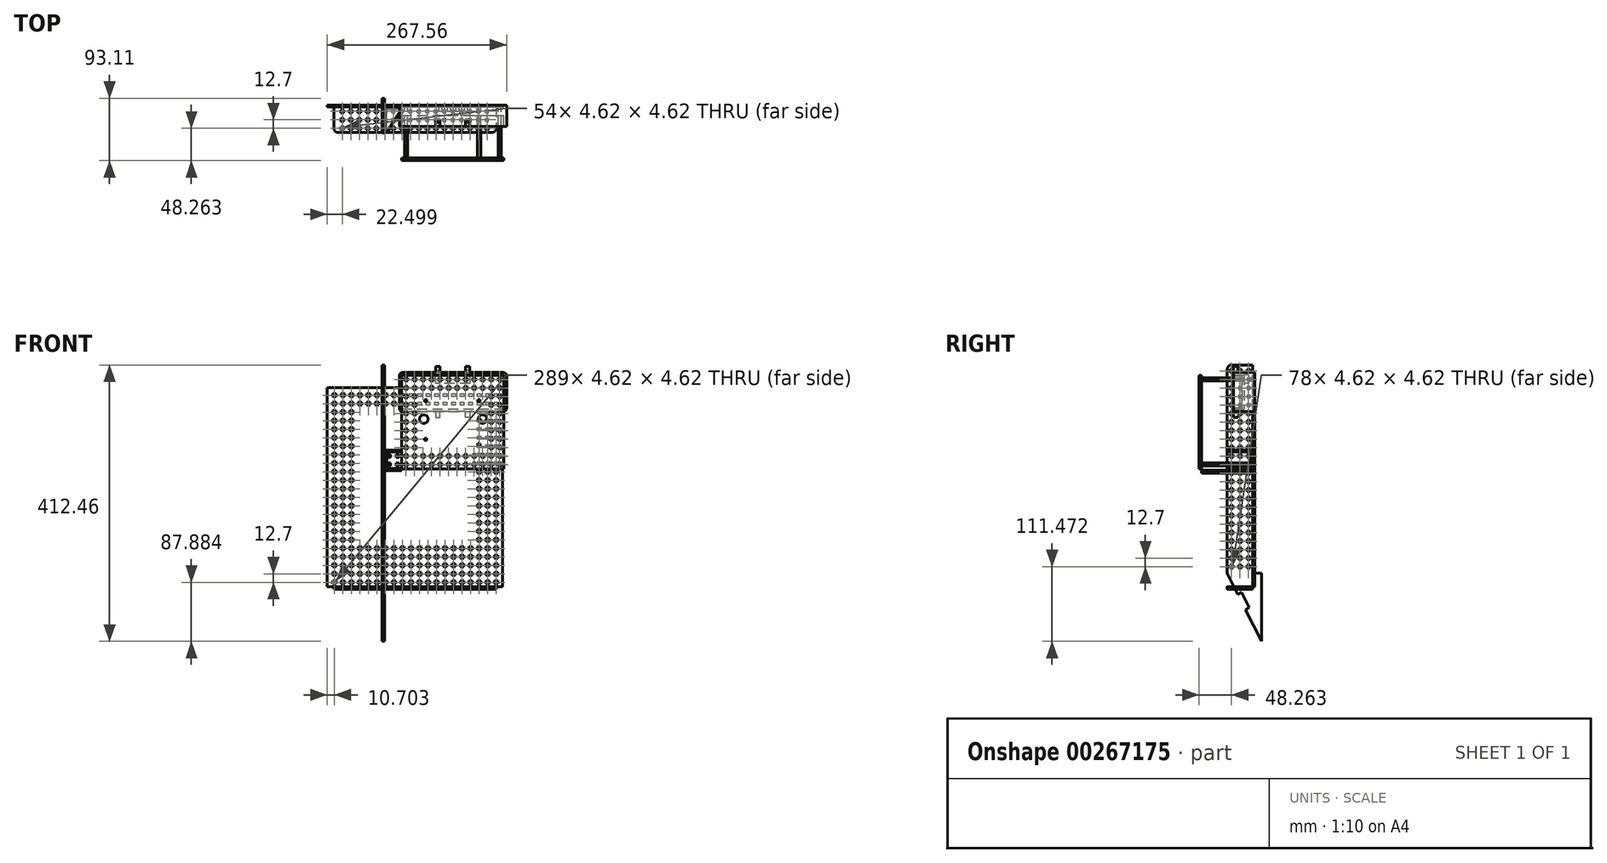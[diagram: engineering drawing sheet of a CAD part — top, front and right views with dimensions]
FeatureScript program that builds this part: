
annotation { "Feature Type Name" : "Feature", "Feature Type Description" : "" }
export const myFeature = defineFeature(function(context is Context, id is Id, definition is map)
    precondition{}
    {
        {
            var Q0;
            Q0=qCreatedBy(makeId("Front.planeOp"),FACE);
            var sketch = newSketch(context, id + "F0", { "sketchPlane" : qUnion([Q0])});
            skLineSegment(sketch, "E0.0.3.0", {"start": v(43.35, 107.94) * mm, "end": v(43.35, 112.57) * mm});
            skLineSegment(sketch, "E0.0.3.1", {"start": v(47.97, 107.94) * mm, "end": v(43.35, 107.94) * mm});
            skLineSegment(sketch, "E0.0.3.2", {"start": v(47.97, 112.57) * mm, "end": v(47.97, 107.94) * mm});
            skLineSegment(sketch, "E0.0.3.3", {"start": v(43.35, 112.57) * mm, "end": v(47.97, 112.57) * mm});
            skLineSegment(sketch, "E0.0.4.0", {"start": v(43.35, 95.24) * mm, "end": v(43.35, 99.87) * mm});
            skLineSegment(sketch, "E0.0.4.1", {"start": v(47.97, 95.24) * mm, "end": v(43.35, 95.24) * mm});
            skLineSegment(sketch, "E0.0.4.2", {"start": v(47.97, 99.87) * mm, "end": v(47.97, 95.24) * mm});
            skLineSegment(sketch, "E0.0.4.3", {"start": v(43.35, 99.87) * mm, "end": v(47.97, 99.87) * mm});
            skLineSegment(sketch, "E0.0.5.0", {"start": v(43.35, 82.54) * mm, "end": v(43.35, 87.17) * mm});
            skLineSegment(sketch, "E0.0.5.1", {"start": v(47.97, 82.54) * mm, "end": v(43.35, 82.54) * mm});
            skLineSegment(sketch, "E0.0.5.2", {"start": v(47.97, 87.17) * mm, "end": v(47.97, 82.54) * mm});
            skLineSegment(sketch, "E0.0.5.3", {"start": v(43.35, 87.17) * mm, "end": v(47.97, 87.17) * mm});
            skLineSegment(sketch, "E0.0.6.0", {"start": v(43.35, 69.84) * mm, "end": v(43.35, 74.47) * mm});
            skLineSegment(sketch, "E0.0.6.1", {"start": v(47.97, 69.84) * mm, "end": v(43.35, 69.84) * mm});
            skLineSegment(sketch, "E0.0.6.2", {"start": v(47.97, 74.47) * mm, "end": v(47.97, 69.84) * mm});
            skLineSegment(sketch, "E0.0.6.3", {"start": v(43.35, 74.47) * mm, "end": v(47.97, 74.47) * mm});
            skLineSegment(sketch, "E0.0.7.0", {"start": v(43.35, 57.14) * mm, "end": v(43.35, 61.77) * mm});
            skLineSegment(sketch, "E0.0.7.1", {"start": v(47.97, 57.14) * mm, "end": v(43.35, 57.14) * mm});
            skLineSegment(sketch, "E0.0.7.2", {"start": v(47.97, 61.77) * mm, "end": v(47.97, 57.14) * mm});
            skLineSegment(sketch, "E0.0.7.3", {"start": v(43.35, 61.77) * mm, "end": v(47.97, 61.77) * mm});
            skLineSegment(sketch, "E0.0.8.0", {"start": v(43.35, 44.44) * mm, "end": v(43.35, 49.07) * mm});
            skLineSegment(sketch, "E0.0.8.1", {"start": v(47.97, 44.44) * mm, "end": v(43.35, 44.44) * mm});
            skLineSegment(sketch, "E0.0.8.2", {"start": v(47.97, 49.07) * mm, "end": v(47.97, 44.44) * mm});
            skLineSegment(sketch, "E0.0.8.3", {"start": v(43.35, 49.07) * mm, "end": v(47.97, 49.07) * mm});
            skLineSegment(sketch, "E0.0.9.0", {"start": v(43.35, 31.74) * mm, "end": v(43.35, 36.37) * mm});
            skLineSegment(sketch, "E0.0.9.1", {"start": v(47.97, 31.74) * mm, "end": v(43.35, 31.74) * mm});
            skLineSegment(sketch, "E0.0.9.2", {"start": v(47.97, 36.37) * mm, "end": v(47.97, 31.74) * mm});
            skLineSegment(sketch, "E0.0.9.3", {"start": v(43.35, 36.37) * mm, "end": v(47.97, 36.37) * mm});
            skLineSegment(sketch, "E0.0.10.0", {"start": v(43.35, 19.04) * mm, "end": v(43.35, 23.67) * mm});
            skLineSegment(sketch, "E0.0.10.1", {"start": v(47.97, 19.04) * mm, "end": v(43.35, 19.04) * mm});
            skLineSegment(sketch, "E0.0.10.2", {"start": v(47.97, 23.67) * mm, "end": v(47.97, 19.04) * mm});
            skLineSegment(sketch, "E0.0.10.3", {"start": v(43.35, 23.67) * mm, "end": v(47.97, 23.67) * mm});
            skLineSegment(sketch, "E0.0.11.0", {"start": v(43.35, 6.34) * mm, "end": v(43.35, 10.97) * mm});
            skLineSegment(sketch, "E0.0.11.1", {"start": v(47.97, 6.34) * mm, "end": v(43.35, 6.34) * mm});
            skLineSegment(sketch, "E0.0.11.2", {"start": v(47.97, 10.97) * mm, "end": v(47.97, 6.34) * mm});
            skLineSegment(sketch, "E0.0.11.3", {"start": v(43.35, 10.97) * mm, "end": v(47.97, 10.97) * mm});
            skLineSegment(sketch, "E0.0.12.0", {"start": v(43.35, -6.36) * mm, "end": v(43.35, -1.73) * mm});
            skLineSegment(sketch, "E0.0.12.1", {"start": v(47.97, -6.36) * mm, "end": v(43.35, -6.36) * mm});
            skLineSegment(sketch, "E0.0.12.2", {"start": v(47.97, -1.73) * mm, "end": v(47.97, -6.36) * mm});
            skLineSegment(sketch, "E0.0.12.3", {"start": v(43.35, -1.73) * mm, "end": v(47.97, -1.73) * mm});
            skLineSegment(sketch, "E0.0.13.0", {"start": v(43.35, -19.06) * mm, "end": v(43.35, -14.43) * mm});
            skLineSegment(sketch, "E0.0.13.1", {"start": v(47.97, -19.06) * mm, "end": v(43.35, -19.06) * mm});
            skLineSegment(sketch, "E0.0.13.2", {"start": v(47.97, -14.43) * mm, "end": v(47.97, -19.06) * mm});
            skLineSegment(sketch, "E0.0.13.3", {"start": v(43.35, -14.43) * mm, "end": v(47.97, -14.43) * mm});
            skLineSegment(sketch, "E0.0.14.0", {"start": v(43.35, -31.76) * mm, "end": v(43.35, -27.13) * mm});
            skLineSegment(sketch, "E0.0.14.1", {"start": v(47.97, -31.76) * mm, "end": v(43.35, -31.76) * mm});
            skLineSegment(sketch, "E0.0.14.2", {"start": v(47.97, -27.13) * mm, "end": v(47.97, -31.76) * mm});
            skLineSegment(sketch, "E0.0.14.3", {"start": v(43.35, -27.13) * mm, "end": v(47.97, -27.13) * mm});
            skLineSegment(sketch, "E0.0.15.0", {"start": v(43.35, -44.46) * mm, "end": v(43.35, -39.83) * mm});
            skLineSegment(sketch, "E0.0.15.1", {"start": v(47.97, -44.46) * mm, "end": v(43.35, -44.46) * mm});
            skLineSegment(sketch, "E0.0.15.2", {"start": v(47.97, -39.83) * mm, "end": v(47.97, -44.46) * mm});
            skLineSegment(sketch, "E0.0.15.3", {"start": v(43.35, -39.83) * mm, "end": v(47.97, -39.83) * mm});
            skLineSegment(sketch, "E0.0.16.0", {"start": v(43.35, -57.16) * mm, "end": v(43.35, -52.53) * mm});
            skLineSegment(sketch, "E0.0.16.1", {"start": v(47.97, -57.16) * mm, "end": v(43.35, -57.16) * mm});
            skLineSegment(sketch, "E0.0.16.2", {"start": v(47.97, -52.53) * mm, "end": v(47.97, -57.16) * mm});
            skLineSegment(sketch, "E0.0.16.3", {"start": v(43.35, -52.53) * mm, "end": v(47.97, -52.53) * mm});
            skLineSegment(sketch, "E0.0.17.0", {"start": v(43.35, -69.86) * mm, "end": v(43.35, -65.23) * mm});
            skLineSegment(sketch, "E0.0.17.1", {"start": v(47.97, -69.86) * mm, "end": v(43.35, -69.86) * mm});
            skLineSegment(sketch, "E0.0.17.2", {"start": v(47.97, -65.23) * mm, "end": v(47.97, -69.86) * mm});
            skLineSegment(sketch, "E0.0.17.3", {"start": v(43.35, -65.23) * mm, "end": v(47.97, -65.23) * mm});
            skLineSegment(sketch, "E0.0.18.0", {"start": v(43.35, -82.56) * mm, "end": v(43.35, -77.93) * mm});
            skLineSegment(sketch, "E0.0.18.1", {"start": v(47.97, -82.56) * mm, "end": v(43.35, -82.56) * mm});
            skLineSegment(sketch, "E0.0.18.2", {"start": v(47.97, -77.93) * mm, "end": v(47.97, -82.56) * mm});
            skLineSegment(sketch, "E0.0.18.3", {"start": v(43.35, -77.93) * mm, "end": v(47.97, -77.93) * mm});
            skLineSegment(sketch, "E0.0.19.0", {"start": v(43.35, -95.26) * mm, "end": v(43.35, -90.63) * mm});
            skLineSegment(sketch, "E0.0.19.1", {"start": v(47.97, -95.26) * mm, "end": v(43.35, -95.26) * mm});
            skLineSegment(sketch, "E0.0.19.2", {"start": v(47.97, -90.63) * mm, "end": v(47.97, -95.26) * mm});
            skLineSegment(sketch, "E0.0.19.3", {"start": v(43.35, -90.63) * mm, "end": v(47.97, -90.63) * mm});
            skLineSegment(sketch, "E0.0.20.0", {"start": v(43.35, -107.96) * mm, "end": v(43.35, -103.33) * mm});
            skLineSegment(sketch, "E0.0.20.1", {"start": v(47.97, -107.96) * mm, "end": v(43.35, -107.96) * mm});
            skLineSegment(sketch, "E0.0.20.2", {"start": v(47.97, -103.33) * mm, "end": v(47.97, -107.96) * mm});
            skLineSegment(sketch, "E0.0.20.3", {"start": v(43.35, -103.33) * mm, "end": v(47.97, -103.33) * mm});
            skLineSegment(sketch, "E0.0.21.0", {"start": v(43.35, -120.66) * mm, "end": v(43.35, -116.03) * mm});
            skLineSegment(sketch, "E0.0.21.1", {"start": v(47.97, -120.66) * mm, "end": v(43.35, -120.66) * mm});
            skLineSegment(sketch, "E0.0.21.2", {"start": v(47.97, -116.03) * mm, "end": v(47.97, -120.66) * mm});
            skLineSegment(sketch, "E0.0.21.3", {"start": v(43.35, -116.03) * mm, "end": v(47.97, -116.03) * mm});
            skLineSegment(sketch, "E0.0.22.0", {"start": v(43.35, -133.36) * mm, "end": v(43.35, -128.73) * mm});
            skLineSegment(sketch, "E0.0.22.1", {"start": v(47.97, -133.36) * mm, "end": v(43.35, -133.36) * mm});
            skLineSegment(sketch, "E0.0.22.2", {"start": v(47.97, -128.73) * mm, "end": v(47.97, -133.36) * mm});
            skLineSegment(sketch, "E0.0.22.3", {"start": v(43.35, -128.73) * mm, "end": v(47.97, -128.73) * mm});
            skLineSegment(sketch, "E0.0.23.0", {"start": v(43.35, -146.06) * mm, "end": v(43.35, -141.43) * mm});
            skLineSegment(sketch, "E0.0.23.1", {"start": v(47.97, -146.06) * mm, "end": v(43.35, -146.06) * mm});
            skLineSegment(sketch, "E0.0.23.2", {"start": v(47.97, -141.43) * mm, "end": v(47.97, -146.06) * mm});
            skLineSegment(sketch, "E0.0.23.3", {"start": v(43.35, -141.43) * mm, "end": v(47.97, -141.43) * mm});
            skLineSegment(sketch, "E0.0.24.0", {"start": v(43.35, -158.76) * mm, "end": v(43.35, -154.13) * mm});
            skLineSegment(sketch, "E0.0.24.1", {"start": v(47.97, -158.76) * mm, "end": v(43.35, -158.76) * mm});
            skLineSegment(sketch, "E0.0.24.2", {"start": v(47.97, -154.13) * mm, "end": v(47.97, -158.76) * mm});
            skLineSegment(sketch, "E0.0.24.3", {"start": v(43.35, -154.13) * mm, "end": v(47.97, -154.13) * mm});
            skLineSegment(sketch, "E0.0.25.0", {"start": v(43.35, -171.46) * mm, "end": v(43.35, -166.83) * mm});
            skLineSegment(sketch, "E0.0.25.1", {"start": v(47.97, -171.46) * mm, "end": v(43.35, -171.46) * mm});
            skLineSegment(sketch, "E0.0.25.2", {"start": v(47.97, -166.83) * mm, "end": v(47.97, -171.46) * mm});
            skLineSegment(sketch, "E0.0.25.3", {"start": v(43.35, -166.83) * mm, "end": v(47.97, -166.83) * mm});
            skLineSegment(sketch, "E0.1.3.0", {"start": v(30.65, 107.94) * mm, "end": v(30.65, 112.57) * mm});
            skLineSegment(sketch, "E0.1.3.1", {"start": v(35.27, 107.94) * mm, "end": v(30.65, 107.94) * mm});
            skLineSegment(sketch, "E0.1.3.2", {"start": v(35.27, 112.57) * mm, "end": v(35.27, 107.94) * mm});
            skLineSegment(sketch, "E0.1.3.3", {"start": v(30.65, 112.57) * mm, "end": v(35.27, 112.57) * mm});
            skLineSegment(sketch, "E0.1.4.0", {"start": v(30.65, 95.24) * mm, "end": v(30.65, 99.87) * mm});
            skLineSegment(sketch, "E0.1.4.1", {"start": v(35.27, 95.24) * mm, "end": v(30.65, 95.24) * mm});
            skLineSegment(sketch, "E0.1.4.2", {"start": v(35.27, 99.87) * mm, "end": v(35.27, 95.24) * mm});
            skLineSegment(sketch, "E0.1.4.3", {"start": v(30.65, 99.87) * mm, "end": v(35.27, 99.87) * mm});
            skLineSegment(sketch, "E0.1.5.0", {"start": v(30.65, 82.54) * mm, "end": v(30.65, 87.17) * mm});
            skLineSegment(sketch, "E0.1.5.1", {"start": v(35.27, 82.54) * mm, "end": v(30.65, 82.54) * mm});
            skLineSegment(sketch, "E0.1.5.2", {"start": v(35.27, 87.17) * mm, "end": v(35.27, 82.54) * mm});
            skLineSegment(sketch, "E0.1.5.3", {"start": v(30.65, 87.17) * mm, "end": v(35.27, 87.17) * mm});
            skLineSegment(sketch, "E0.1.6.0", {"start": v(30.65, 69.84) * mm, "end": v(30.65, 74.47) * mm});
            skLineSegment(sketch, "E0.1.6.1", {"start": v(35.27, 69.84) * mm, "end": v(30.65, 69.84) * mm});
            skLineSegment(sketch, "E0.1.6.2", {"start": v(35.27, 74.47) * mm, "end": v(35.27, 69.84) * mm});
            skLineSegment(sketch, "E0.1.6.3", {"start": v(30.65, 74.47) * mm, "end": v(35.27, 74.47) * mm});
            skLineSegment(sketch, "E0.1.7.0", {"start": v(30.65, 57.14) * mm, "end": v(30.65, 61.77) * mm});
            skLineSegment(sketch, "E0.1.7.1", {"start": v(35.27, 57.14) * mm, "end": v(30.65, 57.14) * mm});
            skLineSegment(sketch, "E0.1.7.2", {"start": v(35.27, 61.77) * mm, "end": v(35.27, 57.14) * mm});
            skLineSegment(sketch, "E0.1.7.3", {"start": v(30.65, 61.77) * mm, "end": v(35.27, 61.77) * mm});
            skLineSegment(sketch, "E0.1.8.0", {"start": v(30.65, 44.44) * mm, "end": v(30.65, 49.07) * mm});
            skLineSegment(sketch, "E0.1.8.1", {"start": v(35.27, 44.44) * mm, "end": v(30.65, 44.44) * mm});
            skLineSegment(sketch, "E0.1.8.2", {"start": v(35.27, 49.07) * mm, "end": v(35.27, 44.44) * mm});
            skLineSegment(sketch, "E0.1.8.3", {"start": v(30.65, 49.07) * mm, "end": v(35.27, 49.07) * mm});
            skLineSegment(sketch, "E0.1.9.0", {"start": v(30.65, 31.74) * mm, "end": v(30.65, 36.37) * mm});
            skLineSegment(sketch, "E0.1.9.1", {"start": v(35.27, 31.74) * mm, "end": v(30.65, 31.74) * mm});
            skLineSegment(sketch, "E0.1.9.2", {"start": v(35.27, 36.37) * mm, "end": v(35.27, 31.74) * mm});
            skLineSegment(sketch, "E0.1.9.3", {"start": v(30.65, 36.37) * mm, "end": v(35.27, 36.37) * mm});
            skLineSegment(sketch, "E0.1.10.0", {"start": v(30.65, 19.04) * mm, "end": v(30.65, 23.67) * mm});
            skLineSegment(sketch, "E0.1.10.1", {"start": v(35.27, 19.04) * mm, "end": v(30.65, 19.04) * mm});
            skLineSegment(sketch, "E0.1.10.2", {"start": v(35.27, 23.67) * mm, "end": v(35.27, 19.04) * mm});
            skLineSegment(sketch, "E0.1.10.3", {"start": v(30.65, 23.67) * mm, "end": v(35.27, 23.67) * mm});
            skLineSegment(sketch, "E0.1.11.0", {"start": v(30.65, 6.34) * mm, "end": v(30.65, 10.97) * mm});
            skLineSegment(sketch, "E0.1.11.1", {"start": v(35.27, 6.34) * mm, "end": v(30.65, 6.34) * mm});
            skLineSegment(sketch, "E0.1.11.2", {"start": v(35.27, 10.97) * mm, "end": v(35.27, 6.34) * mm});
            skLineSegment(sketch, "E0.1.11.3", {"start": v(30.65, 10.97) * mm, "end": v(35.27, 10.97) * mm});
            skLineSegment(sketch, "E0.1.12.0", {"start": v(30.65, -6.36) * mm, "end": v(30.65, -1.73) * mm});
            skLineSegment(sketch, "E0.1.12.1", {"start": v(35.27, -6.36) * mm, "end": v(30.65, -6.36) * mm});
            skLineSegment(sketch, "E0.1.12.2", {"start": v(35.27, -1.73) * mm, "end": v(35.27, -6.36) * mm});
            skLineSegment(sketch, "E0.1.12.3", {"start": v(30.65, -1.73) * mm, "end": v(35.27, -1.73) * mm});
            skLineSegment(sketch, "E0.1.13.0", {"start": v(30.65, -19.06) * mm, "end": v(30.65, -14.43) * mm});
            skLineSegment(sketch, "E0.1.13.1", {"start": v(35.27, -19.06) * mm, "end": v(30.65, -19.06) * mm});
            skLineSegment(sketch, "E0.1.13.2", {"start": v(35.27, -14.43) * mm, "end": v(35.27, -19.06) * mm});
            skLineSegment(sketch, "E0.1.13.3", {"start": v(30.65, -14.43) * mm, "end": v(35.27, -14.43) * mm});
            skLineSegment(sketch, "E0.1.14.0", {"start": v(30.65, -31.76) * mm, "end": v(30.65, -27.13) * mm});
            skLineSegment(sketch, "E0.1.14.1", {"start": v(35.27, -31.76) * mm, "end": v(30.65, -31.76) * mm});
            skLineSegment(sketch, "E0.1.14.2", {"start": v(35.27, -27.13) * mm, "end": v(35.27, -31.76) * mm});
            skLineSegment(sketch, "E0.1.14.3", {"start": v(30.65, -27.13) * mm, "end": v(35.27, -27.13) * mm});
            skLineSegment(sketch, "E0.1.15.0", {"start": v(30.65, -44.46) * mm, "end": v(30.65, -39.83) * mm});
            skLineSegment(sketch, "E0.1.15.1", {"start": v(35.27, -44.46) * mm, "end": v(30.65, -44.46) * mm});
            skLineSegment(sketch, "E0.1.15.2", {"start": v(35.27, -39.83) * mm, "end": v(35.27, -44.46) * mm});
            skLineSegment(sketch, "E0.1.15.3", {"start": v(30.65, -39.83) * mm, "end": v(35.27, -39.83) * mm});
            skLineSegment(sketch, "E0.1.16.0", {"start": v(30.65, -57.16) * mm, "end": v(30.65, -52.53) * mm});
            skLineSegment(sketch, "E0.1.16.1", {"start": v(35.27, -57.16) * mm, "end": v(30.65, -57.16) * mm});
            skLineSegment(sketch, "E0.1.16.2", {"start": v(35.27, -52.53) * mm, "end": v(35.27, -57.16) * mm});
            skLineSegment(sketch, "E0.1.16.3", {"start": v(30.65, -52.53) * mm, "end": v(35.27, -52.53) * mm});
            skLineSegment(sketch, "E0.1.17.0", {"start": v(30.65, -69.86) * mm, "end": v(30.65, -65.23) * mm});
            skLineSegment(sketch, "E0.1.17.1", {"start": v(35.27, -69.86) * mm, "end": v(30.65, -69.86) * mm});
            skLineSegment(sketch, "E0.1.17.2", {"start": v(35.27, -65.23) * mm, "end": v(35.27, -69.86) * mm});
            skLineSegment(sketch, "E0.1.17.3", {"start": v(30.65, -65.23) * mm, "end": v(35.27, -65.23) * mm});
            skLineSegment(sketch, "E0.1.18.0", {"start": v(30.65, -82.56) * mm, "end": v(30.65, -77.93) * mm});
            skLineSegment(sketch, "E0.1.18.1", {"start": v(35.27, -82.56) * mm, "end": v(30.65, -82.56) * mm});
            skLineSegment(sketch, "E0.1.18.2", {"start": v(35.27, -77.93) * mm, "end": v(35.27, -82.56) * mm});
            skLineSegment(sketch, "E0.1.18.3", {"start": v(30.65, -77.93) * mm, "end": v(35.27, -77.93) * mm});
            skLineSegment(sketch, "E0.1.19.0", {"start": v(30.65, -95.26) * mm, "end": v(30.65, -90.63) * mm});
            skLineSegment(sketch, "E0.1.19.1", {"start": v(35.27, -95.26) * mm, "end": v(30.65, -95.26) * mm});
            skLineSegment(sketch, "E0.1.19.2", {"start": v(35.27, -90.63) * mm, "end": v(35.27, -95.26) * mm});
            skLineSegment(sketch, "E0.1.19.3", {"start": v(30.65, -90.63) * mm, "end": v(35.27, -90.63) * mm});
            skLineSegment(sketch, "E0.1.20.0", {"start": v(30.65, -107.96) * mm, "end": v(30.65, -103.33) * mm});
            skLineSegment(sketch, "E0.1.20.1", {"start": v(35.27, -107.96) * mm, "end": v(30.65, -107.96) * mm});
            skLineSegment(sketch, "E0.1.20.2", {"start": v(35.27, -103.33) * mm, "end": v(35.27, -107.96) * mm});
            skLineSegment(sketch, "E0.1.20.3", {"start": v(30.65, -103.33) * mm, "end": v(35.27, -103.33) * mm});
            skLineSegment(sketch, "E0.1.21.0", {"start": v(30.65, -120.66) * mm, "end": v(30.65, -116.03) * mm});
            skLineSegment(sketch, "E0.1.21.1", {"start": v(35.27, -120.66) * mm, "end": v(30.65, -120.66) * mm});
            skLineSegment(sketch, "E0.1.21.2", {"start": v(35.27, -116.03) * mm, "end": v(35.27, -120.66) * mm});
            skLineSegment(sketch, "E0.1.21.3", {"start": v(30.65, -116.03) * mm, "end": v(35.27, -116.03) * mm});
            skLineSegment(sketch, "E0.1.22.0", {"start": v(30.65, -133.36) * mm, "end": v(30.65, -128.73) * mm});
            skLineSegment(sketch, "E0.1.22.1", {"start": v(35.27, -133.36) * mm, "end": v(30.65, -133.36) * mm});
            skLineSegment(sketch, "E0.1.22.2", {"start": v(35.27, -128.73) * mm, "end": v(35.27, -133.36) * mm});
            skLineSegment(sketch, "E0.1.22.3", {"start": v(30.65, -128.73) * mm, "end": v(35.27, -128.73) * mm});
            skLineSegment(sketch, "E0.1.23.0", {"start": v(30.65, -146.06) * mm, "end": v(30.65, -141.43) * mm});
            skLineSegment(sketch, "E0.1.23.1", {"start": v(35.27, -146.06) * mm, "end": v(30.65, -146.06) * mm});
            skLineSegment(sketch, "E0.1.23.2", {"start": v(35.27, -141.43) * mm, "end": v(35.27, -146.06) * mm});
            skLineSegment(sketch, "E0.1.23.3", {"start": v(30.65, -141.43) * mm, "end": v(35.27, -141.43) * mm});
            skLineSegment(sketch, "E0.1.24.0", {"start": v(30.65, -158.76) * mm, "end": v(30.65, -154.13) * mm});
            skLineSegment(sketch, "E0.1.24.1", {"start": v(35.27, -158.76) * mm, "end": v(30.65, -158.76) * mm});
            skLineSegment(sketch, "E0.1.24.2", {"start": v(35.27, -154.13) * mm, "end": v(35.27, -158.76) * mm});
            skLineSegment(sketch, "E0.1.24.3", {"start": v(30.65, -154.13) * mm, "end": v(35.27, -154.13) * mm});
            skLineSegment(sketch, "E0.1.25.0", {"start": v(30.65, -171.46) * mm, "end": v(30.65, -166.83) * mm});
            skLineSegment(sketch, "E0.1.25.1", {"start": v(35.27, -171.46) * mm, "end": v(30.65, -171.46) * mm});
            skLineSegment(sketch, "E0.1.25.2", {"start": v(35.27, -166.83) * mm, "end": v(35.27, -171.46) * mm});
            skLineSegment(sketch, "E0.1.25.3", {"start": v(30.65, -166.83) * mm, "end": v(35.27, -166.83) * mm});
            skLineSegment(sketch, "E0.2.3.0", {"start": v(17.95, 107.94) * mm, "end": v(17.95, 112.57) * mm});
            skLineSegment(sketch, "E0.2.3.1", {"start": v(22.57, 107.94) * mm, "end": v(17.95, 107.94) * mm});
            skLineSegment(sketch, "E0.2.3.2", {"start": v(22.57, 112.57) * mm, "end": v(22.57, 107.94) * mm});
            skLineSegment(sketch, "E0.2.3.3", {"start": v(17.95, 112.57) * mm, "end": v(22.57, 112.57) * mm});
            skLineSegment(sketch, "E0.2.4.0", {"start": v(17.95, 95.24) * mm, "end": v(17.95, 99.87) * mm});
            skLineSegment(sketch, "E0.2.4.1", {"start": v(22.57, 95.24) * mm, "end": v(17.95, 95.24) * mm});
            skLineSegment(sketch, "E0.2.4.2", {"start": v(22.57, 99.87) * mm, "end": v(22.57, 95.24) * mm});
            skLineSegment(sketch, "E0.2.4.3", {"start": v(17.95, 99.87) * mm, "end": v(22.57, 99.87) * mm});
            skLineSegment(sketch, "E0.2.5.0", {"start": v(17.95, 82.54) * mm, "end": v(17.95, 87.17) * mm});
            skLineSegment(sketch, "E0.2.5.1", {"start": v(22.57, 82.54) * mm, "end": v(17.95, 82.54) * mm});
            skLineSegment(sketch, "E0.2.5.2", {"start": v(22.57, 87.17) * mm, "end": v(22.57, 82.54) * mm});
            skLineSegment(sketch, "E0.2.5.3", {"start": v(17.95, 87.17) * mm, "end": v(22.57, 87.17) * mm});
            skLineSegment(sketch, "E0.2.6.0", {"start": v(17.95, 69.84) * mm, "end": v(17.95, 74.47) * mm});
            skLineSegment(sketch, "E0.2.6.1", {"start": v(22.57, 69.84) * mm, "end": v(17.95, 69.84) * mm});
            skLineSegment(sketch, "E0.2.6.2", {"start": v(22.57, 74.47) * mm, "end": v(22.57, 69.84) * mm});
            skLineSegment(sketch, "E0.2.6.3", {"start": v(17.95, 74.47) * mm, "end": v(22.57, 74.47) * mm});
            skLineSegment(sketch, "E0.2.7.0", {"start": v(17.95, 57.14) * mm, "end": v(17.95, 61.77) * mm});
            skLineSegment(sketch, "E0.2.7.1", {"start": v(22.57, 57.14) * mm, "end": v(17.95, 57.14) * mm});
            skLineSegment(sketch, "E0.2.7.2", {"start": v(22.57, 61.77) * mm, "end": v(22.57, 57.14) * mm});
            skLineSegment(sketch, "E0.2.7.3", {"start": v(17.95, 61.77) * mm, "end": v(22.57, 61.77) * mm});
            skLineSegment(sketch, "E0.2.8.0", {"start": v(17.95, 44.44) * mm, "end": v(17.95, 49.07) * mm});
            skLineSegment(sketch, "E0.2.8.1", {"start": v(22.57, 44.44) * mm, "end": v(17.95, 44.44) * mm});
            skLineSegment(sketch, "E0.2.8.2", {"start": v(22.57, 49.07) * mm, "end": v(22.57, 44.44) * mm});
            skLineSegment(sketch, "E0.2.8.3", {"start": v(17.95, 49.07) * mm, "end": v(22.57, 49.07) * mm});
            skLineSegment(sketch, "E0.2.9.0", {"start": v(17.95, 31.74) * mm, "end": v(17.95, 36.37) * mm});
            skLineSegment(sketch, "E0.2.9.1", {"start": v(22.57, 31.74) * mm, "end": v(17.95, 31.74) * mm});
            skLineSegment(sketch, "E0.2.9.2", {"start": v(22.57, 36.37) * mm, "end": v(22.57, 31.74) * mm});
            skLineSegment(sketch, "E0.2.9.3", {"start": v(17.95, 36.37) * mm, "end": v(22.57, 36.37) * mm});
            skLineSegment(sketch, "E0.2.10.0", {"start": v(17.95, 19.04) * mm, "end": v(17.95, 23.67) * mm});
            skLineSegment(sketch, "E0.2.10.1", {"start": v(22.57, 19.04) * mm, "end": v(17.95, 19.04) * mm});
            skLineSegment(sketch, "E0.2.10.2", {"start": v(22.57, 23.67) * mm, "end": v(22.57, 19.04) * mm});
            skLineSegment(sketch, "E0.2.10.3", {"start": v(17.95, 23.67) * mm, "end": v(22.57, 23.67) * mm});
            skLineSegment(sketch, "E0.2.11.0", {"start": v(17.95, 6.34) * mm, "end": v(17.95, 10.97) * mm});
            skLineSegment(sketch, "E0.2.11.1", {"start": v(22.57, 6.34) * mm, "end": v(17.95, 6.34) * mm});
            skLineSegment(sketch, "E0.2.11.2", {"start": v(22.57, 10.97) * mm, "end": v(22.57, 6.34) * mm});
            skLineSegment(sketch, "E0.2.11.3", {"start": v(17.95, 10.97) * mm, "end": v(22.57, 10.97) * mm});
            skLineSegment(sketch, "E0.2.12.0", {"start": v(17.95, -6.36) * mm, "end": v(17.95, -1.73) * mm});
            skLineSegment(sketch, "E0.2.12.1", {"start": v(22.57, -6.36) * mm, "end": v(17.95, -6.36) * mm});
            skLineSegment(sketch, "E0.2.12.2", {"start": v(22.57, -1.73) * mm, "end": v(22.57, -6.36) * mm});
            skLineSegment(sketch, "E0.2.12.3", {"start": v(17.95, -1.73) * mm, "end": v(22.57, -1.73) * mm});
            skLineSegment(sketch, "E0.2.13.0", {"start": v(17.95, -19.06) * mm, "end": v(17.95, -14.43) * mm});
            skLineSegment(sketch, "E0.2.13.1", {"start": v(22.57, -19.06) * mm, "end": v(17.95, -19.06) * mm});
            skLineSegment(sketch, "E0.2.13.2", {"start": v(22.57, -14.43) * mm, "end": v(22.57, -19.06) * mm});
            skLineSegment(sketch, "E0.2.13.3", {"start": v(17.95, -14.43) * mm, "end": v(22.57, -14.43) * mm});
            skLineSegment(sketch, "E0.2.14.0", {"start": v(17.95, -31.76) * mm, "end": v(17.95, -27.13) * mm});
            skLineSegment(sketch, "E0.2.14.1", {"start": v(22.57, -31.76) * mm, "end": v(17.95, -31.76) * mm});
            skLineSegment(sketch, "E0.2.14.2", {"start": v(22.57, -27.13) * mm, "end": v(22.57, -31.76) * mm});
            skLineSegment(sketch, "E0.2.14.3", {"start": v(17.95, -27.13) * mm, "end": v(22.57, -27.13) * mm});
            skLineSegment(sketch, "E0.2.15.0", {"start": v(17.95, -44.46) * mm, "end": v(17.95, -39.83) * mm});
            skLineSegment(sketch, "E0.2.15.1", {"start": v(22.57, -44.46) * mm, "end": v(17.95, -44.46) * mm});
            skLineSegment(sketch, "E0.2.15.2", {"start": v(22.57, -39.83) * mm, "end": v(22.57, -44.46) * mm});
            skLineSegment(sketch, "E0.2.15.3", {"start": v(17.95, -39.83) * mm, "end": v(22.57, -39.83) * mm});
            skLineSegment(sketch, "E0.2.16.0", {"start": v(17.95, -57.16) * mm, "end": v(17.95, -52.53) * mm});
            skLineSegment(sketch, "E0.2.16.1", {"start": v(22.57, -57.16) * mm, "end": v(17.95, -57.16) * mm});
            skLineSegment(sketch, "E0.2.16.2", {"start": v(22.57, -52.53) * mm, "end": v(22.57, -57.16) * mm});
            skLineSegment(sketch, "E0.2.16.3", {"start": v(17.95, -52.53) * mm, "end": v(22.57, -52.53) * mm});
            skLineSegment(sketch, "E0.2.17.0", {"start": v(17.95, -69.86) * mm, "end": v(17.95, -65.23) * mm});
            skLineSegment(sketch, "E0.2.17.1", {"start": v(22.57, -69.86) * mm, "end": v(17.95, -69.86) * mm});
            skLineSegment(sketch, "E0.2.17.2", {"start": v(22.57, -65.23) * mm, "end": v(22.57, -69.86) * mm});
            skLineSegment(sketch, "E0.2.17.3", {"start": v(17.95, -65.23) * mm, "end": v(22.57, -65.23) * mm});
            skLineSegment(sketch, "E0.2.18.0", {"start": v(17.95, -82.56) * mm, "end": v(17.95, -77.93) * mm});
            skLineSegment(sketch, "E0.2.18.1", {"start": v(22.57, -82.56) * mm, "end": v(17.95, -82.56) * mm});
            skLineSegment(sketch, "E0.2.18.2", {"start": v(22.57, -77.93) * mm, "end": v(22.57, -82.56) * mm});
            skLineSegment(sketch, "E0.2.18.3", {"start": v(17.95, -77.93) * mm, "end": v(22.57, -77.93) * mm});
            skLineSegment(sketch, "E0.2.19.0", {"start": v(17.95, -95.26) * mm, "end": v(17.95, -90.63) * mm});
            skLineSegment(sketch, "E0.2.19.1", {"start": v(22.57, -95.26) * mm, "end": v(17.95, -95.26) * mm});
            skLineSegment(sketch, "E0.2.19.2", {"start": v(22.57, -90.63) * mm, "end": v(22.57, -95.26) * mm});
            skLineSegment(sketch, "E0.2.19.3", {"start": v(17.95, -90.63) * mm, "end": v(22.57, -90.63) * mm});
            skLineSegment(sketch, "E0.2.20.0", {"start": v(17.95, -107.96) * mm, "end": v(17.95, -103.33) * mm});
            skLineSegment(sketch, "E0.2.20.1", {"start": v(22.57, -107.96) * mm, "end": v(17.95, -107.96) * mm});
            skLineSegment(sketch, "E0.2.20.2", {"start": v(22.57, -103.33) * mm, "end": v(22.57, -107.96) * mm});
            skLineSegment(sketch, "E0.2.20.3", {"start": v(17.95, -103.33) * mm, "end": v(22.57, -103.33) * mm});
            skLineSegment(sketch, "E0.2.21.0", {"start": v(17.95, -120.66) * mm, "end": v(17.95, -116.03) * mm});
            skLineSegment(sketch, "E0.2.21.1", {"start": v(22.57, -120.66) * mm, "end": v(17.95, -120.66) * mm});
            skLineSegment(sketch, "E0.2.21.2", {"start": v(22.57, -116.03) * mm, "end": v(22.57, -120.66) * mm});
            skLineSegment(sketch, "E0.2.21.3", {"start": v(17.95, -116.03) * mm, "end": v(22.57, -116.03) * mm});
            skLineSegment(sketch, "E0.2.22.0", {"start": v(17.95, -133.36) * mm, "end": v(17.95, -128.73) * mm});
            skLineSegment(sketch, "E0.2.22.1", {"start": v(22.57, -133.36) * mm, "end": v(17.95, -133.36) * mm});
            skLineSegment(sketch, "E0.2.22.2", {"start": v(22.57, -128.73) * mm, "end": v(22.57, -133.36) * mm});
            skLineSegment(sketch, "E0.2.22.3", {"start": v(17.95, -128.73) * mm, "end": v(22.57, -128.73) * mm});
            skLineSegment(sketch, "E0.2.23.0", {"start": v(17.95, -146.06) * mm, "end": v(17.95, -141.43) * mm});
            skLineSegment(sketch, "E0.2.23.1", {"start": v(22.57, -146.06) * mm, "end": v(17.95, -146.06) * mm});
            skLineSegment(sketch, "E0.2.23.2", {"start": v(22.57, -141.43) * mm, "end": v(22.57, -146.06) * mm});
            skLineSegment(sketch, "E0.2.23.3", {"start": v(17.95, -141.43) * mm, "end": v(22.57, -141.43) * mm});
            skLineSegment(sketch, "E0.2.24.0", {"start": v(17.95, -158.76) * mm, "end": v(17.95, -154.13) * mm});
            skLineSegment(sketch, "E0.2.24.1", {"start": v(22.57, -158.76) * mm, "end": v(17.95, -158.76) * mm});
            skLineSegment(sketch, "E0.2.24.2", {"start": v(22.57, -154.13) * mm, "end": v(22.57, -158.76) * mm});
            skLineSegment(sketch, "E0.2.24.3", {"start": v(17.95, -154.13) * mm, "end": v(22.57, -154.13) * mm});
            skLineSegment(sketch, "E0.2.25.0", {"start": v(17.95, -171.46) * mm, "end": v(17.95, -166.83) * mm});
            skLineSegment(sketch, "E0.2.25.1", {"start": v(22.57, -171.46) * mm, "end": v(17.95, -171.46) * mm});
            skLineSegment(sketch, "E0.2.25.2", {"start": v(22.57, -166.83) * mm, "end": v(22.57, -171.46) * mm});
            skLineSegment(sketch, "E0.2.25.3", {"start": v(17.95, -166.83) * mm, "end": v(22.57, -166.83) * mm});
            skLineSegment(sketch, "E1", {"start": v(-196.31, -175.5) * mm, "end": v(45.66, -175.5) * mm});
            skLineSegment(sketch, "E2.0.1.0", {"start": v(-167.93, 112.57) * mm, "end": v(-167.93, 107.94) * mm});
            skLineSegment(sketch, "E2.0.1.1", {"start": v(-172.55, 112.57) * mm, "end": v(-167.93, 112.57) * mm});
            skLineSegment(sketch, "E2.0.1.2", {"start": v(-172.55, 107.94) * mm, "end": v(-172.55, 112.57) * mm});
            skLineSegment(sketch, "E2.0.1.3", {"start": v(-167.93, 107.94) * mm, "end": v(-172.55, 107.94) * mm});
            skLineSegment(sketch, "E2.0.1.4", {"start": v(-180.63, 112.57) * mm, "end": v(-180.63, 107.94) * mm});
            skLineSegment(sketch, "E2.0.1.5", {"start": v(-185.25, 112.57) * mm, "end": v(-180.63, 112.57) * mm});
            skLineSegment(sketch, "E2.0.1.6", {"start": v(-180.63, 107.94) * mm, "end": v(-185.25, 107.94) * mm});
            skLineSegment(sketch, "E2.0.1.7", {"start": v(-185.25, 107.94) * mm, "end": v(-185.25, 112.57) * mm});
            skLineSegment(sketch, "E2.0.1.8", {"start": v(-193.33, 112.57) * mm, "end": v(-193.33, 107.94) * mm});
            skLineSegment(sketch, "E2.0.1.9", {"start": v(-197.95, 112.57) * mm, "end": v(-193.33, 112.57) * mm});
            skLineSegment(sketch, "E2.0.1.10", {"start": v(-197.95, 107.94) * mm, "end": v(-197.95, 112.57) * mm});
            skLineSegment(sketch, "E2.0.1.11", {"start": v(-193.33, 107.94) * mm, "end": v(-197.95, 107.94) * mm});
            skLineSegment(sketch, "E2.0.2.0", {"start": v(-167.93, 99.87) * mm, "end": v(-167.93, 95.24) * mm});
            skLineSegment(sketch, "E2.0.2.1", {"start": v(-172.55, 99.87) * mm, "end": v(-167.93, 99.87) * mm});
            skLineSegment(sketch, "E2.0.2.2", {"start": v(-172.55, 95.24) * mm, "end": v(-172.55, 99.87) * mm});
            skLineSegment(sketch, "E2.0.2.3", {"start": v(-167.93, 95.24) * mm, "end": v(-172.55, 95.24) * mm});
            skLineSegment(sketch, "E2.0.2.4", {"start": v(-180.63, 99.87) * mm, "end": v(-180.63, 95.24) * mm});
            skLineSegment(sketch, "E2.0.2.5", {"start": v(-185.25, 99.87) * mm, "end": v(-180.63, 99.87) * mm});
            skLineSegment(sketch, "E2.0.2.6", {"start": v(-180.63, 95.24) * mm, "end": v(-185.25, 95.24) * mm});
            skLineSegment(sketch, "E2.0.2.7", {"start": v(-185.25, 95.24) * mm, "end": v(-185.25, 99.87) * mm});
            skLineSegment(sketch, "E2.0.2.8", {"start": v(-193.33, 99.87) * mm, "end": v(-193.33, 95.24) * mm});
            skLineSegment(sketch, "E2.0.2.9", {"start": v(-197.95, 99.87) * mm, "end": v(-193.33, 99.87) * mm});
            skLineSegment(sketch, "E2.0.2.10", {"start": v(-197.95, 95.24) * mm, "end": v(-197.95, 99.87) * mm});
            skLineSegment(sketch, "E2.0.2.11", {"start": v(-193.33, 95.24) * mm, "end": v(-197.95, 95.24) * mm});
            skLineSegment(sketch, "E2.0.3.0", {"start": v(-167.93, 87.17) * mm, "end": v(-167.93, 82.54) * mm});
            skLineSegment(sketch, "E2.0.3.1", {"start": v(-172.55, 87.17) * mm, "end": v(-167.93, 87.17) * mm});
            skLineSegment(sketch, "E2.0.3.2", {"start": v(-172.55, 82.54) * mm, "end": v(-172.55, 87.17) * mm});
            skLineSegment(sketch, "E2.0.3.3", {"start": v(-167.93, 82.54) * mm, "end": v(-172.55, 82.54) * mm});
            skLineSegment(sketch, "E2.0.3.4", {"start": v(-180.63, 87.17) * mm, "end": v(-180.63, 82.54) * mm});
            skLineSegment(sketch, "E2.0.3.5", {"start": v(-185.25, 87.17) * mm, "end": v(-180.63, 87.17) * mm});
            skLineSegment(sketch, "E2.0.3.6", {"start": v(-180.63, 82.54) * mm, "end": v(-185.25, 82.54) * mm});
            skLineSegment(sketch, "E2.0.3.7", {"start": v(-185.25, 82.54) * mm, "end": v(-185.25, 87.17) * mm});
            skLineSegment(sketch, "E2.0.3.8", {"start": v(-193.33, 87.17) * mm, "end": v(-193.33, 82.54) * mm});
            skLineSegment(sketch, "E2.0.3.9", {"start": v(-197.95, 87.17) * mm, "end": v(-193.33, 87.17) * mm});
            skLineSegment(sketch, "E2.0.3.10", {"start": v(-197.95, 82.54) * mm, "end": v(-197.95, 87.17) * mm});
            skLineSegment(sketch, "E2.0.3.11", {"start": v(-193.33, 82.54) * mm, "end": v(-197.95, 82.54) * mm});
            skLineSegment(sketch, "E2.0.4.0", {"start": v(-167.93, 74.47) * mm, "end": v(-167.93, 69.84) * mm});
            skLineSegment(sketch, "E2.0.4.1", {"start": v(-172.55, 74.47) * mm, "end": v(-167.93, 74.47) * mm});
            skLineSegment(sketch, "E2.0.4.2", {"start": v(-172.55, 69.84) * mm, "end": v(-172.55, 74.47) * mm});
            skLineSegment(sketch, "E2.0.4.3", {"start": v(-167.93, 69.84) * mm, "end": v(-172.55, 69.84) * mm});
            skLineSegment(sketch, "E2.0.4.4", {"start": v(-180.63, 74.47) * mm, "end": v(-180.63, 69.84) * mm});
            skLineSegment(sketch, "E2.0.4.5", {"start": v(-185.25, 74.47) * mm, "end": v(-180.63, 74.47) * mm});
            skLineSegment(sketch, "E2.0.4.6", {"start": v(-180.63, 69.84) * mm, "end": v(-185.25, 69.84) * mm});
            skLineSegment(sketch, "E2.0.4.7", {"start": v(-185.25, 69.84) * mm, "end": v(-185.25, 74.47) * mm});
            skLineSegment(sketch, "E2.0.4.8", {"start": v(-193.33, 74.47) * mm, "end": v(-193.33, 69.84) * mm});
            skLineSegment(sketch, "E2.0.4.9", {"start": v(-197.95, 74.47) * mm, "end": v(-193.33, 74.47) * mm});
            skLineSegment(sketch, "E2.0.4.10", {"start": v(-197.95, 69.84) * mm, "end": v(-197.95, 74.47) * mm});
            skLineSegment(sketch, "E2.0.4.11", {"start": v(-193.33, 69.84) * mm, "end": v(-197.95, 69.84) * mm});
            skLineSegment(sketch, "E2.0.5.0", {"start": v(-167.93, 61.77) * mm, "end": v(-167.93, 57.14) * mm});
            skLineSegment(sketch, "E2.0.5.1", {"start": v(-172.55, 61.77) * mm, "end": v(-167.93, 61.77) * mm});
            skLineSegment(sketch, "E2.0.5.2", {"start": v(-172.55, 57.14) * mm, "end": v(-172.55, 61.77) * mm});
            skLineSegment(sketch, "E2.0.5.3", {"start": v(-167.93, 57.14) * mm, "end": v(-172.55, 57.14) * mm});
            skLineSegment(sketch, "E2.0.5.4", {"start": v(-180.63, 61.77) * mm, "end": v(-180.63, 57.14) * mm});
            skLineSegment(sketch, "E2.0.5.5", {"start": v(-185.25, 61.77) * mm, "end": v(-180.63, 61.77) * mm});
            skLineSegment(sketch, "E2.0.5.6", {"start": v(-180.63, 57.14) * mm, "end": v(-185.25, 57.14) * mm});
            skLineSegment(sketch, "E2.0.5.7", {"start": v(-185.25, 57.14) * mm, "end": v(-185.25, 61.77) * mm});
            skLineSegment(sketch, "E2.0.5.8", {"start": v(-193.33, 61.77) * mm, "end": v(-193.33, 57.14) * mm});
            skLineSegment(sketch, "E2.0.5.9", {"start": v(-197.95, 61.77) * mm, "end": v(-193.33, 61.77) * mm});
            skLineSegment(sketch, "E2.0.5.10", {"start": v(-197.95, 57.14) * mm, "end": v(-197.95, 61.77) * mm});
            skLineSegment(sketch, "E2.0.5.11", {"start": v(-193.33, 57.14) * mm, "end": v(-197.95, 57.14) * mm});
            skLineSegment(sketch, "E2.0.6.0", {"start": v(-167.93, 49.07) * mm, "end": v(-167.93, 44.44) * mm});
            skLineSegment(sketch, "E2.0.6.1", {"start": v(-172.55, 49.07) * mm, "end": v(-167.93, 49.07) * mm});
            skLineSegment(sketch, "E2.0.6.2", {"start": v(-172.55, 44.44) * mm, "end": v(-172.55, 49.07) * mm});
            skLineSegment(sketch, "E2.0.6.3", {"start": v(-167.93, 44.44) * mm, "end": v(-172.55, 44.44) * mm});
            skLineSegment(sketch, "E2.0.6.4", {"start": v(-180.63, 49.07) * mm, "end": v(-180.63, 44.44) * mm});
            skLineSegment(sketch, "E2.0.6.5", {"start": v(-185.25, 49.07) * mm, "end": v(-180.63, 49.07) * mm});
            skLineSegment(sketch, "E2.0.6.6", {"start": v(-180.63, 44.44) * mm, "end": v(-185.25, 44.44) * mm});
            skLineSegment(sketch, "E2.0.6.7", {"start": v(-185.25, 44.44) * mm, "end": v(-185.25, 49.07) * mm});
            skLineSegment(sketch, "E2.0.6.8", {"start": v(-193.33, 49.07) * mm, "end": v(-193.33, 44.44) * mm});
            skLineSegment(sketch, "E2.0.6.9", {"start": v(-197.95, 49.07) * mm, "end": v(-193.33, 49.07) * mm});
            skLineSegment(sketch, "E2.0.6.10", {"start": v(-197.95, 44.44) * mm, "end": v(-197.95, 49.07) * mm});
            skLineSegment(sketch, "E2.0.6.11", {"start": v(-193.33, 44.44) * mm, "end": v(-197.95, 44.44) * mm});
            skLineSegment(sketch, "E2.0.7.0", {"start": v(-167.93, 36.37) * mm, "end": v(-167.93, 31.74) * mm});
            skLineSegment(sketch, "E2.0.7.1", {"start": v(-172.55, 36.37) * mm, "end": v(-167.93, 36.37) * mm});
            skLineSegment(sketch, "E2.0.7.2", {"start": v(-172.55, 31.74) * mm, "end": v(-172.55, 36.37) * mm});
            skLineSegment(sketch, "E2.0.7.3", {"start": v(-167.93, 31.74) * mm, "end": v(-172.55, 31.74) * mm});
            skLineSegment(sketch, "E2.0.7.4", {"start": v(-180.63, 36.37) * mm, "end": v(-180.63, 31.74) * mm});
            skLineSegment(sketch, "E2.0.7.5", {"start": v(-185.25, 36.37) * mm, "end": v(-180.63, 36.37) * mm});
            skLineSegment(sketch, "E2.0.7.6", {"start": v(-180.63, 31.74) * mm, "end": v(-185.25, 31.74) * mm});
            skLineSegment(sketch, "E2.0.7.7", {"start": v(-185.25, 31.74) * mm, "end": v(-185.25, 36.37) * mm});
            skLineSegment(sketch, "E2.0.7.8", {"start": v(-193.33, 36.37) * mm, "end": v(-193.33, 31.74) * mm});
            skLineSegment(sketch, "E2.0.7.9", {"start": v(-197.95, 36.37) * mm, "end": v(-193.33, 36.37) * mm});
            skLineSegment(sketch, "E2.0.7.10", {"start": v(-197.95, 31.74) * mm, "end": v(-197.95, 36.37) * mm});
            skLineSegment(sketch, "E2.0.7.11", {"start": v(-193.33, 31.74) * mm, "end": v(-197.95, 31.74) * mm});
            skLineSegment(sketch, "E2.0.8.0", {"start": v(-167.93, 23.67) * mm, "end": v(-167.93, 19.04) * mm});
            skLineSegment(sketch, "E2.0.8.1", {"start": v(-172.55, 23.67) * mm, "end": v(-167.93, 23.67) * mm});
            skLineSegment(sketch, "E2.0.8.2", {"start": v(-172.55, 19.04) * mm, "end": v(-172.55, 23.67) * mm});
            skLineSegment(sketch, "E2.0.8.3", {"start": v(-167.93, 19.04) * mm, "end": v(-172.55, 19.04) * mm});
            skLineSegment(sketch, "E2.0.8.4", {"start": v(-180.63, 23.67) * mm, "end": v(-180.63, 19.04) * mm});
            skLineSegment(sketch, "E2.0.8.5", {"start": v(-185.25, 23.67) * mm, "end": v(-180.63, 23.67) * mm});
            skLineSegment(sketch, "E2.0.8.6", {"start": v(-180.63, 19.04) * mm, "end": v(-185.25, 19.04) * mm});
            skLineSegment(sketch, "E2.0.8.7", {"start": v(-185.25, 19.04) * mm, "end": v(-185.25, 23.67) * mm});
            skLineSegment(sketch, "E2.0.8.8", {"start": v(-193.33, 23.67) * mm, "end": v(-193.33, 19.04) * mm});
            skLineSegment(sketch, "E2.0.8.9", {"start": v(-197.95, 23.67) * mm, "end": v(-193.33, 23.67) * mm});
            skLineSegment(sketch, "E2.0.8.10", {"start": v(-197.95, 19.04) * mm, "end": v(-197.95, 23.67) * mm});
            skLineSegment(sketch, "E2.0.8.11", {"start": v(-193.33, 19.04) * mm, "end": v(-197.95, 19.04) * mm});
            skLineSegment(sketch, "E2.0.9.0", {"start": v(-167.93, 10.97) * mm, "end": v(-167.93, 6.34) * mm});
            skLineSegment(sketch, "E2.0.9.1", {"start": v(-172.55, 10.97) * mm, "end": v(-167.93, 10.97) * mm});
            skLineSegment(sketch, "E2.0.9.2", {"start": v(-172.55, 6.34) * mm, "end": v(-172.55, 10.97) * mm});
            skLineSegment(sketch, "E2.0.9.3", {"start": v(-167.93, 6.34) * mm, "end": v(-172.55, 6.34) * mm});
            skLineSegment(sketch, "E2.0.9.4", {"start": v(-180.63, 10.97) * mm, "end": v(-180.63, 6.34) * mm});
            skLineSegment(sketch, "E2.0.9.5", {"start": v(-185.25, 10.97) * mm, "end": v(-180.63, 10.97) * mm});
            skLineSegment(sketch, "E2.0.9.6", {"start": v(-180.63, 6.34) * mm, "end": v(-185.25, 6.34) * mm});
            skLineSegment(sketch, "E2.0.9.7", {"start": v(-185.25, 6.34) * mm, "end": v(-185.25, 10.97) * mm});
            skLineSegment(sketch, "E2.0.9.8", {"start": v(-193.33, 10.97) * mm, "end": v(-193.33, 6.34) * mm});
            skLineSegment(sketch, "E2.0.9.9", {"start": v(-197.95, 10.97) * mm, "end": v(-193.33, 10.97) * mm});
            skLineSegment(sketch, "E2.0.9.10", {"start": v(-197.95, 6.34) * mm, "end": v(-197.95, 10.97) * mm});
            skLineSegment(sketch, "E2.0.9.11", {"start": v(-193.33, 6.34) * mm, "end": v(-197.95, 6.34) * mm});
            skLineSegment(sketch, "E2.0.10.0", {"start": v(-167.93, -1.73) * mm, "end": v(-167.93, -6.36) * mm});
            skLineSegment(sketch, "E2.0.10.1", {"start": v(-172.55, -1.73) * mm, "end": v(-167.93, -1.73) * mm});
            skLineSegment(sketch, "E2.0.10.2", {"start": v(-172.55, -6.36) * mm, "end": v(-172.55, -1.73) * mm});
            skLineSegment(sketch, "E2.0.10.3", {"start": v(-167.93, -6.36) * mm, "end": v(-172.55, -6.36) * mm});
            skLineSegment(sketch, "E2.0.10.4", {"start": v(-180.63, -1.73) * mm, "end": v(-180.63, -6.36) * mm});
            skLineSegment(sketch, "E2.0.10.5", {"start": v(-185.25, -1.73) * mm, "end": v(-180.63, -1.73) * mm});
            skLineSegment(sketch, "E2.0.10.6", {"start": v(-180.63, -6.36) * mm, "end": v(-185.25, -6.36) * mm});
            skLineSegment(sketch, "E2.0.10.7", {"start": v(-185.25, -6.36) * mm, "end": v(-185.25, -1.73) * mm});
            skLineSegment(sketch, "E2.0.10.8", {"start": v(-193.33, -1.73) * mm, "end": v(-193.33, -6.36) * mm});
            skLineSegment(sketch, "E2.0.10.9", {"start": v(-197.95, -1.73) * mm, "end": v(-193.33, -1.73) * mm});
            skLineSegment(sketch, "E2.0.10.10", {"start": v(-197.95, -6.36) * mm, "end": v(-197.95, -1.73) * mm});
            skLineSegment(sketch, "E2.0.10.11", {"start": v(-193.33, -6.36) * mm, "end": v(-197.95, -6.36) * mm});
            skLineSegment(sketch, "E2.0.11.0", {"start": v(-167.93, -14.43) * mm, "end": v(-167.93, -19.06) * mm});
            skLineSegment(sketch, "E2.0.11.1", {"start": v(-172.55, -14.43) * mm, "end": v(-167.93, -14.43) * mm});
            skLineSegment(sketch, "E2.0.11.2", {"start": v(-172.55, -19.06) * mm, "end": v(-172.55, -14.43) * mm});
            skLineSegment(sketch, "E2.0.11.3", {"start": v(-167.93, -19.06) * mm, "end": v(-172.55, -19.06) * mm});
            skLineSegment(sketch, "E2.0.11.4", {"start": v(-180.63, -14.43) * mm, "end": v(-180.63, -19.06) * mm});
            skLineSegment(sketch, "E2.0.11.5", {"start": v(-185.25, -14.43) * mm, "end": v(-180.63, -14.43) * mm});
            skLineSegment(sketch, "E2.0.11.6", {"start": v(-180.63, -19.06) * mm, "end": v(-185.25, -19.06) * mm});
            skLineSegment(sketch, "E2.0.11.7", {"start": v(-185.25, -19.06) * mm, "end": v(-185.25, -14.43) * mm});
            skLineSegment(sketch, "E2.0.11.8", {"start": v(-193.33, -14.43) * mm, "end": v(-193.33, -19.06) * mm});
            skLineSegment(sketch, "E2.0.11.9", {"start": v(-197.95, -14.43) * mm, "end": v(-193.33, -14.43) * mm});
            skLineSegment(sketch, "E2.0.11.10", {"start": v(-197.95, -19.06) * mm, "end": v(-197.95, -14.43) * mm});
            skLineSegment(sketch, "E2.0.11.11", {"start": v(-193.33, -19.06) * mm, "end": v(-197.95, -19.06) * mm});
            skLineSegment(sketch, "E2.0.12.0", {"start": v(-167.93, -27.13) * mm, "end": v(-167.93, -31.76) * mm});
            skLineSegment(sketch, "E2.0.12.1", {"start": v(-172.55, -27.13) * mm, "end": v(-167.93, -27.13) * mm});
            skLineSegment(sketch, "E2.0.12.2", {"start": v(-172.55, -31.76) * mm, "end": v(-172.55, -27.13) * mm});
            skLineSegment(sketch, "E2.0.12.3", {"start": v(-167.93, -31.76) * mm, "end": v(-172.55, -31.76) * mm});
            skLineSegment(sketch, "E2.0.12.4", {"start": v(-180.63, -27.13) * mm, "end": v(-180.63, -31.76) * mm});
            skLineSegment(sketch, "E2.0.12.5", {"start": v(-185.25, -27.13) * mm, "end": v(-180.63, -27.13) * mm});
            skLineSegment(sketch, "E2.0.12.6", {"start": v(-180.63, -31.76) * mm, "end": v(-185.25, -31.76) * mm});
            skLineSegment(sketch, "E2.0.12.7", {"start": v(-185.25, -31.76) * mm, "end": v(-185.25, -27.13) * mm});
            skLineSegment(sketch, "E2.0.12.8", {"start": v(-193.33, -27.13) * mm, "end": v(-193.33, -31.76) * mm});
            skLineSegment(sketch, "E2.0.12.9", {"start": v(-197.95, -27.13) * mm, "end": v(-193.33, -27.13) * mm});
            skLineSegment(sketch, "E2.0.12.10", {"start": v(-197.95, -31.76) * mm, "end": v(-197.95, -27.13) * mm});
            skLineSegment(sketch, "E2.0.12.11", {"start": v(-193.33, -31.76) * mm, "end": v(-197.95, -31.76) * mm});
            skLineSegment(sketch, "E2.0.13.0", {"start": v(-167.93, -39.83) * mm, "end": v(-167.93, -44.46) * mm});
            skLineSegment(sketch, "E2.0.13.1", {"start": v(-172.55, -39.83) * mm, "end": v(-167.93, -39.83) * mm});
            skLineSegment(sketch, "E2.0.13.2", {"start": v(-172.55, -44.46) * mm, "end": v(-172.55, -39.83) * mm});
            skLineSegment(sketch, "E2.0.13.3", {"start": v(-167.93, -44.46) * mm, "end": v(-172.55, -44.46) * mm});
            skLineSegment(sketch, "E2.0.13.4", {"start": v(-180.63, -39.83) * mm, "end": v(-180.63, -44.46) * mm});
            skLineSegment(sketch, "E2.0.13.5", {"start": v(-185.25, -39.83) * mm, "end": v(-180.63, -39.83) * mm});
            skLineSegment(sketch, "E2.0.13.6", {"start": v(-180.63, -44.46) * mm, "end": v(-185.25, -44.46) * mm});
            skLineSegment(sketch, "E2.0.13.7", {"start": v(-185.25, -44.46) * mm, "end": v(-185.25, -39.83) * mm});
            skLineSegment(sketch, "E2.0.13.8", {"start": v(-193.33, -39.83) * mm, "end": v(-193.33, -44.46) * mm});
            skLineSegment(sketch, "E2.0.13.9", {"start": v(-197.95, -39.83) * mm, "end": v(-193.33, -39.83) * mm});
            skLineSegment(sketch, "E2.0.13.10", {"start": v(-197.95, -44.46) * mm, "end": v(-197.95, -39.83) * mm});
            skLineSegment(sketch, "E2.0.13.11", {"start": v(-193.33, -44.46) * mm, "end": v(-197.95, -44.46) * mm});
            skLineSegment(sketch, "E2.0.14.0", {"start": v(-167.93, -52.53) * mm, "end": v(-167.93, -57.16) * mm});
            skLineSegment(sketch, "E2.0.14.1", {"start": v(-172.55, -52.53) * mm, "end": v(-167.93, -52.53) * mm});
            skLineSegment(sketch, "E2.0.14.2", {"start": v(-172.55, -57.16) * mm, "end": v(-172.55, -52.53) * mm});
            skLineSegment(sketch, "E2.0.14.3", {"start": v(-167.93, -57.16) * mm, "end": v(-172.55, -57.16) * mm});
            skLineSegment(sketch, "E2.0.14.4", {"start": v(-180.63, -52.53) * mm, "end": v(-180.63, -57.16) * mm});
            skLineSegment(sketch, "E2.0.14.5", {"start": v(-185.25, -52.53) * mm, "end": v(-180.63, -52.53) * mm});
            skLineSegment(sketch, "E2.0.14.6", {"start": v(-180.63, -57.16) * mm, "end": v(-185.25, -57.16) * mm});
            skLineSegment(sketch, "E2.0.14.7", {"start": v(-185.25, -57.16) * mm, "end": v(-185.25, -52.53) * mm});
            skLineSegment(sketch, "E2.0.14.8", {"start": v(-193.33, -52.53) * mm, "end": v(-193.33, -57.16) * mm});
            skLineSegment(sketch, "E2.0.14.9", {"start": v(-197.95, -52.53) * mm, "end": v(-193.33, -52.53) * mm});
            skLineSegment(sketch, "E2.0.14.10", {"start": v(-197.95, -57.16) * mm, "end": v(-197.95, -52.53) * mm});
            skLineSegment(sketch, "E2.0.14.11", {"start": v(-193.33, -57.16) * mm, "end": v(-197.95, -57.16) * mm});
            skLineSegment(sketch, "E2.0.15.0", {"start": v(-167.93, -65.23) * mm, "end": v(-167.93, -69.86) * mm});
            skLineSegment(sketch, "E2.0.15.1", {"start": v(-172.55, -65.23) * mm, "end": v(-167.93, -65.23) * mm});
            skLineSegment(sketch, "E2.0.15.2", {"start": v(-172.55, -69.86) * mm, "end": v(-172.55, -65.23) * mm});
            skLineSegment(sketch, "E2.0.15.3", {"start": v(-167.93, -69.86) * mm, "end": v(-172.55, -69.86) * mm});
            skLineSegment(sketch, "E2.0.15.4", {"start": v(-180.63, -65.23) * mm, "end": v(-180.63, -69.86) * mm});
            skLineSegment(sketch, "E2.0.15.5", {"start": v(-185.25, -65.23) * mm, "end": v(-180.63, -65.23) * mm});
            skLineSegment(sketch, "E2.0.15.6", {"start": v(-180.63, -69.86) * mm, "end": v(-185.25, -69.86) * mm});
            skLineSegment(sketch, "E2.0.15.7", {"start": v(-185.25, -69.86) * mm, "end": v(-185.25, -65.23) * mm});
            skLineSegment(sketch, "E2.0.15.8", {"start": v(-193.33, -65.23) * mm, "end": v(-193.33, -69.86) * mm});
            skLineSegment(sketch, "E2.0.15.9", {"start": v(-197.95, -65.23) * mm, "end": v(-193.33, -65.23) * mm});
            skLineSegment(sketch, "E2.0.15.10", {"start": v(-197.95, -69.86) * mm, "end": v(-197.95, -65.23) * mm});
            skLineSegment(sketch, "E2.0.15.11", {"start": v(-193.33, -69.86) * mm, "end": v(-197.95, -69.86) * mm});
            skLineSegment(sketch, "E2.0.16.0", {"start": v(-167.93, -77.93) * mm, "end": v(-167.93, -82.56) * mm});
            skLineSegment(sketch, "E2.0.16.1", {"start": v(-172.55, -77.93) * mm, "end": v(-167.93, -77.93) * mm});
            skLineSegment(sketch, "E2.0.16.2", {"start": v(-172.55, -82.56) * mm, "end": v(-172.55, -77.93) * mm});
            skLineSegment(sketch, "E2.0.16.3", {"start": v(-167.93, -82.56) * mm, "end": v(-172.55, -82.56) * mm});
            skLineSegment(sketch, "E2.0.16.4", {"start": v(-180.63, -77.93) * mm, "end": v(-180.63, -82.56) * mm});
            skLineSegment(sketch, "E2.0.16.5", {"start": v(-185.25, -77.93) * mm, "end": v(-180.63, -77.93) * mm});
            skLineSegment(sketch, "E2.0.16.6", {"start": v(-180.63, -82.56) * mm, "end": v(-185.25, -82.56) * mm});
            skLineSegment(sketch, "E2.0.16.7", {"start": v(-185.25, -82.56) * mm, "end": v(-185.25, -77.93) * mm});
            skLineSegment(sketch, "E2.0.16.8", {"start": v(-193.33, -77.93) * mm, "end": v(-193.33, -82.56) * mm});
            skLineSegment(sketch, "E2.0.16.9", {"start": v(-197.95, -77.93) * mm, "end": v(-193.33, -77.93) * mm});
            skLineSegment(sketch, "E2.0.16.10", {"start": v(-197.95, -82.56) * mm, "end": v(-197.95, -77.93) * mm});
            skLineSegment(sketch, "E2.0.16.11", {"start": v(-193.33, -82.56) * mm, "end": v(-197.95, -82.56) * mm});
            skLineSegment(sketch, "E2.0.17.0", {"start": v(-167.93, -90.63) * mm, "end": v(-167.93, -95.26) * mm});
            skLineSegment(sketch, "E2.0.17.1", {"start": v(-172.55, -90.63) * mm, "end": v(-167.93, -90.63) * mm});
            skLineSegment(sketch, "E2.0.17.2", {"start": v(-172.55, -95.26) * mm, "end": v(-172.55, -90.63) * mm});
            skLineSegment(sketch, "E2.0.17.3", {"start": v(-167.93, -95.26) * mm, "end": v(-172.55, -95.26) * mm});
            skLineSegment(sketch, "E2.0.17.4", {"start": v(-180.63, -90.63) * mm, "end": v(-180.63, -95.26) * mm});
            skLineSegment(sketch, "E2.0.17.5", {"start": v(-185.25, -90.63) * mm, "end": v(-180.63, -90.63) * mm});
            skLineSegment(sketch, "E2.0.17.6", {"start": v(-180.63, -95.26) * mm, "end": v(-185.25, -95.26) * mm});
            skLineSegment(sketch, "E2.0.17.7", {"start": v(-185.25, -95.26) * mm, "end": v(-185.25, -90.63) * mm});
            skLineSegment(sketch, "E2.0.17.8", {"start": v(-193.33, -90.63) * mm, "end": v(-193.33, -95.26) * mm});
            skLineSegment(sketch, "E2.0.17.9", {"start": v(-197.95, -90.63) * mm, "end": v(-193.33, -90.63) * mm});
            skLineSegment(sketch, "E2.0.17.10", {"start": v(-197.95, -95.26) * mm, "end": v(-197.95, -90.63) * mm});
            skLineSegment(sketch, "E2.0.17.11", {"start": v(-193.33, -95.26) * mm, "end": v(-197.95, -95.26) * mm});
            skLineSegment(sketch, "E2.0.18.0", {"start": v(-167.93, -103.33) * mm, "end": v(-167.93, -107.96) * mm});
            skLineSegment(sketch, "E2.0.18.1", {"start": v(-172.55, -103.33) * mm, "end": v(-167.93, -103.33) * mm});
            skLineSegment(sketch, "E2.0.18.2", {"start": v(-172.55, -107.96) * mm, "end": v(-172.55, -103.33) * mm});
            skLineSegment(sketch, "E2.0.18.3", {"start": v(-167.93, -107.96) * mm, "end": v(-172.55, -107.96) * mm});
            skLineSegment(sketch, "E2.0.18.4", {"start": v(-180.63, -103.33) * mm, "end": v(-180.63, -107.96) * mm});
            skLineSegment(sketch, "E2.0.18.5", {"start": v(-185.25, -103.33) * mm, "end": v(-180.63, -103.33) * mm});
            skLineSegment(sketch, "E2.0.18.6", {"start": v(-180.63, -107.96) * mm, "end": v(-185.25, -107.96) * mm});
            skLineSegment(sketch, "E2.0.18.7", {"start": v(-185.25, -107.96) * mm, "end": v(-185.25, -103.33) * mm});
            skLineSegment(sketch, "E2.0.18.8", {"start": v(-193.33, -103.33) * mm, "end": v(-193.33, -107.96) * mm});
            skLineSegment(sketch, "E2.0.18.9", {"start": v(-197.95, -103.33) * mm, "end": v(-193.33, -103.33) * mm});
            skLineSegment(sketch, "E2.0.18.10", {"start": v(-197.95, -107.96) * mm, "end": v(-197.95, -103.33) * mm});
            skLineSegment(sketch, "E2.0.18.11", {"start": v(-193.33, -107.96) * mm, "end": v(-197.95, -107.96) * mm});
            skLineSegment(sketch, "E2.0.19.0", {"start": v(-167.93, -116.03) * mm, "end": v(-167.93, -120.66) * mm});
            skLineSegment(sketch, "E2.0.19.1", {"start": v(-172.55, -116.03) * mm, "end": v(-167.93, -116.03) * mm});
            skLineSegment(sketch, "E2.0.19.2", {"start": v(-172.55, -120.66) * mm, "end": v(-172.55, -116.03) * mm});
            skLineSegment(sketch, "E2.0.19.3", {"start": v(-167.93, -120.66) * mm, "end": v(-172.55, -120.66) * mm});
            skLineSegment(sketch, "E2.0.19.4", {"start": v(-180.63, -116.03) * mm, "end": v(-180.63, -120.66) * mm});
            skLineSegment(sketch, "E2.0.19.5", {"start": v(-185.25, -116.03) * mm, "end": v(-180.63, -116.03) * mm});
            skLineSegment(sketch, "E2.0.19.6", {"start": v(-180.63, -120.66) * mm, "end": v(-185.25, -120.66) * mm});
            skLineSegment(sketch, "E2.0.19.7", {"start": v(-185.25, -120.66) * mm, "end": v(-185.25, -116.03) * mm});
            skLineSegment(sketch, "E2.0.19.8", {"start": v(-193.33, -116.03) * mm, "end": v(-193.33, -120.66) * mm});
            skLineSegment(sketch, "E2.0.19.9", {"start": v(-197.95, -116.03) * mm, "end": v(-193.33, -116.03) * mm});
            skLineSegment(sketch, "E2.0.19.10", {"start": v(-197.95, -120.66) * mm, "end": v(-197.95, -116.03) * mm});
            skLineSegment(sketch, "E2.0.19.11", {"start": v(-193.33, -120.66) * mm, "end": v(-197.95, -120.66) * mm});
            skLineSegment(sketch, "E2.0.20.0", {"start": v(-167.93, -128.73) * mm, "end": v(-167.93, -133.36) * mm});
            skLineSegment(sketch, "E2.0.20.1", {"start": v(-172.55, -128.73) * mm, "end": v(-167.93, -128.73) * mm});
            skLineSegment(sketch, "E2.0.20.2", {"start": v(-172.55, -133.36) * mm, "end": v(-172.55, -128.73) * mm});
            skLineSegment(sketch, "E2.0.20.3", {"start": v(-167.93, -133.36) * mm, "end": v(-172.55, -133.36) * mm});
            skLineSegment(sketch, "E2.0.20.4", {"start": v(-180.63, -128.73) * mm, "end": v(-180.63, -133.36) * mm});
            skLineSegment(sketch, "E2.0.20.5", {"start": v(-185.25, -128.73) * mm, "end": v(-180.63, -128.73) * mm});
            skLineSegment(sketch, "E2.0.20.6", {"start": v(-180.63, -133.36) * mm, "end": v(-185.25, -133.36) * mm});
            skLineSegment(sketch, "E2.0.20.7", {"start": v(-185.25, -133.36) * mm, "end": v(-185.25, -128.73) * mm});
            skLineSegment(sketch, "E2.0.20.8", {"start": v(-193.33, -128.73) * mm, "end": v(-193.33, -133.36) * mm});
            skLineSegment(sketch, "E2.0.20.9", {"start": v(-197.95, -128.73) * mm, "end": v(-193.33, -128.73) * mm});
            skLineSegment(sketch, "E2.0.20.10", {"start": v(-197.95, -133.36) * mm, "end": v(-197.95, -128.73) * mm});
            skLineSegment(sketch, "E2.0.20.11", {"start": v(-193.33, -133.36) * mm, "end": v(-197.95, -133.36) * mm});
            skLineSegment(sketch, "E2.0.21.0", {"start": v(-167.93, -141.43) * mm, "end": v(-167.93, -146.06) * mm});
            skLineSegment(sketch, "E2.0.21.1", {"start": v(-172.55, -141.43) * mm, "end": v(-167.93, -141.43) * mm});
            skLineSegment(sketch, "E2.0.21.2", {"start": v(-172.55, -146.06) * mm, "end": v(-172.55, -141.43) * mm});
            skLineSegment(sketch, "E2.0.21.3", {"start": v(-167.93, -146.06) * mm, "end": v(-172.55, -146.06) * mm});
            skLineSegment(sketch, "E2.0.21.4", {"start": v(-180.63, -141.43) * mm, "end": v(-180.63, -146.06) * mm});
            skLineSegment(sketch, "E2.0.21.5", {"start": v(-185.25, -141.43) * mm, "end": v(-180.63, -141.43) * mm});
            skLineSegment(sketch, "E2.0.21.6", {"start": v(-180.63, -146.06) * mm, "end": v(-185.25, -146.06) * mm});
            skLineSegment(sketch, "E2.0.21.7", {"start": v(-185.25, -146.06) * mm, "end": v(-185.25, -141.43) * mm});
            skLineSegment(sketch, "E2.0.21.8", {"start": v(-193.33, -141.43) * mm, "end": v(-193.33, -146.06) * mm});
            skLineSegment(sketch, "E2.0.21.9", {"start": v(-197.95, -141.43) * mm, "end": v(-193.33, -141.43) * mm});
            skLineSegment(sketch, "E2.0.21.10", {"start": v(-197.95, -146.06) * mm, "end": v(-197.95, -141.43) * mm});
            skLineSegment(sketch, "E2.0.21.11", {"start": v(-193.33, -146.06) * mm, "end": v(-197.95, -146.06) * mm});
            skLineSegment(sketch, "E2.0.22.0", {"start": v(-167.93, -154.13) * mm, "end": v(-167.93, -158.76) * mm});
            skLineSegment(sketch, "E2.0.22.1", {"start": v(-172.55, -154.13) * mm, "end": v(-167.93, -154.13) * mm});
            skLineSegment(sketch, "E2.0.22.2", {"start": v(-172.55, -158.76) * mm, "end": v(-172.55, -154.13) * mm});
            skLineSegment(sketch, "E2.0.22.3", {"start": v(-167.93, -158.76) * mm, "end": v(-172.55, -158.76) * mm});
            skLineSegment(sketch, "E2.0.22.4", {"start": v(-180.63, -154.13) * mm, "end": v(-180.63, -158.76) * mm});
            skLineSegment(sketch, "E2.0.22.5", {"start": v(-185.25, -154.13) * mm, "end": v(-180.63, -154.13) * mm});
            skLineSegment(sketch, "E2.0.22.6", {"start": v(-180.63, -158.76) * mm, "end": v(-185.25, -158.76) * mm});
            skLineSegment(sketch, "E2.0.22.7", {"start": v(-185.25, -158.76) * mm, "end": v(-185.25, -154.13) * mm});
            skLineSegment(sketch, "E2.0.22.8", {"start": v(-193.33, -154.13) * mm, "end": v(-193.33, -158.76) * mm});
            skLineSegment(sketch, "E2.0.22.9", {"start": v(-197.95, -154.13) * mm, "end": v(-193.33, -154.13) * mm});
            skLineSegment(sketch, "E2.0.22.10", {"start": v(-197.95, -158.76) * mm, "end": v(-197.95, -154.13) * mm});
            skLineSegment(sketch, "E2.0.22.11", {"start": v(-193.33, -158.76) * mm, "end": v(-197.95, -158.76) * mm});
            skLineSegment(sketch, "E2.0.23.0", {"start": v(-167.93, -166.83) * mm, "end": v(-167.93, -171.46) * mm});
            skLineSegment(sketch, "E2.0.23.1", {"start": v(-172.55, -166.83) * mm, "end": v(-167.93, -166.83) * mm});
            skLineSegment(sketch, "E2.0.23.2", {"start": v(-172.55, -171.46) * mm, "end": v(-172.55, -166.83) * mm});
            skLineSegment(sketch, "E2.0.23.3", {"start": v(-167.93, -171.46) * mm, "end": v(-172.55, -171.46) * mm});
            skLineSegment(sketch, "E2.0.23.4", {"start": v(-180.63, -166.83) * mm, "end": v(-180.63, -171.46) * mm});
            skLineSegment(sketch, "E2.0.23.5", {"start": v(-185.25, -166.83) * mm, "end": v(-180.63, -166.83) * mm});
            skLineSegment(sketch, "E2.0.23.6", {"start": v(-180.63, -171.46) * mm, "end": v(-185.25, -171.46) * mm});
            skLineSegment(sketch, "E2.0.23.7", {"start": v(-185.25, -171.46) * mm, "end": v(-185.25, -166.83) * mm});
            skLineSegment(sketch, "E2.0.23.8", {"start": v(-193.33, -166.83) * mm, "end": v(-193.33, -171.46) * mm});
            skLineSegment(sketch, "E2.0.23.9", {"start": v(-197.95, -166.83) * mm, "end": v(-193.33, -166.83) * mm});
            skLineSegment(sketch, "E2.0.23.10", {"start": v(-197.95, -171.46) * mm, "end": v(-197.95, -166.83) * mm});
            skLineSegment(sketch, "E2.0.23.11", {"start": v(-193.33, -171.46) * mm, "end": v(-197.95, -171.46) * mm});
            skLineSegment(sketch, "E3.1.0.0", {"start": v(9.87, 107.94) * mm, "end": v(5.25, 107.94) * mm});
            skLineSegment(sketch, "E3.1.0.1", {"start": v(9.87, 112.57) * mm, "end": v(9.87, 107.94) * mm});
            skLineSegment(sketch, "E3.1.0.2", {"start": v(5.25, 112.57) * mm, "end": v(9.87, 112.57) * mm});
            skLineSegment(sketch, "E3.1.0.3", {"start": v(5.25, 95.24) * mm, "end": v(5.25, 99.87) * mm});
            skLineSegment(sketch, "E3.1.0.4", {"start": v(9.87, 95.24) * mm, "end": v(5.25, 95.24) * mm});
            skLineSegment(sketch, "E3.1.0.5", {"start": v(9.87, 99.87) * mm, "end": v(9.87, 95.24) * mm});
            skLineSegment(sketch, "E3.1.0.6", {"start": v(5.25, 99.87) * mm, "end": v(9.87, 99.87) * mm});
            skLineSegment(sketch, "E3.1.0.7", {"start": v(5.25, 107.94) * mm, "end": v(5.25, 112.57) * mm});
            skLineSegment(sketch, "E3.2.0.0", {"start": v(-2.83, 107.94) * mm, "end": v(-7.45, 107.94) * mm});
            skLineSegment(sketch, "E3.2.0.1", {"start": v(-2.83, 112.57) * mm, "end": v(-2.83, 107.94) * mm});
            skLineSegment(sketch, "E3.2.0.2", {"start": v(-7.45, 112.57) * mm, "end": v(-2.83, 112.57) * mm});
            skLineSegment(sketch, "E3.2.0.3", {"start": v(-7.45, 95.24) * mm, "end": v(-7.45, 99.87) * mm});
            skLineSegment(sketch, "E3.2.0.4", {"start": v(-2.83, 95.24) * mm, "end": v(-7.45, 95.24) * mm});
            skLineSegment(sketch, "E3.2.0.5", {"start": v(-2.83, 99.87) * mm, "end": v(-2.83, 95.24) * mm});
            skLineSegment(sketch, "E3.2.0.6", {"start": v(-7.45, 99.87) * mm, "end": v(-2.83, 99.87) * mm});
            skLineSegment(sketch, "E3.2.0.7", {"start": v(-7.45, 107.94) * mm, "end": v(-7.45, 112.57) * mm});
            skLineSegment(sketch, "E3.3.0.0", {"start": v(-15.53, 107.94) * mm, "end": v(-20.15, 107.94) * mm});
            skLineSegment(sketch, "E3.3.0.1", {"start": v(-15.53, 112.57) * mm, "end": v(-15.53, 107.94) * mm});
            skLineSegment(sketch, "E3.3.0.2", {"start": v(-20.15, 112.57) * mm, "end": v(-15.53, 112.57) * mm});
            skLineSegment(sketch, "E3.3.0.3", {"start": v(-20.15, 95.24) * mm, "end": v(-20.15, 99.87) * mm});
            skLineSegment(sketch, "E3.3.0.4", {"start": v(-15.53, 95.24) * mm, "end": v(-20.15, 95.24) * mm});
            skLineSegment(sketch, "E3.3.0.5", {"start": v(-15.53, 99.87) * mm, "end": v(-15.53, 95.24) * mm});
            skLineSegment(sketch, "E3.3.0.6", {"start": v(-20.15, 99.87) * mm, "end": v(-15.53, 99.87) * mm});
            skLineSegment(sketch, "E3.3.0.7", {"start": v(-20.15, 107.94) * mm, "end": v(-20.15, 112.57) * mm});
            skLineSegment(sketch, "E3.4.0.0", {"start": v(-28.23, 107.94) * mm, "end": v(-32.85, 107.94) * mm});
            skLineSegment(sketch, "E3.4.0.1", {"start": v(-28.23, 112.57) * mm, "end": v(-28.23, 107.94) * mm});
            skLineSegment(sketch, "E3.4.0.2", {"start": v(-32.85, 112.57) * mm, "end": v(-28.23, 112.57) * mm});
            skLineSegment(sketch, "E3.4.0.3", {"start": v(-32.85, 95.24) * mm, "end": v(-32.85, 99.87) * mm});
            skLineSegment(sketch, "E3.4.0.4", {"start": v(-28.23, 95.24) * mm, "end": v(-32.85, 95.24) * mm});
            skLineSegment(sketch, "E3.4.0.5", {"start": v(-28.23, 99.87) * mm, "end": v(-28.23, 95.24) * mm});
            skLineSegment(sketch, "E3.4.0.6", {"start": v(-32.85, 99.87) * mm, "end": v(-28.23, 99.87) * mm});
            skLineSegment(sketch, "E3.4.0.7", {"start": v(-32.85, 107.94) * mm, "end": v(-32.85, 112.57) * mm});
            skLineSegment(sketch, "E3.5.0.0", {"start": v(-40.93, 107.94) * mm, "end": v(-45.55, 107.94) * mm});
            skLineSegment(sketch, "E3.5.0.1", {"start": v(-40.93, 112.57) * mm, "end": v(-40.93, 107.94) * mm});
            skLineSegment(sketch, "E3.5.0.2", {"start": v(-45.55, 112.57) * mm, "end": v(-40.93, 112.57) * mm});
            skLineSegment(sketch, "E3.5.0.3", {"start": v(-45.55, 95.24) * mm, "end": v(-45.55, 99.87) * mm});
            skLineSegment(sketch, "E3.5.0.4", {"start": v(-40.93, 95.24) * mm, "end": v(-45.55, 95.24) * mm});
            skLineSegment(sketch, "E3.5.0.5", {"start": v(-40.93, 99.87) * mm, "end": v(-40.93, 95.24) * mm});
            skLineSegment(sketch, "E3.5.0.6", {"start": v(-45.55, 99.87) * mm, "end": v(-40.93, 99.87) * mm});
            skLineSegment(sketch, "E3.5.0.7", {"start": v(-45.55, 107.94) * mm, "end": v(-45.55, 112.57) * mm});
            skLineSegment(sketch, "E3.6.0.0", {"start": v(-53.63, 107.94) * mm, "end": v(-58.25, 107.94) * mm});
            skLineSegment(sketch, "E3.6.0.1", {"start": v(-53.63, 112.57) * mm, "end": v(-53.63, 107.94) * mm});
            skLineSegment(sketch, "E3.6.0.2", {"start": v(-58.25, 112.57) * mm, "end": v(-53.63, 112.57) * mm});
            skLineSegment(sketch, "E3.6.0.3", {"start": v(-58.25, 95.24) * mm, "end": v(-58.25, 99.87) * mm});
            skLineSegment(sketch, "E3.6.0.4", {"start": v(-53.63, 95.24) * mm, "end": v(-58.25, 95.24) * mm});
            skLineSegment(sketch, "E3.6.0.5", {"start": v(-53.63, 99.87) * mm, "end": v(-53.63, 95.24) * mm});
            skLineSegment(sketch, "E3.6.0.6", {"start": v(-58.25, 99.87) * mm, "end": v(-53.63, 99.87) * mm});
            skLineSegment(sketch, "E3.6.0.7", {"start": v(-58.25, 107.94) * mm, "end": v(-58.25, 112.57) * mm});
            skLineSegment(sketch, "E3.7.0.0", {"start": v(-66.33, 107.94) * mm, "end": v(-70.95, 107.94) * mm});
            skLineSegment(sketch, "E3.7.0.1", {"start": v(-66.33, 112.57) * mm, "end": v(-66.33, 107.94) * mm});
            skLineSegment(sketch, "E3.7.0.2", {"start": v(-70.95, 112.57) * mm, "end": v(-66.33, 112.57) * mm});
            skLineSegment(sketch, "E3.7.0.3", {"start": v(-70.95, 95.24) * mm, "end": v(-70.95, 99.87) * mm});
            skLineSegment(sketch, "E3.7.0.4", {"start": v(-66.33, 95.24) * mm, "end": v(-70.95, 95.24) * mm});
            skLineSegment(sketch, "E3.7.0.5", {"start": v(-66.33, 99.87) * mm, "end": v(-66.33, 95.24) * mm});
            skLineSegment(sketch, "E3.7.0.6", {"start": v(-70.95, 99.87) * mm, "end": v(-66.33, 99.87) * mm});
            skLineSegment(sketch, "E3.7.0.7", {"start": v(-70.95, 107.94) * mm, "end": v(-70.95, 112.57) * mm});
            skLineSegment(sketch, "E3.8.0.0", {"start": v(-79.03, 107.94) * mm, "end": v(-83.65, 107.94) * mm});
            skLineSegment(sketch, "E3.8.0.1", {"start": v(-79.03, 112.57) * mm, "end": v(-79.03, 107.94) * mm});
            skLineSegment(sketch, "E3.8.0.2", {"start": v(-83.65, 112.57) * mm, "end": v(-79.03, 112.57) * mm});
            skLineSegment(sketch, "E3.8.0.3", {"start": v(-83.65, 95.24) * mm, "end": v(-83.65, 99.87) * mm});
            skLineSegment(sketch, "E3.8.0.4", {"start": v(-79.03, 95.24) * mm, "end": v(-83.65, 95.24) * mm});
            skLineSegment(sketch, "E3.8.0.5", {"start": v(-79.03, 99.87) * mm, "end": v(-79.03, 95.24) * mm});
            skLineSegment(sketch, "E3.8.0.6", {"start": v(-83.65, 99.87) * mm, "end": v(-79.03, 99.87) * mm});
            skLineSegment(sketch, "E3.8.0.7", {"start": v(-83.65, 107.94) * mm, "end": v(-83.65, 112.57) * mm});
            skLineSegment(sketch, "E3.9.0.0", {"start": v(-91.73, 107.94) * mm, "end": v(-96.35, 107.94) * mm});
            skLineSegment(sketch, "E3.9.0.1", {"start": v(-91.73, 112.57) * mm, "end": v(-91.73, 107.94) * mm});
            skLineSegment(sketch, "E3.9.0.2", {"start": v(-96.35, 112.57) * mm, "end": v(-91.73, 112.57) * mm});
            skLineSegment(sketch, "E3.9.0.3", {"start": v(-96.35, 95.24) * mm, "end": v(-96.35, 99.87) * mm});
            skLineSegment(sketch, "E3.9.0.4", {"start": v(-91.73, 95.24) * mm, "end": v(-96.35, 95.24) * mm});
            skLineSegment(sketch, "E3.9.0.5", {"start": v(-91.73, 99.87) * mm, "end": v(-91.73, 95.24) * mm});
            skLineSegment(sketch, "E3.9.0.6", {"start": v(-96.35, 99.87) * mm, "end": v(-91.73, 99.87) * mm});
            skLineSegment(sketch, "E3.9.0.7", {"start": v(-96.35, 107.94) * mm, "end": v(-96.35, 112.57) * mm});
            skLineSegment(sketch, "E3.10.0.0", {"start": v(-104.43, 107.94) * mm, "end": v(-109.05, 107.94) * mm});
            skLineSegment(sketch, "E3.10.0.1", {"start": v(-104.43, 112.57) * mm, "end": v(-104.43, 107.94) * mm});
            skLineSegment(sketch, "E3.10.0.2", {"start": v(-109.05, 112.57) * mm, "end": v(-104.43, 112.57) * mm});
            skLineSegment(sketch, "E3.10.0.3", {"start": v(-109.05, 95.24) * mm, "end": v(-109.05, 99.87) * mm});
            skLineSegment(sketch, "E3.10.0.4", {"start": v(-104.43, 95.24) * mm, "end": v(-109.05, 95.24) * mm});
            skLineSegment(sketch, "E3.10.0.5", {"start": v(-104.43, 99.87) * mm, "end": v(-104.43, 95.24) * mm});
            skLineSegment(sketch, "E3.10.0.6", {"start": v(-109.05, 99.87) * mm, "end": v(-104.43, 99.87) * mm});
            skLineSegment(sketch, "E3.10.0.7", {"start": v(-109.05, 107.94) * mm, "end": v(-109.05, 112.57) * mm});
            skLineSegment(sketch, "E3.11.0.0", {"start": v(-117.13, 107.94) * mm, "end": v(-121.75, 107.94) * mm});
            skLineSegment(sketch, "E3.11.0.1", {"start": v(-117.13, 112.57) * mm, "end": v(-117.13, 107.94) * mm});
            skLineSegment(sketch, "E3.11.0.2", {"start": v(-121.75, 112.57) * mm, "end": v(-117.13, 112.57) * mm});
            skLineSegment(sketch, "E3.11.0.3", {"start": v(-121.75, 95.24) * mm, "end": v(-121.75, 99.87) * mm});
            skLineSegment(sketch, "E3.11.0.4", {"start": v(-117.13, 95.24) * mm, "end": v(-121.75, 95.24) * mm});
            skLineSegment(sketch, "E3.11.0.5", {"start": v(-117.13, 99.87) * mm, "end": v(-117.13, 95.24) * mm});
            skLineSegment(sketch, "E3.11.0.6", {"start": v(-121.75, 99.87) * mm, "end": v(-117.13, 99.87) * mm});
            skLineSegment(sketch, "E3.11.0.7", {"start": v(-121.75, 107.94) * mm, "end": v(-121.75, 112.57) * mm});
            skLineSegment(sketch, "E3.12.0.0", {"start": v(-129.83, 107.94) * mm, "end": v(-134.45, 107.94) * mm});
            skLineSegment(sketch, "E3.12.0.1", {"start": v(-129.83, 112.57) * mm, "end": v(-129.83, 107.94) * mm});
            skLineSegment(sketch, "E3.12.0.2", {"start": v(-134.45, 112.57) * mm, "end": v(-129.83, 112.57) * mm});
            skLineSegment(sketch, "E3.12.0.3", {"start": v(-134.45, 95.24) * mm, "end": v(-134.45, 99.87) * mm});
            skLineSegment(sketch, "E3.12.0.4", {"start": v(-129.83, 95.24) * mm, "end": v(-134.45, 95.24) * mm});
            skLineSegment(sketch, "E3.12.0.5", {"start": v(-129.83, 99.87) * mm, "end": v(-129.83, 95.24) * mm});
            skLineSegment(sketch, "E3.12.0.6", {"start": v(-134.45, 99.87) * mm, "end": v(-129.83, 99.87) * mm});
            skLineSegment(sketch, "E3.12.0.7", {"start": v(-134.45, 107.94) * mm, "end": v(-134.45, 112.57) * mm});
            skLineSegment(sketch, "E3.13.0.0", {"start": v(-142.53, 107.94) * mm, "end": v(-147.15, 107.94) * mm});
            skLineSegment(sketch, "E3.13.0.1", {"start": v(-142.53, 112.57) * mm, "end": v(-142.53, 107.94) * mm});
            skLineSegment(sketch, "E3.13.0.2", {"start": v(-147.15, 112.57) * mm, "end": v(-142.53, 112.57) * mm});
            skLineSegment(sketch, "E3.13.0.3", {"start": v(-147.15, 95.24) * mm, "end": v(-147.15, 99.87) * mm});
            skLineSegment(sketch, "E3.13.0.4", {"start": v(-142.53, 95.24) * mm, "end": v(-147.15, 95.24) * mm});
            skLineSegment(sketch, "E3.13.0.5", {"start": v(-142.53, 99.87) * mm, "end": v(-142.53, 95.24) * mm});
            skLineSegment(sketch, "E3.13.0.6", {"start": v(-147.15, 99.87) * mm, "end": v(-142.53, 99.87) * mm});
            skLineSegment(sketch, "E3.13.0.7", {"start": v(-147.15, 107.94) * mm, "end": v(-147.15, 112.57) * mm});
            skLineSegment(sketch, "E3.14.0.0", {"start": v(-155.23, 107.94) * mm, "end": v(-159.85, 107.94) * mm});
            skLineSegment(sketch, "E3.14.0.1", {"start": v(-155.23, 112.57) * mm, "end": v(-155.23, 107.94) * mm});
            skLineSegment(sketch, "E3.14.0.2", {"start": v(-159.85, 112.57) * mm, "end": v(-155.23, 112.57) * mm});
            skLineSegment(sketch, "E3.14.0.3", {"start": v(-159.85, 95.24) * mm, "end": v(-159.85, 99.87) * mm});
            skLineSegment(sketch, "E3.14.0.4", {"start": v(-155.23, 95.24) * mm, "end": v(-159.85, 95.24) * mm});
            skLineSegment(sketch, "E3.14.0.5", {"start": v(-155.23, 99.87) * mm, "end": v(-155.23, 95.24) * mm});
            skLineSegment(sketch, "E3.14.0.6", {"start": v(-159.85, 99.87) * mm, "end": v(-155.23, 99.87) * mm});
            skLineSegment(sketch, "E3.14.0.7", {"start": v(-159.85, 107.94) * mm, "end": v(-159.85, 112.57) * mm});
            skLineSegment(sketch, "E3.direction1", {"start": v(17.95, 95.24) * mm, "end": v(5.25, 95.24) * mm, "construction": true});
            skLineSegment(sketch, "E4.1.0.0", {"start": v(5.25, -141.43) * mm, "end": v(9.87, -141.43) * mm});
            skLineSegment(sketch, "E4.1.0.1", {"start": v(9.87, -146.06) * mm, "end": v(5.25, -146.06) * mm});
            skLineSegment(sketch, "E4.1.0.2", {"start": v(9.87, -154.13) * mm, "end": v(9.87, -158.76) * mm});
            skLineSegment(sketch, "E4.1.0.3", {"start": v(9.87, -141.43) * mm, "end": v(9.87, -146.06) * mm});
            skLineSegment(sketch, "E4.1.0.4", {"start": v(5.25, -166.83) * mm, "end": v(9.87, -166.83) * mm});
            skLineSegment(sketch, "E4.1.0.5", {"start": v(5.25, -116.03) * mm, "end": v(9.87, -116.03) * mm});
            skLineSegment(sketch, "E4.1.0.6", {"start": v(5.25, -120.66) * mm, "end": v(5.25, -116.03) * mm});
            skLineSegment(sketch, "E4.1.0.7", {"start": v(5.25, -171.46) * mm, "end": v(5.25, -166.83) * mm});
            skLineSegment(sketch, "E4.1.0.8", {"start": v(5.25, -154.13) * mm, "end": v(9.87, -154.13) * mm});
            skLineSegment(sketch, "E4.1.0.9", {"start": v(9.87, -133.36) * mm, "end": v(5.25, -133.36) * mm});
            skLineSegment(sketch, "E4.1.0.10", {"start": v(9.87, -166.83) * mm, "end": v(9.87, -171.46) * mm});
            skLineSegment(sketch, "E4.1.0.11", {"start": v(9.87, -116.03) * mm, "end": v(9.87, -120.66) * mm});
            skLineSegment(sketch, "E4.1.0.12", {"start": v(9.87, -171.46) * mm, "end": v(5.25, -171.46) * mm});
            skLineSegment(sketch, "E4.1.0.13", {"start": v(9.87, -120.66) * mm, "end": v(5.25, -120.66) * mm});
            skLineSegment(sketch, "E4.1.0.14", {"start": v(9.87, -128.73) * mm, "end": v(9.87, -133.36) * mm});
            skLineSegment(sketch, "E4.1.0.15", {"start": v(5.25, -128.73) * mm, "end": v(9.87, -128.73) * mm});
            skLineSegment(sketch, "E4.1.0.16", {"start": v(5.25, -158.76) * mm, "end": v(5.25, -154.13) * mm});
            skLineSegment(sketch, "E4.1.0.17", {"start": v(5.25, -133.36) * mm, "end": v(5.25, -128.73) * mm});
            skLineSegment(sketch, "E4.1.0.18", {"start": v(5.25, -146.06) * mm, "end": v(5.25, -141.43) * mm});
            skLineSegment(sketch, "E4.1.0.19", {"start": v(9.87, -158.76) * mm, "end": v(5.25, -158.76) * mm});
            skLineSegment(sketch, "E4.2.0.0", {"start": v(-7.45, -141.43) * mm, "end": v(-2.83, -141.43) * mm});
            skLineSegment(sketch, "E4.2.0.1", {"start": v(-2.83, -146.06) * mm, "end": v(-7.45, -146.06) * mm});
            skLineSegment(sketch, "E4.2.0.2", {"start": v(-2.83, -154.13) * mm, "end": v(-2.83, -158.76) * mm});
            skLineSegment(sketch, "E4.2.0.3", {"start": v(-2.83, -141.43) * mm, "end": v(-2.83, -146.06) * mm});
            skLineSegment(sketch, "E4.2.0.4", {"start": v(-7.45, -166.83) * mm, "end": v(-2.83, -166.83) * mm});
            skLineSegment(sketch, "E4.2.0.5", {"start": v(-7.45, -116.03) * mm, "end": v(-2.83, -116.03) * mm});
            skLineSegment(sketch, "E4.2.0.6", {"start": v(-7.45, -120.66) * mm, "end": v(-7.45, -116.03) * mm});
            skLineSegment(sketch, "E4.2.0.7", {"start": v(-7.45, -171.46) * mm, "end": v(-7.45, -166.83) * mm});
            skLineSegment(sketch, "E4.2.0.8", {"start": v(-7.45, -154.13) * mm, "end": v(-2.83, -154.13) * mm});
            skLineSegment(sketch, "E4.2.0.9", {"start": v(-2.83, -133.36) * mm, "end": v(-7.45, -133.36) * mm});
            skLineSegment(sketch, "E4.2.0.10", {"start": v(-2.83, -166.83) * mm, "end": v(-2.83, -171.46) * mm});
            skLineSegment(sketch, "E4.2.0.11", {"start": v(-2.83, -116.03) * mm, "end": v(-2.83, -120.66) * mm});
            skLineSegment(sketch, "E4.2.0.12", {"start": v(-2.83, -171.46) * mm, "end": v(-7.45, -171.46) * mm});
            skLineSegment(sketch, "E4.2.0.13", {"start": v(-2.83, -120.66) * mm, "end": v(-7.45, -120.66) * mm});
            skLineSegment(sketch, "E4.2.0.14", {"start": v(-2.83, -128.73) * mm, "end": v(-2.83, -133.36) * mm});
            skLineSegment(sketch, "E4.2.0.15", {"start": v(-7.45, -128.73) * mm, "end": v(-2.83, -128.73) * mm});
            skLineSegment(sketch, "E4.2.0.16", {"start": v(-7.45, -158.76) * mm, "end": v(-7.45, -154.13) * mm});
            skLineSegment(sketch, "E4.2.0.17", {"start": v(-7.45, -133.36) * mm, "end": v(-7.45, -128.73) * mm});
            skLineSegment(sketch, "E4.2.0.18", {"start": v(-7.45, -146.06) * mm, "end": v(-7.45, -141.43) * mm});
            skLineSegment(sketch, "E4.2.0.19", {"start": v(-2.83, -158.76) * mm, "end": v(-7.45, -158.76) * mm});
            skLineSegment(sketch, "E4.3.0.0", {"start": v(-20.15, -141.43) * mm, "end": v(-15.53, -141.43) * mm});
            skLineSegment(sketch, "E4.3.0.1", {"start": v(-15.53, -146.06) * mm, "end": v(-20.15, -146.06) * mm});
            skLineSegment(sketch, "E4.3.0.2", {"start": v(-15.53, -154.13) * mm, "end": v(-15.53, -158.76) * mm});
            skLineSegment(sketch, "E4.3.0.3", {"start": v(-15.53, -141.43) * mm, "end": v(-15.53, -146.06) * mm});
            skLineSegment(sketch, "E4.3.0.4", {"start": v(-20.15, -166.83) * mm, "end": v(-15.53, -166.83) * mm});
            skLineSegment(sketch, "E4.3.0.5", {"start": v(-20.15, -116.03) * mm, "end": v(-15.53, -116.03) * mm});
            skLineSegment(sketch, "E4.3.0.6", {"start": v(-20.15, -120.66) * mm, "end": v(-20.15, -116.03) * mm});
            skLineSegment(sketch, "E4.3.0.7", {"start": v(-20.15, -171.46) * mm, "end": v(-20.15, -166.83) * mm});
            skLineSegment(sketch, "E4.3.0.8", {"start": v(-20.15, -154.13) * mm, "end": v(-15.53, -154.13) * mm});
            skLineSegment(sketch, "E4.3.0.9", {"start": v(-15.53, -133.36) * mm, "end": v(-20.15, -133.36) * mm});
            skLineSegment(sketch, "E4.3.0.10", {"start": v(-15.53, -166.83) * mm, "end": v(-15.53, -171.46) * mm});
            skLineSegment(sketch, "E4.3.0.11", {"start": v(-15.53, -116.03) * mm, "end": v(-15.53, -120.66) * mm});
            skLineSegment(sketch, "E4.3.0.12", {"start": v(-15.53, -171.46) * mm, "end": v(-20.15, -171.46) * mm});
            skLineSegment(sketch, "E4.3.0.13", {"start": v(-15.53, -120.66) * mm, "end": v(-20.15, -120.66) * mm});
            skLineSegment(sketch, "E4.3.0.14", {"start": v(-15.53, -128.73) * mm, "end": v(-15.53, -133.36) * mm});
            skLineSegment(sketch, "E4.3.0.15", {"start": v(-20.15, -128.73) * mm, "end": v(-15.53, -128.73) * mm});
            skLineSegment(sketch, "E4.3.0.16", {"start": v(-20.15, -158.76) * mm, "end": v(-20.15, -154.13) * mm});
            skLineSegment(sketch, "E4.3.0.17", {"start": v(-20.15, -133.36) * mm, "end": v(-20.15, -128.73) * mm});
            skLineSegment(sketch, "E4.3.0.18", {"start": v(-20.15, -146.06) * mm, "end": v(-20.15, -141.43) * mm});
            skLineSegment(sketch, "E4.3.0.19", {"start": v(-15.53, -158.76) * mm, "end": v(-20.15, -158.76) * mm});
            skLineSegment(sketch, "E4.4.0.0", {"start": v(-32.85, -141.43) * mm, "end": v(-28.23, -141.43) * mm});
            skLineSegment(sketch, "E4.4.0.1", {"start": v(-28.23, -146.06) * mm, "end": v(-32.85, -146.06) * mm});
            skLineSegment(sketch, "E4.4.0.2", {"start": v(-28.23, -154.13) * mm, "end": v(-28.23, -158.76) * mm});
            skLineSegment(sketch, "E4.4.0.3", {"start": v(-28.23, -141.43) * mm, "end": v(-28.23, -146.06) * mm});
            skLineSegment(sketch, "E4.4.0.4", {"start": v(-32.85, -166.83) * mm, "end": v(-28.23, -166.83) * mm});
            skLineSegment(sketch, "E4.4.0.5", {"start": v(-32.85, -116.03) * mm, "end": v(-28.23, -116.03) * mm});
            skLineSegment(sketch, "E4.4.0.6", {"start": v(-32.85, -120.66) * mm, "end": v(-32.85, -116.03) * mm});
            skLineSegment(sketch, "E4.4.0.7", {"start": v(-32.85, -171.46) * mm, "end": v(-32.85, -166.83) * mm});
            skLineSegment(sketch, "E4.4.0.8", {"start": v(-32.85, -154.13) * mm, "end": v(-28.23, -154.13) * mm});
            skLineSegment(sketch, "E4.4.0.9", {"start": v(-28.23, -133.36) * mm, "end": v(-32.85, -133.36) * mm});
            skLineSegment(sketch, "E4.4.0.10", {"start": v(-28.23, -166.83) * mm, "end": v(-28.23, -171.46) * mm});
            skLineSegment(sketch, "E4.4.0.11", {"start": v(-28.23, -116.03) * mm, "end": v(-28.23, -120.66) * mm});
            skLineSegment(sketch, "E4.4.0.12", {"start": v(-28.23, -171.46) * mm, "end": v(-32.85, -171.46) * mm});
            skLineSegment(sketch, "E4.4.0.13", {"start": v(-28.23, -120.66) * mm, "end": v(-32.85, -120.66) * mm});
            skLineSegment(sketch, "E4.4.0.14", {"start": v(-28.23, -128.73) * mm, "end": v(-28.23, -133.36) * mm});
            skLineSegment(sketch, "E4.4.0.15", {"start": v(-32.85, -128.73) * mm, "end": v(-28.23, -128.73) * mm});
            skLineSegment(sketch, "E4.4.0.16", {"start": v(-32.85, -158.76) * mm, "end": v(-32.85, -154.13) * mm});
            skLineSegment(sketch, "E4.4.0.17", {"start": v(-32.85, -133.36) * mm, "end": v(-32.85, -128.73) * mm});
            skLineSegment(sketch, "E4.4.0.18", {"start": v(-32.85, -146.06) * mm, "end": v(-32.85, -141.43) * mm});
            skLineSegment(sketch, "E4.4.0.19", {"start": v(-28.23, -158.76) * mm, "end": v(-32.85, -158.76) * mm});
            skLineSegment(sketch, "E4.5.0.0", {"start": v(-45.55, -141.43) * mm, "end": v(-40.93, -141.43) * mm});
            skLineSegment(sketch, "E4.5.0.1", {"start": v(-40.93, -146.06) * mm, "end": v(-45.55, -146.06) * mm});
            skLineSegment(sketch, "E4.5.0.2", {"start": v(-40.93, -154.13) * mm, "end": v(-40.93, -158.76) * mm});
            skLineSegment(sketch, "E4.5.0.3", {"start": v(-40.93, -141.43) * mm, "end": v(-40.93, -146.06) * mm});
            skLineSegment(sketch, "E4.5.0.4", {"start": v(-45.55, -166.83) * mm, "end": v(-40.93, -166.83) * mm});
            skLineSegment(sketch, "E4.5.0.5", {"start": v(-45.55, -116.03) * mm, "end": v(-40.93, -116.03) * mm});
            skLineSegment(sketch, "E4.5.0.6", {"start": v(-45.55, -120.66) * mm, "end": v(-45.55, -116.03) * mm});
            skLineSegment(sketch, "E4.5.0.7", {"start": v(-45.55, -171.46) * mm, "end": v(-45.55, -166.83) * mm});
            skLineSegment(sketch, "E4.5.0.8", {"start": v(-45.55, -154.13) * mm, "end": v(-40.93, -154.13) * mm});
            skLineSegment(sketch, "E4.5.0.9", {"start": v(-40.93, -133.36) * mm, "end": v(-45.55, -133.36) * mm});
            skLineSegment(sketch, "E4.5.0.10", {"start": v(-40.93, -166.83) * mm, "end": v(-40.93, -171.46) * mm});
            skLineSegment(sketch, "E4.5.0.11", {"start": v(-40.93, -116.03) * mm, "end": v(-40.93, -120.66) * mm});
            skLineSegment(sketch, "E4.5.0.12", {"start": v(-40.93, -171.46) * mm, "end": v(-45.55, -171.46) * mm});
            skLineSegment(sketch, "E4.5.0.13", {"start": v(-40.93, -120.66) * mm, "end": v(-45.55, -120.66) * mm});
            skLineSegment(sketch, "E4.5.0.14", {"start": v(-40.93, -128.73) * mm, "end": v(-40.93, -133.36) * mm});
            skLineSegment(sketch, "E4.5.0.15", {"start": v(-45.55, -128.73) * mm, "end": v(-40.93, -128.73) * mm});
            skLineSegment(sketch, "E4.5.0.16", {"start": v(-45.55, -158.76) * mm, "end": v(-45.55, -154.13) * mm});
            skLineSegment(sketch, "E4.5.0.17", {"start": v(-45.55, -133.36) * mm, "end": v(-45.55, -128.73) * mm});
            skLineSegment(sketch, "E4.5.0.18", {"start": v(-45.55, -146.06) * mm, "end": v(-45.55, -141.43) * mm});
            skLineSegment(sketch, "E4.5.0.19", {"start": v(-40.93, -158.76) * mm, "end": v(-45.55, -158.76) * mm});
            skLineSegment(sketch, "E4.6.0.0", {"start": v(-58.25, -141.43) * mm, "end": v(-53.63, -141.43) * mm});
            skLineSegment(sketch, "E4.6.0.1", {"start": v(-53.63, -146.06) * mm, "end": v(-58.25, -146.06) * mm});
            skLineSegment(sketch, "E4.6.0.2", {"start": v(-53.63, -154.13) * mm, "end": v(-53.63, -158.76) * mm});
            skLineSegment(sketch, "E4.6.0.3", {"start": v(-53.63, -141.43) * mm, "end": v(-53.63, -146.06) * mm});
            skLineSegment(sketch, "E4.6.0.4", {"start": v(-58.25, -166.83) * mm, "end": v(-53.63, -166.83) * mm});
            skLineSegment(sketch, "E4.6.0.5", {"start": v(-58.25, -116.03) * mm, "end": v(-53.63, -116.03) * mm});
            skLineSegment(sketch, "E4.6.0.6", {"start": v(-58.25, -120.66) * mm, "end": v(-58.25, -116.03) * mm});
            skLineSegment(sketch, "E4.6.0.7", {"start": v(-58.25, -171.46) * mm, "end": v(-58.25, -166.83) * mm});
            skLineSegment(sketch, "E4.6.0.8", {"start": v(-58.25, -154.13) * mm, "end": v(-53.63, -154.13) * mm});
            skLineSegment(sketch, "E4.6.0.9", {"start": v(-53.63, -133.36) * mm, "end": v(-58.25, -133.36) * mm});
            skLineSegment(sketch, "E4.6.0.10", {"start": v(-53.63, -166.83) * mm, "end": v(-53.63, -171.46) * mm});
            skLineSegment(sketch, "E4.6.0.11", {"start": v(-53.63, -116.03) * mm, "end": v(-53.63, -120.66) * mm});
            skLineSegment(sketch, "E4.6.0.12", {"start": v(-53.63, -171.46) * mm, "end": v(-58.25, -171.46) * mm});
            skLineSegment(sketch, "E4.6.0.13", {"start": v(-53.63, -120.66) * mm, "end": v(-58.25, -120.66) * mm});
            skLineSegment(sketch, "E4.6.0.14", {"start": v(-53.63, -128.73) * mm, "end": v(-53.63, -133.36) * mm});
            skLineSegment(sketch, "E4.6.0.15", {"start": v(-58.25, -128.73) * mm, "end": v(-53.63, -128.73) * mm});
            skLineSegment(sketch, "E4.6.0.16", {"start": v(-58.25, -158.76) * mm, "end": v(-58.25, -154.13) * mm});
            skLineSegment(sketch, "E4.6.0.17", {"start": v(-58.25, -133.36) * mm, "end": v(-58.25, -128.73) * mm});
            skLineSegment(sketch, "E4.6.0.18", {"start": v(-58.25, -146.06) * mm, "end": v(-58.25, -141.43) * mm});
            skLineSegment(sketch, "E4.6.0.19", {"start": v(-53.63, -158.76) * mm, "end": v(-58.25, -158.76) * mm});
            skLineSegment(sketch, "E4.7.0.0", {"start": v(-70.95, -141.43) * mm, "end": v(-66.33, -141.43) * mm});
            skLineSegment(sketch, "E4.7.0.1", {"start": v(-66.33, -146.06) * mm, "end": v(-70.95, -146.06) * mm});
            skLineSegment(sketch, "E4.7.0.2", {"start": v(-66.33, -154.13) * mm, "end": v(-66.33, -158.76) * mm});
            skLineSegment(sketch, "E4.7.0.3", {"start": v(-66.33, -141.43) * mm, "end": v(-66.33, -146.06) * mm});
            skLineSegment(sketch, "E4.7.0.4", {"start": v(-70.95, -166.83) * mm, "end": v(-66.33, -166.83) * mm});
            skLineSegment(sketch, "E4.7.0.5", {"start": v(-70.95, -116.03) * mm, "end": v(-66.33, -116.03) * mm});
            skLineSegment(sketch, "E4.7.0.6", {"start": v(-70.95, -120.66) * mm, "end": v(-70.95, -116.03) * mm});
            skLineSegment(sketch, "E4.7.0.7", {"start": v(-70.95, -171.46) * mm, "end": v(-70.95, -166.83) * mm});
            skLineSegment(sketch, "E4.7.0.8", {"start": v(-70.95, -154.13) * mm, "end": v(-66.33, -154.13) * mm});
            skLineSegment(sketch, "E4.7.0.9", {"start": v(-66.33, -133.36) * mm, "end": v(-70.95, -133.36) * mm});
            skLineSegment(sketch, "E4.7.0.10", {"start": v(-66.33, -166.83) * mm, "end": v(-66.33, -171.46) * mm});
            skLineSegment(sketch, "E4.7.0.11", {"start": v(-66.33, -116.03) * mm, "end": v(-66.33, -120.66) * mm});
            skLineSegment(sketch, "E4.7.0.12", {"start": v(-66.33, -171.46) * mm, "end": v(-70.95, -171.46) * mm});
            skLineSegment(sketch, "E4.7.0.13", {"start": v(-66.33, -120.66) * mm, "end": v(-70.95, -120.66) * mm});
            skLineSegment(sketch, "E4.7.0.14", {"start": v(-66.33, -128.73) * mm, "end": v(-66.33, -133.36) * mm});
            skLineSegment(sketch, "E4.7.0.15", {"start": v(-70.95, -128.73) * mm, "end": v(-66.33, -128.73) * mm});
            skLineSegment(sketch, "E4.7.0.16", {"start": v(-70.95, -158.76) * mm, "end": v(-70.95, -154.13) * mm});
            skLineSegment(sketch, "E4.7.0.17", {"start": v(-70.95, -133.36) * mm, "end": v(-70.95, -128.73) * mm});
            skLineSegment(sketch, "E4.7.0.18", {"start": v(-70.95, -146.06) * mm, "end": v(-70.95, -141.43) * mm});
            skLineSegment(sketch, "E4.7.0.19", {"start": v(-66.33, -158.76) * mm, "end": v(-70.95, -158.76) * mm});
            skLineSegment(sketch, "E4.8.0.0", {"start": v(-83.65, -141.43) * mm, "end": v(-79.03, -141.43) * mm});
            skLineSegment(sketch, "E4.8.0.1", {"start": v(-79.03, -146.06) * mm, "end": v(-83.65, -146.06) * mm});
            skLineSegment(sketch, "E4.8.0.2", {"start": v(-79.03, -154.13) * mm, "end": v(-79.03, -158.76) * mm});
            skLineSegment(sketch, "E4.8.0.3", {"start": v(-79.03, -141.43) * mm, "end": v(-79.03, -146.06) * mm});
            skLineSegment(sketch, "E4.8.0.4", {"start": v(-83.65, -166.83) * mm, "end": v(-79.03, -166.83) * mm});
            skLineSegment(sketch, "E4.8.0.5", {"start": v(-83.65, -116.03) * mm, "end": v(-79.03, -116.03) * mm});
            skLineSegment(sketch, "E4.8.0.6", {"start": v(-83.65, -120.66) * mm, "end": v(-83.65, -116.03) * mm});
            skLineSegment(sketch, "E4.8.0.7", {"start": v(-83.65, -171.46) * mm, "end": v(-83.65, -166.83) * mm});
            skLineSegment(sketch, "E4.8.0.8", {"start": v(-83.65, -154.13) * mm, "end": v(-79.03, -154.13) * mm});
            skLineSegment(sketch, "E4.8.0.9", {"start": v(-79.03, -133.36) * mm, "end": v(-83.65, -133.36) * mm});
            skLineSegment(sketch, "E4.8.0.10", {"start": v(-79.03, -166.83) * mm, "end": v(-79.03, -171.46) * mm});
            skLineSegment(sketch, "E4.8.0.11", {"start": v(-79.03, -116.03) * mm, "end": v(-79.03, -120.66) * mm});
            skLineSegment(sketch, "E4.8.0.12", {"start": v(-79.03, -171.46) * mm, "end": v(-83.65, -171.46) * mm});
            skLineSegment(sketch, "E4.8.0.13", {"start": v(-79.03, -120.66) * mm, "end": v(-83.65, -120.66) * mm});
            skLineSegment(sketch, "E4.8.0.14", {"start": v(-79.03, -128.73) * mm, "end": v(-79.03, -133.36) * mm});
            skLineSegment(sketch, "E4.8.0.15", {"start": v(-83.65, -128.73) * mm, "end": v(-79.03, -128.73) * mm});
            skLineSegment(sketch, "E4.8.0.16", {"start": v(-83.65, -158.76) * mm, "end": v(-83.65, -154.13) * mm});
            skLineSegment(sketch, "E4.8.0.17", {"start": v(-83.65, -133.36) * mm, "end": v(-83.65, -128.73) * mm});
            skLineSegment(sketch, "E4.8.0.18", {"start": v(-83.65, -146.06) * mm, "end": v(-83.65, -141.43) * mm});
            skLineSegment(sketch, "E4.8.0.19", {"start": v(-79.03, -158.76) * mm, "end": v(-83.65, -158.76) * mm});
            skLineSegment(sketch, "E4.9.0.0", {"start": v(-96.35, -141.43) * mm, "end": v(-91.73, -141.43) * mm});
            skLineSegment(sketch, "E4.9.0.1", {"start": v(-91.73, -146.06) * mm, "end": v(-96.35, -146.06) * mm});
            skLineSegment(sketch, "E4.9.0.2", {"start": v(-91.73, -154.13) * mm, "end": v(-91.73, -158.76) * mm});
            skLineSegment(sketch, "E4.9.0.3", {"start": v(-91.73, -141.43) * mm, "end": v(-91.73, -146.06) * mm});
            skLineSegment(sketch, "E4.9.0.4", {"start": v(-96.35, -166.83) * mm, "end": v(-91.73, -166.83) * mm});
            skLineSegment(sketch, "E4.9.0.5", {"start": v(-96.35, -116.03) * mm, "end": v(-91.73, -116.03) * mm});
            skLineSegment(sketch, "E4.9.0.6", {"start": v(-96.35, -120.66) * mm, "end": v(-96.35, -116.03) * mm});
            skLineSegment(sketch, "E4.9.0.7", {"start": v(-96.35, -171.46) * mm, "end": v(-96.35, -166.83) * mm});
            skLineSegment(sketch, "E4.9.0.8", {"start": v(-96.35, -154.13) * mm, "end": v(-91.73, -154.13) * mm});
            skLineSegment(sketch, "E4.9.0.9", {"start": v(-91.73, -133.36) * mm, "end": v(-96.35, -133.36) * mm});
            skLineSegment(sketch, "E4.9.0.10", {"start": v(-91.73, -166.83) * mm, "end": v(-91.73, -171.46) * mm});
            skLineSegment(sketch, "E4.9.0.11", {"start": v(-91.73, -116.03) * mm, "end": v(-91.73, -120.66) * mm});
            skLineSegment(sketch, "E4.9.0.12", {"start": v(-91.73, -171.46) * mm, "end": v(-96.35, -171.46) * mm});
            skLineSegment(sketch, "E4.9.0.13", {"start": v(-91.73, -120.66) * mm, "end": v(-96.35, -120.66) * mm});
            skLineSegment(sketch, "E4.9.0.14", {"start": v(-91.73, -128.73) * mm, "end": v(-91.73, -133.36) * mm});
            skLineSegment(sketch, "E4.9.0.15", {"start": v(-96.35, -128.73) * mm, "end": v(-91.73, -128.73) * mm});
            skLineSegment(sketch, "E4.9.0.16", {"start": v(-96.35, -158.76) * mm, "end": v(-96.35, -154.13) * mm});
            skLineSegment(sketch, "E4.9.0.17", {"start": v(-96.35, -133.36) * mm, "end": v(-96.35, -128.73) * mm});
            skLineSegment(sketch, "E4.9.0.18", {"start": v(-96.35, -146.06) * mm, "end": v(-96.35, -141.43) * mm});
            skLineSegment(sketch, "E4.9.0.19", {"start": v(-91.73, -158.76) * mm, "end": v(-96.35, -158.76) * mm});
            skLineSegment(sketch, "E4.10.0.0", {"start": v(-109.05, -141.43) * mm, "end": v(-104.43, -141.43) * mm});
            skLineSegment(sketch, "E4.10.0.1", {"start": v(-104.43, -146.06) * mm, "end": v(-109.05, -146.06) * mm});
            skLineSegment(sketch, "E4.10.0.2", {"start": v(-104.43, -154.13) * mm, "end": v(-104.43, -158.76) * mm});
            skLineSegment(sketch, "E4.10.0.3", {"start": v(-104.43, -141.43) * mm, "end": v(-104.43, -146.06) * mm});
            skLineSegment(sketch, "E4.10.0.4", {"start": v(-109.05, -166.83) * mm, "end": v(-104.43, -166.83) * mm});
            skLineSegment(sketch, "E4.10.0.5", {"start": v(-109.05, -116.03) * mm, "end": v(-104.43, -116.03) * mm});
            skLineSegment(sketch, "E4.10.0.6", {"start": v(-109.05, -120.66) * mm, "end": v(-109.05, -116.03) * mm});
            skLineSegment(sketch, "E4.10.0.7", {"start": v(-109.05, -171.46) * mm, "end": v(-109.05, -166.83) * mm});
            skLineSegment(sketch, "E4.10.0.8", {"start": v(-109.05, -154.13) * mm, "end": v(-104.43, -154.13) * mm});
            skLineSegment(sketch, "E4.10.0.9", {"start": v(-104.43, -133.36) * mm, "end": v(-109.05, -133.36) * mm});
            skLineSegment(sketch, "E4.10.0.10", {"start": v(-104.43, -166.83) * mm, "end": v(-104.43, -171.46) * mm});
            skLineSegment(sketch, "E4.10.0.11", {"start": v(-104.43, -116.03) * mm, "end": v(-104.43, -120.66) * mm});
            skLineSegment(sketch, "E4.10.0.12", {"start": v(-104.43, -171.46) * mm, "end": v(-109.05, -171.46) * mm});
            skLineSegment(sketch, "E4.10.0.13", {"start": v(-104.43, -120.66) * mm, "end": v(-109.05, -120.66) * mm});
            skLineSegment(sketch, "E4.10.0.14", {"start": v(-104.43, -128.73) * mm, "end": v(-104.43, -133.36) * mm});
            skLineSegment(sketch, "E4.10.0.15", {"start": v(-109.05, -128.73) * mm, "end": v(-104.43, -128.73) * mm});
            skLineSegment(sketch, "E4.10.0.16", {"start": v(-109.05, -158.76) * mm, "end": v(-109.05, -154.13) * mm});
            skLineSegment(sketch, "E4.10.0.17", {"start": v(-109.05, -133.36) * mm, "end": v(-109.05, -128.73) * mm});
            skLineSegment(sketch, "E4.10.0.18", {"start": v(-109.05, -146.06) * mm, "end": v(-109.05, -141.43) * mm});
            skLineSegment(sketch, "E4.10.0.19", {"start": v(-104.43, -158.76) * mm, "end": v(-109.05, -158.76) * mm});
            skLineSegment(sketch, "E4.11.0.0", {"start": v(-121.75, -141.43) * mm, "end": v(-117.13, -141.43) * mm});
            skLineSegment(sketch, "E4.11.0.1", {"start": v(-117.13, -146.06) * mm, "end": v(-121.75, -146.06) * mm});
            skLineSegment(sketch, "E4.11.0.2", {"start": v(-117.13, -154.13) * mm, "end": v(-117.13, -158.76) * mm});
            skLineSegment(sketch, "E4.11.0.3", {"start": v(-117.13, -141.43) * mm, "end": v(-117.13, -146.06) * mm});
            skLineSegment(sketch, "E4.11.0.4", {"start": v(-121.75, -166.83) * mm, "end": v(-117.13, -166.83) * mm});
            skLineSegment(sketch, "E4.11.0.5", {"start": v(-121.75, -116.03) * mm, "end": v(-117.13, -116.03) * mm});
            skLineSegment(sketch, "E4.11.0.6", {"start": v(-121.75, -120.66) * mm, "end": v(-121.75, -116.03) * mm});
            skLineSegment(sketch, "E4.11.0.7", {"start": v(-121.75, -171.46) * mm, "end": v(-121.75, -166.83) * mm});
            skLineSegment(sketch, "E4.11.0.8", {"start": v(-121.75, -154.13) * mm, "end": v(-117.13, -154.13) * mm});
            skLineSegment(sketch, "E4.11.0.9", {"start": v(-117.13, -133.36) * mm, "end": v(-121.75, -133.36) * mm});
            skLineSegment(sketch, "E4.11.0.10", {"start": v(-117.13, -166.83) * mm, "end": v(-117.13, -171.46) * mm});
            skLineSegment(sketch, "E4.11.0.11", {"start": v(-117.13, -116.03) * mm, "end": v(-117.13, -120.66) * mm});
            skLineSegment(sketch, "E4.11.0.12", {"start": v(-117.13, -171.46) * mm, "end": v(-121.75, -171.46) * mm});
            skLineSegment(sketch, "E4.11.0.13", {"start": v(-117.13, -120.66) * mm, "end": v(-121.75, -120.66) * mm});
            skLineSegment(sketch, "E4.11.0.14", {"start": v(-117.13, -128.73) * mm, "end": v(-117.13, -133.36) * mm});
            skLineSegment(sketch, "E4.11.0.15", {"start": v(-121.75, -128.73) * mm, "end": v(-117.13, -128.73) * mm});
            skLineSegment(sketch, "E4.11.0.16", {"start": v(-121.75, -158.76) * mm, "end": v(-121.75, -154.13) * mm});
            skLineSegment(sketch, "E4.11.0.17", {"start": v(-121.75, -133.36) * mm, "end": v(-121.75, -128.73) * mm});
            skLineSegment(sketch, "E4.11.0.18", {"start": v(-121.75, -146.06) * mm, "end": v(-121.75, -141.43) * mm});
            skLineSegment(sketch, "E4.11.0.19", {"start": v(-117.13, -158.76) * mm, "end": v(-121.75, -158.76) * mm});
            skLineSegment(sketch, "E4.12.0.0", {"start": v(-134.45, -141.43) * mm, "end": v(-129.83, -141.43) * mm});
            skLineSegment(sketch, "E4.12.0.1", {"start": v(-129.83, -146.06) * mm, "end": v(-134.45, -146.06) * mm});
            skLineSegment(sketch, "E4.12.0.2", {"start": v(-129.83, -154.13) * mm, "end": v(-129.83, -158.76) * mm});
            skLineSegment(sketch, "E4.12.0.3", {"start": v(-129.83, -141.43) * mm, "end": v(-129.83, -146.06) * mm});
            skLineSegment(sketch, "E4.12.0.4", {"start": v(-134.45, -166.83) * mm, "end": v(-129.83, -166.83) * mm});
            skLineSegment(sketch, "E4.12.0.5", {"start": v(-134.45, -116.03) * mm, "end": v(-129.83, -116.03) * mm});
            skLineSegment(sketch, "E4.12.0.6", {"start": v(-134.45, -120.66) * mm, "end": v(-134.45, -116.03) * mm});
            skLineSegment(sketch, "E4.12.0.7", {"start": v(-134.45, -171.46) * mm, "end": v(-134.45, -166.83) * mm});
            skLineSegment(sketch, "E4.12.0.8", {"start": v(-134.45, -154.13) * mm, "end": v(-129.83, -154.13) * mm});
            skLineSegment(sketch, "E4.12.0.9", {"start": v(-129.83, -133.36) * mm, "end": v(-134.45, -133.36) * mm});
            skLineSegment(sketch, "E4.12.0.10", {"start": v(-129.83, -166.83) * mm, "end": v(-129.83, -171.46) * mm});
            skLineSegment(sketch, "E4.12.0.11", {"start": v(-129.83, -116.03) * mm, "end": v(-129.83, -120.66) * mm});
            skLineSegment(sketch, "E4.12.0.12", {"start": v(-129.83, -171.46) * mm, "end": v(-134.45, -171.46) * mm});
            skLineSegment(sketch, "E4.12.0.13", {"start": v(-129.83, -120.66) * mm, "end": v(-134.45, -120.66) * mm});
            skLineSegment(sketch, "E4.12.0.14", {"start": v(-129.83, -128.73) * mm, "end": v(-129.83, -133.36) * mm});
            skLineSegment(sketch, "E4.12.0.15", {"start": v(-134.45, -128.73) * mm, "end": v(-129.83, -128.73) * mm});
            skLineSegment(sketch, "E4.12.0.16", {"start": v(-134.45, -158.76) * mm, "end": v(-134.45, -154.13) * mm});
            skLineSegment(sketch, "E4.12.0.17", {"start": v(-134.45, -133.36) * mm, "end": v(-134.45, -128.73) * mm});
            skLineSegment(sketch, "E4.12.0.18", {"start": v(-134.45, -146.06) * mm, "end": v(-134.45, -141.43) * mm});
            skLineSegment(sketch, "E4.12.0.19", {"start": v(-129.83, -158.76) * mm, "end": v(-134.45, -158.76) * mm});
            skLineSegment(sketch, "E4.13.0.0", {"start": v(-147.15, -141.43) * mm, "end": v(-142.53, -141.43) * mm});
            skLineSegment(sketch, "E4.13.0.1", {"start": v(-142.53, -146.06) * mm, "end": v(-147.15, -146.06) * mm});
            skLineSegment(sketch, "E4.13.0.2", {"start": v(-142.53, -154.13) * mm, "end": v(-142.53, -158.76) * mm});
            skLineSegment(sketch, "E4.13.0.3", {"start": v(-142.53, -141.43) * mm, "end": v(-142.53, -146.06) * mm});
            skLineSegment(sketch, "E4.13.0.4", {"start": v(-147.15, -166.83) * mm, "end": v(-142.53, -166.83) * mm});
            skLineSegment(sketch, "E4.13.0.5", {"start": v(-147.15, -116.03) * mm, "end": v(-142.53, -116.03) * mm});
            skLineSegment(sketch, "E4.13.0.6", {"start": v(-147.15, -120.66) * mm, "end": v(-147.15, -116.03) * mm});
            skLineSegment(sketch, "E4.13.0.7", {"start": v(-147.15, -171.46) * mm, "end": v(-147.15, -166.83) * mm});
            skLineSegment(sketch, "E4.13.0.8", {"start": v(-147.15, -154.13) * mm, "end": v(-142.53, -154.13) * mm});
            skLineSegment(sketch, "E4.13.0.9", {"start": v(-142.53, -133.36) * mm, "end": v(-147.15, -133.36) * mm});
            skLineSegment(sketch, "E4.13.0.10", {"start": v(-142.53, -166.83) * mm, "end": v(-142.53, -171.46) * mm});
            skLineSegment(sketch, "E4.13.0.11", {"start": v(-142.53, -116.03) * mm, "end": v(-142.53, -120.66) * mm});
            skLineSegment(sketch, "E4.13.0.12", {"start": v(-142.53, -171.46) * mm, "end": v(-147.15, -171.46) * mm});
            skLineSegment(sketch, "E4.13.0.13", {"start": v(-142.53, -120.66) * mm, "end": v(-147.15, -120.66) * mm});
            skLineSegment(sketch, "E4.13.0.14", {"start": v(-142.53, -128.73) * mm, "end": v(-142.53, -133.36) * mm});
            skLineSegment(sketch, "E4.13.0.15", {"start": v(-147.15, -128.73) * mm, "end": v(-142.53, -128.73) * mm});
            skLineSegment(sketch, "E4.13.0.16", {"start": v(-147.15, -158.76) * mm, "end": v(-147.15, -154.13) * mm});
            skLineSegment(sketch, "E4.13.0.17", {"start": v(-147.15, -133.36) * mm, "end": v(-147.15, -128.73) * mm});
            skLineSegment(sketch, "E4.13.0.18", {"start": v(-147.15, -146.06) * mm, "end": v(-147.15, -141.43) * mm});
            skLineSegment(sketch, "E4.13.0.19", {"start": v(-142.53, -158.76) * mm, "end": v(-147.15, -158.76) * mm});
            skLineSegment(sketch, "E4.14.0.0", {"start": v(-159.85, -141.43) * mm, "end": v(-155.23, -141.43) * mm});
            skLineSegment(sketch, "E4.14.0.1", {"start": v(-155.23, -146.06) * mm, "end": v(-159.85, -146.06) * mm});
            skLineSegment(sketch, "E4.14.0.2", {"start": v(-155.23, -154.13) * mm, "end": v(-155.23, -158.76) * mm});
            skLineSegment(sketch, "E4.14.0.3", {"start": v(-155.23, -141.43) * mm, "end": v(-155.23, -146.06) * mm});
            skLineSegment(sketch, "E4.14.0.4", {"start": v(-159.85, -166.83) * mm, "end": v(-155.23, -166.83) * mm});
            skLineSegment(sketch, "E4.14.0.5", {"start": v(-159.85, -116.03) * mm, "end": v(-155.23, -116.03) * mm});
            skLineSegment(sketch, "E4.14.0.6", {"start": v(-159.85, -120.66) * mm, "end": v(-159.85, -116.03) * mm});
            skLineSegment(sketch, "E4.14.0.7", {"start": v(-159.85, -171.46) * mm, "end": v(-159.85, -166.83) * mm});
            skLineSegment(sketch, "E4.14.0.8", {"start": v(-159.85, -154.13) * mm, "end": v(-155.23, -154.13) * mm});
            skLineSegment(sketch, "E4.14.0.9", {"start": v(-155.23, -133.36) * mm, "end": v(-159.85, -133.36) * mm});
            skLineSegment(sketch, "E4.14.0.10", {"start": v(-155.23, -166.83) * mm, "end": v(-155.23, -171.46) * mm});
            skLineSegment(sketch, "E4.14.0.11", {"start": v(-155.23, -116.03) * mm, "end": v(-155.23, -120.66) * mm});
            skLineSegment(sketch, "E4.14.0.12", {"start": v(-155.23, -171.46) * mm, "end": v(-159.85, -171.46) * mm});
            skLineSegment(sketch, "E4.14.0.13", {"start": v(-155.23, -120.66) * mm, "end": v(-159.85, -120.66) * mm});
            skLineSegment(sketch, "E4.14.0.14", {"start": v(-155.23, -128.73) * mm, "end": v(-155.23, -133.36) * mm});
            skLineSegment(sketch, "E4.14.0.15", {"start": v(-159.85, -128.73) * mm, "end": v(-155.23, -128.73) * mm});
            skLineSegment(sketch, "E4.14.0.16", {"start": v(-159.85, -158.76) * mm, "end": v(-159.85, -154.13) * mm});
            skLineSegment(sketch, "E4.14.0.17", {"start": v(-159.85, -133.36) * mm, "end": v(-159.85, -128.73) * mm});
            skLineSegment(sketch, "E4.14.0.18", {"start": v(-159.85, -146.06) * mm, "end": v(-159.85, -141.43) * mm});
            skLineSegment(sketch, "E4.14.0.19", {"start": v(-155.23, -158.76) * mm, "end": v(-159.85, -158.76) * mm});
            skLineSegment(sketch, "E4.direction1", {"start": v(17.95, -171.46) * mm, "end": v(5.25, -171.46) * mm, "construction": true});
            skLineSegment(sketch, "E5", {"start": v(-206.34, 112.57) * mm, "end": v(-206.34, -175.5) * mm});
            skLineSegment(sketch, "E6", {"start": v(-206.34, -175.5) * mm, "end": v(-196.31, -175.5) * mm});
            skLineSegment(sketch, "E7", {"start": v(-206.34, 112.57) * mm, "end": v(-206.34, 121.25) * mm});
            skLineSegment(sketch, "E8", {"start": v(-206.34, 121.25) * mm, "end": v(55.04, 121.25) * mm});
            skLineSegment(sketch, "E9", {"start": v(55.04, 121.25) * mm, "end": v(55.04, -175.5) * mm});
            skLineSegment(sketch, "E10", {"start": v(55.04, -175.5) * mm, "end": v(45.66, -175.5) * mm});
            skSolve(sketch);
        }
        {
            var Q0;
            Q0=makeQuery(id+"F0.imprint","IMPRINT",FACE,{"disambiguationData":[TD([[makeQuery(id+"F0.imprint","IMPRINT",EDGE,{"derivedFrom":sQuery(id+"F0.wireOp",EDGE,"E0.0.3.0")}),1.0]])]});
            var sketch = newSketch(context, id + "F1", { "sketchPlane" : qUnion([Q0])});
            skLineSegment(sketch, "E11", {"start": v(-95.21, 140.42) * mm, "end": v(57.19, 140.42) * mm});
            skLineSegment(sketch, "E12", {"start": v(-95.21, 140.42) * mm, "end": v(-95.21, 89.62) * mm});
            skLineSegment(sketch, "E13", {"start": v(-95.21, 89.62) * mm, "end": v(57.19, 89.62) * mm});
            skLineSegment(sketch, "E14", {"start": v(57.19, 89.62) * mm, "end": v(57.19, 140.42) * mm});
            skLineSegment(sketch, "E15", {"start": v(57.19, 144.23) * mm, "end": v(61, 144.23) * mm});
            skLineSegment(sketch, "E16", {"start": v(61.22, 144.23) * mm, "end": v(61.22, 85.81) * mm});
            skPoint(sketch, "E16.endSnap0", {"position": v(61.22, 44.94) * mm});
            skLineSegment(sketch, "E17", {"start": v(61.22, 85.81) * mm, "end": v(-98.8, 85.81) * mm});
            skLineSegment(sketch, "E18", {"start": v(-98.8, 85.81) * mm, "end": v(-98.8, 144.23) * mm});
            skLineSegment(sketch, "E19", {"start": v(-98.8, 144.23) * mm, "end": v(61.22, 144.23) * mm});
            skSolve(sketch);
        }
        {
            var Q0;
            Q0 = qSketchRegion(id + "F0", true);
            extrude(context, id + "F2", {"entities" : qUnion([Q0]), "depth" : 3 * mm});
        }
        {
            var Q0;
            Q0 = qSketchRegion(id + "F1", true);
            extrude(context, id + "F3", {"entities" : qUnion([Q0]), "depth" : 31.75 * mm});
        }
        {
            var Q0;
            Q0=makeQuery(id+"F2.opExtrude","CAP_FACE",FACE,{"disambiguationData":[OSD([sQuery(id+"F0.wireOp",EDGE,"e2akh6Oa-UBHa-86Pb-ZkKs-OABukGgOBKLV.right"),sQuery(id+"F0.wireOp",EDGE,"RFzYo0nL-dbGn-g4QQ-aZl6-wjgrSkBCbLW4.bottom"),sQuery(id+"F0.wireOp",EDGE,"RFzYo0nL-dbGn-g4QQ-aZl6-wjgrSkBCbLW4.top"),sQuery(id+"F0.wireOp",EDGE,"RFzYo0nL-dbGn-g4QQ-aZl6-wjgrSkBCbLW4.left"),sQuery(id+"F0.wireOp",EDGE,"RFzYo0nL-dbGn-g4QQ-aZl6-wjgrSkBCbLW4.right"),sQuery(id+"F0.wireOp",EDGE,"7c84c30b-10c3-426a-8278-929d31200ebf.0.1.0"),sQuery(id+"F0.wireOp",EDGE,"7c84c30b-10c3-426a-8278-929d31200ebf.0.1.1"),sQuery(id+"F0.wireOp",EDGE,"7c84c30b-10c3-426a-8278-929d31200ebf.0.1.2"),sQuery(id+"F0.wireOp",EDGE,"7c84c30b-10c3-426a-8278-929d31200ebf.0.1.3"),sQuery(id+"F0.wireOp",EDGE,"7c84c30b-10c3-426a-8278-929d31200ebf.0.2.0"),sQuery(id+"F0.wireOp",EDGE,"7c84c30b-10c3-426a-8278-929d31200ebf.0.2.1"),sQuery(id+"F0.wireOp",EDGE,"7c84c30b-10c3-426a-8278-929d31200ebf.0.2.2"),sQuery(id+"F0.wireOp",EDGE,"7c84c30b-10c3-426a-8278-929d31200ebf.0.2.3"),sQuery(id+"F0.wireOp",EDGE,"7c84c30b-10c3-426a-8278-929d31200ebf.0.3.0"),sQuery(id+"F0.wireOp",EDGE,"7c84c30b-10c3-426a-8278-929d31200ebf.0.3.1"),sQuery(id+"F0.wireOp",EDGE,"7c84c30b-10c3-426a-8278-929d31200ebf.0.3.2"),sQuery(id+"F0.wireOp",EDGE,"7c84c30b-10c3-426a-8278-929d31200ebf.0.3.3"),sQuery(id+"F0.wireOp",EDGE,"7c84c30b-10c3-426a-8278-929d31200ebf.0.4.0"),sQuery(id+"F0.wireOp",EDGE,"7c84c30b-10c3-426a-8278-929d31200ebf.0.4.1"),sQuery(id+"F0.wireOp",EDGE,"7c84c30b-10c3-426a-8278-929d31200ebf.0.4.2"),sQuery(id+"F0.wireOp",EDGE,"7c84c30b-10c3-426a-8278-929d31200ebf.0.4.3"),sQuery(id+"F0.wireOp",EDGE,"7c84c30b-10c3-426a-8278-929d31200ebf.0.5.0"),sQuery(id+"F0.wireOp",EDGE,"7c84c30b-10c3-426a-8278-929d31200ebf.0.5.1"),sQuery(id+"F0.wireOp",EDGE,"7c84c30b-10c3-426a-8278-929d31200ebf.0.5.2"),sQuery(id+"F0.wireOp",EDGE,"7c84c30b-10c3-426a-8278-929d31200ebf.0.5.3"),sQuery(id+"F0.wireOp",EDGE,"7c84c30b-10c3-426a-8278-929d31200ebf.0.6.0"),sQuery(id+"F0.wireOp",EDGE,"7c84c30b-10c3-426a-8278-929d31200ebf.0.6.1"),sQuery(id+"F0.wireOp",EDGE,"7c84c30b-10c3-426a-8278-929d31200ebf.0.6.2"),sQuery(id+"F0.wireOp",EDGE,"7c84c30b-10c3-426a-8278-929d31200ebf.0.6.3"),sQuery(id+"F0.wireOp",EDGE,"7c84c30b-10c3-426a-8278-929d31200ebf.0.7.0"),sQuery(id+"F0.wireOp",EDGE,"7c84c30b-10c3-426a-8278-929d31200ebf.0.7.1"),sQuery(id+"F0.wireOp",EDGE,"7c84c30b-10c3-426a-8278-929d31200ebf.0.7.2"),sQuery(id+"F0.wireOp",EDGE,"7c84c30b-10c3-426a-8278-929d31200ebf.0.7.3"),sQuery(id+"F0.wireOp",EDGE,"7c84c30b-10c3-426a-8278-929d31200ebf.0.8.0"),sQuery(id+"F0.wireOp",EDGE,"7c84c30b-10c3-426a-8278-929d31200ebf.0.8.1"),sQuery(id+"F0.wireOp",EDGE,"7c84c30b-10c3-426a-8278-929d31200ebf.0.8.2"),sQuery(id+"F0.wireOp",EDGE,"7c84c30b-10c3-426a-8278-929d31200ebf.0.8.3"),sQuery(id+"F0.wireOp",EDGE,"7c84c30b-10c3-426a-8278-929d31200ebf.0.9.0"),sQuery(id+"F0.wireOp",EDGE,"7c84c30b-10c3-426a-8278-929d31200ebf.0.9.1"),sQuery(id+"F0.wireOp",EDGE,"7c84c30b-10c3-426a-8278-929d31200ebf.0.9.2"),sQuery(id+"F0.wireOp",EDGE,"7c84c30b-10c3-426a-8278-929d31200ebf.0.9.3"),sQuery(id+"F0.wireOp",EDGE,"7c84c30b-10c3-426a-8278-929d31200ebf.0.10.0"),sQuery(id+"F0.wireOp",EDGE,"7c84c30b-10c3-426a-8278-929d31200ebf.0.10.1"),sQuery(id+"F0.wireOp",EDGE,"7c84c30b-10c3-426a-8278-929d31200ebf.0.10.2"),sQuery(id+"F0.wireOp",EDGE,"7c84c30b-10c3-426a-8278-929d31200ebf.0.10.3"),sQuery(id+"F0.wireOp",EDGE,"7c84c30b-10c3-426a-8278-929d31200ebf.0.11.0"),sQuery(id+"F0.wireOp",EDGE,"7c84c30b-10c3-426a-8278-929d31200ebf.0.11.1"),sQuery(id+"F0.wireOp",EDGE,"7c84c30b-10c3-426a-8278-929d31200ebf.0.11.2"),sQuery(id+"F0.wireOp",EDGE,"7c84c30b-10c3-426a-8278-929d31200ebf.0.11.3"),sQuery(id+"F0.wireOp",EDGE,"7c84c30b-10c3-426a-8278-929d31200ebf.0.12.0"),sQuery(id+"F0.wireOp",EDGE,"7c84c30b-10c3-426a-8278-929d31200ebf.0.12.1"),sQuery(id+"F0.wireOp",EDGE,"7c84c30b-10c3-426a-8278-929d31200ebf.0.12.2"),sQuery(id+"F0.wireOp",EDGE,"7c84c30b-10c3-426a-8278-929d31200ebf.0.12.3"),sQuery(id+"F0.wireOp",EDGE,"7c84c30b-10c3-426a-8278-929d31200ebf.0.13.0"),sQuery(id+"F0.wireOp",EDGE,"7c84c30b-10c3-426a-8278-929d31200ebf.0.13.1"),sQuery(id+"F0.wireOp",EDGE,"7c84c30b-10c3-426a-8278-929d31200ebf.0.13.2"),sQuery(id+"F0.wireOp",EDGE,"7c84c30b-10c3-426a-8278-929d31200ebf.0.13.3"),sQuery(id+"F0.wireOp",EDGE,"7c84c30b-10c3-426a-8278-929d31200ebf.0.14.0"),sQuery(id+"F0.wireOp",EDGE,"7c84c30b-10c3-426a-8278-929d31200ebf.0.14.1"),sQuery(id+"F0.wireOp",EDGE,"7c84c30b-10c3-426a-8278-929d31200ebf.0.14.2"),sQuery(id+"F0.wireOp",EDGE,"7c84c30b-10c3-426a-8278-929d31200ebf.0.14.3"),sQuery(id+"F0.wireOp",EDGE,"7c84c30b-10c3-426a-8278-929d31200ebf.0.15.0"),sQuery(id+"F0.wireOp",EDGE,"7c84c30b-10c3-426a-8278-929d31200ebf.0.15.1"),sQuery(id+"F0.wireOp",EDGE,"7c84c30b-10c3-426a-8278-929d31200ebf.0.15.2"),sQuery(id+"F0.wireOp",EDGE,"7c84c30b-10c3-426a-8278-929d31200ebf.0.15.3"),sQuery(id+"F0.wireOp",EDGE,"7c84c30b-10c3-426a-8278-929d31200ebf.0.16.0"),sQuery(id+"F0.wireOp",EDGE,"7c84c30b-10c3-426a-8278-929d31200ebf.0.16.1"),sQuery(id+"F0.wireOp",EDGE,"7c84c30b-10c3-426a-8278-929d31200ebf.0.16.2"),sQuery(id+"F0.wireOp",EDGE,"7c84c30b-10c3-426a-8278-929d31200ebf.0.16.3"),sQuery(id+"F0.wireOp",EDGE,"7c84c30b-10c3-426a-8278-929d31200ebf.0.17.0"),sQuery(id+"F0.wireOp",EDGE,"7c84c30b-10c3-426a-8278-929d31200ebf.0.17.1"),sQuery(id+"F0.wireOp",EDGE,"7c84c30b-10c3-426a-8278-929d31200ebf.0.17.2"),sQuery(id+"F0.wireOp",EDGE,"7c84c30b-10c3-426a-8278-929d31200ebf.0.17.3"),sQuery(id+"F0.wireOp",EDGE,"7c84c30b-10c3-426a-8278-929d31200ebf.0.18.0"),sQuery(id+"F0.wireOp",EDGE,"7c84c30b-10c3-426a-8278-929d31200ebf.0.18.1"),sQuery(id+"F0.wireOp",EDGE,"7c84c30b-10c3-426a-8278-929d31200ebf.0.18.2"),sQuery(id+"F0.wireOp",EDGE,"7c84c30b-10c3-426a-8278-929d31200ebf.0.18.3"),sQuery(id+"F0.wireOp",EDGE,"7c84c30b-10c3-426a-8278-929d31200ebf.0.19.0"),sQuery(id+"F0.wireOp",EDGE,"7c84c30b-10c3-426a-8278-929d31200ebf.0.19.1"),sQuery(id+"F0.wireOp",EDGE,"7c84c30b-10c3-426a-8278-929d31200ebf.0.19.2"),sQuery(id+"F0.wireOp",EDGE,"7c84c30b-10c3-426a-8278-929d31200ebf.0.19.3"),sQuery(id+"F0.wireOp",EDGE,"7c84c30b-10c3-426a-8278-929d31200ebf.0.20.0"),sQuery(id+"F0.wireOp",EDGE,"7c84c30b-10c3-426a-8278-929d31200ebf.0.20.1"),sQuery(id+"F0.wireOp",EDGE,"7c84c30b-10c3-426a-8278-929d31200ebf.0.20.2"),sQuery(id+"F0.wireOp",EDGE,"7c84c30b-10c3-426a-8278-929d31200ebf.0.20.3"),sQuery(id+"F0.wireOp",EDGE,"7c84c30b-10c3-426a-8278-929d31200ebf.0.21.0"),sQuery(id+"F0.wireOp",EDGE,"7c84c30b-10c3-426a-8278-929d31200ebf.0.21.1"),sQuery(id+"F0.wireOp",EDGE,"7c84c30b-10c3-426a-8278-929d31200ebf.0.21.2"),sQuery(id+"F0.wireOp",EDGE,"7c84c30b-10c3-426a-8278-929d31200ebf.0.21.3"),sQuery(id+"F0.wireOp",EDGE,"7c84c30b-10c3-426a-8278-929d31200ebf.0.22.0"),sQuery(id+"F0.wireOp",EDGE,"7c84c30b-10c3-426a-8278-929d31200ebf.0.22.1"),sQuery(id+"F0.wireOp",EDGE,"7c84c30b-10c3-426a-8278-929d31200ebf.0.22.2"),sQuery(id+"F0.wireOp",EDGE,"7c84c30b-10c3-426a-8278-929d31200ebf.0.22.3"),sQuery(id+"F0.wireOp",EDGE,"7c84c30b-10c3-426a-8278-929d31200ebf.0.23.0"),sQuery(id+"F0.wireOp",EDGE,"7c84c30b-10c3-426a-8278-929d31200ebf.0.23.1"),sQuery(id+"F0.wireOp",EDGE,"7c84c30b-10c3-426a-8278-929d31200ebf.0.23.2"),sQuery(id+"F0.wireOp",EDGE,"7c84c30b-10c3-426a-8278-929d31200ebf.0.23.3"),sQuery(id+"F0.wireOp",EDGE,"7c84c30b-10c3-426a-8278-929d31200ebf.0.24.0"),sQuery(id+"F0.wireOp",EDGE,"7c84c30b-10c3-426a-8278-929d31200ebf.0.24.1"),sQuery(id+"F0.wireOp",EDGE,"7c84c30b-10c3-426a-8278-929d31200ebf.0.24.2"),sQuery(id+"F0.wireOp",EDGE,"7c84c30b-10c3-426a-8278-929d31200ebf.0.24.3"),sQuery(id+"F0.wireOp",EDGE,"7c84c30b-10c3-426a-8278-929d31200ebf.0.25.0"),sQuery(id+"F0.wireOp",EDGE,"7c84c30b-10c3-426a-8278-929d31200ebf.0.25.1"),sQuery(id+"F0.wireOp",EDGE,"7c84c30b-10c3-426a-8278-929d31200ebf.0.25.2"),sQuery(id+"F0.wireOp",EDGE,"7c84c30b-10c3-426a-8278-929d31200ebf.0.25.3"),sQuery(id+"F0.wireOp",EDGE,"7c84c30b-10c3-426a-8278-929d31200ebf.1.0.0"),sQuery(id+"F0.wireOp",EDGE,"7c84c30b-10c3-426a-8278-929d31200ebf.1.0.1"),sQuery(id+"F0.wireOp",EDGE,"7c84c30b-10c3-426a-8278-929d31200ebf.1.0.2"),sQuery(id+"F0.wireOp",EDGE,"7c84c30b-10c3-426a-8278-929d31200ebf.1.0.3"),sQuery(id+"F0.wireOp",EDGE,"7c84c30b-10c3-426a-8278-929d31200ebf.1.1.0"),sQuery(id+"F0.wireOp",EDGE,"7c84c30b-10c3-426a-8278-929d31200ebf.1.1.1"),sQuery(id+"F0.wireOp",EDGE,"7c84c30b-10c3-426a-8278-929d31200ebf.1.1.2"),sQuery(id+"F0.wireOp",EDGE,"7c84c30b-10c3-426a-8278-929d31200ebf.1.1.3"),sQuery(id+"F0.wireOp",EDGE,"7c84c30b-10c3-426a-8278-929d31200ebf.1.2.0"),sQuery(id+"F0.wireOp",EDGE,"7c84c30b-10c3-426a-8278-929d31200ebf.1.2.1"),sQuery(id+"F0.wireOp",EDGE,"7c84c30b-10c3-426a-8278-929d31200ebf.1.2.2"),sQuery(id+"F0.wireOp",EDGE,"7c84c30b-10c3-426a-8278-929d31200ebf.1.2.3"),sQuery(id+"F0.wireOp",EDGE,"7c84c30b-10c3-426a-8278-929d31200ebf.1.3.0"),sQuery(id+"F0.wireOp",EDGE,"7c84c30b-10c3-426a-8278-929d31200ebf.1.3.1"),sQuery(id+"F0.wireOp",EDGE,"7c84c30b-10c3-426a-8278-929d31200ebf.1.3.2"),sQuery(id+"F0.wireOp",EDGE,"7c84c30b-10c3-426a-8278-929d31200ebf.1.3.3"),sQuery(id+"F0.wireOp",EDGE,"7c84c30b-10c3-426a-8278-929d31200ebf.1.4.0"),sQuery(id+"F0.wireOp",EDGE,"7c84c30b-10c3-426a-8278-929d31200ebf.1.4.1"),sQuery(id+"F0.wireOp",EDGE,"7c84c30b-10c3-426a-8278-929d31200ebf.1.4.2"),sQuery(id+"F0.wireOp",EDGE,"7c84c30b-10c3-426a-8278-929d31200ebf.1.4.3"),sQuery(id+"F0.wireOp",EDGE,"7c84c30b-10c3-426a-8278-929d31200ebf.1.5.0"),sQuery(id+"F0.wireOp",EDGE,"7c84c30b-10c3-426a-8278-929d31200ebf.1.5.1"),sQuery(id+"F0.wireOp",EDGE,"7c84c30b-10c3-426a-8278-929d31200ebf.1.5.2"),sQuery(id+"F0.wireOp",EDGE,"7c84c30b-10c3-426a-8278-929d31200ebf.1.5.3"),sQuery(id+"F0.wireOp",EDGE,"7c84c30b-10c3-426a-8278-929d31200ebf.1.6.0"),sQuery(id+"F0.wireOp",EDGE,"7c84c30b-10c3-426a-8278-929d31200ebf.1.6.1"),sQuery(id+"F0.wireOp",EDGE,"7c84c30b-10c3-426a-8278-929d31200ebf.1.6.2"),sQuery(id+"F0.wireOp",EDGE,"7c84c30b-10c3-426a-8278-929d31200ebf.1.6.3"),sQuery(id+"F0.wireOp",EDGE,"7c84c30b-10c3-426a-8278-929d31200ebf.1.7.0"),sQuery(id+"F0.wireOp",EDGE,"7c84c30b-10c3-426a-8278-929d31200ebf.1.7.1"),sQuery(id+"F0.wireOp",EDGE,"7c84c30b-10c3-426a-8278-929d31200ebf.1.7.2"),sQuery(id+"F0.wireOp",EDGE,"7c84c30b-10c3-426a-8278-929d31200ebf.1.7.3"),sQuery(id+"F0.wireOp",EDGE,"7c84c30b-10c3-426a-8278-929d31200ebf.1.8.0"),sQuery(id+"F0.wireOp",EDGE,"7c84c30b-10c3-426a-8278-929d31200ebf.1.8.1"),sQuery(id+"F0.wireOp",EDGE,"7c84c30b-10c3-426a-8278-929d31200ebf.1.8.2"),sQuery(id+"F0.wireOp",EDGE,"7c84c30b-10c3-426a-8278-929d31200ebf.1.8.3"),sQuery(id+"F0.wireOp",EDGE,"7c84c30b-10c3-426a-8278-929d31200ebf.1.9.0"),sQuery(id+"F0.wireOp",EDGE,"7c84c30b-10c3-426a-8278-929d31200ebf.1.9.1"),sQuery(id+"F0.wireOp",EDGE,"7c84c30b-10c3-426a-8278-929d31200ebf.1.9.2"),sQuery(id+"F0.wireOp",EDGE,"7c84c30b-10c3-426a-8278-929d31200ebf.1.9.3"),sQuery(id+"F0.wireOp",EDGE,"7c84c30b-10c3-426a-8278-929d31200ebf.1.10.0"),sQuery(id+"F0.wireOp",EDGE,"7c84c30b-10c3-426a-8278-929d31200ebf.1.10.1"),sQuery(id+"F0.wireOp",EDGE,"7c84c30b-10c3-426a-8278-929d31200ebf.1.10.2"),sQuery(id+"F0.wireOp",EDGE,"7c84c30b-10c3-426a-8278-929d31200ebf.1.10.3"),sQuery(id+"F0.wireOp",EDGE,"7c84c30b-10c3-426a-8278-929d31200ebf.1.11.0"),sQuery(id+"F0.wireOp",EDGE,"7c84c30b-10c3-426a-8278-929d31200ebf.1.11.1"),sQuery(id+"F0.wireOp",EDGE,"7c84c30b-10c3-426a-8278-929d31200ebf.1.11.2"),sQuery(id+"F0.wireOp",EDGE,"7c84c30b-10c3-426a-8278-929d31200ebf.1.11.3"),sQuery(id+"F0.wireOp",EDGE,"7c84c30b-10c3-426a-8278-929d31200ebf.1.12.0"),sQuery(id+"F0.wireOp",EDGE,"7c84c30b-10c3-426a-8278-929d31200ebf.1.12.1"),sQuery(id+"F0.wireOp",EDGE,"7c84c30b-10c3-426a-8278-929d31200ebf.1.12.2"),sQuery(id+"F0.wireOp",EDGE,"7c84c30b-10c3-426a-8278-929d31200ebf.1.12.3"),sQuery(id+"F0.wireOp",EDGE,"7c84c30b-10c3-426a-8278-929d31200ebf.1.13.0"),sQuery(id+"F0.wireOp",EDGE,"7c84c30b-10c3-426a-8278-929d31200ebf.1.13.1"),sQuery(id+"F0.wireOp",EDGE,"7c84c30b-10c3-426a-8278-929d31200ebf.1.13.2"),sQuery(id+"F0.wireOp",EDGE,"7c84c30b-10c3-426a-8278-929d31200ebf.1.13.3"),sQuery(id+"F0.wireOp",EDGE,"7c84c30b-10c3-426a-8278-929d31200ebf.1.14.0"),sQuery(id+"F0.wireOp",EDGE,"7c84c30b-10c3-426a-8278-929d31200ebf.1.14.1"),sQuery(id+"F0.wireOp",EDGE,"7c84c30b-10c3-426a-8278-929d31200ebf.1.14.2"),sQuery(id+"F0.wireOp",EDGE,"7c84c30b-10c3-426a-8278-929d31200ebf.1.14.3"),sQuery(id+"F0.wireOp",EDGE,"7c84c30b-10c3-426a-8278-929d31200ebf.1.15.0"),sQuery(id+"F0.wireOp",EDGE,"7c84c30b-10c3-426a-8278-929d31200ebf.1.15.1"),sQuery(id+"F0.wireOp",EDGE,"7c84c30b-10c3-426a-8278-929d31200ebf.1.15.2"),sQuery(id+"F0.wireOp",EDGE,"7c84c30b-10c3-426a-8278-929d31200ebf.1.15.3"),sQuery(id+"F0.wireOp",EDGE,"7c84c30b-10c3-426a-8278-929d31200ebf.1.16.0"),sQuery(id+"F0.wireOp",EDGE,"7c84c30b-10c3-426a-8278-929d31200ebf.1.16.1"),sQuery(id+"F0.wireOp",EDGE,"7c84c30b-10c3-426a-8278-929d31200ebf.1.16.2"),sQuery(id+"F0.wireOp",EDGE,"7c84c30b-10c3-426a-8278-929d31200ebf.1.16.3"),sQuery(id+"F0.wireOp",EDGE,"7c84c30b-10c3-426a-8278-929d31200ebf.1.17.0"),sQuery(id+"F0.wireOp",EDGE,"7c84c30b-10c3-426a-8278-929d31200ebf.1.17.1"),sQuery(id+"F0.wireOp",EDGE,"7c84c30b-10c3-426a-8278-929d31200ebf.1.17.2"),sQuery(id+"F0.wireOp",EDGE,"7c84c30b-10c3-426a-8278-929d31200ebf.1.17.3"),sQuery(id+"F0.wireOp",EDGE,"7c84c30b-10c3-426a-8278-929d31200ebf.1.18.0"),sQuery(id+"F0.wireOp",EDGE,"7c84c30b-10c3-426a-8278-929d31200ebf.1.18.1"),sQuery(id+"F0.wireOp",EDGE,"7c84c30b-10c3-426a-8278-929d31200ebf.1.18.2"),sQuery(id+"F0.wireOp",EDGE,"7c84c30b-10c3-426a-8278-929d31200ebf.1.18.3"),sQuery(id+"F0.wireOp",EDGE,"7c84c30b-10c3-426a-8278-929d31200ebf.1.19.0"),sQuery(id+"F0.wireOp",EDGE,"7c84c30b-10c3-426a-8278-929d31200ebf.1.19.1"),sQuery(id+"F0.wireOp",EDGE,"7c84c30b-10c3-426a-8278-929d31200ebf.1.19.2"),sQuery(id+"F0.wireOp",EDGE,"7c84c30b-10c3-426a-8278-929d31200ebf.1.19.3"),sQuery(id+"F0.wireOp",EDGE,"7c84c30b-10c3-426a-8278-929d31200ebf.1.20.0"),sQuery(id+"F0.wireOp",EDGE,"7c84c30b-10c3-426a-8278-929d31200ebf.1.20.1"),sQuery(id+"F0.wireOp",EDGE,"7c84c30b-10c3-426a-8278-929d31200ebf.1.20.2"),sQuery(id+"F0.wireOp",EDGE,"7c84c30b-10c3-426a-8278-929d31200ebf.1.20.3"),sQuery(id+"F0.wireOp",EDGE,"7c84c30b-10c3-426a-8278-929d31200ebf.1.21.0"),sQuery(id+"F0.wireOp",EDGE,"7c84c30b-10c3-426a-8278-929d31200ebf.1.21.1"),sQuery(id+"F0.wireOp",EDGE,"7c84c30b-10c3-426a-8278-929d31200ebf.1.21.2"),sQuery(id+"F0.wireOp",EDGE,"7c84c30b-10c3-426a-8278-929d31200ebf.1.21.3"),sQuery(id+"F0.wireOp",EDGE,"7c84c30b-10c3-426a-8278-929d31200ebf.1.22.0"),sQuery(id+"F0.wireOp",EDGE,"7c84c30b-10c3-426a-8278-929d31200ebf.1.22.1"),sQuery(id+"F0.wireOp",EDGE,"7c84c30b-10c3-426a-8278-929d31200ebf.1.22.2"),sQuery(id+"F0.wireOp",EDGE,"7c84c30b-10c3-426a-8278-929d31200ebf.1.22.3"),sQuery(id+"F0.wireOp",EDGE,"7c84c30b-10c3-426a-8278-929d31200ebf.1.23.0"),sQuery(id+"F0.wireOp",EDGE,"7c84c30b-10c3-426a-8278-929d31200ebf.1.23.1"),sQuery(id+"F0.wireOp",EDGE,"7c84c30b-10c3-426a-8278-929d31200ebf.1.23.2"),sQuery(id+"F0.wireOp",EDGE,"7c84c30b-10c3-426a-8278-929d31200ebf.1.23.3"),sQuery(id+"F0.wireOp",EDGE,"7c84c30b-10c3-426a-8278-929d31200ebf.1.24.0"),sQuery(id+"F0.wireOp",EDGE,"7c84c30b-10c3-426a-8278-929d31200ebf.1.24.1"),sQuery(id+"F0.wireOp",EDGE,"7c84c30b-10c3-426a-8278-929d31200ebf.1.24.2"),sQuery(id+"F0.wireOp",EDGE,"7c84c30b-10c3-426a-8278-929d31200ebf.1.24.3"),sQuery(id+"F0.wireOp",EDGE,"7c84c30b-10c3-426a-8278-929d31200ebf.1.25.0"),sQuery(id+"F0.wireOp",EDGE,"7c84c30b-10c3-426a-8278-929d31200ebf.1.25.1"),sQuery(id+"F0.wireOp",EDGE,"7c84c30b-10c3-426a-8278-929d31200ebf.1.25.2"),sQuery(id+"F0.wireOp",EDGE,"7c84c30b-10c3-426a-8278-929d31200ebf.1.25.3"),sQuery(id+"F0.wireOp",EDGE,"7c84c30b-10c3-426a-8278-929d31200ebf.2.0.0"),sQuery(id+"F0.wireOp",EDGE,"7c84c30b-10c3-426a-8278-929d31200ebf.2.0.1"),sQuery(id+"F0.wireOp",EDGE,"7c84c30b-10c3-426a-8278-929d31200ebf.2.0.2"),sQuery(id+"F0.wireOp",EDGE,"7c84c30b-10c3-426a-8278-929d31200ebf.2.0.3"),sQuery(id+"F0.wireOp",EDGE,"7c84c30b-10c3-426a-8278-929d31200ebf.2.1.0"),sQuery(id+"F0.wireOp",EDGE,"7c84c30b-10c3-426a-8278-929d31200ebf.2.1.1"),sQuery(id+"F0.wireOp",EDGE,"7c84c30b-10c3-426a-8278-929d31200ebf.2.1.2"),sQuery(id+"F0.wireOp",EDGE,"7c84c30b-10c3-426a-8278-929d31200ebf.2.1.3"),sQuery(id+"F0.wireOp",EDGE,"7c84c30b-10c3-426a-8278-929d31200ebf.2.2.0"),sQuery(id+"F0.wireOp",EDGE,"7c84c30b-10c3-426a-8278-929d31200ebf.2.2.1"),sQuery(id+"F0.wireOp",EDGE,"7c84c30b-10c3-426a-8278-929d31200ebf.2.2.2"),sQuery(id+"F0.wireOp",EDGE,"7c84c30b-10c3-426a-8278-929d31200ebf.2.2.3"),sQuery(id+"F0.wireOp",EDGE,"7c84c30b-10c3-426a-8278-929d31200ebf.2.3.0"),sQuery(id+"F0.wireOp",EDGE,"7c84c30b-10c3-426a-8278-929d31200ebf.2.3.1"),sQuery(id+"F0.wireOp",EDGE,"7c84c30b-10c3-426a-8278-929d31200ebf.2.3.2"),sQuery(id+"F0.wireOp",EDGE,"7c84c30b-10c3-426a-8278-929d31200ebf.2.3.3"),sQuery(id+"F0.wireOp",EDGE,"7c84c30b-10c3-426a-8278-929d31200ebf.2.4.0"),sQuery(id+"F0.wireOp",EDGE,"7c84c30b-10c3-426a-8278-929d31200ebf.2.4.1"),sQuery(id+"F0.wireOp",EDGE,"7c84c30b-10c3-426a-8278-929d31200ebf.2.4.2"),sQuery(id+"F0.wireOp",EDGE,"7c84c30b-10c3-426a-8278-929d31200ebf.2.4.3"),sQuery(id+"F0.wireOp",EDGE,"7c84c30b-10c3-426a-8278-929d31200ebf.2.5.0"),sQuery(id+"F0.wireOp",EDGE,"7c84c30b-10c3-426a-8278-929d31200ebf.2.5.1"),sQuery(id+"F0.wireOp",EDGE,"7c84c30b-10c3-426a-8278-929d31200ebf.2.5.2"),sQuery(id+"F0.wireOp",EDGE,"7c84c30b-10c3-426a-8278-929d31200ebf.2.5.3"),sQuery(id+"F0.wireOp",EDGE,"7c84c30b-10c3-426a-8278-929d31200ebf.2.6.0"),sQuery(id+"F0.wireOp",EDGE,"7c84c30b-10c3-426a-8278-929d31200ebf.2.6.1"),sQuery(id+"F0.wireOp",EDGE,"7c84c30b-10c3-426a-8278-929d31200ebf.2.6.2"),sQuery(id+"F0.wireOp",EDGE,"7c84c30b-10c3-426a-8278-929d31200ebf.2.6.3"),sQuery(id+"F0.wireOp",EDGE,"7c84c30b-10c3-426a-8278-929d31200ebf.2.7.0"),sQuery(id+"F0.wireOp",EDGE,"7c84c30b-10c3-426a-8278-929d31200ebf.2.7.1"),sQuery(id+"F0.wireOp",EDGE,"7c84c30b-10c3-426a-8278-929d31200ebf.2.7.2"),sQuery(id+"F0.wireOp",EDGE,"7c84c30b-10c3-426a-8278-929d31200ebf.2.7.3"),sQuery(id+"F0.wireOp",EDGE,"7c84c30b-10c3-426a-8278-929d31200ebf.2.8.0"),sQuery(id+"F0.wireOp",EDGE,"7c84c30b-10c3-426a-8278-929d31200ebf.2.8.1"),sQuery(id+"F0.wireOp",EDGE,"7c84c30b-10c3-426a-8278-929d31200ebf.2.8.2"),sQuery(id+"F0.wireOp",EDGE,"7c84c30b-10c3-426a-8278-929d31200ebf.2.8.3"),sQuery(id+"F0.wireOp",EDGE,"7c84c30b-10c3-426a-8278-929d31200ebf.2.9.0"),sQuery(id+"F0.wireOp",EDGE,"7c84c30b-10c3-426a-8278-929d31200ebf.2.9.1"),sQuery(id+"F0.wireOp",EDGE,"7c84c30b-10c3-426a-8278-929d31200ebf.2.9.2"),sQuery(id+"F0.wireOp",EDGE,"7c84c30b-10c3-426a-8278-929d31200ebf.2.9.3"),sQuery(id+"F0.wireOp",EDGE,"7c84c30b-10c3-426a-8278-929d31200ebf.2.10.0"),sQuery(id+"F0.wireOp",EDGE,"7c84c30b-10c3-426a-8278-929d31200ebf.2.10.1"),sQuery(id+"F0.wireOp",EDGE,"7c84c30b-10c3-426a-8278-929d31200ebf.2.10.2"),sQuery(id+"F0.wireOp",EDGE,"7c84c30b-10c3-426a-8278-929d31200ebf.2.10.3"),sQuery(id+"F0.wireOp",EDGE,"7c84c30b-10c3-426a-8278-929d31200ebf.2.11.0"),sQuery(id+"F0.wireOp",EDGE,"7c84c30b-10c3-426a-8278-929d31200ebf.2.11.1"),sQuery(id+"F0.wireOp",EDGE,"7c84c30b-10c3-426a-8278-929d31200ebf.2.11.2"),sQuery(id+"F0.wireOp",EDGE,"7c84c30b-10c3-426a-8278-929d31200ebf.2.11.3"),sQuery(id+"F0.wireOp",EDGE,"7c84c30b-10c3-426a-8278-929d31200ebf.2.12.0"),sQuery(id+"F0.wireOp",EDGE,"7c84c30b-10c3-426a-8278-929d31200ebf.2.12.1"),sQuery(id+"F0.wireOp",EDGE,"7c84c30b-10c3-426a-8278-929d31200ebf.2.12.2"),sQuery(id+"F0.wireOp",EDGE,"7c84c30b-10c3-426a-8278-929d31200ebf.2.12.3"),sQuery(id+"F0.wireOp",EDGE,"7c84c30b-10c3-426a-8278-929d31200ebf.2.13.0"),sQuery(id+"F0.wireOp",EDGE,"7c84c30b-10c3-426a-8278-929d31200ebf.2.13.1"),sQuery(id+"F0.wireOp",EDGE,"7c84c30b-10c3-426a-8278-929d31200ebf.2.13.2"),sQuery(id+"F0.wireOp",EDGE,"7c84c30b-10c3-426a-8278-929d31200ebf.2.13.3"),sQuery(id+"F0.wireOp",EDGE,"7c84c30b-10c3-426a-8278-929d31200ebf.2.14.0"),sQuery(id+"F0.wireOp",EDGE,"7c84c30b-10c3-426a-8278-929d31200ebf.2.14.1"),sQuery(id+"F0.wireOp",EDGE,"7c84c30b-10c3-426a-8278-929d31200ebf.2.14.2"),sQuery(id+"F0.wireOp",EDGE,"7c84c30b-10c3-426a-8278-929d31200ebf.2.14.3"),sQuery(id+"F0.wireOp",EDGE,"7c84c30b-10c3-426a-8278-929d31200ebf.2.15.0"),sQuery(id+"F0.wireOp",EDGE,"7c84c30b-10c3-426a-8278-929d31200ebf.2.15.1"),sQuery(id+"F0.wireOp",EDGE,"7c84c30b-10c3-426a-8278-929d31200ebf.2.15.2"),sQuery(id+"F0.wireOp",EDGE,"7c84c30b-10c3-426a-8278-929d31200ebf.2.15.3"),sQuery(id+"F0.wireOp",EDGE,"7c84c30b-10c3-426a-8278-929d31200ebf.2.16.0"),sQuery(id+"F0.wireOp",EDGE,"7c84c30b-10c3-426a-8278-929d31200ebf.2.16.1"),sQuery(id+"F0.wireOp",EDGE,"7c84c30b-10c3-426a-8278-929d31200ebf.2.16.2"),sQuery(id+"F0.wireOp",EDGE,"7c84c30b-10c3-426a-8278-929d31200ebf.2.16.3"),sQuery(id+"F0.wireOp",EDGE,"7c84c30b-10c3-426a-8278-929d31200ebf.2.17.0"),sQuery(id+"F0.wireOp",EDGE,"7c84c30b-10c3-426a-8278-929d31200ebf.2.17.1"),sQuery(id+"F0.wireOp",EDGE,"7c84c30b-10c3-426a-8278-929d31200ebf.2.17.2"),sQuery(id+"F0.wireOp",EDGE,"7c84c30b-10c3-426a-8278-929d31200ebf.2.17.3"),sQuery(id+"F0.wireOp",EDGE,"7c84c30b-10c3-426a-8278-929d31200ebf.2.18.0"),sQuery(id+"F0.wireOp",EDGE,"7c84c30b-10c3-426a-8278-929d31200ebf.2.18.1"),sQuery(id+"F0.wireOp",EDGE,"7c84c30b-10c3-426a-8278-929d31200ebf.2.18.2"),sQuery(id+"F0.wireOp",EDGE,"7c84c30b-10c3-426a-8278-929d31200ebf.2.18.3"),sQuery(id+"F0.wireOp",EDGE,"7c84c30b-10c3-426a-8278-929d31200ebf.2.19.0"),sQuery(id+"F0.wireOp",EDGE,"7c84c30b-10c3-426a-8278-929d31200ebf.2.19.1"),sQuery(id+"F0.wireOp",EDGE,"7c84c30b-10c3-426a-8278-929d31200ebf.2.19.2"),sQuery(id+"F0.wireOp",EDGE,"7c84c30b-10c3-426a-8278-929d31200ebf.2.19.3"),sQuery(id+"F0.wireOp",EDGE,"7c84c30b-10c3-426a-8278-929d31200ebf.2.20.0"),sQuery(id+"F0.wireOp",EDGE,"7c84c30b-10c3-426a-8278-929d31200ebf.2.20.1"),sQuery(id+"F0.wireOp",EDGE,"7c84c30b-10c3-426a-8278-929d31200ebf.2.20.2"),sQuery(id+"F0.wireOp",EDGE,"7c84c30b-10c3-426a-8278-929d31200ebf.2.20.3"),sQuery(id+"F0.wireOp",EDGE,"7c84c30b-10c3-426a-8278-929d31200ebf.2.21.0"),sQuery(id+"F0.wireOp",EDGE,"7c84c30b-10c3-426a-8278-929d31200ebf.2.21.1"),sQuery(id+"F0.wireOp",EDGE,"7c84c30b-10c3-426a-8278-929d31200ebf.2.21.2"),sQuery(id+"F0.wireOp",EDGE,"7c84c30b-10c3-426a-8278-929d31200ebf.2.21.3"),sQuery(id+"F0.wireOp",EDGE,"7c84c30b-10c3-426a-8278-929d31200ebf.2.22.0"),sQuery(id+"F0.wireOp",EDGE,"7c84c30b-10c3-426a-8278-929d31200ebf.2.22.1"),sQuery(id+"F0.wireOp",EDGE,"7c84c30b-10c3-426a-8278-929d31200ebf.2.22.2"),sQuery(id+"F0.wireOp",EDGE,"7c84c30b-10c3-426a-8278-929d31200ebf.2.22.3"),sQuery(id+"F0.wireOp",EDGE,"7c84c30b-10c3-426a-8278-929d31200ebf.2.23.0"),sQuery(id+"F0.wireOp",EDGE,"7c84c30b-10c3-426a-8278-929d31200ebf.2.23.1"),sQuery(id+"F0.wireOp",EDGE,"7c84c30b-10c3-426a-8278-929d31200ebf.2.23.2"),sQuery(id+"F0.wireOp",EDGE,"7c84c30b-10c3-426a-8278-929d31200ebf.2.23.3"),sQuery(id+"F0.wireOp",EDGE,"7c84c30b-10c3-426a-8278-929d31200ebf.2.24.0"),sQuery(id+"F0.wireOp",EDGE,"7c84c30b-10c3-426a-8278-929d31200ebf.2.24.1"),sQuery(id+"F0.wireOp",EDGE,"7c84c30b-10c3-426a-8278-929d31200ebf.2.24.2"),sQuery(id+"F0.wireOp",EDGE,"7c84c30b-10c3-426a-8278-929d31200ebf.2.24.3"),sQuery(id+"F0.wireOp",EDGE,"7c84c30b-10c3-426a-8278-929d31200ebf.2.25.0"),sQuery(id+"F0.wireOp",EDGE,"7c84c30b-10c3-426a-8278-929d31200ebf.2.25.1"),sQuery(id+"F0.wireOp",EDGE,"7c84c30b-10c3-426a-8278-929d31200ebf.2.25.2"),sQuery(id+"F0.wireOp",EDGE,"7c84c30b-10c3-426a-8278-929d31200ebf.2.25.3"),sQuery(id+"F0.wireOp",EDGE,"DqMKkSLq-MZEV-FMmD-DK04-qPwwkAkBIbn5"),sQuery(id+"F0.wireOp",EDGE,"b6izAig9-YVkh-wso9-hAal-lVyQwPKH0Rqq"),sQuery(id+"F0.wireOp",EDGE,"Ld8sGsMe-wxKW-HELd-rUX3-tJrgnMnEQjee"),sQuery(id+"F0.wireOp",EDGE,"KcqUpT09-MFPH-TNWY-efLy-ihoS9jBIaYSA"),sQuery(id+"F0.wireOp",EDGE,"E0.0.1.1"),sQuery(id+"F0.wireOp",EDGE,"E0.0.1.2"),sQuery(id+"F0.wireOp",EDGE,"E0.0.1.3"),sQuery(id+"F0.wireOp",EDGE,"E0.0.2.0"),sQuery(id+"F0.wireOp",EDGE,"E0.0.2.1"),sQuery(id+"F0.wireOp",EDGE,"E0.0.2.2"),sQuery(id+"F0.wireOp",EDGE,"E0.0.2.3"),sQuery(id+"F0.wireOp",EDGE,"E0.0.3.0"),sQuery(id+"F0.wireOp",EDGE,"E0.0.3.1"),sQuery(id+"F0.wireOp",EDGE,"E0.0.3.2"),sQuery(id+"F0.wireOp",EDGE,"E0.0.3.3"),sQuery(id+"F0.wireOp",EDGE,"E0.0.4.0"),sQuery(id+"F0.wireOp",EDGE,"E0.0.4.1"),sQuery(id+"F0.wireOp",EDGE,"E0.0.4.2"),sQuery(id+"F0.wireOp",EDGE,"E0.0.4.3"),sQuery(id+"F0.wireOp",EDGE,"E0.0.5.0"),sQuery(id+"F0.wireOp",EDGE,"E0.0.5.1"),sQuery(id+"F0.wireOp",EDGE,"E0.0.5.2"),sQuery(id+"F0.wireOp",EDGE,"E0.0.5.3"),sQuery(id+"F0.wireOp",EDGE,"E0.0.6.0"),sQuery(id+"F0.wireOp",EDGE,"E0.0.6.1"),sQuery(id+"F0.wireOp",EDGE,"E0.0.6.2"),sQuery(id+"F0.wireOp",EDGE,"E0.0.6.3"),sQuery(id+"F0.wireOp",EDGE,"E0.0.7.0"),sQuery(id+"F0.wireOp",EDGE,"E0.0.7.1"),sQuery(id+"F0.wireOp",EDGE,"E0.0.7.2"),sQuery(id+"F0.wireOp",EDGE,"E0.0.7.3"),sQuery(id+"F0.wireOp",EDGE,"E0.0.8.0"),sQuery(id+"F0.wireOp",EDGE,"E0.0.8.1"),sQuery(id+"F0.wireOp",EDGE,"E0.0.8.2"),sQuery(id+"F0.wireOp",EDGE,"E0.0.8.3"),sQuery(id+"F0.wireOp",EDGE,"E0.0.9.0"),sQuery(id+"F0.wireOp",EDGE,"E0.0.9.1"),sQuery(id+"F0.wireOp",EDGE,"E0.0.9.2"),sQuery(id+"F0.wireOp",EDGE,"E0.0.9.3"),sQuery(id+"F0.wireOp",EDGE,"E0.0.10.0"),sQuery(id+"F0.wireOp",EDGE,"E0.0.10.1"),sQuery(id+"F0.wireOp",EDGE,"E0.0.10.2"),sQuery(id+"F0.wireOp",EDGE,"E0.0.10.3"),sQuery(id+"F0.wireOp",EDGE,"E0.0.11.0"),sQuery(id+"F0.wireOp",EDGE,"E0.0.11.1"),sQuery(id+"F0.wireOp",EDGE,"E0.0.11.2"),sQuery(id+"F0.wireOp",EDGE,"E0.0.11.3"),sQuery(id+"F0.wireOp",EDGE,"E0.0.12.0"),sQuery(id+"F0.wireOp",EDGE,"E0.0.12.1"),sQuery(id+"F0.wireOp",EDGE,"E0.0.12.2"),sQuery(id+"F0.wireOp",EDGE,"E0.0.12.3"),sQuery(id+"F0.wireOp",EDGE,"E0.0.13.0"),sQuery(id+"F0.wireOp",EDGE,"E0.0.13.1"),sQuery(id+"F0.wireOp",EDGE,"E0.0.13.2"),sQuery(id+"F0.wireOp",EDGE,"E0.0.13.3"),sQuery(id+"F0.wireOp",EDGE,"E0.0.14.0"),sQuery(id+"F0.wireOp",EDGE,"E0.0.14.1"),sQuery(id+"F0.wireOp",EDGE,"E0.0.14.2"),sQuery(id+"F0.wireOp",EDGE,"E0.0.14.3"),sQuery(id+"F0.wireOp",EDGE,"E0.0.15.0"),sQuery(id+"F0.wireOp",EDGE,"E0.0.15.1"),sQuery(id+"F0.wireOp",EDGE,"E0.0.15.2"),sQuery(id+"F0.wireOp",EDGE,"E0.0.15.3"),sQuery(id+"F0.wireOp",EDGE,"E0.0.16.0"),sQuery(id+"F0.wireOp",EDGE,"E0.0.16.1"),sQuery(id+"F0.wireOp",EDGE,"E0.0.16.2"),sQuery(id+"F0.wireOp",EDGE,"E0.0.16.3"),sQuery(id+"F0.wireOp",EDGE,"E0.0.17.0"),sQuery(id+"F0.wireOp",EDGE,"E0.0.17.1"),sQuery(id+"F0.wireOp",EDGE,"E0.0.17.2"),sQuery(id+"F0.wireOp",EDGE,"E0.0.17.3"),sQuery(id+"F0.wireOp",EDGE,"E0.0.18.0"),sQuery(id+"F0.wireOp",EDGE,"E0.0.18.1"),sQuery(id+"F0.wireOp",EDGE,"E0.0.18.2"),sQuery(id+"F0.wireOp",EDGE,"E0.0.18.3"),sQuery(id+"F0.wireOp",EDGE,"E0.0.19.0"),sQuery(id+"F0.wireOp",EDGE,"E0.0.19.1"),sQuery(id+"F0.wireOp",EDGE,"E0.0.19.2"),sQuery(id+"F0.wireOp",EDGE,"E0.0.19.3"),sQuery(id+"F0.wireOp",EDGE,"E0.0.20.0"),sQuery(id+"F0.wireOp",EDGE,"E0.0.20.1"),sQuery(id+"F0.wireOp",EDGE,"E0.0.20.2"),sQuery(id+"F0.wireOp",EDGE,"E0.0.20.3"),sQuery(id+"F0.wireOp",EDGE,"E0.0.21.0"),sQuery(id+"F0.wireOp",EDGE,"E0.0.21.1"),sQuery(id+"F0.wireOp",EDGE,"E0.0.21.2"),sQuery(id+"F0.wireOp",EDGE,"E0.0.21.3"),sQuery(id+"F0.wireOp",EDGE,"E0.0.22.0"),sQuery(id+"F0.wireOp",EDGE,"E0.0.22.1"),sQuery(id+"F0.wireOp",EDGE,"E0.0.22.2"),sQuery(id+"F0.wireOp",EDGE,"E0.0.22.3"),sQuery(id+"F0.wireOp",EDGE,"E0.0.23.0"),sQuery(id+"F0.wireOp",EDGE,"E0.0.23.1"),sQuery(id+"F0.wireOp",EDGE,"E0.0.23.2"),sQuery(id+"F0.wireOp",EDGE,"E0.0.23.3"),sQuery(id+"F0.wireOp",EDGE,"E0.0.24.0"),sQuery(id+"F0.wireOp",EDGE,"E0.0.24.1"),sQuery(id+"F0.wireOp",EDGE,"E0.0.24.2"),sQuery(id+"F0.wireOp",EDGE,"E0.0.24.3"),sQuery(id+"F0.wireOp",EDGE,"E0.0.25.0"),sQuery(id+"F0.wireOp",EDGE,"E0.0.25.1"),sQuery(id+"F0.wireOp",EDGE,"E0.0.25.2"),sQuery(id+"F0.wireOp",EDGE,"E0.0.25.3"),sQuery(id+"F0.wireOp",EDGE,"E0.1.0.0"),sQuery(id+"F0.wireOp",EDGE,"E0.1.0.1"),sQuery(id+"F0.wireOp",EDGE,"E0.1.0.2"),sQuery(id+"F0.wireOp",EDGE,"E0.1.0.3"),sQuery(id+"F0.wireOp",EDGE,"E0.1.1.0"),sQuery(id+"F0.wireOp",EDGE,"E0.1.1.1"),sQuery(id+"F0.wireOp",EDGE,"E0.1.1.2"),sQuery(id+"F0.wireOp",EDGE,"E0.1.1.3"),sQuery(id+"F0.wireOp",EDGE,"E0.1.2.0"),sQuery(id+"F0.wireOp",EDGE,"E0.1.2.1"),sQuery(id+"F0.wireOp",EDGE,"E0.1.2.2"),sQuery(id+"F0.wireOp",EDGE,"E0.1.2.3"),sQuery(id+"F0.wireOp",EDGE,"E0.1.3.0"),sQuery(id+"F0.wireOp",EDGE,"E0.1.3.1"),sQuery(id+"F0.wireOp",EDGE,"E0.1.3.2"),sQuery(id+"F0.wireOp",EDGE,"E0.1.3.3"),sQuery(id+"F0.wireOp",EDGE,"E0.1.4.0"),sQuery(id+"F0.wireOp",EDGE,"E0.1.4.1"),sQuery(id+"F0.wireOp",EDGE,"E0.1.4.2"),sQuery(id+"F0.wireOp",EDGE,"E0.1.4.3"),sQuery(id+"F0.wireOp",EDGE,"E0.1.5.0"),sQuery(id+"F0.wireOp",EDGE,"E0.1.5.1"),sQuery(id+"F0.wireOp",EDGE,"E0.1.5.2"),sQuery(id+"F0.wireOp",EDGE,"E0.1.5.3"),sQuery(id+"F0.wireOp",EDGE,"E0.1.6.0"),sQuery(id+"F0.wireOp",EDGE,"E0.1.6.1"),sQuery(id+"F0.wireOp",EDGE,"E0.1.6.2"),sQuery(id+"F0.wireOp",EDGE,"E0.1.6.3"),sQuery(id+"F0.wireOp",EDGE,"E0.1.7.0"),sQuery(id+"F0.wireOp",EDGE,"E0.1.7.1"),sQuery(id+"F0.wireOp",EDGE,"E0.1.7.2"),sQuery(id+"F0.wireOp",EDGE,"E0.1.7.3"),sQuery(id+"F0.wireOp",EDGE,"E0.1.8.0"),sQuery(id+"F0.wireOp",EDGE,"E0.1.8.1"),sQuery(id+"F0.wireOp",EDGE,"E0.1.8.2"),sQuery(id+"F0.wireOp",EDGE,"E0.1.8.3"),sQuery(id+"F0.wireOp",EDGE,"E0.1.9.0"),sQuery(id+"F0.wireOp",EDGE,"E0.1.9.1"),sQuery(id+"F0.wireOp",EDGE,"E0.1.9.2"),sQuery(id+"F0.wireOp",EDGE,"E0.1.9.3"),sQuery(id+"F0.wireOp",EDGE,"E0.1.10.0"),sQuery(id+"F0.wireOp",EDGE,"E0.1.10.1"),sQuery(id+"F0.wireOp",EDGE,"E0.1.10.2"),sQuery(id+"F0.wireOp",EDGE,"E0.1.10.3"),sQuery(id+"F0.wireOp",EDGE,"E0.1.11.0"),sQuery(id+"F0.wireOp",EDGE,"E0.1.11.1"),sQuery(id+"F0.wireOp",EDGE,"E0.1.11.2"),sQuery(id+"F0.wireOp",EDGE,"E0.1.11.3"),sQuery(id+"F0.wireOp",EDGE,"E0.1.12.0"),sQuery(id+"F0.wireOp",EDGE,"E0.1.12.1"),sQuery(id+"F0.wireOp",EDGE,"E0.1.12.2"),sQuery(id+"F0.wireOp",EDGE,"E0.1.12.3"),sQuery(id+"F0.wireOp",EDGE,"E0.1.13.0"),sQuery(id+"F0.wireOp",EDGE,"E0.1.13.1"),sQuery(id+"F0.wireOp",EDGE,"E0.1.13.2"),sQuery(id+"F0.wireOp",EDGE,"E0.1.13.3"),sQuery(id+"F0.wireOp",EDGE,"E0.1.14.0"),sQuery(id+"F0.wireOp",EDGE,"E0.1.14.1"),sQuery(id+"F0.wireOp",EDGE,"E0.1.14.2"),sQuery(id+"F0.wireOp",EDGE,"E0.1.14.3"),sQuery(id+"F0.wireOp",EDGE,"E0.1.15.0"),sQuery(id+"F0.wireOp",EDGE,"E0.1.15.1"),sQuery(id+"F0.wireOp",EDGE,"E0.1.15.2"),sQuery(id+"F0.wireOp",EDGE,"E0.1.15.3"),sQuery(id+"F0.wireOp",EDGE,"E0.1.16.0"),sQuery(id+"F0.wireOp",EDGE,"E0.1.16.1"),sQuery(id+"F0.wireOp",EDGE,"E0.1.16.2"),sQuery(id+"F0.wireOp",EDGE,"E0.1.16.3"),sQuery(id+"F0.wireOp",EDGE,"E0.1.17.0"),sQuery(id+"F0.wireOp",EDGE,"E0.1.17.1"),sQuery(id+"F0.wireOp",EDGE,"E0.1.17.2"),sQuery(id+"F0.wireOp",EDGE,"E0.1.17.3"),sQuery(id+"F0.wireOp",EDGE,"E0.1.18.0"),sQuery(id+"F0.wireOp",EDGE,"E0.1.18.1"),sQuery(id+"F0.wireOp",EDGE,"E0.1.18.2"),sQuery(id+"F0.wireOp",EDGE,"E0.1.18.3"),sQuery(id+"F0.wireOp",EDGE,"E0.1.19.0"),sQuery(id+"F0.wireOp",EDGE,"E0.1.19.1"),sQuery(id+"F0.wireOp",EDGE,"E0.1.19.2"),sQuery(id+"F0.wireOp",EDGE,"E0.1.19.3"),sQuery(id+"F0.wireOp",EDGE,"E0.1.20.0"),sQuery(id+"F0.wireOp",EDGE,"E0.1.20.1"),sQuery(id+"F0.wireOp",EDGE,"E0.1.20.2"),sQuery(id+"F0.wireOp",EDGE,"E0.1.20.3"),sQuery(id+"F0.wireOp",EDGE,"E0.1.21.0"),sQuery(id+"F0.wireOp",EDGE,"E0.1.21.1"),sQuery(id+"F0.wireOp",EDGE,"E0.1.21.2"),sQuery(id+"F0.wireOp",EDGE,"E0.1.21.3"),sQuery(id+"F0.wireOp",EDGE,"E0.1.22.0"),sQuery(id+"F0.wireOp",EDGE,"E0.1.22.1"),sQuery(id+"F0.wireOp",EDGE,"E0.1.22.2"),sQuery(id+"F0.wireOp",EDGE,"E0.1.22.3"),sQuery(id+"F0.wireOp",EDGE,"E0.1.23.0"),sQuery(id+"F0.wireOp",EDGE,"E0.1.23.1"),sQuery(id+"F0.wireOp",EDGE,"E0.1.23.2"),sQuery(id+"F0.wireOp",EDGE,"E0.1.23.3"),sQuery(id+"F0.wireOp",EDGE,"E0.1.24.0"),sQuery(id+"F0.wireOp",EDGE,"E0.1.24.1"),sQuery(id+"F0.wireOp",EDGE,"E0.1.24.2"),sQuery(id+"F0.wireOp",EDGE,"E0.1.24.3"),sQuery(id+"F0.wireOp",EDGE,"E0.1.25.0"),sQuery(id+"F0.wireOp",EDGE,"E0.1.25.1"),sQuery(id+"F0.wireOp",EDGE,"E0.1.25.2"),sQuery(id+"F0.wireOp",EDGE,"E0.1.25.3"),sQuery(id+"F0.wireOp",EDGE,"E0.2.0.0"),sQuery(id+"F0.wireOp",EDGE,"E0.2.0.1"),sQuery(id+"F0.wireOp",EDGE,"E0.2.0.2"),sQuery(id+"F0.wireOp",EDGE,"E0.2.0.3"),sQuery(id+"F0.wireOp",EDGE,"E0.2.1.0"),sQuery(id+"F0.wireOp",EDGE,"E0.2.1.1"),sQuery(id+"F0.wireOp",EDGE,"E0.2.1.2"),sQuery(id+"F0.wireOp",EDGE,"E0.2.1.3"),sQuery(id+"F0.wireOp",EDGE,"E0.2.2.0"),sQuery(id+"F0.wireOp",EDGE,"E0.2.2.1"),sQuery(id+"F0.wireOp",EDGE,"E0.2.2.2"),sQuery(id+"F0.wireOp",EDGE,"E0.2.2.3"),sQuery(id+"F0.wireOp",EDGE,"E0.2.3.0"),sQuery(id+"F0.wireOp",EDGE,"E0.2.3.1"),sQuery(id+"F0.wireOp",EDGE,"E0.2.3.2"),sQuery(id+"F0.wireOp",EDGE,"E0.2.3.3"),sQuery(id+"F0.wireOp",EDGE,"E0.2.4.0"),sQuery(id+"F0.wireOp",EDGE,"E0.2.4.1"),sQuery(id+"F0.wireOp",EDGE,"E0.2.4.2"),sQuery(id+"F0.wireOp",EDGE,"E0.2.4.3"),sQuery(id+"F0.wireOp",EDGE,"E0.2.5.0"),sQuery(id+"F0.wireOp",EDGE,"E0.2.5.1"),sQuery(id+"F0.wireOp",EDGE,"E0.2.5.2"),sQuery(id+"F0.wireOp",EDGE,"E0.2.5.3"),sQuery(id+"F0.wireOp",EDGE,"E0.2.6.0"),sQuery(id+"F0.wireOp",EDGE,"E0.2.6.1"),sQuery(id+"F0.wireOp",EDGE,"E0.2.6.2"),sQuery(id+"F0.wireOp",EDGE,"E0.2.6.3"),sQuery(id+"F0.wireOp",EDGE,"E0.2.7.0"),sQuery(id+"F0.wireOp",EDGE,"E0.2.7.1"),sQuery(id+"F0.wireOp",EDGE,"E0.2.7.2"),sQuery(id+"F0.wireOp",EDGE,"E0.2.7.3"),sQuery(id+"F0.wireOp",EDGE,"E0.2.8.0"),sQuery(id+"F0.wireOp",EDGE,"E0.2.8.1"),sQuery(id+"F0.wireOp",EDGE,"E0.2.8.2"),sQuery(id+"F0.wireOp",EDGE,"E0.2.8.3"),sQuery(id+"F0.wireOp",EDGE,"E0.2.9.0"),sQuery(id+"F0.wireOp",EDGE,"E0.2.9.1"),sQuery(id+"F0.wireOp",EDGE,"E0.2.9.2"),sQuery(id+"F0.wireOp",EDGE,"E0.2.9.3"),sQuery(id+"F0.wireOp",EDGE,"E0.2.10.0"),sQuery(id+"F0.wireOp",EDGE,"E0.2.10.1"),sQuery(id+"F0.wireOp",EDGE,"E0.2.10.2"),sQuery(id+"F0.wireOp",EDGE,"E0.2.10.3"),sQuery(id+"F0.wireOp",EDGE,"E0.2.11.0"),sQuery(id+"F0.wireOp",EDGE,"E0.2.11.1"),sQuery(id+"F0.wireOp",EDGE,"E0.2.11.2"),sQuery(id+"F0.wireOp",EDGE,"E0.2.11.3"),sQuery(id+"F0.wireOp",EDGE,"E0.2.12.0"),sQuery(id+"F0.wireOp",EDGE,"E0.2.12.1"),sQuery(id+"F0.wireOp",EDGE,"E0.2.12.2"),sQuery(id+"F0.wireOp",EDGE,"E0.2.12.3"),sQuery(id+"F0.wireOp",EDGE,"E0.2.13.0"),sQuery(id+"F0.wireOp",EDGE,"E0.2.13.1"),sQuery(id+"F0.wireOp",EDGE,"E0.2.13.2"),sQuery(id+"F0.wireOp",EDGE,"E0.2.13.3"),sQuery(id+"F0.wireOp",EDGE,"E0.2.14.0"),sQuery(id+"F0.wireOp",EDGE,"E0.2.14.1"),sQuery(id+"F0.wireOp",EDGE,"E0.2.14.2"),sQuery(id+"F0.wireOp",EDGE,"E0.2.14.3"),sQuery(id+"F0.wireOp",EDGE,"E0.2.15.0"),sQuery(id+"F0.wireOp",EDGE,"E0.2.15.1"),sQuery(id+"F0.wireOp",EDGE,"E0.2.15.2"),sQuery(id+"F0.wireOp",EDGE,"E0.2.15.3"),sQuery(id+"F0.wireOp",EDGE,"E0.2.16.0"),sQuery(id+"F0.wireOp",EDGE,"E0.2.16.1"),sQuery(id+"F0.wireOp",EDGE,"E0.2.16.2"),sQuery(id+"F0.wireOp",EDGE,"E0.2.16.3"),sQuery(id+"F0.wireOp",EDGE,"E0.2.17.0"),sQuery(id+"F0.wireOp",EDGE,"E0.2.17.1"),sQuery(id+"F0.wireOp",EDGE,"E0.2.17.2"),sQuery(id+"F0.wireOp",EDGE,"E0.2.17.3"),sQuery(id+"F0.wireOp",EDGE,"E0.2.18.0"),sQuery(id+"F0.wireOp",EDGE,"E0.2.18.1"),sQuery(id+"F0.wireOp",EDGE,"E0.2.18.2"),sQuery(id+"F0.wireOp",EDGE,"E0.2.18.3"),sQuery(id+"F0.wireOp",EDGE,"E0.2.19.0"),sQuery(id+"F0.wireOp",EDGE,"E0.2.19.1"),sQuery(id+"F0.wireOp",EDGE,"E0.2.19.2"),sQuery(id+"F0.wireOp",EDGE,"E0.2.19.3"),sQuery(id+"F0.wireOp",EDGE,"E0.2.20.0"),sQuery(id+"F0.wireOp",EDGE,"E0.2.20.1"),sQuery(id+"F0.wireOp",EDGE,"E0.2.20.2"),sQuery(id+"F0.wireOp",EDGE,"E0.2.20.3"),sQuery(id+"F0.wireOp",EDGE,"E0.2.21.0"),sQuery(id+"F0.wireOp",EDGE,"E0.2.21.1"),sQuery(id+"F0.wireOp",EDGE,"E0.2.21.2"),sQuery(id+"F0.wireOp",EDGE,"E0.2.21.3"),sQuery(id+"F0.wireOp",EDGE,"E0.2.22.0"),sQuery(id+"F0.wireOp",EDGE,"E0.2.22.1"),sQuery(id+"F0.wireOp",EDGE,"E0.2.22.2"),sQuery(id+"F0.wireOp",EDGE,"E0.2.22.3"),sQuery(id+"F0.wireOp",EDGE,"E0.2.23.0"),sQuery(id+"F0.wireOp",EDGE,"E0.2.23.1"),sQuery(id+"F0.wireOp",EDGE,"E0.2.23.2"),sQuery(id+"F0.wireOp",EDGE,"E0.2.23.3"),sQuery(id+"F0.wireOp",EDGE,"E0.2.24.0"),sQuery(id+"F0.wireOp",EDGE,"E0.2.24.1"),sQuery(id+"F0.wireOp",EDGE,"E0.2.24.2"),sQuery(id+"F0.wireOp",EDGE,"E0.2.24.3"),sQuery(id+"F0.wireOp",EDGE,"E0.2.25.0"),sQuery(id+"F0.wireOp",EDGE,"E0.2.25.1"),sQuery(id+"F0.wireOp",EDGE,"E0.2.25.2"),sQuery(id+"F0.wireOp",EDGE,"E0.2.25.3"),sQuery(id+"F0.wireOp",EDGE,"AU2oHFlj-txaj-hLN4-KDEQ-E2aTrxoRIFTm"),sQuery(id+"F0.wireOp",EDGE,"T7GrudpP-bjZC-sghp-RzMj-ol2ZXyDjpRGs"),sQuery(id+"F0.wireOp",EDGE,"E1"),sQuery(id+"F0.wireOp",EDGE,"90fbf2e0-ce94-4077-ba36-f7078a65e9f6.1.0.0"),sQuery(id+"F0.wireOp",EDGE,"90fbf2e0-ce94-4077-ba36-f7078a65e9f6.1.0.1"),sQuery(id+"F0.wireOp",EDGE,"90fbf2e0-ce94-4077-ba36-f7078a65e9f6.1.0.2"),sQuery(id+"F0.wireOp",EDGE,"90fbf2e0-ce94-4077-ba36-f7078a65e9f6.1.0.3"),sQuery(id+"F0.wireOp",EDGE,"90fbf2e0-ce94-4077-ba36-f7078a65e9f6.1.0.4"),sQuery(id+"F0.wireOp",EDGE,"90fbf2e0-ce94-4077-ba36-f7078a65e9f6.1.0.5"),sQuery(id+"F0.wireOp",EDGE,"90fbf2e0-ce94-4077-ba36-f7078a65e9f6.1.0.6"),sQuery(id+"F0.wireOp",EDGE,"90fbf2e0-ce94-4077-ba36-f7078a65e9f6.1.0.7"),sQuery(id+"F0.wireOp",EDGE,"90fbf2e0-ce94-4077-ba36-f7078a65e9f6.1.0.8"),sQuery(id+"F0.wireOp",EDGE,"90fbf2e0-ce94-4077-ba36-f7078a65e9f6.1.0.9"),sQuery(id+"F0.wireOp",EDGE,"90fbf2e0-ce94-4077-ba36-f7078a65e9f6.1.0.10"),sQuery(id+"F0.wireOp",EDGE,"90fbf2e0-ce94-4077-ba36-f7078a65e9f6.1.0.11"),sQuery(id+"F0.wireOp",EDGE,"90fbf2e0-ce94-4077-ba36-f7078a65e9f6.2.0.0"),sQuery(id+"F0.wireOp",EDGE,"90fbf2e0-ce94-4077-ba36-f7078a65e9f6.2.0.1"),sQuery(id+"F0.wireOp",EDGE,"90fbf2e0-ce94-4077-ba36-f7078a65e9f6.2.0.2"),sQuery(id+"F0.wireOp",EDGE,"90fbf2e0-ce94-4077-ba36-f7078a65e9f6.2.0.3"),sQuery(id+"F0.wireOp",EDGE,"90fbf2e0-ce94-4077-ba36-f7078a65e9f6.2.0.4"),sQuery(id+"F0.wireOp",EDGE,"90fbf2e0-ce94-4077-ba36-f7078a65e9f6.2.0.5"),sQuery(id+"F0.wireOp",EDGE,"90fbf2e0-ce94-4077-ba36-f7078a65e9f6.2.0.6"),sQuery(id+"F0.wireOp",EDGE,"90fbf2e0-ce94-4077-ba36-f7078a65e9f6.2.0.7"),sQuery(id+"F0.wireOp",EDGE,"90fbf2e0-ce94-4077-ba36-f7078a65e9f6.2.0.8"),sQuery(id+"F0.wireOp",EDGE,"90fbf2e0-ce94-4077-ba36-f7078a65e9f6.2.0.9"),sQuery(id+"F0.wireOp",EDGE,"90fbf2e0-ce94-4077-ba36-f7078a65e9f6.2.0.10"),sQuery(id+"F0.wireOp",EDGE,"90fbf2e0-ce94-4077-ba36-f7078a65e9f6.2.0.11"),sQuery(id+"F0.wireOp",EDGE,"90fbf2e0-ce94-4077-ba36-f7078a65e9f6.3.0.0"),sQuery(id+"F0.wireOp",EDGE,"90fbf2e0-ce94-4077-ba36-f7078a65e9f6.3.0.1"),sQuery(id+"F0.wireOp",EDGE,"90fbf2e0-ce94-4077-ba36-f7078a65e9f6.3.0.2"),sQuery(id+"F0.wireOp",EDGE,"90fbf2e0-ce94-4077-ba36-f7078a65e9f6.3.0.3"),sQuery(id+"F0.wireOp",EDGE,"90fbf2e0-ce94-4077-ba36-f7078a65e9f6.3.0.4"),sQuery(id+"F0.wireOp",EDGE,"90fbf2e0-ce94-4077-ba36-f7078a65e9f6.3.0.5"),sQuery(id+"F0.wireOp",EDGE,"90fbf2e0-ce94-4077-ba36-f7078a65e9f6.3.0.6"),sQuery(id+"F0.wireOp",EDGE,"90fbf2e0-ce94-4077-ba36-f7078a65e9f6.3.0.7"),sQuery(id+"F0.wireOp",EDGE,"90fbf2e0-ce94-4077-ba36-f7078a65e9f6.3.0.8"),sQuery(id+"F0.wireOp",EDGE,"90fbf2e0-ce94-4077-ba36-f7078a65e9f6.3.0.9"),sQuery(id+"F0.wireOp",EDGE,"90fbf2e0-ce94-4077-ba36-f7078a65e9f6.3.0.10"),sQuery(id+"F0.wireOp",EDGE,"90fbf2e0-ce94-4077-ba36-f7078a65e9f6.3.0.11"),sQuery(id+"F0.wireOp",EDGE,"90fbf2e0-ce94-4077-ba36-f7078a65e9f6.4.0.0"),sQuery(id+"F0.wireOp",EDGE,"90fbf2e0-ce94-4077-ba36-f7078a65e9f6.4.0.1"),sQuery(id+"F0.wireOp",EDGE,"90fbf2e0-ce94-4077-ba36-f7078a65e9f6.4.0.2"),sQuery(id+"F0.wireOp",EDGE,"90fbf2e0-ce94-4077-ba36-f7078a65e9f6.4.0.3"),sQuery(id+"F0.wireOp",EDGE,"90fbf2e0-ce94-4077-ba36-f7078a65e9f6.4.0.4"),sQuery(id+"F0.wireOp",EDGE,"90fbf2e0-ce94-4077-ba36-f7078a65e9f6.4.0.5"),sQuery(id+"F0.wireOp",EDGE,"90fbf2e0-ce94-4077-ba36-f7078a65e9f6.4.0.6"),sQuery(id+"F0.wireOp",EDGE,"90fbf2e0-ce94-4077-ba36-f7078a65e9f6.4.0.7"),sQuery(id+"F0.wireOp",EDGE,"90fbf2e0-ce94-4077-ba36-f7078a65e9f6.4.0.8"),sQuery(id+"F0.wireOp",EDGE,"90fbf2e0-ce94-4077-ba36-f7078a65e9f6.4.0.9"),sQuery(id+"F0.wireOp",EDGE,"90fbf2e0-ce94-4077-ba36-f7078a65e9f6.4.0.10"),sQuery(id+"F0.wireOp",EDGE,"90fbf2e0-ce94-4077-ba36-f7078a65e9f6.4.0.11"),sQuery(id+"F0.wireOp",EDGE,"90fbf2e0-ce94-4077-ba36-f7078a65e9f6.5.0.0"),sQuery(id+"F0.wireOp",EDGE,"90fbf2e0-ce94-4077-ba36-f7078a65e9f6.5.0.1"),sQuery(id+"F0.wireOp",EDGE,"90fbf2e0-ce94-4077-ba36-f7078a65e9f6.5.0.2"),sQuery(id+"F0.wireOp",EDGE,"90fbf2e0-ce94-4077-ba36-f7078a65e9f6.5.0.3"),sQuery(id+"F0.wireOp",EDGE,"90fbf2e0-ce94-4077-ba36-f7078a65e9f6.5.0.4"),sQuery(id+"F0.wireOp",EDGE,"90fbf2e0-ce94-4077-ba36-f7078a65e9f6.5.0.5"),sQuery(id+"F0.wireOp",EDGE,"90fbf2e0-ce94-4077-ba36-f7078a65e9f6.5.0.6"),sQuery(id+"F0.wireOp",EDGE,"90fbf2e0-ce94-4077-ba36-f7078a65e9f6.5.0.7"),sQuery(id+"F0.wireOp",EDGE,"90fbf2e0-ce94-4077-ba36-f7078a65e9f6.5.0.8"),sQuery(id+"F0.wireOp",EDGE,"90fbf2e0-ce94-4077-ba36-f7078a65e9f6.5.0.9"),sQuery(id+"F0.wireOp",EDGE,"90fbf2e0-ce94-4077-ba36-f7078a65e9f6.5.0.10"),sQuery(id+"F0.wireOp",EDGE,"90fbf2e0-ce94-4077-ba36-f7078a65e9f6.5.0.11"),sQuery(id+"F0.wireOp",EDGE,"90fbf2e0-ce94-4077-ba36-f7078a65e9f6.6.0.0"),sQuery(id+"F0.wireOp",EDGE,"90fbf2e0-ce94-4077-ba36-f7078a65e9f6.6.0.1"),sQuery(id+"F0.wireOp",EDGE,"90fbf2e0-ce94-4077-ba36-f7078a65e9f6.6.0.2"),sQuery(id+"F0.wireOp",EDGE,"90fbf2e0-ce94-4077-ba36-f7078a65e9f6.6.0.3"),sQuery(id+"F0.wireOp",EDGE,"90fbf2e0-ce94-4077-ba36-f7078a65e9f6.6.0.4"),sQuery(id+"F0.wireOp",EDGE,"90fbf2e0-ce94-4077-ba36-f7078a65e9f6.6.0.5"),sQuery(id+"F0.wireOp",EDGE,"90fbf2e0-ce94-4077-ba36-f7078a65e9f6.6.0.6"),sQuery(id+"F0.wireOp",EDGE,"90fbf2e0-ce94-4077-ba36-f7078a65e9f6.6.0.7"),sQuery(id+"F0.wireOp",EDGE,"90fbf2e0-ce94-4077-ba36-f7078a65e9f6.6.0.8"),sQuery(id+"F0.wireOp",EDGE,"90fbf2e0-ce94-4077-ba36-f7078a65e9f6.6.0.9"),sQuery(id+"F0.wireOp",EDGE,"90fbf2e0-ce94-4077-ba36-f7078a65e9f6.6.0.10"),sQuery(id+"F0.wireOp",EDGE,"90fbf2e0-ce94-4077-ba36-f7078a65e9f6.6.0.11"),sQuery(id+"F0.wireOp",EDGE,"90fbf2e0-ce94-4077-ba36-f7078a65e9f6.7.0.0"),sQuery(id+"F0.wireOp",EDGE,"90fbf2e0-ce94-4077-ba36-f7078a65e9f6.7.0.1"),sQuery(id+"F0.wireOp",EDGE,"90fbf2e0-ce94-4077-ba36-f7078a65e9f6.7.0.2"),sQuery(id+"F0.wireOp",EDGE,"90fbf2e0-ce94-4077-ba36-f7078a65e9f6.7.0.3"),sQuery(id+"F0.wireOp",EDGE,"90fbf2e0-ce94-4077-ba36-f7078a65e9f6.7.0.4"),sQuery(id+"F0.wireOp",EDGE,"90fbf2e0-ce94-4077-ba36-f7078a65e9f6.7.0.5"),sQuery(id+"F0.wireOp",EDGE,"90fbf2e0-ce94-4077-ba36-f7078a65e9f6.7.0.6"),sQuery(id+"F0.wireOp",EDGE,"90fbf2e0-ce94-4077-ba36-f7078a65e9f6.7.0.7"),sQuery(id+"F0.wireOp",EDGE,"90fbf2e0-ce94-4077-ba36-f7078a65e9f6.7.0.8"),sQuery(id+"F0.wireOp",EDGE,"90fbf2e0-ce94-4077-ba36-f7078a65e9f6.7.0.9"),sQuery(id+"F0.wireOp",EDGE,"90fbf2e0-ce94-4077-ba36-f7078a65e9f6.7.0.10"),sQuery(id+"F0.wireOp",EDGE,"90fbf2e0-ce94-4077-ba36-f7078a65e9f6.7.0.11"),sQuery(id+"F0.wireOp",EDGE,"90fbf2e0-ce94-4077-ba36-f7078a65e9f6.8.0.0"),sQuery(id+"F0.wireOp",EDGE,"90fbf2e0-ce94-4077-ba36-f7078a65e9f6.8.0.1"),sQuery(id+"F0.wireOp",EDGE,"90fbf2e0-ce94-4077-ba36-f7078a65e9f6.8.0.2"),sQuery(id+"F0.wireOp",EDGE,"90fbf2e0-ce94-4077-ba36-f7078a65e9f6.8.0.3"),sQuery(id+"F0.wireOp",EDGE,"90fbf2e0-ce94-4077-ba36-f7078a65e9f6.8.0.4"),sQuery(id+"F0.wireOp",EDGE,"90fbf2e0-ce94-4077-ba36-f7078a65e9f6.8.0.5"),sQuery(id+"F0.wireOp",EDGE,"90fbf2e0-ce94-4077-ba36-f7078a65e9f6.8.0.6"),sQuery(id+"F0.wireOp",EDGE,"90fbf2e0-ce94-4077-ba36-f7078a65e9f6.8.0.7"),sQuery(id+"F0.wireOp",EDGE,"90fbf2e0-ce94-4077-ba36-f7078a65e9f6.8.0.8"),sQuery(id+"F0.wireOp",EDGE,"90fbf2e0-ce94-4077-ba36-f7078a65e9f6.8.0.9"),sQuery(id+"F0.wireOp",EDGE,"90fbf2e0-ce94-4077-ba36-f7078a65e9f6.8.0.10"),sQuery(id+"F0.wireOp",EDGE,"90fbf2e0-ce94-4077-ba36-f7078a65e9f6.8.0.11"),sQuery(id+"F0.wireOp",EDGE,"90fbf2e0-ce94-4077-ba36-f7078a65e9f6.9.0.0"),sQuery(id+"F0.wireOp",EDGE,"90fbf2e0-ce94-4077-ba36-f7078a65e9f6.9.0.1"),sQuery(id+"F0.wireOp",EDGE,"90fbf2e0-ce94-4077-ba36-f7078a65e9f6.9.0.2"),sQuery(id+"F0.wireOp",EDGE,"90fbf2e0-ce94-4077-ba36-f7078a65e9f6.9.0.3"),sQuery(id+"F0.wireOp",EDGE,"90fbf2e0-ce94-4077-ba36-f7078a65e9f6.9.0.4"),sQuery(id+"F0.wireOp",EDGE,"90fbf2e0-ce94-4077-ba36-f7078a65e9f6.9.0.5"),sQuery(id+"F0.wireOp",EDGE,"90fbf2e0-ce94-4077-ba36-f7078a65e9f6.9.0.6"),sQuery(id+"F0.wireOp",EDGE,"90fbf2e0-ce94-4077-ba36-f7078a65e9f6.9.0.7"),sQuery(id+"F0.wireOp",EDGE,"90fbf2e0-ce94-4077-ba36-f7078a65e9f6.9.0.8"),sQuery(id+"F0.wireOp",EDGE,"90fbf2e0-ce94-4077-ba36-f7078a65e9f6.9.0.9"),sQuery(id+"F0.wireOp",EDGE,"90fbf2e0-ce94-4077-ba36-f7078a65e9f6.9.0.10"),sQuery(id+"F0.wireOp",EDGE,"90fbf2e0-ce94-4077-ba36-f7078a65e9f6.9.0.11"),sQuery(id+"F0.wireOp",EDGE,"90fbf2e0-ce94-4077-ba36-f7078a65e9f6.10.0.0"),sQuery(id+"F0.wireOp",EDGE,"90fbf2e0-ce94-4077-ba36-f7078a65e9f6.10.0.1"),sQuery(id+"F0.wireOp",EDGE,"90fbf2e0-ce94-4077-ba36-f7078a65e9f6.10.0.2"),sQuery(id+"F0.wireOp",EDGE,"90fbf2e0-ce94-4077-ba36-f7078a65e9f6.10.0.3"),sQuery(id+"F0.wireOp",EDGE,"90fbf2e0-ce94-4077-ba36-f7078a65e9f6.10.0.4"),sQuery(id+"F0.wireOp",EDGE,"90fbf2e0-ce94-4077-ba36-f7078a65e9f6.10.0.5"),sQuery(id+"F0.wireOp",EDGE,"90fbf2e0-ce94-4077-ba36-f7078a65e9f6.10.0.6"),sQuery(id+"F0.wireOp",EDGE,"90fbf2e0-ce94-4077-ba36-f7078a65e9f6.10.0.7"),sQuery(id+"F0.wireOp",EDGE,"90fbf2e0-ce94-4077-ba36-f7078a65e9f6.10.0.8"),sQuery(id+"F0.wireOp",EDGE,"90fbf2e0-ce94-4077-ba36-f7078a65e9f6.10.0.9"),sQuery(id+"F0.wireOp",EDGE,"90fbf2e0-ce94-4077-ba36-f7078a65e9f6.10.0.10"),sQuery(id+"F0.wireOp",EDGE,"90fbf2e0-ce94-4077-ba36-f7078a65e9f6.10.0.11"),sQuery(id+"F0.wireOp",EDGE,"ef05f06f-9539-49a4-bbe1-e5de78f87bac.1.0.0"),sQuery(id+"F0.wireOp",EDGE,"ef05f06f-9539-49a4-bbe1-e5de78f87bac.1.0.1"),sQuery(id+"F0.wireOp",EDGE,"ef05f06f-9539-49a4-bbe1-e5de78f87bac.1.0.2"),sQuery(id+"F0.wireOp",EDGE,"ef05f06f-9539-49a4-bbe1-e5de78f87bac.1.0.3"),sQuery(id+"F0.wireOp",EDGE,"ef05f06f-9539-49a4-bbe1-e5de78f87bac.1.0.4"),sQuery(id+"F0.wireOp",EDGE,"ef05f06f-9539-49a4-bbe1-e5de78f87bac.1.0.5"),sQuery(id+"F0.wireOp",EDGE,"ef05f06f-9539-49a4-bbe1-e5de78f87bac.1.0.6"),sQuery(id+"F0.wireOp",EDGE,"ef05f06f-9539-49a4-bbe1-e5de78f87bac.1.0.7"),sQuery(id+"F0.wireOp",EDGE,"ef05f06f-9539-49a4-bbe1-e5de78f87bac.1.0.8"),sQuery(id+"F0.wireOp",EDGE,"ef05f06f-9539-49a4-bbe1-e5de78f87bac.1.0.9"),sQuery(id+"F0.wireOp",EDGE,"ef05f06f-9539-49a4-bbe1-e5de78f87bac.1.0.10"),sQuery(id+"F0.wireOp",EDGE,"ef05f06f-9539-49a4-bbe1-e5de78f87bac.1.0.11"),sQuery(id+"F0.wireOp",EDGE,"ef05f06f-9539-49a4-bbe1-e5de78f87bac.2.0.0"),sQuery(id+"F0.wireOp",EDGE,"ef05f06f-9539-49a4-bbe1-e5de78f87bac.2.0.1"),sQuery(id+"F0.wireOp",EDGE,"ef05f06f-9539-49a4-bbe1-e5de78f87bac.2.0.2"),sQuery(id+"F0.wireOp",EDGE,"ef05f06f-9539-49a4-bbe1-e5de78f87bac.2.0.3"),sQuery(id+"F0.wireOp",EDGE,"ef05f06f-9539-49a4-bbe1-e5de78f87bac.2.0.4"),sQuery(id+"F0.wireOp",EDGE,"ef05f06f-9539-49a4-bbe1-e5de78f87bac.2.0.5"),sQuery(id+"F0.wireOp",EDGE,"ef05f06f-9539-49a4-bbe1-e5de78f87bac.2.0.6"),sQuery(id+"F0.wireOp",EDGE,"ef05f06f-9539-49a4-bbe1-e5de78f87bac.2.0.7"),sQuery(id+"F0.wireOp",EDGE,"ef05f06f-9539-49a4-bbe1-e5de78f87bac.2.0.8"),sQuery(id+"F0.wireOp",EDGE,"ef05f06f-9539-49a4-bbe1-e5de78f87bac.2.0.9"),sQuery(id+"F0.wireOp",EDGE,"ef05f06f-9539-49a4-bbe1-e5de78f87bac.2.0.10"),sQuery(id+"F0.wireOp",EDGE,"ef05f06f-9539-49a4-bbe1-e5de78f87bac.2.0.11"),sQuery(id+"F0.wireOp",EDGE,"ef05f06f-9539-49a4-bbe1-e5de78f87bac.3.0.0"),sQuery(id+"F0.wireOp",EDGE,"ef05f06f-9539-49a4-bbe1-e5de78f87bac.3.0.1"),sQuery(id+"F0.wireOp",EDGE,"ef05f06f-9539-49a4-bbe1-e5de78f87bac.3.0.2"),sQuery(id+"F0.wireOp",EDGE,"ef05f06f-9539-49a4-bbe1-e5de78f87bac.3.0.3"),sQuery(id+"F0.wireOp",EDGE,"ef05f06f-9539-49a4-bbe1-e5de78f87bac.3.0.4"),sQuery(id+"F0.wireOp",EDGE,"ef05f06f-9539-49a4-bbe1-e5de78f87bac.3.0.5"),sQuery(id+"F0.wireOp",EDGE,"ef05f06f-9539-49a4-bbe1-e5de78f87bac.3.0.6"),sQuery(id+"F0.wireOp",EDGE,"ef05f06f-9539-49a4-bbe1-e5de78f87bac.3.0.7"),sQuery(id+"F0.wireOp",EDGE,"ef05f06f-9539-49a4-bbe1-e5de78f87bac.3.0.8"),sQuery(id+"F0.wireOp",EDGE,"ef05f06f-9539-49a4-bbe1-e5de78f87bac.3.0.9"),sQuery(id+"F0.wireOp",EDGE,"ef05f06f-9539-49a4-bbe1-e5de78f87bac.3.0.10"),sQuery(id+"F0.wireOp",EDGE,"ef05f06f-9539-49a4-bbe1-e5de78f87bac.3.0.11"),sQuery(id+"F0.wireOp",EDGE,"ef05f06f-9539-49a4-bbe1-e5de78f87bac.4.0.0"),sQuery(id+"F0.wireOp",EDGE,"ef05f06f-9539-49a4-bbe1-e5de78f87bac.4.0.1"),sQuery(id+"F0.wireOp",EDGE,"ef05f06f-9539-49a4-bbe1-e5de78f87bac.4.0.2"),sQuery(id+"F0.wireOp",EDGE,"ef05f06f-9539-49a4-bbe1-e5de78f87bac.4.0.3"),sQuery(id+"F0.wireOp",EDGE,"ef05f06f-9539-49a4-bbe1-e5de78f87bac.4.0.4"),sQuery(id+"F0.wireOp",EDGE,"ef05f06f-9539-49a4-bbe1-e5de78f87bac.4.0.5"),sQuery(id+"F0.wireOp",EDGE,"ef05f06f-9539-49a4-bbe1-e5de78f87bac.4.0.6"),sQuery(id+"F0.wireOp",EDGE,"ef05f06f-9539-49a4-bbe1-e5de78f87bac.4.0.7"),sQuery(id+"F0.wireOp",EDGE,"ef05f06f-9539-49a4-bbe1-e5de78f87bac.4.0.8"),sQuery(id+"F0.wireOp",EDGE,"ef05f06f-9539-49a4-bbe1-e5de78f87bac.4.0.9"),sQuery(id+"F0.wireOp",EDGE,"ef05f06f-9539-49a4-bbe1-e5de78f87bac.4.0.10"),sQuery(id+"F0.wireOp",EDGE,"ef05f06f-9539-49a4-bbe1-e5de78f87bac.4.0.11"),sQuery(id+"F0.wireOp",EDGE,"ef05f06f-9539-49a4-bbe1-e5de78f87bac.5.0.0"),sQuery(id+"F0.wireOp",EDGE,"ef05f06f-9539-49a4-bbe1-e5de78f87bac.5.0.1"),sQuery(id+"F0.wireOp",EDGE,"ef05f06f-9539-49a4-bbe1-e5de78f87bac.5.0.2"),sQuery(id+"F0.wireOp",EDGE,"ef05f06f-9539-49a4-bbe1-e5de78f87bac.5.0.3"),sQuery(id+"F0.wireOp",EDGE,"ef05f06f-9539-49a4-bbe1-e5de78f87bac.5.0.4"),sQuery(id+"F0.wireOp",EDGE,"ef05f06f-9539-49a4-bbe1-e5de78f87bac.5.0.5"),sQuery(id+"F0.wireOp",EDGE,"ef05f06f-9539-49a4-bbe1-e5de78f87bac.5.0.6"),sQuery(id+"F0.wireOp",EDGE,"ef05f06f-9539-49a4-bbe1-e5de78f87bac.5.0.7"),sQuery(id+"F0.wireOp",EDGE,"ef05f06f-9539-49a4-bbe1-e5de78f87bac.5.0.8"),sQuery(id+"F0.wireOp",EDGE,"ef05f06f-9539-49a4-bbe1-e5de78f87bac.5.0.9"),sQuery(id+"F0.wireOp",EDGE,"ef05f06f-9539-49a4-bbe1-e5de78f87bac.5.0.10"),sQuery(id+"F0.wireOp",EDGE,"ef05f06f-9539-49a4-bbe1-e5de78f87bac.5.0.11"),sQuery(id+"F0.wireOp",EDGE,"ef05f06f-9539-49a4-bbe1-e5de78f87bac.6.0.0"),sQuery(id+"F0.wireOp",EDGE,"ef05f06f-9539-49a4-bbe1-e5de78f87bac.6.0.1"),sQuery(id+"F0.wireOp",EDGE,"ef05f06f-9539-49a4-bbe1-e5de78f87bac.6.0.2"),sQuery(id+"F0.wireOp",EDGE,"ef05f06f-9539-49a4-bbe1-e5de78f87bac.6.0.3"),sQuery(id+"F0.wireOp",EDGE,"ef05f06f-9539-49a4-bbe1-e5de78f87bac.6.0.4"),sQuery(id+"F0.wireOp",EDGE,"ef05f06f-9539-49a4-bbe1-e5de78f87bac.6.0.5"),sQuery(id+"F0.wireOp",EDGE,"ef05f06f-9539-49a4-bbe1-e5de78f87bac.6.0.6"),sQuery(id+"F0.wireOp",EDGE,"ef05f06f-9539-49a4-bbe1-e5de78f87bac.6.0.7"),sQuery(id+"F0.wireOp",EDGE,"ef05f06f-9539-49a4-bbe1-e5de78f87bac.6.0.8"),sQuery(id+"F0.wireOp",EDGE,"ef05f06f-9539-49a4-bbe1-e5de78f87bac.6.0.9"),sQuery(id+"F0.wireOp",EDGE,"ef05f06f-9539-49a4-bbe1-e5de78f87bac.6.0.10"),sQuery(id+"F0.wireOp",EDGE,"ef05f06f-9539-49a4-bbe1-e5de78f87bac.6.0.11"),sQuery(id+"F0.wireOp",EDGE,"ef05f06f-9539-49a4-bbe1-e5de78f87bac.7.0.0"),sQuery(id+"F0.wireOp",EDGE,"ef05f06f-9539-49a4-bbe1-e5de78f87bac.7.0.1"),sQuery(id+"F0.wireOp",EDGE,"ef05f06f-9539-49a4-bbe1-e5de78f87bac.7.0.2"),sQuery(id+"F0.wireOp",EDGE,"ef05f06f-9539-49a4-bbe1-e5de78f87bac.7.0.3"),sQuery(id+"F0.wireOp",EDGE,"ef05f06f-9539-49a4-bbe1-e5de78f87bac.7.0.4"),sQuery(id+"F0.wireOp",EDGE,"ef05f06f-9539-49a4-bbe1-e5de78f87bac.7.0.5"),sQuery(id+"F0.wireOp",EDGE,"ef05f06f-9539-49a4-bbe1-e5de78f87bac.7.0.6"),sQuery(id+"F0.wireOp",EDGE,"ef05f06f-9539-49a4-bbe1-e5de78f87bac.7.0.7"),sQuery(id+"F0.wireOp",EDGE,"ef05f06f-9539-49a4-bbe1-e5de78f87bac.7.0.8"),sQuery(id+"F0.wireOp",EDGE,"ef05f06f-9539-49a4-bbe1-e5de78f87bac.7.0.9"),sQuery(id+"F0.wireOp",EDGE,"ef05f06f-9539-49a4-bbe1-e5de78f87bac.7.0.10"),sQuery(id+"F0.wireOp",EDGE,"ef05f06f-9539-49a4-bbe1-e5de78f87bac.7.0.11"),sQuery(id+"F0.wireOp",EDGE,"ef05f06f-9539-49a4-bbe1-e5de78f87bac.8.0.0"),sQuery(id+"F0.wireOp",EDGE,"ef05f06f-9539-49a4-bbe1-e5de78f87bac.8.0.1"),sQuery(id+"F0.wireOp",EDGE,"ef05f06f-9539-49a4-bbe1-e5de78f87bac.8.0.2"),sQuery(id+"F0.wireOp",EDGE,"ef05f06f-9539-49a4-bbe1-e5de78f87bac.8.0.3"),sQuery(id+"F0.wireOp",EDGE,"ef05f06f-9539-49a4-bbe1-e5de78f87bac.8.0.4"),sQuery(id+"F0.wireOp",EDGE,"ef05f06f-9539-49a4-bbe1-e5de78f87bac.8.0.5"),sQuery(id+"F0.wireOp",EDGE,"ef05f06f-9539-49a4-bbe1-e5de78f87bac.8.0.6"),sQuery(id+"F0.wireOp",EDGE,"ef05f06f-9539-49a4-bbe1-e5de78f87bac.8.0.7"),sQuery(id+"F0.wireOp",EDGE,"ef05f06f-9539-49a4-bbe1-e5de78f87bac.8.0.8"),sQuery(id+"F0.wireOp",EDGE,"ef05f06f-9539-49a4-bbe1-e5de78f87bac.8.0.9"),sQuery(id+"F0.wireOp",EDGE,"ef05f06f-9539-49a4-bbe1-e5de78f87bac.8.0.10"),sQuery(id+"F0.wireOp",EDGE,"ef05f06f-9539-49a4-bbe1-e5de78f87bac.8.0.11"),sQuery(id+"F0.wireOp",EDGE,"ef05f06f-9539-49a4-bbe1-e5de78f87bac.9.0.0"),sQuery(id+"F0.wireOp",EDGE,"ef05f06f-9539-49a4-bbe1-e5de78f87bac.9.0.1"),sQuery(id+"F0.wireOp",EDGE,"ef05f06f-9539-49a4-bbe1-e5de78f87bac.9.0.2"),sQuery(id+"F0.wireOp",EDGE,"ef05f06f-9539-49a4-bbe1-e5de78f87bac.9.0.3"),sQuery(id+"F0.wireOp",EDGE,"ef05f06f-9539-49a4-bbe1-e5de78f87bac.9.0.4"),sQuery(id+"F0.wireOp",EDGE,"ef05f06f-9539-49a4-bbe1-e5de78f87bac.9.0.5"),sQuery(id+"F0.wireOp",EDGE,"ef05f06f-9539-49a4-bbe1-e5de78f87bac.9.0.6"),sQuery(id+"F0.wireOp",EDGE,"ef05f06f-9539-49a4-bbe1-e5de78f87bac.9.0.7"),sQuery(id+"F0.wireOp",EDGE,"ef05f06f-9539-49a4-bbe1-e5de78f87bac.9.0.8"),sQuery(id+"F0.wireOp",EDGE,"ef05f06f-9539-49a4-bbe1-e5de78f87bac.9.0.9"),sQuery(id+"F0.wireOp",EDGE,"ef05f06f-9539-49a4-bbe1-e5de78f87bac.9.0.10"),sQuery(id+"F0.wireOp",EDGE,"ef05f06f-9539-49a4-bbe1-e5de78f87bac.9.0.11"),sQuery(id+"F0.wireOp",EDGE,"ef05f06f-9539-49a4-bbe1-e5de78f87bac.10.0.0"),sQuery(id+"F0.wireOp",EDGE,"ef05f06f-9539-49a4-bbe1-e5de78f87bac.10.0.1"),sQuery(id+"F0.wireOp",EDGE,"ef05f06f-9539-49a4-bbe1-e5de78f87bac.10.0.2"),sQuery(id+"F0.wireOp",EDGE,"ef05f06f-9539-49a4-bbe1-e5de78f87bac.10.0.3"),sQuery(id+"F0.wireOp",EDGE,"ef05f06f-9539-49a4-bbe1-e5de78f87bac.10.0.4"),sQuery(id+"F0.wireOp",EDGE,"ef05f06f-9539-49a4-bbe1-e5de78f87bac.10.0.5"),sQuery(id+"F0.wireOp",EDGE,"ef05f06f-9539-49a4-bbe1-e5de78f87bac.10.0.6"),sQuery(id+"F0.wireOp",EDGE,"ef05f06f-9539-49a4-bbe1-e5de78f87bac.10.0.7"),sQuery(id+"F0.wireOp",EDGE,"ef05f06f-9539-49a4-bbe1-e5de78f87bac.10.0.8"),sQuery(id+"F0.wireOp",EDGE,"ef05f06f-9539-49a4-bbe1-e5de78f87bac.10.0.9"),sQuery(id+"F0.wireOp",EDGE,"ef05f06f-9539-49a4-bbe1-e5de78f87bac.10.0.10"),sQuery(id+"F0.wireOp",EDGE,"ef05f06f-9539-49a4-bbe1-e5de78f87bac.10.0.11"),sQuery(id+"F0.wireOp",EDGE,"OJy4rNNo-w8Xi-PtYp-78KY-KX9WQq1O9zWX"),sQuery(id+"F0.wireOp",EDGE,"6ad1825e-1499-4b2d-8658-c8d5a4458ecc.filletArc"),sQuery(id+"F0.wireOp",EDGE,"0e28861b-0804-44a8-a45e-df2b0c80d6fb.filletArc"),sQuery(id+"F0.wireOp",EDGE,"69729d80-6c64-417c-b4d8-b2ce01de760d.filletArc"),sQuery(id+"F0.wireOp",EDGE,"57ece835-d495-4d14-92ee-c9d50648b8c1.filletArc")])],"isStart":false});
            var sketch = newSketch(context, id + "F4", { "sketchPlane" : qUnion([Q0])});
            skLineSegment(sketch, "E20", {"start": v(-95.21, 140.42) * mm, "end": v(57.19, 140.42) * mm});
            skLineSegment(sketch, "E21", {"start": v(-95.21, 140.42) * mm, "end": v(-95.21, 89.62) * mm});
            skLineSegment(sketch, "E22", {"start": v(-95.21, 89.62) * mm, "end": v(57.19, 89.62) * mm});
            skLineSegment(sketch, "E23", {"start": v(57.19, 89.62) * mm, "end": v(57.19, 140.42) * mm});
            skSolve(sketch);
        }
        {
            var Q0;
            Q0 = qSketchRegion(id + "F4", true);
            extrude(context, id + "F5", {"entities" : qUnion([Q0]), "operationType" : NewBodyOperationType.ADD, "depth" : 12.7 * mm});
        }
        {
            var Q0;
            Q0=makeQuery(id+"F5.opExtrude","CAP_FACE",FACE,{"disambiguationData":[OSD([sQuery(id+"F4.wireOp",EDGE,"E20"),sQuery(id+"F4.wireOp",EDGE,"E21"),sQuery(id+"F4.wireOp",EDGE,"E22"),sQuery(id+"F4.wireOp",EDGE,"E23")])],"isStart":false});
            var sketch = newSketch(context, id + "F6", { "sketchPlane" : qUnion([Q0])});
            skLineSegment(sketch, "E24", {"start": v(-19.01, 140.42) * mm, "end": v(6.39, 140.42) * mm});
            skLineSegment(sketch, "E25", {"start": v(6.39, 140.42) * mm, "end": v(6.39, 127.72) * mm});
            skLineSegment(sketch, "E26", {"start": v(6.39, 127.72) * mm, "end": v(-44.41, 127.72) * mm});
            skLineSegment(sketch, "E27", {"start": v(-44.41, 127.72) * mm, "end": v(-44.41, 140.42) * mm});
            skLineSegment(sketch, "E28", {"start": v(-44.41, 140.42) * mm, "end": v(-19.01, 140.42) * mm});
            skSolve(sketch);
        }
        {
            var Q0;
            Q0=makeQuery(id+"F6.imprint","IMPRINT",FACE,{"disambiguationData":[TD([[makeQuery(id+"F6.imprint","IMPRINT",EDGE,{"derivedFrom":sQuery(id+"F6.wireOp",EDGE,"E24")}),-1.0]])]});
            extrude(context, id + "F7", {"entities" : qUnion([Q0]), "operationType" : NewBodyOperationType.REMOVE, "oppositeDirection" : true, "depth" : 6.35 * mm});
        }
        {
            var Q0;
            Q0=makeQuery(id+"F7.boolean.opBoolean","COPY",FACE,{"derivedFrom":makeQuery(id+"F7.opExtrude","CAP_FACE",FACE,{"disambiguationData":[OSD([sQuery(id+"F6.wireOp",EDGE,"E24"),sQuery(id+"F6.wireOp",EDGE,"E25"),sQuery(id+"F6.wireOp",EDGE,"E26"),sQuery(id+"F6.wireOp",EDGE,"E27"),sQuery(id+"F6.wireOp",EDGE,"E28")])],"isStart":false})});
            var sketch = newSketch(context, id + "F8", { "sketchPlane" : qUnion([Q0])});
            skLineSegment(sketch, "E29", {"start": v(-44.41, 140.42) * mm, "end": v(-40.38, 140.42) * mm});
            skLineSegment(sketch, "E30", {"start": v(-40.38, 140.42) * mm, "end": v(-44.41, 140.42) * mm});
            skLineSegment(sketch, "E31.bottom", {"start": v(-40.38, 131.53) * mm, "end": v(-35.75, 131.53) * mm});
            skLineSegment(sketch, "E31.top", {"start": v(-40.38, 136.15) * mm, "end": v(-35.75, 136.15) * mm});
            skLineSegment(sketch, "E31.right", {"start": v(-35.75, 131.53) * mm, "end": v(-35.75, 136.15) * mm});
            skLineSegment(sketch, "E32", {"start": v(-40.38, 131.53) * mm, "end": v(-40.38, 136.15) * mm});
            skLineSegment(sketch, "E33.1.0.0", {"start": v(-23.05, 131.53) * mm, "end": v(-23.05, 136.15) * mm});
            skLineSegment(sketch, "E33.1.0.1", {"start": v(-27.68, 136.15) * mm, "end": v(-23.05, 136.15) * mm});
            skLineSegment(sketch, "E33.1.0.2", {"start": v(-27.68, 131.53) * mm, "end": v(-27.68, 136.15) * mm});
            skLineSegment(sketch, "E33.1.0.3", {"start": v(-27.68, 131.53) * mm, "end": v(-23.05, 131.53) * mm});
            skLineSegment(sketch, "E33.2.0.0", {"start": v(-10.35, 131.53) * mm, "end": v(-10.35, 136.15) * mm});
            skLineSegment(sketch, "E33.2.0.1", {"start": v(-14.98, 136.15) * mm, "end": v(-10.35, 136.15) * mm});
            skLineSegment(sketch, "E33.2.0.2", {"start": v(-14.98, 131.53) * mm, "end": v(-14.98, 136.15) * mm});
            skLineSegment(sketch, "E33.2.0.3", {"start": v(-14.98, 131.53) * mm, "end": v(-10.35, 131.53) * mm});
            skLineSegment(sketch, "E33.3.0.0", {"start": v(2.35, 131.53) * mm, "end": v(2.35, 136.15) * mm});
            skLineSegment(sketch, "E33.3.0.1", {"start": v(-2.28, 136.15) * mm, "end": v(2.35, 136.15) * mm});
            skLineSegment(sketch, "E33.3.0.2", {"start": v(-2.28, 131.53) * mm, "end": v(-2.28, 136.15) * mm});
            skLineSegment(sketch, "E33.3.0.3", {"start": v(-2.28, 131.53) * mm, "end": v(2.35, 131.53) * mm});
            skLineSegment(sketch, "E33.direction1", {"start": v(-35.75, 131.53) * mm, "end": v(-23.05, 131.53) * mm, "construction": true});
            skSolve(sketch);
        }
        {
            var Q0;
            Q0=makeQuery(id+"F3.opExtrude","SWEPT_EDGE",EDGE,{"disambiguationData":[OSD([sQuery(id+"F0.wireOp",EDGE,"E0.1.1.0"),sQuery(id+"F0.wireOp",EDGE,"E0.1.1.1"),sQuery(id+"F1.wireOp",EDGE,"E16"),sQuery(id+"F1.wireOp",EDGE,"E19")])]});
            var Q1;
            Q1=makeQuery(id+"F3.opExtrude","SWEPT_EDGE",EDGE,{"disambiguationData":[OSD([sQuery(id+"F1.wireOp",EDGE,"E16"),sQuery(id+"F1.wireOp",EDGE,"E17")])]});
            var Q2;
            Q2=makeQuery(id+"F3.opExtrude","SWEPT_EDGE",EDGE,{"disambiguationData":[OSD([sQuery(id+"F1.wireOp",EDGE,"E17"),sQuery(id+"F1.wireOp",EDGE,"E18")])]});
            var Q3;
            Q3=makeQuery(id+"F3.opExtrude","SWEPT_EDGE",EDGE,{"disambiguationData":[OSD([sQuery(id+"F1.wireOp",EDGE,"E18"),sQuery(id+"F1.wireOp",EDGE,"E19")])]});
            fillet(context, id + "F9", {"entities" : qUnion([Q0, Q1, Q2, Q3]), "radius" : 5.08 * mm, "tangentPropagation" : true, "allowEdgeOverflow" : false});
        }
        {
            var Q0;
            Q0 = qSketchRegion(id + "F8", true);
            extrude(context, id + "F10", {"entities" : qUnion([Q0]), "operationType" : NewBodyOperationType.REMOVE, "oppositeDirection" : true, "depth" : 6.35 * mm});
        }
        {
            var Q0;
            Q0=makeQuery(id+"F3.opExtrude","CAP_FACE",FACE,{"disambiguationData":[OSD([sQuery(id+"F1.wireOp",EDGE,"E11"),sQuery(id+"F1.wireOp",EDGE,"E12"),sQuery(id+"F1.wireOp",EDGE,"E13"),sQuery(id+"F1.wireOp",EDGE,"E14"),sQuery(id+"F1.wireOp",EDGE,"E16"),sQuery(id+"F1.wireOp",EDGE,"E17"),sQuery(id+"F1.wireOp",EDGE,"E18"),sQuery(id+"F1.wireOp",EDGE,"E19")])],"isStart":false});
            var sketch = newSketch(context, id + "F11", { "sketchPlane" : qUnion([Q0])});
            skLineSegment(sketch, "E34", {"start": v(-38.06, 140.42) * mm, "end": v(-44.41, 140.42) * mm});
            skLineSegment(sketch, "E35", {"start": v(-44.41, 140.42) * mm, "end": v(-44.41, 153.12) * mm});
            skLineSegment(sketch, "E36", {"start": v(-44.41, 153.12) * mm, "end": v(-38.06, 153.12) * mm});
            skLineSegment(sketch, "E37", {"start": v(-38.06, 153.12) * mm, "end": v(-38.06, 140.42) * mm});
            skLineSegment(sketch, "E38.MirrorCS", {"start": v(0.04, 153.12) * mm, "end": v(0.04, 140.42) * mm});
            skLineSegment(sketch, "E39.MirrorCS", {"start": v(0.04, 140.42) * mm, "end": v(6.39, 140.42) * mm});
            skLineSegment(sketch, "E40.MirrorCS", {"start": v(6.39, 140.42) * mm, "end": v(6.39, 153.12) * mm});
            skLineSegment(sketch, "E41.MirrorCS", {"start": v(6.39, 153.12) * mm, "end": v(0.04, 153.12) * mm});
            skLineSegment(sketch, "E42.MirrorCS", {"start": v(6.39, 89.62) * mm, "end": v(6.39, 76.92) * mm});
            skLineSegment(sketch, "E43.MirrorCS", {"start": v(0.04, 76.92) * mm, "end": v(0.04, 89.62) * mm});
            skLineSegment(sketch, "E44.MirrorCS", {"start": v(6.39, 76.92) * mm, "end": v(0.04, 76.92) * mm});
            skLineSegment(sketch, "E45.MirrorCS", {"start": v(-44.41, 76.92) * mm, "end": v(-38.06, 76.92) * mm});
            skLineSegment(sketch, "E46.MirrorCS", {"start": v(-38.06, 76.92) * mm, "end": v(-38.06, 89.62) * mm});
            skLineSegment(sketch, "E47.MirrorCS", {"start": v(-44.41, 89.62) * mm, "end": v(-44.41, 76.92) * mm});
            skLineSegment(sketch, "E48.MirrorCS", {"start": v(-38.06, 89.62) * mm, "end": v(-44.41, 89.62) * mm});
            skLineSegment(sketch, "E49.MirrorCS", {"start": v(0.04, 89.62) * mm, "end": v(6.39, 89.62) * mm});
            skSolve(sketch);
        }
        {
            var Q0;
            Q0 = qSketchRegion(id + "F11", true);
            extrude(context, id + "F12", {"entities" : qUnion([Q0]), "operationType" : NewBodyOperationType.ADD, "oppositeDirection" : true, "depth" : 6.35 * mm});
        }
        {
            var Q0;
            Q0=makeQuery(id+"F12.opExtrude","SWEPT_FACE",FACE,{"disambiguationData":[OSD([sQuery(id+"F11.wireOp",EDGE,"E42.MirrorCS")])]});
            var sketch = newSketch(context, id + "F13", { "sketchPlane" : qUnion([Q0])});
            skLineSegment(sketch, "E50", {"start": v(-20.32, 85.81) * mm, "end": v(-25.4, 85.81) * mm});
            skLineSegment(sketch, "E51", {"start": v(-25.4, 85.81) * mm, "end": v(-25.4, 76.92) * mm});
            skLineSegment(sketch, "E52", {"start": v(-20.32, 85.81) * mm, "end": v(-25.4, 76.92) * mm});
            skLineSegment(sketch, "E53", {"start": v(-23.32, 144.23) * mm, "end": v(-28.4, 144.23) * mm});
            skLineSegment(sketch, "E54", {"start": v(-23.32, 144.23) * mm, "end": v(-28.4, 153.12) * mm});
            skLineSegment(sketch, "E55.trimOffspring", {"start": v(-28.4, 144.23) * mm, "end": v(-28.4, 153.12) * mm});
            skSolve(sketch);
        }
        {
            var Q0;
            Q0=makeQuery(id+"F13.imprint","IMPRINT",FACE,{"disambiguationData":[TD([[makeQuery(id+"F13.imprint","IMPRINT",EDGE,{"derivedFrom":sQuery(id+"F13.wireOp",EDGE,"E53")}),-1.0]])]});
            var Q1;
            Q1=makeQuery(id+"F13.imprint","IMPRINT",FACE,{"disambiguationData":[TD([[makeQuery(id+"F13.imprint","IMPRINT",EDGE,{"derivedFrom":sQuery(id+"F13.wireOp",EDGE,"E50")}),1.0]])]});
            extrude(context, id + "F14", {"entities" : qUnion([Q0, Q1]), "operationType" : NewBodyOperationType.ADD, "oppositeDirection" : true, "depth" : 6.35 * mm});
        }
        {
            var Q0;
            Q0=makeQuery(id+"F12.opExtrude","SWEPT_FACE",FACE,{"disambiguationData":[OSD([sQuery(id+"F11.wireOp",EDGE,"E47.MirrorCS")])]});
            var sketch = newSketch(context, id + "F15", { "sketchPlane" : qUnion([Q0])});
            skLineSegment(sketch, "E56", {"start": v(25.4, 76.92) * mm, "end": v(25.4, 85.81) * mm});
            skLineSegment(sketch, "E57", {"start": v(25.4, 85.81) * mm, "end": v(20.32, 85.81) * mm});
            skLineSegment(sketch, "E58", {"start": v(20.32, 85.81) * mm, "end": v(25.4, 76.92) * mm});
            skLineSegment(sketch, "E59.MirrorCS", {"start": v(28.4, 153.12) * mm, "end": v(28.4, 144.23) * mm});
            skLineSegment(sketch, "E60.MirrorCS", {"start": v(28.4, 144.23) * mm, "end": v(23.32, 144.23) * mm});
            skLineSegment(sketch, "E61.MirrorCS", {"start": v(23.32, 144.23) * mm, "end": v(28.4, 153.12) * mm});
            skSolve(sketch);
        }
        {
            var Q0;
            Q0 = qSketchRegion(id + "F15", true);
            extrude(context, id + "F16", {"entities" : qUnion([Q0]), "operationType" : NewBodyOperationType.ADD, "oppositeDirection" : true, "depth" : 6.35 * mm});
        }
        {
            var Q0;
            Q0=makeQuery(id+"F12.boolean.opBoolean","MERGE",FACE,{"derivedFrom":[makeQuery(id+"F3.opExtrude","CAP_FACE",FACE,{"disambiguationData":[OSD([sQuery(id+"F1.wireOp",EDGE,"E11"),sQuery(id+"F1.wireOp",EDGE,"E12"),sQuery(id+"F1.wireOp",EDGE,"E13"),sQuery(id+"F1.wireOp",EDGE,"E14"),sQuery(id+"F1.wireOp",EDGE,"E16"),sQuery(id+"F1.wireOp",EDGE,"E17"),sQuery(id+"F1.wireOp",EDGE,"E18"),sQuery(id+"F1.wireOp",EDGE,"E19")])],"isStart":false}),makeQuery(id+"F12.opExtrude","CAP_FACE",FACE,{"disambiguationData":[OSD([sQuery(id+"F11.wireOp",EDGE,"E34"),sQuery(id+"F11.wireOp",EDGE,"E35"),sQuery(id+"F11.wireOp",EDGE,"E36"),sQuery(id+"F11.wireOp",EDGE,"E37")])],"isStart":true}),makeQuery(id+"F12.opExtrude","CAP_FACE",FACE,{"disambiguationData":[OSD([sQuery(id+"F11.wireOp",EDGE,"E38.MirrorCS"),sQuery(id+"F11.wireOp",EDGE,"E39.MirrorCS"),sQuery(id+"F11.wireOp",EDGE,"E40.MirrorCS"),sQuery(id+"F11.wireOp",EDGE,"E41.MirrorCS")])],"isStart":true}),makeQuery(id+"F12.opExtrude","CAP_FACE",FACE,{"disambiguationData":[OSD([sQuery(id+"F11.wireOp",EDGE,"E42.MirrorCS"),sQuery(id+"F11.wireOp",EDGE,"E43.MirrorCS"),sQuery(id+"F11.wireOp",EDGE,"E44.MirrorCS"),sQuery(id+"F11.wireOp",EDGE,"E49.MirrorCS")])],"isStart":true}),makeQuery(id+"F12.opExtrude","CAP_FACE",FACE,{"disambiguationData":[OSD([sQuery(id+"F11.wireOp",EDGE,"E45.MirrorCS"),sQuery(id+"F11.wireOp",EDGE,"E46.MirrorCS"),sQuery(id+"F11.wireOp",EDGE,"E47.MirrorCS"),sQuery(id+"F11.wireOp",EDGE,"E48.MirrorCS")])],"isStart":true})]});
            var sketch = newSketch(context, id + "F17", { "sketchPlane" : qUnion([Q0])});
            skLineSegment(sketch, "E62", {"start": v(-95.21, 140.42) * mm, "end": v(-95.21, 89.62) * mm});
            skLineSegment(sketch, "E63", {"start": v(-95.21, 89.62) * mm, "end": v(-98.8, 90.9) * mm});
            skLineSegment(sketch, "E64", {"start": v(-98.8, 90.9) * mm, "end": v(-98.8, 139.15) * mm});
            skLineSegment(sketch, "E65", {"start": v(-98.8, 139.15) * mm, "end": v(-95.21, 140.42) * mm});
            skSolve(sketch);
        }
        {
            var Q0;
            Q0 = qSketchRegion(id + "F17", true);
            extrude(context, id + "F18", {"entities" : qUnion([Q0]), "operationType" : NewBodyOperationType.REMOVE, "oppositeDirection" : true, "depth" : 12.7 * mm});
        }
        {
            var Q0;
            Q0=makeQuery(id+"F2.opExtrude","CAP_FACE",FACE,{"disambiguationData":[OSD([sQuery(id+"F0.wireOp",EDGE,"e2akh6Oa-UBHa-86Pb-ZkKs-OABukGgOBKLV.right"),sQuery(id+"F0.wireOp",EDGE,"RFzYo0nL-dbGn-g4QQ-aZl6-wjgrSkBCbLW4.bottom"),sQuery(id+"F0.wireOp",EDGE,"RFzYo0nL-dbGn-g4QQ-aZl6-wjgrSkBCbLW4.top"),sQuery(id+"F0.wireOp",EDGE,"RFzYo0nL-dbGn-g4QQ-aZl6-wjgrSkBCbLW4.left"),sQuery(id+"F0.wireOp",EDGE,"RFzYo0nL-dbGn-g4QQ-aZl6-wjgrSkBCbLW4.right"),sQuery(id+"F0.wireOp",EDGE,"7c84c30b-10c3-426a-8278-929d31200ebf.0.1.0"),sQuery(id+"F0.wireOp",EDGE,"7c84c30b-10c3-426a-8278-929d31200ebf.0.1.1"),sQuery(id+"F0.wireOp",EDGE,"7c84c30b-10c3-426a-8278-929d31200ebf.0.1.2"),sQuery(id+"F0.wireOp",EDGE,"7c84c30b-10c3-426a-8278-929d31200ebf.0.1.3"),sQuery(id+"F0.wireOp",EDGE,"7c84c30b-10c3-426a-8278-929d31200ebf.0.2.0"),sQuery(id+"F0.wireOp",EDGE,"7c84c30b-10c3-426a-8278-929d31200ebf.0.2.1"),sQuery(id+"F0.wireOp",EDGE,"7c84c30b-10c3-426a-8278-929d31200ebf.0.2.2"),sQuery(id+"F0.wireOp",EDGE,"7c84c30b-10c3-426a-8278-929d31200ebf.0.2.3"),sQuery(id+"F0.wireOp",EDGE,"7c84c30b-10c3-426a-8278-929d31200ebf.0.3.0"),sQuery(id+"F0.wireOp",EDGE,"7c84c30b-10c3-426a-8278-929d31200ebf.0.3.1"),sQuery(id+"F0.wireOp",EDGE,"7c84c30b-10c3-426a-8278-929d31200ebf.0.3.2"),sQuery(id+"F0.wireOp",EDGE,"7c84c30b-10c3-426a-8278-929d31200ebf.0.3.3"),sQuery(id+"F0.wireOp",EDGE,"7c84c30b-10c3-426a-8278-929d31200ebf.0.4.0"),sQuery(id+"F0.wireOp",EDGE,"7c84c30b-10c3-426a-8278-929d31200ebf.0.4.1"),sQuery(id+"F0.wireOp",EDGE,"7c84c30b-10c3-426a-8278-929d31200ebf.0.4.2"),sQuery(id+"F0.wireOp",EDGE,"7c84c30b-10c3-426a-8278-929d31200ebf.0.4.3"),sQuery(id+"F0.wireOp",EDGE,"7c84c30b-10c3-426a-8278-929d31200ebf.0.5.0"),sQuery(id+"F0.wireOp",EDGE,"7c84c30b-10c3-426a-8278-929d31200ebf.0.5.1"),sQuery(id+"F0.wireOp",EDGE,"7c84c30b-10c3-426a-8278-929d31200ebf.0.5.2"),sQuery(id+"F0.wireOp",EDGE,"7c84c30b-10c3-426a-8278-929d31200ebf.0.5.3"),sQuery(id+"F0.wireOp",EDGE,"7c84c30b-10c3-426a-8278-929d31200ebf.0.6.0"),sQuery(id+"F0.wireOp",EDGE,"7c84c30b-10c3-426a-8278-929d31200ebf.0.6.1"),sQuery(id+"F0.wireOp",EDGE,"7c84c30b-10c3-426a-8278-929d31200ebf.0.6.2"),sQuery(id+"F0.wireOp",EDGE,"7c84c30b-10c3-426a-8278-929d31200ebf.0.6.3"),sQuery(id+"F0.wireOp",EDGE,"7c84c30b-10c3-426a-8278-929d31200ebf.0.7.0"),sQuery(id+"F0.wireOp",EDGE,"7c84c30b-10c3-426a-8278-929d31200ebf.0.7.1"),sQuery(id+"F0.wireOp",EDGE,"7c84c30b-10c3-426a-8278-929d31200ebf.0.7.2"),sQuery(id+"F0.wireOp",EDGE,"7c84c30b-10c3-426a-8278-929d31200ebf.0.7.3"),sQuery(id+"F0.wireOp",EDGE,"7c84c30b-10c3-426a-8278-929d31200ebf.0.8.0"),sQuery(id+"F0.wireOp",EDGE,"7c84c30b-10c3-426a-8278-929d31200ebf.0.8.1"),sQuery(id+"F0.wireOp",EDGE,"7c84c30b-10c3-426a-8278-929d31200ebf.0.8.2"),sQuery(id+"F0.wireOp",EDGE,"7c84c30b-10c3-426a-8278-929d31200ebf.0.8.3"),sQuery(id+"F0.wireOp",EDGE,"7c84c30b-10c3-426a-8278-929d31200ebf.0.9.0"),sQuery(id+"F0.wireOp",EDGE,"7c84c30b-10c3-426a-8278-929d31200ebf.0.9.1"),sQuery(id+"F0.wireOp",EDGE,"7c84c30b-10c3-426a-8278-929d31200ebf.0.9.2"),sQuery(id+"F0.wireOp",EDGE,"7c84c30b-10c3-426a-8278-929d31200ebf.0.9.3"),sQuery(id+"F0.wireOp",EDGE,"7c84c30b-10c3-426a-8278-929d31200ebf.0.10.0"),sQuery(id+"F0.wireOp",EDGE,"7c84c30b-10c3-426a-8278-929d31200ebf.0.10.1"),sQuery(id+"F0.wireOp",EDGE,"7c84c30b-10c3-426a-8278-929d31200ebf.0.10.2"),sQuery(id+"F0.wireOp",EDGE,"7c84c30b-10c3-426a-8278-929d31200ebf.0.10.3"),sQuery(id+"F0.wireOp",EDGE,"7c84c30b-10c3-426a-8278-929d31200ebf.0.11.0"),sQuery(id+"F0.wireOp",EDGE,"7c84c30b-10c3-426a-8278-929d31200ebf.0.11.1"),sQuery(id+"F0.wireOp",EDGE,"7c84c30b-10c3-426a-8278-929d31200ebf.0.11.2"),sQuery(id+"F0.wireOp",EDGE,"7c84c30b-10c3-426a-8278-929d31200ebf.0.11.3"),sQuery(id+"F0.wireOp",EDGE,"7c84c30b-10c3-426a-8278-929d31200ebf.0.12.0"),sQuery(id+"F0.wireOp",EDGE,"7c84c30b-10c3-426a-8278-929d31200ebf.0.12.1"),sQuery(id+"F0.wireOp",EDGE,"7c84c30b-10c3-426a-8278-929d31200ebf.0.12.2"),sQuery(id+"F0.wireOp",EDGE,"7c84c30b-10c3-426a-8278-929d31200ebf.0.12.3"),sQuery(id+"F0.wireOp",EDGE,"7c84c30b-10c3-426a-8278-929d31200ebf.0.13.0"),sQuery(id+"F0.wireOp",EDGE,"7c84c30b-10c3-426a-8278-929d31200ebf.0.13.1"),sQuery(id+"F0.wireOp",EDGE,"7c84c30b-10c3-426a-8278-929d31200ebf.0.13.2"),sQuery(id+"F0.wireOp",EDGE,"7c84c30b-10c3-426a-8278-929d31200ebf.0.13.3"),sQuery(id+"F0.wireOp",EDGE,"7c84c30b-10c3-426a-8278-929d31200ebf.0.14.0"),sQuery(id+"F0.wireOp",EDGE,"7c84c30b-10c3-426a-8278-929d31200ebf.0.14.1"),sQuery(id+"F0.wireOp",EDGE,"7c84c30b-10c3-426a-8278-929d31200ebf.0.14.2"),sQuery(id+"F0.wireOp",EDGE,"7c84c30b-10c3-426a-8278-929d31200ebf.0.14.3"),sQuery(id+"F0.wireOp",EDGE,"7c84c30b-10c3-426a-8278-929d31200ebf.0.15.0"),sQuery(id+"F0.wireOp",EDGE,"7c84c30b-10c3-426a-8278-929d31200ebf.0.15.1"),sQuery(id+"F0.wireOp",EDGE,"7c84c30b-10c3-426a-8278-929d31200ebf.0.15.2"),sQuery(id+"F0.wireOp",EDGE,"7c84c30b-10c3-426a-8278-929d31200ebf.0.15.3"),sQuery(id+"F0.wireOp",EDGE,"7c84c30b-10c3-426a-8278-929d31200ebf.0.16.0"),sQuery(id+"F0.wireOp",EDGE,"7c84c30b-10c3-426a-8278-929d31200ebf.0.16.1"),sQuery(id+"F0.wireOp",EDGE,"7c84c30b-10c3-426a-8278-929d31200ebf.0.16.2"),sQuery(id+"F0.wireOp",EDGE,"7c84c30b-10c3-426a-8278-929d31200ebf.0.16.3"),sQuery(id+"F0.wireOp",EDGE,"7c84c30b-10c3-426a-8278-929d31200ebf.0.17.0"),sQuery(id+"F0.wireOp",EDGE,"7c84c30b-10c3-426a-8278-929d31200ebf.0.17.1"),sQuery(id+"F0.wireOp",EDGE,"7c84c30b-10c3-426a-8278-929d31200ebf.0.17.2"),sQuery(id+"F0.wireOp",EDGE,"7c84c30b-10c3-426a-8278-929d31200ebf.0.17.3"),sQuery(id+"F0.wireOp",EDGE,"7c84c30b-10c3-426a-8278-929d31200ebf.0.18.0"),sQuery(id+"F0.wireOp",EDGE,"7c84c30b-10c3-426a-8278-929d31200ebf.0.18.1"),sQuery(id+"F0.wireOp",EDGE,"7c84c30b-10c3-426a-8278-929d31200ebf.0.18.2"),sQuery(id+"F0.wireOp",EDGE,"7c84c30b-10c3-426a-8278-929d31200ebf.0.18.3"),sQuery(id+"F0.wireOp",EDGE,"7c84c30b-10c3-426a-8278-929d31200ebf.0.19.0"),sQuery(id+"F0.wireOp",EDGE,"7c84c30b-10c3-426a-8278-929d31200ebf.0.19.1"),sQuery(id+"F0.wireOp",EDGE,"7c84c30b-10c3-426a-8278-929d31200ebf.0.19.2"),sQuery(id+"F0.wireOp",EDGE,"7c84c30b-10c3-426a-8278-929d31200ebf.0.19.3"),sQuery(id+"F0.wireOp",EDGE,"7c84c30b-10c3-426a-8278-929d31200ebf.0.20.0"),sQuery(id+"F0.wireOp",EDGE,"7c84c30b-10c3-426a-8278-929d31200ebf.0.20.1"),sQuery(id+"F0.wireOp",EDGE,"7c84c30b-10c3-426a-8278-929d31200ebf.0.20.2"),sQuery(id+"F0.wireOp",EDGE,"7c84c30b-10c3-426a-8278-929d31200ebf.0.20.3"),sQuery(id+"F0.wireOp",EDGE,"7c84c30b-10c3-426a-8278-929d31200ebf.0.21.0"),sQuery(id+"F0.wireOp",EDGE,"7c84c30b-10c3-426a-8278-929d31200ebf.0.21.1"),sQuery(id+"F0.wireOp",EDGE,"7c84c30b-10c3-426a-8278-929d31200ebf.0.21.2"),sQuery(id+"F0.wireOp",EDGE,"7c84c30b-10c3-426a-8278-929d31200ebf.0.21.3"),sQuery(id+"F0.wireOp",EDGE,"7c84c30b-10c3-426a-8278-929d31200ebf.0.22.0"),sQuery(id+"F0.wireOp",EDGE,"7c84c30b-10c3-426a-8278-929d31200ebf.0.22.1"),sQuery(id+"F0.wireOp",EDGE,"7c84c30b-10c3-426a-8278-929d31200ebf.0.22.2"),sQuery(id+"F0.wireOp",EDGE,"7c84c30b-10c3-426a-8278-929d31200ebf.0.22.3"),sQuery(id+"F0.wireOp",EDGE,"7c84c30b-10c3-426a-8278-929d31200ebf.0.23.0"),sQuery(id+"F0.wireOp",EDGE,"7c84c30b-10c3-426a-8278-929d31200ebf.0.23.1"),sQuery(id+"F0.wireOp",EDGE,"7c84c30b-10c3-426a-8278-929d31200ebf.0.23.2"),sQuery(id+"F0.wireOp",EDGE,"7c84c30b-10c3-426a-8278-929d31200ebf.0.23.3"),sQuery(id+"F0.wireOp",EDGE,"7c84c30b-10c3-426a-8278-929d31200ebf.0.24.0"),sQuery(id+"F0.wireOp",EDGE,"7c84c30b-10c3-426a-8278-929d31200ebf.0.24.1"),sQuery(id+"F0.wireOp",EDGE,"7c84c30b-10c3-426a-8278-929d31200ebf.0.24.2"),sQuery(id+"F0.wireOp",EDGE,"7c84c30b-10c3-426a-8278-929d31200ebf.0.24.3"),sQuery(id+"F0.wireOp",EDGE,"7c84c30b-10c3-426a-8278-929d31200ebf.0.25.0"),sQuery(id+"F0.wireOp",EDGE,"7c84c30b-10c3-426a-8278-929d31200ebf.0.25.1"),sQuery(id+"F0.wireOp",EDGE,"7c84c30b-10c3-426a-8278-929d31200ebf.0.25.2"),sQuery(id+"F0.wireOp",EDGE,"7c84c30b-10c3-426a-8278-929d31200ebf.0.25.3"),sQuery(id+"F0.wireOp",EDGE,"7c84c30b-10c3-426a-8278-929d31200ebf.1.0.0"),sQuery(id+"F0.wireOp",EDGE,"7c84c30b-10c3-426a-8278-929d31200ebf.1.0.1"),sQuery(id+"F0.wireOp",EDGE,"7c84c30b-10c3-426a-8278-929d31200ebf.1.0.2"),sQuery(id+"F0.wireOp",EDGE,"7c84c30b-10c3-426a-8278-929d31200ebf.1.0.3"),sQuery(id+"F0.wireOp",EDGE,"7c84c30b-10c3-426a-8278-929d31200ebf.1.1.0"),sQuery(id+"F0.wireOp",EDGE,"7c84c30b-10c3-426a-8278-929d31200ebf.1.1.1"),sQuery(id+"F0.wireOp",EDGE,"7c84c30b-10c3-426a-8278-929d31200ebf.1.1.2"),sQuery(id+"F0.wireOp",EDGE,"7c84c30b-10c3-426a-8278-929d31200ebf.1.1.3"),sQuery(id+"F0.wireOp",EDGE,"7c84c30b-10c3-426a-8278-929d31200ebf.1.2.0"),sQuery(id+"F0.wireOp",EDGE,"7c84c30b-10c3-426a-8278-929d31200ebf.1.2.1"),sQuery(id+"F0.wireOp",EDGE,"7c84c30b-10c3-426a-8278-929d31200ebf.1.2.2"),sQuery(id+"F0.wireOp",EDGE,"7c84c30b-10c3-426a-8278-929d31200ebf.1.2.3"),sQuery(id+"F0.wireOp",EDGE,"7c84c30b-10c3-426a-8278-929d31200ebf.1.3.0"),sQuery(id+"F0.wireOp",EDGE,"7c84c30b-10c3-426a-8278-929d31200ebf.1.3.1"),sQuery(id+"F0.wireOp",EDGE,"7c84c30b-10c3-426a-8278-929d31200ebf.1.3.2"),sQuery(id+"F0.wireOp",EDGE,"7c84c30b-10c3-426a-8278-929d31200ebf.1.3.3"),sQuery(id+"F0.wireOp",EDGE,"7c84c30b-10c3-426a-8278-929d31200ebf.1.4.0"),sQuery(id+"F0.wireOp",EDGE,"7c84c30b-10c3-426a-8278-929d31200ebf.1.4.1"),sQuery(id+"F0.wireOp",EDGE,"7c84c30b-10c3-426a-8278-929d31200ebf.1.4.2"),sQuery(id+"F0.wireOp",EDGE,"7c84c30b-10c3-426a-8278-929d31200ebf.1.4.3"),sQuery(id+"F0.wireOp",EDGE,"7c84c30b-10c3-426a-8278-929d31200ebf.1.5.0"),sQuery(id+"F0.wireOp",EDGE,"7c84c30b-10c3-426a-8278-929d31200ebf.1.5.1"),sQuery(id+"F0.wireOp",EDGE,"7c84c30b-10c3-426a-8278-929d31200ebf.1.5.2"),sQuery(id+"F0.wireOp",EDGE,"7c84c30b-10c3-426a-8278-929d31200ebf.1.5.3"),sQuery(id+"F0.wireOp",EDGE,"7c84c30b-10c3-426a-8278-929d31200ebf.1.6.0"),sQuery(id+"F0.wireOp",EDGE,"7c84c30b-10c3-426a-8278-929d31200ebf.1.6.1"),sQuery(id+"F0.wireOp",EDGE,"7c84c30b-10c3-426a-8278-929d31200ebf.1.6.2"),sQuery(id+"F0.wireOp",EDGE,"7c84c30b-10c3-426a-8278-929d31200ebf.1.6.3"),sQuery(id+"F0.wireOp",EDGE,"7c84c30b-10c3-426a-8278-929d31200ebf.1.7.0"),sQuery(id+"F0.wireOp",EDGE,"7c84c30b-10c3-426a-8278-929d31200ebf.1.7.1"),sQuery(id+"F0.wireOp",EDGE,"7c84c30b-10c3-426a-8278-929d31200ebf.1.7.2"),sQuery(id+"F0.wireOp",EDGE,"7c84c30b-10c3-426a-8278-929d31200ebf.1.7.3"),sQuery(id+"F0.wireOp",EDGE,"7c84c30b-10c3-426a-8278-929d31200ebf.1.8.0"),sQuery(id+"F0.wireOp",EDGE,"7c84c30b-10c3-426a-8278-929d31200ebf.1.8.1"),sQuery(id+"F0.wireOp",EDGE,"7c84c30b-10c3-426a-8278-929d31200ebf.1.8.2"),sQuery(id+"F0.wireOp",EDGE,"7c84c30b-10c3-426a-8278-929d31200ebf.1.8.3"),sQuery(id+"F0.wireOp",EDGE,"7c84c30b-10c3-426a-8278-929d31200ebf.1.9.0"),sQuery(id+"F0.wireOp",EDGE,"7c84c30b-10c3-426a-8278-929d31200ebf.1.9.1"),sQuery(id+"F0.wireOp",EDGE,"7c84c30b-10c3-426a-8278-929d31200ebf.1.9.2"),sQuery(id+"F0.wireOp",EDGE,"7c84c30b-10c3-426a-8278-929d31200ebf.1.9.3"),sQuery(id+"F0.wireOp",EDGE,"7c84c30b-10c3-426a-8278-929d31200ebf.1.10.0"),sQuery(id+"F0.wireOp",EDGE,"7c84c30b-10c3-426a-8278-929d31200ebf.1.10.1"),sQuery(id+"F0.wireOp",EDGE,"7c84c30b-10c3-426a-8278-929d31200ebf.1.10.2"),sQuery(id+"F0.wireOp",EDGE,"7c84c30b-10c3-426a-8278-929d31200ebf.1.10.3"),sQuery(id+"F0.wireOp",EDGE,"7c84c30b-10c3-426a-8278-929d31200ebf.1.11.0"),sQuery(id+"F0.wireOp",EDGE,"7c84c30b-10c3-426a-8278-929d31200ebf.1.11.1"),sQuery(id+"F0.wireOp",EDGE,"7c84c30b-10c3-426a-8278-929d31200ebf.1.11.2"),sQuery(id+"F0.wireOp",EDGE,"7c84c30b-10c3-426a-8278-929d31200ebf.1.11.3"),sQuery(id+"F0.wireOp",EDGE,"7c84c30b-10c3-426a-8278-929d31200ebf.1.12.0"),sQuery(id+"F0.wireOp",EDGE,"7c84c30b-10c3-426a-8278-929d31200ebf.1.12.1"),sQuery(id+"F0.wireOp",EDGE,"7c84c30b-10c3-426a-8278-929d31200ebf.1.12.2"),sQuery(id+"F0.wireOp",EDGE,"7c84c30b-10c3-426a-8278-929d31200ebf.1.12.3"),sQuery(id+"F0.wireOp",EDGE,"7c84c30b-10c3-426a-8278-929d31200ebf.1.13.0"),sQuery(id+"F0.wireOp",EDGE,"7c84c30b-10c3-426a-8278-929d31200ebf.1.13.1"),sQuery(id+"F0.wireOp",EDGE,"7c84c30b-10c3-426a-8278-929d31200ebf.1.13.2"),sQuery(id+"F0.wireOp",EDGE,"7c84c30b-10c3-426a-8278-929d31200ebf.1.13.3"),sQuery(id+"F0.wireOp",EDGE,"7c84c30b-10c3-426a-8278-929d31200ebf.1.14.0"),sQuery(id+"F0.wireOp",EDGE,"7c84c30b-10c3-426a-8278-929d31200ebf.1.14.1"),sQuery(id+"F0.wireOp",EDGE,"7c84c30b-10c3-426a-8278-929d31200ebf.1.14.2"),sQuery(id+"F0.wireOp",EDGE,"7c84c30b-10c3-426a-8278-929d31200ebf.1.14.3"),sQuery(id+"F0.wireOp",EDGE,"7c84c30b-10c3-426a-8278-929d31200ebf.1.15.0"),sQuery(id+"F0.wireOp",EDGE,"7c84c30b-10c3-426a-8278-929d31200ebf.1.15.1"),sQuery(id+"F0.wireOp",EDGE,"7c84c30b-10c3-426a-8278-929d31200ebf.1.15.2"),sQuery(id+"F0.wireOp",EDGE,"7c84c30b-10c3-426a-8278-929d31200ebf.1.15.3"),sQuery(id+"F0.wireOp",EDGE,"7c84c30b-10c3-426a-8278-929d31200ebf.1.16.0"),sQuery(id+"F0.wireOp",EDGE,"7c84c30b-10c3-426a-8278-929d31200ebf.1.16.1"),sQuery(id+"F0.wireOp",EDGE,"7c84c30b-10c3-426a-8278-929d31200ebf.1.16.2"),sQuery(id+"F0.wireOp",EDGE,"7c84c30b-10c3-426a-8278-929d31200ebf.1.16.3"),sQuery(id+"F0.wireOp",EDGE,"7c84c30b-10c3-426a-8278-929d31200ebf.1.17.0"),sQuery(id+"F0.wireOp",EDGE,"7c84c30b-10c3-426a-8278-929d31200ebf.1.17.1"),sQuery(id+"F0.wireOp",EDGE,"7c84c30b-10c3-426a-8278-929d31200ebf.1.17.2"),sQuery(id+"F0.wireOp",EDGE,"7c84c30b-10c3-426a-8278-929d31200ebf.1.17.3"),sQuery(id+"F0.wireOp",EDGE,"7c84c30b-10c3-426a-8278-929d31200ebf.1.18.0"),sQuery(id+"F0.wireOp",EDGE,"7c84c30b-10c3-426a-8278-929d31200ebf.1.18.1"),sQuery(id+"F0.wireOp",EDGE,"7c84c30b-10c3-426a-8278-929d31200ebf.1.18.2"),sQuery(id+"F0.wireOp",EDGE,"7c84c30b-10c3-426a-8278-929d31200ebf.1.18.3"),sQuery(id+"F0.wireOp",EDGE,"7c84c30b-10c3-426a-8278-929d31200ebf.1.19.0"),sQuery(id+"F0.wireOp",EDGE,"7c84c30b-10c3-426a-8278-929d31200ebf.1.19.1"),sQuery(id+"F0.wireOp",EDGE,"7c84c30b-10c3-426a-8278-929d31200ebf.1.19.2"),sQuery(id+"F0.wireOp",EDGE,"7c84c30b-10c3-426a-8278-929d31200ebf.1.19.3"),sQuery(id+"F0.wireOp",EDGE,"7c84c30b-10c3-426a-8278-929d31200ebf.1.20.0"),sQuery(id+"F0.wireOp",EDGE,"7c84c30b-10c3-426a-8278-929d31200ebf.1.20.1"),sQuery(id+"F0.wireOp",EDGE,"7c84c30b-10c3-426a-8278-929d31200ebf.1.20.2"),sQuery(id+"F0.wireOp",EDGE,"7c84c30b-10c3-426a-8278-929d31200ebf.1.20.3"),sQuery(id+"F0.wireOp",EDGE,"7c84c30b-10c3-426a-8278-929d31200ebf.1.21.0"),sQuery(id+"F0.wireOp",EDGE,"7c84c30b-10c3-426a-8278-929d31200ebf.1.21.1"),sQuery(id+"F0.wireOp",EDGE,"7c84c30b-10c3-426a-8278-929d31200ebf.1.21.2"),sQuery(id+"F0.wireOp",EDGE,"7c84c30b-10c3-426a-8278-929d31200ebf.1.21.3"),sQuery(id+"F0.wireOp",EDGE,"7c84c30b-10c3-426a-8278-929d31200ebf.1.22.0"),sQuery(id+"F0.wireOp",EDGE,"7c84c30b-10c3-426a-8278-929d31200ebf.1.22.1"),sQuery(id+"F0.wireOp",EDGE,"7c84c30b-10c3-426a-8278-929d31200ebf.1.22.2"),sQuery(id+"F0.wireOp",EDGE,"7c84c30b-10c3-426a-8278-929d31200ebf.1.22.3"),sQuery(id+"F0.wireOp",EDGE,"7c84c30b-10c3-426a-8278-929d31200ebf.1.23.0"),sQuery(id+"F0.wireOp",EDGE,"7c84c30b-10c3-426a-8278-929d31200ebf.1.23.1"),sQuery(id+"F0.wireOp",EDGE,"7c84c30b-10c3-426a-8278-929d31200ebf.1.23.2"),sQuery(id+"F0.wireOp",EDGE,"7c84c30b-10c3-426a-8278-929d31200ebf.1.23.3"),sQuery(id+"F0.wireOp",EDGE,"7c84c30b-10c3-426a-8278-929d31200ebf.1.24.0"),sQuery(id+"F0.wireOp",EDGE,"7c84c30b-10c3-426a-8278-929d31200ebf.1.24.1"),sQuery(id+"F0.wireOp",EDGE,"7c84c30b-10c3-426a-8278-929d31200ebf.1.24.2"),sQuery(id+"F0.wireOp",EDGE,"7c84c30b-10c3-426a-8278-929d31200ebf.1.24.3"),sQuery(id+"F0.wireOp",EDGE,"7c84c30b-10c3-426a-8278-929d31200ebf.1.25.0"),sQuery(id+"F0.wireOp",EDGE,"7c84c30b-10c3-426a-8278-929d31200ebf.1.25.1"),sQuery(id+"F0.wireOp",EDGE,"7c84c30b-10c3-426a-8278-929d31200ebf.1.25.2"),sQuery(id+"F0.wireOp",EDGE,"7c84c30b-10c3-426a-8278-929d31200ebf.1.25.3"),sQuery(id+"F0.wireOp",EDGE,"7c84c30b-10c3-426a-8278-929d31200ebf.2.0.0"),sQuery(id+"F0.wireOp",EDGE,"7c84c30b-10c3-426a-8278-929d31200ebf.2.0.1"),sQuery(id+"F0.wireOp",EDGE,"7c84c30b-10c3-426a-8278-929d31200ebf.2.0.2"),sQuery(id+"F0.wireOp",EDGE,"7c84c30b-10c3-426a-8278-929d31200ebf.2.0.3"),sQuery(id+"F0.wireOp",EDGE,"7c84c30b-10c3-426a-8278-929d31200ebf.2.1.0"),sQuery(id+"F0.wireOp",EDGE,"7c84c30b-10c3-426a-8278-929d31200ebf.2.1.1"),sQuery(id+"F0.wireOp",EDGE,"7c84c30b-10c3-426a-8278-929d31200ebf.2.1.2"),sQuery(id+"F0.wireOp",EDGE,"7c84c30b-10c3-426a-8278-929d31200ebf.2.1.3"),sQuery(id+"F0.wireOp",EDGE,"7c84c30b-10c3-426a-8278-929d31200ebf.2.2.0"),sQuery(id+"F0.wireOp",EDGE,"7c84c30b-10c3-426a-8278-929d31200ebf.2.2.1"),sQuery(id+"F0.wireOp",EDGE,"7c84c30b-10c3-426a-8278-929d31200ebf.2.2.2"),sQuery(id+"F0.wireOp",EDGE,"7c84c30b-10c3-426a-8278-929d31200ebf.2.2.3"),sQuery(id+"F0.wireOp",EDGE,"7c84c30b-10c3-426a-8278-929d31200ebf.2.3.0"),sQuery(id+"F0.wireOp",EDGE,"7c84c30b-10c3-426a-8278-929d31200ebf.2.3.1"),sQuery(id+"F0.wireOp",EDGE,"7c84c30b-10c3-426a-8278-929d31200ebf.2.3.2"),sQuery(id+"F0.wireOp",EDGE,"7c84c30b-10c3-426a-8278-929d31200ebf.2.3.3"),sQuery(id+"F0.wireOp",EDGE,"7c84c30b-10c3-426a-8278-929d31200ebf.2.4.0"),sQuery(id+"F0.wireOp",EDGE,"7c84c30b-10c3-426a-8278-929d31200ebf.2.4.1"),sQuery(id+"F0.wireOp",EDGE,"7c84c30b-10c3-426a-8278-929d31200ebf.2.4.2"),sQuery(id+"F0.wireOp",EDGE,"7c84c30b-10c3-426a-8278-929d31200ebf.2.4.3"),sQuery(id+"F0.wireOp",EDGE,"7c84c30b-10c3-426a-8278-929d31200ebf.2.5.0"),sQuery(id+"F0.wireOp",EDGE,"7c84c30b-10c3-426a-8278-929d31200ebf.2.5.1"),sQuery(id+"F0.wireOp",EDGE,"7c84c30b-10c3-426a-8278-929d31200ebf.2.5.2"),sQuery(id+"F0.wireOp",EDGE,"7c84c30b-10c3-426a-8278-929d31200ebf.2.5.3"),sQuery(id+"F0.wireOp",EDGE,"7c84c30b-10c3-426a-8278-929d31200ebf.2.6.0"),sQuery(id+"F0.wireOp",EDGE,"7c84c30b-10c3-426a-8278-929d31200ebf.2.6.1"),sQuery(id+"F0.wireOp",EDGE,"7c84c30b-10c3-426a-8278-929d31200ebf.2.6.2"),sQuery(id+"F0.wireOp",EDGE,"7c84c30b-10c3-426a-8278-929d31200ebf.2.6.3"),sQuery(id+"F0.wireOp",EDGE,"7c84c30b-10c3-426a-8278-929d31200ebf.2.7.0"),sQuery(id+"F0.wireOp",EDGE,"7c84c30b-10c3-426a-8278-929d31200ebf.2.7.1"),sQuery(id+"F0.wireOp",EDGE,"7c84c30b-10c3-426a-8278-929d31200ebf.2.7.2"),sQuery(id+"F0.wireOp",EDGE,"7c84c30b-10c3-426a-8278-929d31200ebf.2.7.3"),sQuery(id+"F0.wireOp",EDGE,"7c84c30b-10c3-426a-8278-929d31200ebf.2.8.0"),sQuery(id+"F0.wireOp",EDGE,"7c84c30b-10c3-426a-8278-929d31200ebf.2.8.1"),sQuery(id+"F0.wireOp",EDGE,"7c84c30b-10c3-426a-8278-929d31200ebf.2.8.2"),sQuery(id+"F0.wireOp",EDGE,"7c84c30b-10c3-426a-8278-929d31200ebf.2.8.3"),sQuery(id+"F0.wireOp",EDGE,"7c84c30b-10c3-426a-8278-929d31200ebf.2.9.0"),sQuery(id+"F0.wireOp",EDGE,"7c84c30b-10c3-426a-8278-929d31200ebf.2.9.1"),sQuery(id+"F0.wireOp",EDGE,"7c84c30b-10c3-426a-8278-929d31200ebf.2.9.2"),sQuery(id+"F0.wireOp",EDGE,"7c84c30b-10c3-426a-8278-929d31200ebf.2.9.3"),sQuery(id+"F0.wireOp",EDGE,"7c84c30b-10c3-426a-8278-929d31200ebf.2.10.0"),sQuery(id+"F0.wireOp",EDGE,"7c84c30b-10c3-426a-8278-929d31200ebf.2.10.1"),sQuery(id+"F0.wireOp",EDGE,"7c84c30b-10c3-426a-8278-929d31200ebf.2.10.2"),sQuery(id+"F0.wireOp",EDGE,"7c84c30b-10c3-426a-8278-929d31200ebf.2.10.3"),sQuery(id+"F0.wireOp",EDGE,"7c84c30b-10c3-426a-8278-929d31200ebf.2.11.0"),sQuery(id+"F0.wireOp",EDGE,"7c84c30b-10c3-426a-8278-929d31200ebf.2.11.1"),sQuery(id+"F0.wireOp",EDGE,"7c84c30b-10c3-426a-8278-929d31200ebf.2.11.2"),sQuery(id+"F0.wireOp",EDGE,"7c84c30b-10c3-426a-8278-929d31200ebf.2.11.3"),sQuery(id+"F0.wireOp",EDGE,"7c84c30b-10c3-426a-8278-929d31200ebf.2.12.0"),sQuery(id+"F0.wireOp",EDGE,"7c84c30b-10c3-426a-8278-929d31200ebf.2.12.1"),sQuery(id+"F0.wireOp",EDGE,"7c84c30b-10c3-426a-8278-929d31200ebf.2.12.2"),sQuery(id+"F0.wireOp",EDGE,"7c84c30b-10c3-426a-8278-929d31200ebf.2.12.3"),sQuery(id+"F0.wireOp",EDGE,"7c84c30b-10c3-426a-8278-929d31200ebf.2.13.0"),sQuery(id+"F0.wireOp",EDGE,"7c84c30b-10c3-426a-8278-929d31200ebf.2.13.1"),sQuery(id+"F0.wireOp",EDGE,"7c84c30b-10c3-426a-8278-929d31200ebf.2.13.2"),sQuery(id+"F0.wireOp",EDGE,"7c84c30b-10c3-426a-8278-929d31200ebf.2.13.3"),sQuery(id+"F0.wireOp",EDGE,"7c84c30b-10c3-426a-8278-929d31200ebf.2.14.0"),sQuery(id+"F0.wireOp",EDGE,"7c84c30b-10c3-426a-8278-929d31200ebf.2.14.1"),sQuery(id+"F0.wireOp",EDGE,"7c84c30b-10c3-426a-8278-929d31200ebf.2.14.2"),sQuery(id+"F0.wireOp",EDGE,"7c84c30b-10c3-426a-8278-929d31200ebf.2.14.3"),sQuery(id+"F0.wireOp",EDGE,"7c84c30b-10c3-426a-8278-929d31200ebf.2.15.0"),sQuery(id+"F0.wireOp",EDGE,"7c84c30b-10c3-426a-8278-929d31200ebf.2.15.1"),sQuery(id+"F0.wireOp",EDGE,"7c84c30b-10c3-426a-8278-929d31200ebf.2.15.2"),sQuery(id+"F0.wireOp",EDGE,"7c84c30b-10c3-426a-8278-929d31200ebf.2.15.3"),sQuery(id+"F0.wireOp",EDGE,"7c84c30b-10c3-426a-8278-929d31200ebf.2.16.0"),sQuery(id+"F0.wireOp",EDGE,"7c84c30b-10c3-426a-8278-929d31200ebf.2.16.1"),sQuery(id+"F0.wireOp",EDGE,"7c84c30b-10c3-426a-8278-929d31200ebf.2.16.2"),sQuery(id+"F0.wireOp",EDGE,"7c84c30b-10c3-426a-8278-929d31200ebf.2.16.3"),sQuery(id+"F0.wireOp",EDGE,"7c84c30b-10c3-426a-8278-929d31200ebf.2.17.0"),sQuery(id+"F0.wireOp",EDGE,"7c84c30b-10c3-426a-8278-929d31200ebf.2.17.1"),sQuery(id+"F0.wireOp",EDGE,"7c84c30b-10c3-426a-8278-929d31200ebf.2.17.2"),sQuery(id+"F0.wireOp",EDGE,"7c84c30b-10c3-426a-8278-929d31200ebf.2.17.3"),sQuery(id+"F0.wireOp",EDGE,"7c84c30b-10c3-426a-8278-929d31200ebf.2.18.0"),sQuery(id+"F0.wireOp",EDGE,"7c84c30b-10c3-426a-8278-929d31200ebf.2.18.1"),sQuery(id+"F0.wireOp",EDGE,"7c84c30b-10c3-426a-8278-929d31200ebf.2.18.2"),sQuery(id+"F0.wireOp",EDGE,"7c84c30b-10c3-426a-8278-929d31200ebf.2.18.3"),sQuery(id+"F0.wireOp",EDGE,"7c84c30b-10c3-426a-8278-929d31200ebf.2.19.0"),sQuery(id+"F0.wireOp",EDGE,"7c84c30b-10c3-426a-8278-929d31200ebf.2.19.1"),sQuery(id+"F0.wireOp",EDGE,"7c84c30b-10c3-426a-8278-929d31200ebf.2.19.2"),sQuery(id+"F0.wireOp",EDGE,"7c84c30b-10c3-426a-8278-929d31200ebf.2.19.3"),sQuery(id+"F0.wireOp",EDGE,"7c84c30b-10c3-426a-8278-929d31200ebf.2.20.0"),sQuery(id+"F0.wireOp",EDGE,"7c84c30b-10c3-426a-8278-929d31200ebf.2.20.1"),sQuery(id+"F0.wireOp",EDGE,"7c84c30b-10c3-426a-8278-929d31200ebf.2.20.2"),sQuery(id+"F0.wireOp",EDGE,"7c84c30b-10c3-426a-8278-929d31200ebf.2.20.3"),sQuery(id+"F0.wireOp",EDGE,"7c84c30b-10c3-426a-8278-929d31200ebf.2.21.0"),sQuery(id+"F0.wireOp",EDGE,"7c84c30b-10c3-426a-8278-929d31200ebf.2.21.1"),sQuery(id+"F0.wireOp",EDGE,"7c84c30b-10c3-426a-8278-929d31200ebf.2.21.2"),sQuery(id+"F0.wireOp",EDGE,"7c84c30b-10c3-426a-8278-929d31200ebf.2.21.3"),sQuery(id+"F0.wireOp",EDGE,"7c84c30b-10c3-426a-8278-929d31200ebf.2.22.0"),sQuery(id+"F0.wireOp",EDGE,"7c84c30b-10c3-426a-8278-929d31200ebf.2.22.1"),sQuery(id+"F0.wireOp",EDGE,"7c84c30b-10c3-426a-8278-929d31200ebf.2.22.2"),sQuery(id+"F0.wireOp",EDGE,"7c84c30b-10c3-426a-8278-929d31200ebf.2.22.3"),sQuery(id+"F0.wireOp",EDGE,"7c84c30b-10c3-426a-8278-929d31200ebf.2.23.0"),sQuery(id+"F0.wireOp",EDGE,"7c84c30b-10c3-426a-8278-929d31200ebf.2.23.1"),sQuery(id+"F0.wireOp",EDGE,"7c84c30b-10c3-426a-8278-929d31200ebf.2.23.2"),sQuery(id+"F0.wireOp",EDGE,"7c84c30b-10c3-426a-8278-929d31200ebf.2.23.3"),sQuery(id+"F0.wireOp",EDGE,"7c84c30b-10c3-426a-8278-929d31200ebf.2.24.0"),sQuery(id+"F0.wireOp",EDGE,"7c84c30b-10c3-426a-8278-929d31200ebf.2.24.1"),sQuery(id+"F0.wireOp",EDGE,"7c84c30b-10c3-426a-8278-929d31200ebf.2.24.2"),sQuery(id+"F0.wireOp",EDGE,"7c84c30b-10c3-426a-8278-929d31200ebf.2.24.3"),sQuery(id+"F0.wireOp",EDGE,"7c84c30b-10c3-426a-8278-929d31200ebf.2.25.0"),sQuery(id+"F0.wireOp",EDGE,"7c84c30b-10c3-426a-8278-929d31200ebf.2.25.1"),sQuery(id+"F0.wireOp",EDGE,"7c84c30b-10c3-426a-8278-929d31200ebf.2.25.2"),sQuery(id+"F0.wireOp",EDGE,"7c84c30b-10c3-426a-8278-929d31200ebf.2.25.3"),sQuery(id+"F0.wireOp",EDGE,"DqMKkSLq-MZEV-FMmD-DK04-qPwwkAkBIbn5"),sQuery(id+"F0.wireOp",EDGE,"b6izAig9-YVkh-wso9-hAal-lVyQwPKH0Rqq"),sQuery(id+"F0.wireOp",EDGE,"Ld8sGsMe-wxKW-HELd-rUX3-tJrgnMnEQjee"),sQuery(id+"F0.wireOp",EDGE,"KcqUpT09-MFPH-TNWY-efLy-ihoS9jBIaYSA"),sQuery(id+"F0.wireOp",EDGE,"E0.0.1.1"),sQuery(id+"F0.wireOp",EDGE,"E0.0.1.2"),sQuery(id+"F0.wireOp",EDGE,"E0.0.1.3"),sQuery(id+"F0.wireOp",EDGE,"E0.0.2.0"),sQuery(id+"F0.wireOp",EDGE,"E0.0.2.1"),sQuery(id+"F0.wireOp",EDGE,"E0.0.2.2"),sQuery(id+"F0.wireOp",EDGE,"E0.0.2.3"),sQuery(id+"F0.wireOp",EDGE,"E0.0.3.0"),sQuery(id+"F0.wireOp",EDGE,"E0.0.3.1"),sQuery(id+"F0.wireOp",EDGE,"E0.0.3.2"),sQuery(id+"F0.wireOp",EDGE,"E0.0.3.3"),sQuery(id+"F0.wireOp",EDGE,"E0.0.4.0"),sQuery(id+"F0.wireOp",EDGE,"E0.0.4.1"),sQuery(id+"F0.wireOp",EDGE,"E0.0.4.2"),sQuery(id+"F0.wireOp",EDGE,"E0.0.4.3"),sQuery(id+"F0.wireOp",EDGE,"E0.0.5.0"),sQuery(id+"F0.wireOp",EDGE,"E0.0.5.1"),sQuery(id+"F0.wireOp",EDGE,"E0.0.5.2"),sQuery(id+"F0.wireOp",EDGE,"E0.0.5.3"),sQuery(id+"F0.wireOp",EDGE,"E0.0.6.0"),sQuery(id+"F0.wireOp",EDGE,"E0.0.6.1"),sQuery(id+"F0.wireOp",EDGE,"E0.0.6.2"),sQuery(id+"F0.wireOp",EDGE,"E0.0.6.3"),sQuery(id+"F0.wireOp",EDGE,"E0.0.7.0"),sQuery(id+"F0.wireOp",EDGE,"E0.0.7.1"),sQuery(id+"F0.wireOp",EDGE,"E0.0.7.2"),sQuery(id+"F0.wireOp",EDGE,"E0.0.7.3"),sQuery(id+"F0.wireOp",EDGE,"E0.0.8.0"),sQuery(id+"F0.wireOp",EDGE,"E0.0.8.1"),sQuery(id+"F0.wireOp",EDGE,"E0.0.8.2"),sQuery(id+"F0.wireOp",EDGE,"E0.0.8.3"),sQuery(id+"F0.wireOp",EDGE,"E0.0.9.0"),sQuery(id+"F0.wireOp",EDGE,"E0.0.9.1"),sQuery(id+"F0.wireOp",EDGE,"E0.0.9.2"),sQuery(id+"F0.wireOp",EDGE,"E0.0.9.3"),sQuery(id+"F0.wireOp",EDGE,"E0.0.10.0"),sQuery(id+"F0.wireOp",EDGE,"E0.0.10.1"),sQuery(id+"F0.wireOp",EDGE,"E0.0.10.2"),sQuery(id+"F0.wireOp",EDGE,"E0.0.10.3"),sQuery(id+"F0.wireOp",EDGE,"E0.0.11.0"),sQuery(id+"F0.wireOp",EDGE,"E0.0.11.1"),sQuery(id+"F0.wireOp",EDGE,"E0.0.11.2"),sQuery(id+"F0.wireOp",EDGE,"E0.0.11.3"),sQuery(id+"F0.wireOp",EDGE,"E0.0.12.0"),sQuery(id+"F0.wireOp",EDGE,"E0.0.12.1"),sQuery(id+"F0.wireOp",EDGE,"E0.0.12.2"),sQuery(id+"F0.wireOp",EDGE,"E0.0.12.3"),sQuery(id+"F0.wireOp",EDGE,"E0.0.13.0"),sQuery(id+"F0.wireOp",EDGE,"E0.0.13.1"),sQuery(id+"F0.wireOp",EDGE,"E0.0.13.2"),sQuery(id+"F0.wireOp",EDGE,"E0.0.13.3"),sQuery(id+"F0.wireOp",EDGE,"E0.0.14.0"),sQuery(id+"F0.wireOp",EDGE,"E0.0.14.1"),sQuery(id+"F0.wireOp",EDGE,"E0.0.14.2"),sQuery(id+"F0.wireOp",EDGE,"E0.0.14.3"),sQuery(id+"F0.wireOp",EDGE,"E0.0.15.0"),sQuery(id+"F0.wireOp",EDGE,"E0.0.15.1"),sQuery(id+"F0.wireOp",EDGE,"E0.0.15.2"),sQuery(id+"F0.wireOp",EDGE,"E0.0.15.3"),sQuery(id+"F0.wireOp",EDGE,"E0.0.16.0"),sQuery(id+"F0.wireOp",EDGE,"E0.0.16.1"),sQuery(id+"F0.wireOp",EDGE,"E0.0.16.2"),sQuery(id+"F0.wireOp",EDGE,"E0.0.16.3"),sQuery(id+"F0.wireOp",EDGE,"E0.0.17.0"),sQuery(id+"F0.wireOp",EDGE,"E0.0.17.1"),sQuery(id+"F0.wireOp",EDGE,"E0.0.17.2"),sQuery(id+"F0.wireOp",EDGE,"E0.0.17.3"),sQuery(id+"F0.wireOp",EDGE,"E0.0.18.0"),sQuery(id+"F0.wireOp",EDGE,"E0.0.18.1"),sQuery(id+"F0.wireOp",EDGE,"E0.0.18.2"),sQuery(id+"F0.wireOp",EDGE,"E0.0.18.3"),sQuery(id+"F0.wireOp",EDGE,"E0.0.19.0"),sQuery(id+"F0.wireOp",EDGE,"E0.0.19.1"),sQuery(id+"F0.wireOp",EDGE,"E0.0.19.2"),sQuery(id+"F0.wireOp",EDGE,"E0.0.19.3"),sQuery(id+"F0.wireOp",EDGE,"E0.0.20.0"),sQuery(id+"F0.wireOp",EDGE,"E0.0.20.1"),sQuery(id+"F0.wireOp",EDGE,"E0.0.20.2"),sQuery(id+"F0.wireOp",EDGE,"E0.0.20.3"),sQuery(id+"F0.wireOp",EDGE,"E0.0.21.0"),sQuery(id+"F0.wireOp",EDGE,"E0.0.21.1"),sQuery(id+"F0.wireOp",EDGE,"E0.0.21.2"),sQuery(id+"F0.wireOp",EDGE,"E0.0.21.3"),sQuery(id+"F0.wireOp",EDGE,"E0.0.22.0"),sQuery(id+"F0.wireOp",EDGE,"E0.0.22.1"),sQuery(id+"F0.wireOp",EDGE,"E0.0.22.2"),sQuery(id+"F0.wireOp",EDGE,"E0.0.22.3"),sQuery(id+"F0.wireOp",EDGE,"E0.0.23.0"),sQuery(id+"F0.wireOp",EDGE,"E0.0.23.1"),sQuery(id+"F0.wireOp",EDGE,"E0.0.23.2"),sQuery(id+"F0.wireOp",EDGE,"E0.0.23.3"),sQuery(id+"F0.wireOp",EDGE,"E0.0.24.0"),sQuery(id+"F0.wireOp",EDGE,"E0.0.24.1"),sQuery(id+"F0.wireOp",EDGE,"E0.0.24.2"),sQuery(id+"F0.wireOp",EDGE,"E0.0.24.3"),sQuery(id+"F0.wireOp",EDGE,"E0.0.25.0"),sQuery(id+"F0.wireOp",EDGE,"E0.0.25.1"),sQuery(id+"F0.wireOp",EDGE,"E0.0.25.2"),sQuery(id+"F0.wireOp",EDGE,"E0.0.25.3"),sQuery(id+"F0.wireOp",EDGE,"E0.1.0.0"),sQuery(id+"F0.wireOp",EDGE,"E0.1.0.1"),sQuery(id+"F0.wireOp",EDGE,"E0.1.0.2"),sQuery(id+"F0.wireOp",EDGE,"E0.1.0.3"),sQuery(id+"F0.wireOp",EDGE,"E0.1.1.0"),sQuery(id+"F0.wireOp",EDGE,"E0.1.1.1"),sQuery(id+"F0.wireOp",EDGE,"E0.1.1.2"),sQuery(id+"F0.wireOp",EDGE,"E0.1.1.3"),sQuery(id+"F0.wireOp",EDGE,"E0.1.2.0"),sQuery(id+"F0.wireOp",EDGE,"E0.1.2.1"),sQuery(id+"F0.wireOp",EDGE,"E0.1.2.2"),sQuery(id+"F0.wireOp",EDGE,"E0.1.2.3"),sQuery(id+"F0.wireOp",EDGE,"E0.1.3.0"),sQuery(id+"F0.wireOp",EDGE,"E0.1.3.1"),sQuery(id+"F0.wireOp",EDGE,"E0.1.3.2"),sQuery(id+"F0.wireOp",EDGE,"E0.1.3.3"),sQuery(id+"F0.wireOp",EDGE,"E0.1.4.0"),sQuery(id+"F0.wireOp",EDGE,"E0.1.4.1"),sQuery(id+"F0.wireOp",EDGE,"E0.1.4.2"),sQuery(id+"F0.wireOp",EDGE,"E0.1.4.3"),sQuery(id+"F0.wireOp",EDGE,"E0.1.5.0"),sQuery(id+"F0.wireOp",EDGE,"E0.1.5.1"),sQuery(id+"F0.wireOp",EDGE,"E0.1.5.2"),sQuery(id+"F0.wireOp",EDGE,"E0.1.5.3"),sQuery(id+"F0.wireOp",EDGE,"E0.1.6.0"),sQuery(id+"F0.wireOp",EDGE,"E0.1.6.1"),sQuery(id+"F0.wireOp",EDGE,"E0.1.6.2"),sQuery(id+"F0.wireOp",EDGE,"E0.1.6.3"),sQuery(id+"F0.wireOp",EDGE,"E0.1.7.0"),sQuery(id+"F0.wireOp",EDGE,"E0.1.7.1"),sQuery(id+"F0.wireOp",EDGE,"E0.1.7.2"),sQuery(id+"F0.wireOp",EDGE,"E0.1.7.3"),sQuery(id+"F0.wireOp",EDGE,"E0.1.8.0"),sQuery(id+"F0.wireOp",EDGE,"E0.1.8.1"),sQuery(id+"F0.wireOp",EDGE,"E0.1.8.2"),sQuery(id+"F0.wireOp",EDGE,"E0.1.8.3"),sQuery(id+"F0.wireOp",EDGE,"E0.1.9.0"),sQuery(id+"F0.wireOp",EDGE,"E0.1.9.1"),sQuery(id+"F0.wireOp",EDGE,"E0.1.9.2"),sQuery(id+"F0.wireOp",EDGE,"E0.1.9.3"),sQuery(id+"F0.wireOp",EDGE,"E0.1.10.0"),sQuery(id+"F0.wireOp",EDGE,"E0.1.10.1"),sQuery(id+"F0.wireOp",EDGE,"E0.1.10.2"),sQuery(id+"F0.wireOp",EDGE,"E0.1.10.3"),sQuery(id+"F0.wireOp",EDGE,"E0.1.11.0"),sQuery(id+"F0.wireOp",EDGE,"E0.1.11.1"),sQuery(id+"F0.wireOp",EDGE,"E0.1.11.2"),sQuery(id+"F0.wireOp",EDGE,"E0.1.11.3"),sQuery(id+"F0.wireOp",EDGE,"E0.1.12.0"),sQuery(id+"F0.wireOp",EDGE,"E0.1.12.1"),sQuery(id+"F0.wireOp",EDGE,"E0.1.12.2"),sQuery(id+"F0.wireOp",EDGE,"E0.1.12.3"),sQuery(id+"F0.wireOp",EDGE,"E0.1.13.0"),sQuery(id+"F0.wireOp",EDGE,"E0.1.13.1"),sQuery(id+"F0.wireOp",EDGE,"E0.1.13.2"),sQuery(id+"F0.wireOp",EDGE,"E0.1.13.3"),sQuery(id+"F0.wireOp",EDGE,"E0.1.14.0"),sQuery(id+"F0.wireOp",EDGE,"E0.1.14.1"),sQuery(id+"F0.wireOp",EDGE,"E0.1.14.2"),sQuery(id+"F0.wireOp",EDGE,"E0.1.14.3"),sQuery(id+"F0.wireOp",EDGE,"E0.1.15.0"),sQuery(id+"F0.wireOp",EDGE,"E0.1.15.1"),sQuery(id+"F0.wireOp",EDGE,"E0.1.15.2"),sQuery(id+"F0.wireOp",EDGE,"E0.1.15.3"),sQuery(id+"F0.wireOp",EDGE,"E0.1.16.0"),sQuery(id+"F0.wireOp",EDGE,"E0.1.16.1"),sQuery(id+"F0.wireOp",EDGE,"E0.1.16.2"),sQuery(id+"F0.wireOp",EDGE,"E0.1.16.3"),sQuery(id+"F0.wireOp",EDGE,"E0.1.17.0"),sQuery(id+"F0.wireOp",EDGE,"E0.1.17.1"),sQuery(id+"F0.wireOp",EDGE,"E0.1.17.2"),sQuery(id+"F0.wireOp",EDGE,"E0.1.17.3"),sQuery(id+"F0.wireOp",EDGE,"E0.1.18.0"),sQuery(id+"F0.wireOp",EDGE,"E0.1.18.1"),sQuery(id+"F0.wireOp",EDGE,"E0.1.18.2"),sQuery(id+"F0.wireOp",EDGE,"E0.1.18.3"),sQuery(id+"F0.wireOp",EDGE,"E0.1.19.0"),sQuery(id+"F0.wireOp",EDGE,"E0.1.19.1"),sQuery(id+"F0.wireOp",EDGE,"E0.1.19.2"),sQuery(id+"F0.wireOp",EDGE,"E0.1.19.3"),sQuery(id+"F0.wireOp",EDGE,"E0.1.20.0"),sQuery(id+"F0.wireOp",EDGE,"E0.1.20.1"),sQuery(id+"F0.wireOp",EDGE,"E0.1.20.2"),sQuery(id+"F0.wireOp",EDGE,"E0.1.20.3"),sQuery(id+"F0.wireOp",EDGE,"E0.1.21.0"),sQuery(id+"F0.wireOp",EDGE,"E0.1.21.1"),sQuery(id+"F0.wireOp",EDGE,"E0.1.21.2"),sQuery(id+"F0.wireOp",EDGE,"E0.1.21.3"),sQuery(id+"F0.wireOp",EDGE,"E0.1.22.0"),sQuery(id+"F0.wireOp",EDGE,"E0.1.22.1"),sQuery(id+"F0.wireOp",EDGE,"E0.1.22.2"),sQuery(id+"F0.wireOp",EDGE,"E0.1.22.3"),sQuery(id+"F0.wireOp",EDGE,"E0.1.23.0"),sQuery(id+"F0.wireOp",EDGE,"E0.1.23.1"),sQuery(id+"F0.wireOp",EDGE,"E0.1.23.2"),sQuery(id+"F0.wireOp",EDGE,"E0.1.23.3"),sQuery(id+"F0.wireOp",EDGE,"E0.1.24.0"),sQuery(id+"F0.wireOp",EDGE,"E0.1.24.1"),sQuery(id+"F0.wireOp",EDGE,"E0.1.24.2"),sQuery(id+"F0.wireOp",EDGE,"E0.1.24.3"),sQuery(id+"F0.wireOp",EDGE,"E0.1.25.0"),sQuery(id+"F0.wireOp",EDGE,"E0.1.25.1"),sQuery(id+"F0.wireOp",EDGE,"E0.1.25.2"),sQuery(id+"F0.wireOp",EDGE,"E0.1.25.3"),sQuery(id+"F0.wireOp",EDGE,"E0.2.0.0"),sQuery(id+"F0.wireOp",EDGE,"E0.2.0.1"),sQuery(id+"F0.wireOp",EDGE,"E0.2.0.2"),sQuery(id+"F0.wireOp",EDGE,"E0.2.0.3"),sQuery(id+"F0.wireOp",EDGE,"E0.2.1.0"),sQuery(id+"F0.wireOp",EDGE,"E0.2.1.1"),sQuery(id+"F0.wireOp",EDGE,"E0.2.1.2"),sQuery(id+"F0.wireOp",EDGE,"E0.2.1.3"),sQuery(id+"F0.wireOp",EDGE,"E0.2.2.0"),sQuery(id+"F0.wireOp",EDGE,"E0.2.2.1"),sQuery(id+"F0.wireOp",EDGE,"E0.2.2.2"),sQuery(id+"F0.wireOp",EDGE,"E0.2.2.3"),sQuery(id+"F0.wireOp",EDGE,"E0.2.3.0"),sQuery(id+"F0.wireOp",EDGE,"E0.2.3.1"),sQuery(id+"F0.wireOp",EDGE,"E0.2.3.2"),sQuery(id+"F0.wireOp",EDGE,"E0.2.3.3"),sQuery(id+"F0.wireOp",EDGE,"E0.2.4.0"),sQuery(id+"F0.wireOp",EDGE,"E0.2.4.1"),sQuery(id+"F0.wireOp",EDGE,"E0.2.4.2"),sQuery(id+"F0.wireOp",EDGE,"E0.2.4.3"),sQuery(id+"F0.wireOp",EDGE,"E0.2.5.0"),sQuery(id+"F0.wireOp",EDGE,"E0.2.5.1"),sQuery(id+"F0.wireOp",EDGE,"E0.2.5.2"),sQuery(id+"F0.wireOp",EDGE,"E0.2.5.3"),sQuery(id+"F0.wireOp",EDGE,"E0.2.6.0"),sQuery(id+"F0.wireOp",EDGE,"E0.2.6.1"),sQuery(id+"F0.wireOp",EDGE,"E0.2.6.2"),sQuery(id+"F0.wireOp",EDGE,"E0.2.6.3"),sQuery(id+"F0.wireOp",EDGE,"E0.2.7.0"),sQuery(id+"F0.wireOp",EDGE,"E0.2.7.1"),sQuery(id+"F0.wireOp",EDGE,"E0.2.7.2"),sQuery(id+"F0.wireOp",EDGE,"E0.2.7.3"),sQuery(id+"F0.wireOp",EDGE,"E0.2.8.0"),sQuery(id+"F0.wireOp",EDGE,"E0.2.8.1"),sQuery(id+"F0.wireOp",EDGE,"E0.2.8.2"),sQuery(id+"F0.wireOp",EDGE,"E0.2.8.3"),sQuery(id+"F0.wireOp",EDGE,"E0.2.9.0"),sQuery(id+"F0.wireOp",EDGE,"E0.2.9.1"),sQuery(id+"F0.wireOp",EDGE,"E0.2.9.2"),sQuery(id+"F0.wireOp",EDGE,"E0.2.9.3"),sQuery(id+"F0.wireOp",EDGE,"E0.2.10.0"),sQuery(id+"F0.wireOp",EDGE,"E0.2.10.1"),sQuery(id+"F0.wireOp",EDGE,"E0.2.10.2"),sQuery(id+"F0.wireOp",EDGE,"E0.2.10.3"),sQuery(id+"F0.wireOp",EDGE,"E0.2.11.0"),sQuery(id+"F0.wireOp",EDGE,"E0.2.11.1"),sQuery(id+"F0.wireOp",EDGE,"E0.2.11.2"),sQuery(id+"F0.wireOp",EDGE,"E0.2.11.3"),sQuery(id+"F0.wireOp",EDGE,"E0.2.12.0"),sQuery(id+"F0.wireOp",EDGE,"E0.2.12.1"),sQuery(id+"F0.wireOp",EDGE,"E0.2.12.2"),sQuery(id+"F0.wireOp",EDGE,"E0.2.12.3"),sQuery(id+"F0.wireOp",EDGE,"E0.2.13.0"),sQuery(id+"F0.wireOp",EDGE,"E0.2.13.1"),sQuery(id+"F0.wireOp",EDGE,"E0.2.13.2"),sQuery(id+"F0.wireOp",EDGE,"E0.2.13.3"),sQuery(id+"F0.wireOp",EDGE,"E0.2.14.0"),sQuery(id+"F0.wireOp",EDGE,"E0.2.14.1"),sQuery(id+"F0.wireOp",EDGE,"E0.2.14.2"),sQuery(id+"F0.wireOp",EDGE,"E0.2.14.3"),sQuery(id+"F0.wireOp",EDGE,"E0.2.15.0"),sQuery(id+"F0.wireOp",EDGE,"E0.2.15.1"),sQuery(id+"F0.wireOp",EDGE,"E0.2.15.2"),sQuery(id+"F0.wireOp",EDGE,"E0.2.15.3"),sQuery(id+"F0.wireOp",EDGE,"E0.2.16.0"),sQuery(id+"F0.wireOp",EDGE,"E0.2.16.1"),sQuery(id+"F0.wireOp",EDGE,"E0.2.16.2"),sQuery(id+"F0.wireOp",EDGE,"E0.2.16.3"),sQuery(id+"F0.wireOp",EDGE,"E0.2.17.0"),sQuery(id+"F0.wireOp",EDGE,"E0.2.17.1"),sQuery(id+"F0.wireOp",EDGE,"E0.2.17.2"),sQuery(id+"F0.wireOp",EDGE,"E0.2.17.3"),sQuery(id+"F0.wireOp",EDGE,"E0.2.18.0"),sQuery(id+"F0.wireOp",EDGE,"E0.2.18.1"),sQuery(id+"F0.wireOp",EDGE,"E0.2.18.2"),sQuery(id+"F0.wireOp",EDGE,"E0.2.18.3"),sQuery(id+"F0.wireOp",EDGE,"E0.2.19.0"),sQuery(id+"F0.wireOp",EDGE,"E0.2.19.1"),sQuery(id+"F0.wireOp",EDGE,"E0.2.19.2"),sQuery(id+"F0.wireOp",EDGE,"E0.2.19.3"),sQuery(id+"F0.wireOp",EDGE,"E0.2.20.0"),sQuery(id+"F0.wireOp",EDGE,"E0.2.20.1"),sQuery(id+"F0.wireOp",EDGE,"E0.2.20.2"),sQuery(id+"F0.wireOp",EDGE,"E0.2.20.3"),sQuery(id+"F0.wireOp",EDGE,"E0.2.21.0"),sQuery(id+"F0.wireOp",EDGE,"E0.2.21.1"),sQuery(id+"F0.wireOp",EDGE,"E0.2.21.2"),sQuery(id+"F0.wireOp",EDGE,"E0.2.21.3"),sQuery(id+"F0.wireOp",EDGE,"E0.2.22.0"),sQuery(id+"F0.wireOp",EDGE,"E0.2.22.1"),sQuery(id+"F0.wireOp",EDGE,"E0.2.22.2"),sQuery(id+"F0.wireOp",EDGE,"E0.2.22.3"),sQuery(id+"F0.wireOp",EDGE,"E0.2.23.0"),sQuery(id+"F0.wireOp",EDGE,"E0.2.23.1"),sQuery(id+"F0.wireOp",EDGE,"E0.2.23.2"),sQuery(id+"F0.wireOp",EDGE,"E0.2.23.3"),sQuery(id+"F0.wireOp",EDGE,"E0.2.24.0"),sQuery(id+"F0.wireOp",EDGE,"E0.2.24.1"),sQuery(id+"F0.wireOp",EDGE,"E0.2.24.2"),sQuery(id+"F0.wireOp",EDGE,"E0.2.24.3"),sQuery(id+"F0.wireOp",EDGE,"E0.2.25.0"),sQuery(id+"F0.wireOp",EDGE,"E0.2.25.1"),sQuery(id+"F0.wireOp",EDGE,"E0.2.25.2"),sQuery(id+"F0.wireOp",EDGE,"E0.2.25.3"),sQuery(id+"F0.wireOp",EDGE,"AU2oHFlj-txaj-hLN4-KDEQ-E2aTrxoRIFTm"),sQuery(id+"F0.wireOp",EDGE,"T7GrudpP-bjZC-sghp-RzMj-ol2ZXyDjpRGs"),sQuery(id+"F0.wireOp",EDGE,"E1"),sQuery(id+"F0.wireOp",EDGE,"90fbf2e0-ce94-4077-ba36-f7078a65e9f6.1.0.0"),sQuery(id+"F0.wireOp",EDGE,"90fbf2e0-ce94-4077-ba36-f7078a65e9f6.1.0.1"),sQuery(id+"F0.wireOp",EDGE,"90fbf2e0-ce94-4077-ba36-f7078a65e9f6.1.0.2"),sQuery(id+"F0.wireOp",EDGE,"90fbf2e0-ce94-4077-ba36-f7078a65e9f6.1.0.3"),sQuery(id+"F0.wireOp",EDGE,"90fbf2e0-ce94-4077-ba36-f7078a65e9f6.1.0.4"),sQuery(id+"F0.wireOp",EDGE,"90fbf2e0-ce94-4077-ba36-f7078a65e9f6.1.0.5"),sQuery(id+"F0.wireOp",EDGE,"90fbf2e0-ce94-4077-ba36-f7078a65e9f6.1.0.6"),sQuery(id+"F0.wireOp",EDGE,"90fbf2e0-ce94-4077-ba36-f7078a65e9f6.1.0.7"),sQuery(id+"F0.wireOp",EDGE,"90fbf2e0-ce94-4077-ba36-f7078a65e9f6.1.0.8"),sQuery(id+"F0.wireOp",EDGE,"90fbf2e0-ce94-4077-ba36-f7078a65e9f6.1.0.9"),sQuery(id+"F0.wireOp",EDGE,"90fbf2e0-ce94-4077-ba36-f7078a65e9f6.1.0.10"),sQuery(id+"F0.wireOp",EDGE,"90fbf2e0-ce94-4077-ba36-f7078a65e9f6.1.0.11"),sQuery(id+"F0.wireOp",EDGE,"90fbf2e0-ce94-4077-ba36-f7078a65e9f6.2.0.0"),sQuery(id+"F0.wireOp",EDGE,"90fbf2e0-ce94-4077-ba36-f7078a65e9f6.2.0.1"),sQuery(id+"F0.wireOp",EDGE,"90fbf2e0-ce94-4077-ba36-f7078a65e9f6.2.0.2"),sQuery(id+"F0.wireOp",EDGE,"90fbf2e0-ce94-4077-ba36-f7078a65e9f6.2.0.3"),sQuery(id+"F0.wireOp",EDGE,"90fbf2e0-ce94-4077-ba36-f7078a65e9f6.2.0.4"),sQuery(id+"F0.wireOp",EDGE,"90fbf2e0-ce94-4077-ba36-f7078a65e9f6.2.0.5"),sQuery(id+"F0.wireOp",EDGE,"90fbf2e0-ce94-4077-ba36-f7078a65e9f6.2.0.6"),sQuery(id+"F0.wireOp",EDGE,"90fbf2e0-ce94-4077-ba36-f7078a65e9f6.2.0.7"),sQuery(id+"F0.wireOp",EDGE,"90fbf2e0-ce94-4077-ba36-f7078a65e9f6.2.0.8"),sQuery(id+"F0.wireOp",EDGE,"90fbf2e0-ce94-4077-ba36-f7078a65e9f6.2.0.9"),sQuery(id+"F0.wireOp",EDGE,"90fbf2e0-ce94-4077-ba36-f7078a65e9f6.2.0.10"),sQuery(id+"F0.wireOp",EDGE,"90fbf2e0-ce94-4077-ba36-f7078a65e9f6.2.0.11"),sQuery(id+"F0.wireOp",EDGE,"90fbf2e0-ce94-4077-ba36-f7078a65e9f6.3.0.0"),sQuery(id+"F0.wireOp",EDGE,"90fbf2e0-ce94-4077-ba36-f7078a65e9f6.3.0.1"),sQuery(id+"F0.wireOp",EDGE,"90fbf2e0-ce94-4077-ba36-f7078a65e9f6.3.0.2"),sQuery(id+"F0.wireOp",EDGE,"90fbf2e0-ce94-4077-ba36-f7078a65e9f6.3.0.3"),sQuery(id+"F0.wireOp",EDGE,"90fbf2e0-ce94-4077-ba36-f7078a65e9f6.3.0.4"),sQuery(id+"F0.wireOp",EDGE,"90fbf2e0-ce94-4077-ba36-f7078a65e9f6.3.0.5"),sQuery(id+"F0.wireOp",EDGE,"90fbf2e0-ce94-4077-ba36-f7078a65e9f6.3.0.6"),sQuery(id+"F0.wireOp",EDGE,"90fbf2e0-ce94-4077-ba36-f7078a65e9f6.3.0.7"),sQuery(id+"F0.wireOp",EDGE,"90fbf2e0-ce94-4077-ba36-f7078a65e9f6.3.0.8"),sQuery(id+"F0.wireOp",EDGE,"90fbf2e0-ce94-4077-ba36-f7078a65e9f6.3.0.9"),sQuery(id+"F0.wireOp",EDGE,"90fbf2e0-ce94-4077-ba36-f7078a65e9f6.3.0.10"),sQuery(id+"F0.wireOp",EDGE,"90fbf2e0-ce94-4077-ba36-f7078a65e9f6.3.0.11"),sQuery(id+"F0.wireOp",EDGE,"90fbf2e0-ce94-4077-ba36-f7078a65e9f6.4.0.0"),sQuery(id+"F0.wireOp",EDGE,"90fbf2e0-ce94-4077-ba36-f7078a65e9f6.4.0.1"),sQuery(id+"F0.wireOp",EDGE,"90fbf2e0-ce94-4077-ba36-f7078a65e9f6.4.0.2"),sQuery(id+"F0.wireOp",EDGE,"90fbf2e0-ce94-4077-ba36-f7078a65e9f6.4.0.3"),sQuery(id+"F0.wireOp",EDGE,"90fbf2e0-ce94-4077-ba36-f7078a65e9f6.4.0.4"),sQuery(id+"F0.wireOp",EDGE,"90fbf2e0-ce94-4077-ba36-f7078a65e9f6.4.0.5"),sQuery(id+"F0.wireOp",EDGE,"90fbf2e0-ce94-4077-ba36-f7078a65e9f6.4.0.6"),sQuery(id+"F0.wireOp",EDGE,"90fbf2e0-ce94-4077-ba36-f7078a65e9f6.4.0.7"),sQuery(id+"F0.wireOp",EDGE,"90fbf2e0-ce94-4077-ba36-f7078a65e9f6.4.0.8"),sQuery(id+"F0.wireOp",EDGE,"90fbf2e0-ce94-4077-ba36-f7078a65e9f6.4.0.9"),sQuery(id+"F0.wireOp",EDGE,"90fbf2e0-ce94-4077-ba36-f7078a65e9f6.4.0.10"),sQuery(id+"F0.wireOp",EDGE,"90fbf2e0-ce94-4077-ba36-f7078a65e9f6.4.0.11"),sQuery(id+"F0.wireOp",EDGE,"90fbf2e0-ce94-4077-ba36-f7078a65e9f6.5.0.0"),sQuery(id+"F0.wireOp",EDGE,"90fbf2e0-ce94-4077-ba36-f7078a65e9f6.5.0.1"),sQuery(id+"F0.wireOp",EDGE,"90fbf2e0-ce94-4077-ba36-f7078a65e9f6.5.0.2"),sQuery(id+"F0.wireOp",EDGE,"90fbf2e0-ce94-4077-ba36-f7078a65e9f6.5.0.3"),sQuery(id+"F0.wireOp",EDGE,"90fbf2e0-ce94-4077-ba36-f7078a65e9f6.5.0.4"),sQuery(id+"F0.wireOp",EDGE,"90fbf2e0-ce94-4077-ba36-f7078a65e9f6.5.0.5"),sQuery(id+"F0.wireOp",EDGE,"90fbf2e0-ce94-4077-ba36-f7078a65e9f6.5.0.6"),sQuery(id+"F0.wireOp",EDGE,"90fbf2e0-ce94-4077-ba36-f7078a65e9f6.5.0.7"),sQuery(id+"F0.wireOp",EDGE,"90fbf2e0-ce94-4077-ba36-f7078a65e9f6.5.0.8"),sQuery(id+"F0.wireOp",EDGE,"90fbf2e0-ce94-4077-ba36-f7078a65e9f6.5.0.9"),sQuery(id+"F0.wireOp",EDGE,"90fbf2e0-ce94-4077-ba36-f7078a65e9f6.5.0.10"),sQuery(id+"F0.wireOp",EDGE,"90fbf2e0-ce94-4077-ba36-f7078a65e9f6.5.0.11"),sQuery(id+"F0.wireOp",EDGE,"90fbf2e0-ce94-4077-ba36-f7078a65e9f6.6.0.0"),sQuery(id+"F0.wireOp",EDGE,"90fbf2e0-ce94-4077-ba36-f7078a65e9f6.6.0.1"),sQuery(id+"F0.wireOp",EDGE,"90fbf2e0-ce94-4077-ba36-f7078a65e9f6.6.0.2"),sQuery(id+"F0.wireOp",EDGE,"90fbf2e0-ce94-4077-ba36-f7078a65e9f6.6.0.3"),sQuery(id+"F0.wireOp",EDGE,"90fbf2e0-ce94-4077-ba36-f7078a65e9f6.6.0.4"),sQuery(id+"F0.wireOp",EDGE,"90fbf2e0-ce94-4077-ba36-f7078a65e9f6.6.0.5"),sQuery(id+"F0.wireOp",EDGE,"90fbf2e0-ce94-4077-ba36-f7078a65e9f6.6.0.6"),sQuery(id+"F0.wireOp",EDGE,"90fbf2e0-ce94-4077-ba36-f7078a65e9f6.6.0.7"),sQuery(id+"F0.wireOp",EDGE,"90fbf2e0-ce94-4077-ba36-f7078a65e9f6.6.0.8"),sQuery(id+"F0.wireOp",EDGE,"90fbf2e0-ce94-4077-ba36-f7078a65e9f6.6.0.9"),sQuery(id+"F0.wireOp",EDGE,"90fbf2e0-ce94-4077-ba36-f7078a65e9f6.6.0.10"),sQuery(id+"F0.wireOp",EDGE,"90fbf2e0-ce94-4077-ba36-f7078a65e9f6.6.0.11"),sQuery(id+"F0.wireOp",EDGE,"90fbf2e0-ce94-4077-ba36-f7078a65e9f6.7.0.0"),sQuery(id+"F0.wireOp",EDGE,"90fbf2e0-ce94-4077-ba36-f7078a65e9f6.7.0.1"),sQuery(id+"F0.wireOp",EDGE,"90fbf2e0-ce94-4077-ba36-f7078a65e9f6.7.0.2"),sQuery(id+"F0.wireOp",EDGE,"90fbf2e0-ce94-4077-ba36-f7078a65e9f6.7.0.3"),sQuery(id+"F0.wireOp",EDGE,"90fbf2e0-ce94-4077-ba36-f7078a65e9f6.7.0.4"),sQuery(id+"F0.wireOp",EDGE,"90fbf2e0-ce94-4077-ba36-f7078a65e9f6.7.0.5"),sQuery(id+"F0.wireOp",EDGE,"90fbf2e0-ce94-4077-ba36-f7078a65e9f6.7.0.6"),sQuery(id+"F0.wireOp",EDGE,"90fbf2e0-ce94-4077-ba36-f7078a65e9f6.7.0.7"),sQuery(id+"F0.wireOp",EDGE,"90fbf2e0-ce94-4077-ba36-f7078a65e9f6.7.0.8"),sQuery(id+"F0.wireOp",EDGE,"90fbf2e0-ce94-4077-ba36-f7078a65e9f6.7.0.9"),sQuery(id+"F0.wireOp",EDGE,"90fbf2e0-ce94-4077-ba36-f7078a65e9f6.7.0.10"),sQuery(id+"F0.wireOp",EDGE,"90fbf2e0-ce94-4077-ba36-f7078a65e9f6.7.0.11"),sQuery(id+"F0.wireOp",EDGE,"90fbf2e0-ce94-4077-ba36-f7078a65e9f6.8.0.0"),sQuery(id+"F0.wireOp",EDGE,"90fbf2e0-ce94-4077-ba36-f7078a65e9f6.8.0.1"),sQuery(id+"F0.wireOp",EDGE,"90fbf2e0-ce94-4077-ba36-f7078a65e9f6.8.0.2"),sQuery(id+"F0.wireOp",EDGE,"90fbf2e0-ce94-4077-ba36-f7078a65e9f6.8.0.3"),sQuery(id+"F0.wireOp",EDGE,"90fbf2e0-ce94-4077-ba36-f7078a65e9f6.8.0.4"),sQuery(id+"F0.wireOp",EDGE,"90fbf2e0-ce94-4077-ba36-f7078a65e9f6.8.0.5"),sQuery(id+"F0.wireOp",EDGE,"90fbf2e0-ce94-4077-ba36-f7078a65e9f6.8.0.6"),sQuery(id+"F0.wireOp",EDGE,"90fbf2e0-ce94-4077-ba36-f7078a65e9f6.8.0.7"),sQuery(id+"F0.wireOp",EDGE,"90fbf2e0-ce94-4077-ba36-f7078a65e9f6.8.0.8"),sQuery(id+"F0.wireOp",EDGE,"90fbf2e0-ce94-4077-ba36-f7078a65e9f6.8.0.9"),sQuery(id+"F0.wireOp",EDGE,"90fbf2e0-ce94-4077-ba36-f7078a65e9f6.8.0.10"),sQuery(id+"F0.wireOp",EDGE,"90fbf2e0-ce94-4077-ba36-f7078a65e9f6.8.0.11"),sQuery(id+"F0.wireOp",EDGE,"90fbf2e0-ce94-4077-ba36-f7078a65e9f6.9.0.0"),sQuery(id+"F0.wireOp",EDGE,"90fbf2e0-ce94-4077-ba36-f7078a65e9f6.9.0.1"),sQuery(id+"F0.wireOp",EDGE,"90fbf2e0-ce94-4077-ba36-f7078a65e9f6.9.0.2"),sQuery(id+"F0.wireOp",EDGE,"90fbf2e0-ce94-4077-ba36-f7078a65e9f6.9.0.3"),sQuery(id+"F0.wireOp",EDGE,"90fbf2e0-ce94-4077-ba36-f7078a65e9f6.9.0.4"),sQuery(id+"F0.wireOp",EDGE,"90fbf2e0-ce94-4077-ba36-f7078a65e9f6.9.0.5"),sQuery(id+"F0.wireOp",EDGE,"90fbf2e0-ce94-4077-ba36-f7078a65e9f6.9.0.6"),sQuery(id+"F0.wireOp",EDGE,"90fbf2e0-ce94-4077-ba36-f7078a65e9f6.9.0.7"),sQuery(id+"F0.wireOp",EDGE,"90fbf2e0-ce94-4077-ba36-f7078a65e9f6.9.0.8"),sQuery(id+"F0.wireOp",EDGE,"90fbf2e0-ce94-4077-ba36-f7078a65e9f6.9.0.9"),sQuery(id+"F0.wireOp",EDGE,"90fbf2e0-ce94-4077-ba36-f7078a65e9f6.9.0.10"),sQuery(id+"F0.wireOp",EDGE,"90fbf2e0-ce94-4077-ba36-f7078a65e9f6.9.0.11"),sQuery(id+"F0.wireOp",EDGE,"90fbf2e0-ce94-4077-ba36-f7078a65e9f6.10.0.0"),sQuery(id+"F0.wireOp",EDGE,"90fbf2e0-ce94-4077-ba36-f7078a65e9f6.10.0.1"),sQuery(id+"F0.wireOp",EDGE,"90fbf2e0-ce94-4077-ba36-f7078a65e9f6.10.0.2"),sQuery(id+"F0.wireOp",EDGE,"90fbf2e0-ce94-4077-ba36-f7078a65e9f6.10.0.3"),sQuery(id+"F0.wireOp",EDGE,"90fbf2e0-ce94-4077-ba36-f7078a65e9f6.10.0.4"),sQuery(id+"F0.wireOp",EDGE,"90fbf2e0-ce94-4077-ba36-f7078a65e9f6.10.0.5"),sQuery(id+"F0.wireOp",EDGE,"90fbf2e0-ce94-4077-ba36-f7078a65e9f6.10.0.6"),sQuery(id+"F0.wireOp",EDGE,"90fbf2e0-ce94-4077-ba36-f7078a65e9f6.10.0.7"),sQuery(id+"F0.wireOp",EDGE,"90fbf2e0-ce94-4077-ba36-f7078a65e9f6.10.0.8"),sQuery(id+"F0.wireOp",EDGE,"90fbf2e0-ce94-4077-ba36-f7078a65e9f6.10.0.9"),sQuery(id+"F0.wireOp",EDGE,"90fbf2e0-ce94-4077-ba36-f7078a65e9f6.10.0.10"),sQuery(id+"F0.wireOp",EDGE,"90fbf2e0-ce94-4077-ba36-f7078a65e9f6.10.0.11"),sQuery(id+"F0.wireOp",EDGE,"ef05f06f-9539-49a4-bbe1-e5de78f87bac.1.0.0"),sQuery(id+"F0.wireOp",EDGE,"ef05f06f-9539-49a4-bbe1-e5de78f87bac.1.0.1"),sQuery(id+"F0.wireOp",EDGE,"ef05f06f-9539-49a4-bbe1-e5de78f87bac.1.0.2"),sQuery(id+"F0.wireOp",EDGE,"ef05f06f-9539-49a4-bbe1-e5de78f87bac.1.0.3"),sQuery(id+"F0.wireOp",EDGE,"ef05f06f-9539-49a4-bbe1-e5de78f87bac.1.0.4"),sQuery(id+"F0.wireOp",EDGE,"ef05f06f-9539-49a4-bbe1-e5de78f87bac.1.0.5"),sQuery(id+"F0.wireOp",EDGE,"ef05f06f-9539-49a4-bbe1-e5de78f87bac.1.0.6"),sQuery(id+"F0.wireOp",EDGE,"ef05f06f-9539-49a4-bbe1-e5de78f87bac.1.0.7"),sQuery(id+"F0.wireOp",EDGE,"ef05f06f-9539-49a4-bbe1-e5de78f87bac.1.0.8"),sQuery(id+"F0.wireOp",EDGE,"ef05f06f-9539-49a4-bbe1-e5de78f87bac.1.0.9"),sQuery(id+"F0.wireOp",EDGE,"ef05f06f-9539-49a4-bbe1-e5de78f87bac.1.0.10"),sQuery(id+"F0.wireOp",EDGE,"ef05f06f-9539-49a4-bbe1-e5de78f87bac.1.0.11"),sQuery(id+"F0.wireOp",EDGE,"ef05f06f-9539-49a4-bbe1-e5de78f87bac.2.0.0"),sQuery(id+"F0.wireOp",EDGE,"ef05f06f-9539-49a4-bbe1-e5de78f87bac.2.0.1"),sQuery(id+"F0.wireOp",EDGE,"ef05f06f-9539-49a4-bbe1-e5de78f87bac.2.0.2"),sQuery(id+"F0.wireOp",EDGE,"ef05f06f-9539-49a4-bbe1-e5de78f87bac.2.0.3"),sQuery(id+"F0.wireOp",EDGE,"ef05f06f-9539-49a4-bbe1-e5de78f87bac.2.0.4"),sQuery(id+"F0.wireOp",EDGE,"ef05f06f-9539-49a4-bbe1-e5de78f87bac.2.0.5"),sQuery(id+"F0.wireOp",EDGE,"ef05f06f-9539-49a4-bbe1-e5de78f87bac.2.0.6"),sQuery(id+"F0.wireOp",EDGE,"ef05f06f-9539-49a4-bbe1-e5de78f87bac.2.0.7"),sQuery(id+"F0.wireOp",EDGE,"ef05f06f-9539-49a4-bbe1-e5de78f87bac.2.0.8"),sQuery(id+"F0.wireOp",EDGE,"ef05f06f-9539-49a4-bbe1-e5de78f87bac.2.0.9"),sQuery(id+"F0.wireOp",EDGE,"ef05f06f-9539-49a4-bbe1-e5de78f87bac.2.0.10"),sQuery(id+"F0.wireOp",EDGE,"ef05f06f-9539-49a4-bbe1-e5de78f87bac.2.0.11"),sQuery(id+"F0.wireOp",EDGE,"ef05f06f-9539-49a4-bbe1-e5de78f87bac.3.0.0"),sQuery(id+"F0.wireOp",EDGE,"ef05f06f-9539-49a4-bbe1-e5de78f87bac.3.0.1"),sQuery(id+"F0.wireOp",EDGE,"ef05f06f-9539-49a4-bbe1-e5de78f87bac.3.0.2"),sQuery(id+"F0.wireOp",EDGE,"ef05f06f-9539-49a4-bbe1-e5de78f87bac.3.0.3"),sQuery(id+"F0.wireOp",EDGE,"ef05f06f-9539-49a4-bbe1-e5de78f87bac.3.0.4"),sQuery(id+"F0.wireOp",EDGE,"ef05f06f-9539-49a4-bbe1-e5de78f87bac.3.0.5"),sQuery(id+"F0.wireOp",EDGE,"ef05f06f-9539-49a4-bbe1-e5de78f87bac.3.0.6"),sQuery(id+"F0.wireOp",EDGE,"ef05f06f-9539-49a4-bbe1-e5de78f87bac.3.0.7"),sQuery(id+"F0.wireOp",EDGE,"ef05f06f-9539-49a4-bbe1-e5de78f87bac.3.0.8"),sQuery(id+"F0.wireOp",EDGE,"ef05f06f-9539-49a4-bbe1-e5de78f87bac.3.0.9"),sQuery(id+"F0.wireOp",EDGE,"ef05f06f-9539-49a4-bbe1-e5de78f87bac.3.0.10"),sQuery(id+"F0.wireOp",EDGE,"ef05f06f-9539-49a4-bbe1-e5de78f87bac.3.0.11"),sQuery(id+"F0.wireOp",EDGE,"ef05f06f-9539-49a4-bbe1-e5de78f87bac.4.0.0"),sQuery(id+"F0.wireOp",EDGE,"ef05f06f-9539-49a4-bbe1-e5de78f87bac.4.0.1"),sQuery(id+"F0.wireOp",EDGE,"ef05f06f-9539-49a4-bbe1-e5de78f87bac.4.0.2"),sQuery(id+"F0.wireOp",EDGE,"ef05f06f-9539-49a4-bbe1-e5de78f87bac.4.0.3"),sQuery(id+"F0.wireOp",EDGE,"ef05f06f-9539-49a4-bbe1-e5de78f87bac.4.0.4"),sQuery(id+"F0.wireOp",EDGE,"ef05f06f-9539-49a4-bbe1-e5de78f87bac.4.0.5"),sQuery(id+"F0.wireOp",EDGE,"ef05f06f-9539-49a4-bbe1-e5de78f87bac.4.0.6"),sQuery(id+"F0.wireOp",EDGE,"ef05f06f-9539-49a4-bbe1-e5de78f87bac.4.0.7"),sQuery(id+"F0.wireOp",EDGE,"ef05f06f-9539-49a4-bbe1-e5de78f87bac.4.0.8"),sQuery(id+"F0.wireOp",EDGE,"ef05f06f-9539-49a4-bbe1-e5de78f87bac.4.0.9"),sQuery(id+"F0.wireOp",EDGE,"ef05f06f-9539-49a4-bbe1-e5de78f87bac.4.0.10"),sQuery(id+"F0.wireOp",EDGE,"ef05f06f-9539-49a4-bbe1-e5de78f87bac.4.0.11"),sQuery(id+"F0.wireOp",EDGE,"ef05f06f-9539-49a4-bbe1-e5de78f87bac.5.0.0"),sQuery(id+"F0.wireOp",EDGE,"ef05f06f-9539-49a4-bbe1-e5de78f87bac.5.0.1"),sQuery(id+"F0.wireOp",EDGE,"ef05f06f-9539-49a4-bbe1-e5de78f87bac.5.0.2"),sQuery(id+"F0.wireOp",EDGE,"ef05f06f-9539-49a4-bbe1-e5de78f87bac.5.0.3"),sQuery(id+"F0.wireOp",EDGE,"ef05f06f-9539-49a4-bbe1-e5de78f87bac.5.0.4"),sQuery(id+"F0.wireOp",EDGE,"ef05f06f-9539-49a4-bbe1-e5de78f87bac.5.0.5"),sQuery(id+"F0.wireOp",EDGE,"ef05f06f-9539-49a4-bbe1-e5de78f87bac.5.0.6"),sQuery(id+"F0.wireOp",EDGE,"ef05f06f-9539-49a4-bbe1-e5de78f87bac.5.0.7"),sQuery(id+"F0.wireOp",EDGE,"ef05f06f-9539-49a4-bbe1-e5de78f87bac.5.0.8"),sQuery(id+"F0.wireOp",EDGE,"ef05f06f-9539-49a4-bbe1-e5de78f87bac.5.0.9"),sQuery(id+"F0.wireOp",EDGE,"ef05f06f-9539-49a4-bbe1-e5de78f87bac.5.0.10"),sQuery(id+"F0.wireOp",EDGE,"ef05f06f-9539-49a4-bbe1-e5de78f87bac.5.0.11"),sQuery(id+"F0.wireOp",EDGE,"ef05f06f-9539-49a4-bbe1-e5de78f87bac.6.0.0"),sQuery(id+"F0.wireOp",EDGE,"ef05f06f-9539-49a4-bbe1-e5de78f87bac.6.0.1"),sQuery(id+"F0.wireOp",EDGE,"ef05f06f-9539-49a4-bbe1-e5de78f87bac.6.0.2"),sQuery(id+"F0.wireOp",EDGE,"ef05f06f-9539-49a4-bbe1-e5de78f87bac.6.0.3"),sQuery(id+"F0.wireOp",EDGE,"ef05f06f-9539-49a4-bbe1-e5de78f87bac.6.0.4"),sQuery(id+"F0.wireOp",EDGE,"ef05f06f-9539-49a4-bbe1-e5de78f87bac.6.0.5"),sQuery(id+"F0.wireOp",EDGE,"ef05f06f-9539-49a4-bbe1-e5de78f87bac.6.0.6"),sQuery(id+"F0.wireOp",EDGE,"ef05f06f-9539-49a4-bbe1-e5de78f87bac.6.0.7"),sQuery(id+"F0.wireOp",EDGE,"ef05f06f-9539-49a4-bbe1-e5de78f87bac.6.0.8"),sQuery(id+"F0.wireOp",EDGE,"ef05f06f-9539-49a4-bbe1-e5de78f87bac.6.0.9"),sQuery(id+"F0.wireOp",EDGE,"ef05f06f-9539-49a4-bbe1-e5de78f87bac.6.0.10"),sQuery(id+"F0.wireOp",EDGE,"ef05f06f-9539-49a4-bbe1-e5de78f87bac.6.0.11"),sQuery(id+"F0.wireOp",EDGE,"ef05f06f-9539-49a4-bbe1-e5de78f87bac.7.0.0"),sQuery(id+"F0.wireOp",EDGE,"ef05f06f-9539-49a4-bbe1-e5de78f87bac.7.0.1"),sQuery(id+"F0.wireOp",EDGE,"ef05f06f-9539-49a4-bbe1-e5de78f87bac.7.0.2"),sQuery(id+"F0.wireOp",EDGE,"ef05f06f-9539-49a4-bbe1-e5de78f87bac.7.0.3"),sQuery(id+"F0.wireOp",EDGE,"ef05f06f-9539-49a4-bbe1-e5de78f87bac.7.0.4"),sQuery(id+"F0.wireOp",EDGE,"ef05f06f-9539-49a4-bbe1-e5de78f87bac.7.0.5"),sQuery(id+"F0.wireOp",EDGE,"ef05f06f-9539-49a4-bbe1-e5de78f87bac.7.0.6"),sQuery(id+"F0.wireOp",EDGE,"ef05f06f-9539-49a4-bbe1-e5de78f87bac.7.0.7"),sQuery(id+"F0.wireOp",EDGE,"ef05f06f-9539-49a4-bbe1-e5de78f87bac.7.0.8"),sQuery(id+"F0.wireOp",EDGE,"ef05f06f-9539-49a4-bbe1-e5de78f87bac.7.0.9"),sQuery(id+"F0.wireOp",EDGE,"ef05f06f-9539-49a4-bbe1-e5de78f87bac.7.0.10"),sQuery(id+"F0.wireOp",EDGE,"ef05f06f-9539-49a4-bbe1-e5de78f87bac.7.0.11"),sQuery(id+"F0.wireOp",EDGE,"ef05f06f-9539-49a4-bbe1-e5de78f87bac.8.0.0"),sQuery(id+"F0.wireOp",EDGE,"ef05f06f-9539-49a4-bbe1-e5de78f87bac.8.0.1"),sQuery(id+"F0.wireOp",EDGE,"ef05f06f-9539-49a4-bbe1-e5de78f87bac.8.0.2"),sQuery(id+"F0.wireOp",EDGE,"ef05f06f-9539-49a4-bbe1-e5de78f87bac.8.0.3"),sQuery(id+"F0.wireOp",EDGE,"ef05f06f-9539-49a4-bbe1-e5de78f87bac.8.0.4"),sQuery(id+"F0.wireOp",EDGE,"ef05f06f-9539-49a4-bbe1-e5de78f87bac.8.0.5"),sQuery(id+"F0.wireOp",EDGE,"ef05f06f-9539-49a4-bbe1-e5de78f87bac.8.0.6"),sQuery(id+"F0.wireOp",EDGE,"ef05f06f-9539-49a4-bbe1-e5de78f87bac.8.0.7"),sQuery(id+"F0.wireOp",EDGE,"ef05f06f-9539-49a4-bbe1-e5de78f87bac.8.0.8"),sQuery(id+"F0.wireOp",EDGE,"ef05f06f-9539-49a4-bbe1-e5de78f87bac.8.0.9"),sQuery(id+"F0.wireOp",EDGE,"ef05f06f-9539-49a4-bbe1-e5de78f87bac.8.0.10"),sQuery(id+"F0.wireOp",EDGE,"ef05f06f-9539-49a4-bbe1-e5de78f87bac.8.0.11"),sQuery(id+"F0.wireOp",EDGE,"ef05f06f-9539-49a4-bbe1-e5de78f87bac.9.0.0"),sQuery(id+"F0.wireOp",EDGE,"ef05f06f-9539-49a4-bbe1-e5de78f87bac.9.0.1"),sQuery(id+"F0.wireOp",EDGE,"ef05f06f-9539-49a4-bbe1-e5de78f87bac.9.0.2"),sQuery(id+"F0.wireOp",EDGE,"ef05f06f-9539-49a4-bbe1-e5de78f87bac.9.0.3"),sQuery(id+"F0.wireOp",EDGE,"ef05f06f-9539-49a4-bbe1-e5de78f87bac.9.0.4"),sQuery(id+"F0.wireOp",EDGE,"ef05f06f-9539-49a4-bbe1-e5de78f87bac.9.0.5"),sQuery(id+"F0.wireOp",EDGE,"ef05f06f-9539-49a4-bbe1-e5de78f87bac.9.0.6"),sQuery(id+"F0.wireOp",EDGE,"ef05f06f-9539-49a4-bbe1-e5de78f87bac.9.0.7"),sQuery(id+"F0.wireOp",EDGE,"ef05f06f-9539-49a4-bbe1-e5de78f87bac.9.0.8"),sQuery(id+"F0.wireOp",EDGE,"ef05f06f-9539-49a4-bbe1-e5de78f87bac.9.0.9"),sQuery(id+"F0.wireOp",EDGE,"ef05f06f-9539-49a4-bbe1-e5de78f87bac.9.0.10"),sQuery(id+"F0.wireOp",EDGE,"ef05f06f-9539-49a4-bbe1-e5de78f87bac.9.0.11"),sQuery(id+"F0.wireOp",EDGE,"ef05f06f-9539-49a4-bbe1-e5de78f87bac.10.0.0"),sQuery(id+"F0.wireOp",EDGE,"ef05f06f-9539-49a4-bbe1-e5de78f87bac.10.0.1"),sQuery(id+"F0.wireOp",EDGE,"ef05f06f-9539-49a4-bbe1-e5de78f87bac.10.0.2"),sQuery(id+"F0.wireOp",EDGE,"ef05f06f-9539-49a4-bbe1-e5de78f87bac.10.0.3"),sQuery(id+"F0.wireOp",EDGE,"ef05f06f-9539-49a4-bbe1-e5de78f87bac.10.0.4"),sQuery(id+"F0.wireOp",EDGE,"ef05f06f-9539-49a4-bbe1-e5de78f87bac.10.0.5"),sQuery(id+"F0.wireOp",EDGE,"ef05f06f-9539-49a4-bbe1-e5de78f87bac.10.0.6"),sQuery(id+"F0.wireOp",EDGE,"ef05f06f-9539-49a4-bbe1-e5de78f87bac.10.0.7"),sQuery(id+"F0.wireOp",EDGE,"ef05f06f-9539-49a4-bbe1-e5de78f87bac.10.0.8"),sQuery(id+"F0.wireOp",EDGE,"ef05f06f-9539-49a4-bbe1-e5de78f87bac.10.0.9"),sQuery(id+"F0.wireOp",EDGE,"ef05f06f-9539-49a4-bbe1-e5de78f87bac.10.0.10"),sQuery(id+"F0.wireOp",EDGE,"ef05f06f-9539-49a4-bbe1-e5de78f87bac.10.0.11"),sQuery(id+"F0.wireOp",EDGE,"OJy4rNNo-w8Xi-PtYp-78KY-KX9WQq1O9zWX"),sQuery(id+"F0.wireOp",EDGE,"6ad1825e-1499-4b2d-8658-c8d5a4458ecc.filletArc"),sQuery(id+"F0.wireOp",EDGE,"0e28861b-0804-44a8-a45e-df2b0c80d6fb.filletArc"),sQuery(id+"F0.wireOp",EDGE,"69729d80-6c64-417c-b4d8-b2ce01de760d.filletArc"),sQuery(id+"F0.wireOp",EDGE,"57ece835-d495-4d14-92ee-c9d50648b8c1.filletArc")])],"isStart":false});
            var sketch = newSketch(context, id + "F19", { "sketchPlane" : qUnion([Q0])});
            skLineSegment(sketch, "E66", {"start": v(-99.25, 21.85) * mm, "end": v(-103.88, 21.85) * mm});
            skLineSegment(sketch, "E67", {"start": v(-103.88, 21.85) * mm, "end": v(-103.88, 17.23) * mm});
            skLineSegment(sketch, "E68", {"start": v(-103.88, 17.23) * mm, "end": v(-99.25, 17.23) * mm});
            skLineSegment(sketch, "E69", {"start": v(-99.25, 17.23) * mm, "end": v(-99.25, 21.85) * mm});
            skLineSegment(sketch, "E70", {"start": v(-103.88, 9.15) * mm, "end": v(-103.88, 4.53) * mm});
            skLineSegment(sketch, "E71", {"start": v(-103.88, 4.53) * mm, "end": v(-99.25, 4.53) * mm});
            skLineSegment(sketch, "E72", {"start": v(-99.25, 4.53) * mm, "end": v(-99.25, 9.15) * mm});
            skLineSegment(sketch, "E73", {"start": v(-99.25, 9.15) * mm, "end": v(-103.88, 9.15) * mm});
            skLineSegment(sketch, "E74", {"start": v(-111.95, 21.85) * mm, "end": v(-111.95, 17.23) * mm});
            skLineSegment(sketch, "E75", {"start": v(-111.95, 17.23) * mm, "end": v(-116.58, 17.23) * mm});
            skLineSegment(sketch, "E76", {"start": v(-116.58, 17.23) * mm, "end": v(-116.58, 21.85) * mm});
            skLineSegment(sketch, "E77", {"start": v(-116.58, 21.85) * mm, "end": v(-111.95, 21.85) * mm});
            skLineSegment(sketch, "E78.bottom", {"start": v(-116.58, 9.15) * mm, "end": v(-111.95, 9.15) * mm});
            skLineSegment(sketch, "E78.top", {"start": v(-116.58, 4.53) * mm, "end": v(-111.95, 4.53) * mm});
            skLineSegment(sketch, "E78.left", {"start": v(-116.58, 9.15) * mm, "end": v(-116.58, 4.53) * mm});
            skLineSegment(sketch, "E78.right", {"start": v(-111.95, 9.15) * mm, "end": v(-111.95, 4.53) * mm});
            skLineSegment(sketch, "E79", {"start": v(-120.61, 13.2) * mm, "end": v(-120.61, 28.43) * mm});
            skLineSegment(sketch, "E80.top", {"start": v(-120.61, 28.43) * mm, "end": v(-95.21, 28.43) * mm});
            skLineSegment(sketch, "E80.right", {"start": v(-95.21, 13.2) * mm, "end": v(-95.21, 28.43) * mm});
            skLineSegment(sketch, "E81.MirrorCS", {"start": v(-95.21, 13.2) * mm, "end": v(-95.21, -2.05) * mm});
            skLineSegment(sketch, "E82.MirrorCS", {"start": v(-120.61, -2.05) * mm, "end": v(-95.21, -2.05) * mm});
            skLineSegment(sketch, "E83.MirrorCS", {"start": v(-120.61, 13.2) * mm, "end": v(-120.61, -2.05) * mm});
            skSolve(sketch);
        }
        {
            var Q0;
            Q0 = qSketchRegion(id + "F19", true);
            extrude(context, id + "F20", {"entities" : qUnion([Q0]), "depth" : 3.05 * mm});
        }
        {
            var Q0;
            Q0=makeQuery(id+"F20.opExtrude","SWEPT_FACE",FACE,{"disambiguationData":[OSD([sQuery(id+"F19.wireOp",EDGE,"E79"),sQuery(id+"F19.wireOp",EDGE,"E83.MirrorCS")])]});
            var sketch = newSketch(context, id + "F21", { "sketchPlane" : qUnion([Q0])});
            skLineSegment(sketch, "E84", {"start": v(3, 28.43) * mm, "end": v(41.1, 28.43) * mm});
            skPoint(sketch, "E84.endSnap0", {"position": v(5.02, 28.43) * mm});
            skLineSegment(sketch, "E85.bottom", {"start": v(7.04, 21.85) * mm, "end": v(11.66, 21.85) * mm});
            skLineSegment(sketch, "E85.top", {"start": v(7.04, 17.23) * mm, "end": v(11.66, 17.23) * mm});
            skLineSegment(sketch, "E85.left", {"start": v(7.04, 21.85) * mm, "end": v(7.04, 17.23) * mm});
            skLineSegment(sketch, "E85.right", {"start": v(11.66, 21.85) * mm, "end": v(11.66, 17.23) * mm});
            skLineSegment(sketch, "E86.0.1.0", {"start": v(7.04, 4.53) * mm, "end": v(11.66, 4.53) * mm});
            skLineSegment(sketch, "E86.0.1.1", {"start": v(11.66, 9.15) * mm, "end": v(11.66, 4.53) * mm});
            skLineSegment(sketch, "E86.0.1.2", {"start": v(7.04, 9.15) * mm, "end": v(11.66, 9.15) * mm});
            skLineSegment(sketch, "E86.0.1.3", {"start": v(7.04, 9.15) * mm, "end": v(7.04, 4.53) * mm});
            skLineSegment(sketch, "E86.1.0.0", {"start": v(19.74, 17.23) * mm, "end": v(24.36, 17.23) * mm});
            skLineSegment(sketch, "E86.1.0.1", {"start": v(24.36, 21.85) * mm, "end": v(24.36, 17.23) * mm});
            skLineSegment(sketch, "E86.1.0.2", {"start": v(19.74, 21.85) * mm, "end": v(24.36, 21.85) * mm});
            skLineSegment(sketch, "E86.1.0.3", {"start": v(19.74, 21.85) * mm, "end": v(19.74, 17.23) * mm});
            skLineSegment(sketch, "E86.1.1.0", {"start": v(19.74, 4.53) * mm, "end": v(24.36, 4.53) * mm});
            skLineSegment(sketch, "E86.1.1.1", {"start": v(24.36, 9.15) * mm, "end": v(24.36, 4.53) * mm});
            skLineSegment(sketch, "E86.1.1.2", {"start": v(19.74, 9.15) * mm, "end": v(24.36, 9.15) * mm});
            skLineSegment(sketch, "E86.1.1.3", {"start": v(19.74, 9.15) * mm, "end": v(19.74, 4.53) * mm});
            skLineSegment(sketch, "E86.2.0.0", {"start": v(32.44, 17.23) * mm, "end": v(37.06, 17.23) * mm});
            skLineSegment(sketch, "E86.2.0.1", {"start": v(37.06, 21.85) * mm, "end": v(37.06, 17.23) * mm});
            skLineSegment(sketch, "E86.2.0.2", {"start": v(32.44, 21.85) * mm, "end": v(37.06, 21.85) * mm});
            skLineSegment(sketch, "E86.2.0.3", {"start": v(32.44, 21.85) * mm, "end": v(32.44, 17.23) * mm});
            skLineSegment(sketch, "E86.2.1.0", {"start": v(32.44, 4.53) * mm, "end": v(37.06, 4.53) * mm});
            skLineSegment(sketch, "E86.2.1.1", {"start": v(37.06, 9.15) * mm, "end": v(37.06, 4.53) * mm});
            skLineSegment(sketch, "E86.2.1.2", {"start": v(32.44, 9.15) * mm, "end": v(37.06, 9.15) * mm});
            skLineSegment(sketch, "E86.2.1.3", {"start": v(32.44, 9.15) * mm, "end": v(32.44, 4.53) * mm});
            skLineSegment(sketch, "E86.direction1", {"start": v(7.04, 17.23) * mm, "end": v(19.74, 17.23) * mm, "construction": true});
            skLineSegment(sketch, "E86.direction2", {"start": v(7.04, 17.23) * mm, "end": v(7.04, 4.53) * mm, "construction": true});
            skLineSegment(sketch, "E87", {"start": v(41.1, 28.43) * mm, "end": v(41.1, 28.43) * mm});
            skLineSegment(sketch, "E88", {"start": v(3, 28.43) * mm, "end": v(3, 28.43) * mm});
            skLineSegment(sketch, "E89", {"start": v(41.1, 28.43) * mm, "end": v(41.1, -2.05) * mm});
            skPoint(sketch, "E89.endSnap0", {"position": v(4.52, -2.05) * mm});
            skLineSegment(sketch, "E90", {"start": v(41.1, -2.05) * mm, "end": v(3, -2.05) * mm});
            skLineSegment(sketch, "E91", {"start": v(3, -2.05) * mm, "end": v(3, 28.43) * mm});
            skSolve(sketch);
        }
        {
            var Q0;
            Q0 = qSketchRegion(id + "F21", true);
            extrude(context, id + "F22", {"entities" : qUnion([Q0]), "operationType" : NewBodyOperationType.ADD, "oppositeDirection" : true, "depth" : 3.05 * mm});
        }
        {
            var Q0;
            Q0=makeQuery(id+"F22.boolean.opBoolean","MERGE",FACE,{"derivedFrom":[makeQuery(id+"F20.opExtrude","SWEPT_FACE",FACE,{"disambiguationData":[OSD([sQuery(id+"F19.wireOp",EDGE,"ebnsWsaP-uctX-nHvH-lFZW-5bgZdQeTNv2S")])]}),makeQuery(id+"F22.opExtrude","SWEPT_FACE",FACE,{"disambiguationData":[OSD([sQuery(id+"F21.wireOp",EDGE,"E84")])]})]});
            var sketch = newSketch(context, id + "F23", { "sketchPlane" : qUnion([Q0])});
            skLineSegment(sketch, "E92", {"start": v(-95.98, -6.05) * mm, "end": v(-117.57, -6.05) * mm});
            skLineSegment(sketch, "E93", {"start": v(-117.57, -6.05) * mm, "end": v(-117.57, -41.1) * mm});
            skLineSegment(sketch, "E94", {"start": v(-117.57, -41.1) * mm, "end": v(-95.21, -6.05) * mm});
            skLineSegment(sketch, "E95", {"start": v(-95.21, -6.05) * mm, "end": v(-95.98, -6.05) * mm});
            skSolve(sketch);
        }
        {
            var Q0;
            Q0 = qSketchRegion(id + "F23", true);
            extrude(context, id + "F24", {"entities" : qUnion([Q0]), "operationType" : NewBodyOperationType.ADD, "oppositeDirection" : true, "depth" : 3.05 * mm});
        }
        {
            var Q0;
            Q0=makeQuery(id+"F22.boolean.opBoolean","MERGE",FACE,{"derivedFrom":[makeQuery(id+"F20.opExtrude","SWEPT_FACE",FACE,{"disambiguationData":[OSD([sQuery(id+"F19.wireOp",EDGE,"E82.MirrorCS")])]}),makeQuery(id+"F22.opExtrude","SWEPT_FACE",FACE,{"disambiguationData":[OSD([sQuery(id+"F21.wireOp",EDGE,"E90")])]})]});
            var sketch = newSketch(context, id + "F25", { "sketchPlane" : qUnion([Q0])});
            skLineSegment(sketch, "E96", {"start": v(-117.57, 41.1) * mm, "end": v(-117.57, 6.05) * mm});
            skLineSegment(sketch, "E97", {"start": v(-117.57, 6.05) * mm, "end": v(-95.21, 6.05) * mm});
            skLineSegment(sketch, "E98", {"start": v(-95.21, 6.05) * mm, "end": v(-117.57, 41.1) * mm});
            skSolve(sketch);
        }
        {
            var Q0;
            Q0=makeQuery(id+"F22.boolean.opBoolean","MERGE",FACE,{"derivedFrom":[makeQuery(id+"F20.opExtrude","SWEPT_FACE",FACE,{"disambiguationData":[OSD([sQuery(id+"F19.wireOp",EDGE,"E79"),sQuery(id+"F19.wireOp",EDGE,"E83.MirrorCS")])]}),makeQuery(id+"F22.opExtrude","CAP_FACE",FACE,{"disambiguationData":[OSD([sQuery(id+"F21.wireOp",EDGE,"E84"),sQuery(id+"F21.wireOp",EDGE,"E85.bottom"),sQuery(id+"F21.wireOp",EDGE,"E85.top"),sQuery(id+"F21.wireOp",EDGE,"E85.left"),sQuery(id+"F21.wireOp",EDGE,"E85.right"),sQuery(id+"F21.wireOp",EDGE,"E86.0.1.0"),sQuery(id+"F21.wireOp",EDGE,"E86.0.1.1"),sQuery(id+"F21.wireOp",EDGE,"E86.0.1.2"),sQuery(id+"F21.wireOp",EDGE,"E86.0.1.3"),sQuery(id+"F21.wireOp",EDGE,"E86.1.0.0"),sQuery(id+"F21.wireOp",EDGE,"E86.1.0.1"),sQuery(id+"F21.wireOp",EDGE,"E86.1.0.2"),sQuery(id+"F21.wireOp",EDGE,"E86.1.0.3"),sQuery(id+"F21.wireOp",EDGE,"E86.1.1.0"),sQuery(id+"F21.wireOp",EDGE,"E86.1.1.1"),sQuery(id+"F21.wireOp",EDGE,"E86.1.1.2"),sQuery(id+"F21.wireOp",EDGE,"E86.1.1.3"),sQuery(id+"F21.wireOp",EDGE,"E86.2.0.0"),sQuery(id+"F21.wireOp",EDGE,"E86.2.0.1"),sQuery(id+"F21.wireOp",EDGE,"E86.2.0.2"),sQuery(id+"F21.wireOp",EDGE,"E86.2.0.3"),sQuery(id+"F21.wireOp",EDGE,"E86.2.1.0"),sQuery(id+"F21.wireOp",EDGE,"E86.2.1.1"),sQuery(id+"F21.wireOp",EDGE,"E86.2.1.2"),sQuery(id+"F21.wireOp",EDGE,"E86.2.1.3"),sQuery(id+"F21.wireOp",EDGE,"E89"),sQuery(id+"F21.wireOp",EDGE,"E90"),sQuery(id+"F21.wireOp",EDGE,"E91")])],"isStart":true})]});
            var sketch = newSketch(context, id + "F26", { "sketchPlane" : qUnion([Q0])});
            skLineSegment(sketch, "E99", {"start": v(0, 0) * mm, "end": v(0, 165.1) * mm});
            skLineSegment(sketch, "E100", {"start": v(3, 28.43) * mm, "end": v(3, 155.43) * mm});
            skLineSegment(sketch, "E101", {"start": v(3, 0) * mm, "end": v(3, 28.43) * mm});
            skLineSegment(sketch, "E102", {"start": v(3, 155.43) * mm, "end": v(34.75, 155.43) * mm});
            skLineSegment(sketch, "E103", {"start": v(41.1, 149.08) * mm, "end": v(41.1, 0) * mm});
            skLineSegment(sketch, "E104.MirrorCS", {"start": v(41.45, -149.08) * mm, "end": v(41.45, -76.2) * mm});
            skLineSegment(sketch, "E105.bottom", {"start": v(37.06, 148.85) * mm, "end": v(32.44, 148.85) * mm});
            skLineSegment(sketch, "E105.top", {"start": v(37.06, 144.23) * mm, "end": v(32.44, 144.23) * mm});
            skLineSegment(sketch, "E105.left", {"start": v(37.06, 148.85) * mm, "end": v(37.06, 144.23) * mm});
            skLineSegment(sketch, "E105.right", {"start": v(32.44, 148.85) * mm, "end": v(32.44, 144.23) * mm});
            skLineSegment(sketch, "E106.0.1.0", {"start": v(37.06, 131.53) * mm, "end": v(32.44, 131.53) * mm});
            skLineSegment(sketch, "E106.0.1.1", {"start": v(37.06, 136.15) * mm, "end": v(37.06, 131.53) * mm});
            skLineSegment(sketch, "E106.0.1.2", {"start": v(37.06, 136.15) * mm, "end": v(32.44, 136.15) * mm});
            skLineSegment(sketch, "E106.0.1.3", {"start": v(32.44, 136.15) * mm, "end": v(32.44, 131.53) * mm});
            skLineSegment(sketch, "E106.0.2.0", {"start": v(37.06, 118.83) * mm, "end": v(32.44, 118.83) * mm});
            skLineSegment(sketch, "E106.0.2.1", {"start": v(37.06, 123.45) * mm, "end": v(37.06, 118.83) * mm});
            skLineSegment(sketch, "E106.0.2.2", {"start": v(37.06, 123.45) * mm, "end": v(32.44, 123.45) * mm});
            skLineSegment(sketch, "E106.0.2.3", {"start": v(32.44, 123.45) * mm, "end": v(32.44, 118.83) * mm});
            skLineSegment(sketch, "E106.0.3.0", {"start": v(37.06, 106.13) * mm, "end": v(32.44, 106.13) * mm});
            skLineSegment(sketch, "E106.0.3.1", {"start": v(37.06, 110.75) * mm, "end": v(37.06, 106.13) * mm});
            skLineSegment(sketch, "E106.0.3.2", {"start": v(37.06, 110.75) * mm, "end": v(32.44, 110.75) * mm});
            skLineSegment(sketch, "E106.0.3.3", {"start": v(32.44, 110.75) * mm, "end": v(32.44, 106.13) * mm});
            skLineSegment(sketch, "E106.0.4.0", {"start": v(37.06, 93.43) * mm, "end": v(32.44, 93.43) * mm});
            skLineSegment(sketch, "E106.0.4.1", {"start": v(37.06, 98.05) * mm, "end": v(37.06, 93.43) * mm});
            skLineSegment(sketch, "E106.0.4.2", {"start": v(37.06, 98.05) * mm, "end": v(32.44, 98.05) * mm});
            skLineSegment(sketch, "E106.0.4.3", {"start": v(32.44, 98.05) * mm, "end": v(32.44, 93.43) * mm});
            skLineSegment(sketch, "E106.0.5.0", {"start": v(37.06, 80.73) * mm, "end": v(32.44, 80.73) * mm});
            skLineSegment(sketch, "E106.0.5.1", {"start": v(37.06, 85.35) * mm, "end": v(37.06, 80.73) * mm});
            skLineSegment(sketch, "E106.0.5.2", {"start": v(37.06, 85.35) * mm, "end": v(32.44, 85.35) * mm});
            skLineSegment(sketch, "E106.0.5.3", {"start": v(32.44, 85.35) * mm, "end": v(32.44, 80.73) * mm});
            skLineSegment(sketch, "E106.0.6.0", {"start": v(37.06, 68.03) * mm, "end": v(32.44, 68.03) * mm});
            skLineSegment(sketch, "E106.0.6.1", {"start": v(37.06, 72.65) * mm, "end": v(37.06, 68.03) * mm});
            skLineSegment(sketch, "E106.0.6.2", {"start": v(37.06, 72.65) * mm, "end": v(32.44, 72.65) * mm});
            skLineSegment(sketch, "E106.0.6.3", {"start": v(32.44, 72.65) * mm, "end": v(32.44, 68.03) * mm});
            skLineSegment(sketch, "E106.0.7.0", {"start": v(37.06, 55.33) * mm, "end": v(32.44, 55.33) * mm});
            skLineSegment(sketch, "E106.0.7.1", {"start": v(37.06, 59.95) * mm, "end": v(37.06, 55.33) * mm});
            skLineSegment(sketch, "E106.0.7.2", {"start": v(37.06, 59.95) * mm, "end": v(32.44, 59.95) * mm});
            skLineSegment(sketch, "E106.0.7.3", {"start": v(32.44, 59.95) * mm, "end": v(32.44, 55.33) * mm});
            skLineSegment(sketch, "E106.0.8.0", {"start": v(37.06, 42.63) * mm, "end": v(32.44, 42.63) * mm});
            skLineSegment(sketch, "E106.0.8.1", {"start": v(37.06, 47.25) * mm, "end": v(37.06, 42.63) * mm});
            skLineSegment(sketch, "E106.0.8.2", {"start": v(37.06, 47.25) * mm, "end": v(32.44, 47.25) * mm});
            skLineSegment(sketch, "E106.0.8.3", {"start": v(32.44, 47.25) * mm, "end": v(32.44, 42.63) * mm});
            skLineSegment(sketch, "E106.0.9.0", {"start": v(37.06, 29.93) * mm, "end": v(32.44, 29.93) * mm});
            skLineSegment(sketch, "E106.0.9.1", {"start": v(37.06, 34.55) * mm, "end": v(37.06, 29.93) * mm});
            skLineSegment(sketch, "E106.0.9.2", {"start": v(37.06, 34.55) * mm, "end": v(32.44, 34.55) * mm});
            skLineSegment(sketch, "E106.0.9.3", {"start": v(32.44, 34.55) * mm, "end": v(32.44, 29.93) * mm});
            skLineSegment(sketch, "E106.0.10.0", {"start": v(37.06, 17.23) * mm, "end": v(32.44, 17.23) * mm});
            skLineSegment(sketch, "E106.0.10.1", {"start": v(37.06, 21.85) * mm, "end": v(37.06, 17.23) * mm});
            skLineSegment(sketch, "E106.0.10.2", {"start": v(37.06, 21.85) * mm, "end": v(32.44, 21.85) * mm});
            skLineSegment(sketch, "E106.0.10.3", {"start": v(32.44, 21.85) * mm, "end": v(32.44, 17.23) * mm});
            skLineSegment(sketch, "E106.0.11.0", {"start": v(37.06, 4.53) * mm, "end": v(32.44, 4.53) * mm});
            skLineSegment(sketch, "E106.0.11.1", {"start": v(37.06, 9.15) * mm, "end": v(37.06, 4.53) * mm});
            skLineSegment(sketch, "E106.0.11.2", {"start": v(37.06, 9.15) * mm, "end": v(32.44, 9.15) * mm});
            skLineSegment(sketch, "E106.0.11.3", {"start": v(32.44, 9.15) * mm, "end": v(32.44, 4.53) * mm});
            skLineSegment(sketch, "E106.0.12.0", {"start": v(37.06, -8.17) * mm, "end": v(32.44, -8.17) * mm});
            skLineSegment(sketch, "E106.0.12.1", {"start": v(37.06, -3.55) * mm, "end": v(37.06, -8.17) * mm});
            skLineSegment(sketch, "E106.0.12.2", {"start": v(37.06, -3.55) * mm, "end": v(32.44, -3.55) * mm});
            skLineSegment(sketch, "E106.0.12.3", {"start": v(32.44, -3.55) * mm, "end": v(32.44, -8.17) * mm});
            skLineSegment(sketch, "E106.0.13.0", {"start": v(37.06, -20.87) * mm, "end": v(32.44, -20.87) * mm});
            skLineSegment(sketch, "E106.0.13.1", {"start": v(37.06, -16.25) * mm, "end": v(37.06, -20.87) * mm});
            skLineSegment(sketch, "E106.0.13.2", {"start": v(37.06, -16.25) * mm, "end": v(32.44, -16.25) * mm});
            skLineSegment(sketch, "E106.0.13.3", {"start": v(32.44, -16.25) * mm, "end": v(32.44, -20.87) * mm});
            skLineSegment(sketch, "E106.0.14.0", {"start": v(37.06, -33.57) * mm, "end": v(32.44, -33.57) * mm});
            skLineSegment(sketch, "E106.0.14.1", {"start": v(37.06, -28.95) * mm, "end": v(37.06, -33.57) * mm});
            skLineSegment(sketch, "E106.0.14.2", {"start": v(37.06, -28.95) * mm, "end": v(32.44, -28.95) * mm});
            skLineSegment(sketch, "E106.0.14.3", {"start": v(32.44, -28.95) * mm, "end": v(32.44, -33.57) * mm});
            skLineSegment(sketch, "E106.0.15.0", {"start": v(37.06, -46.27) * mm, "end": v(32.44, -46.27) * mm});
            skLineSegment(sketch, "E106.0.15.1", {"start": v(37.06, -41.65) * mm, "end": v(37.06, -46.27) * mm});
            skLineSegment(sketch, "E106.0.15.2", {"start": v(37.06, -41.65) * mm, "end": v(32.44, -41.65) * mm});
            skLineSegment(sketch, "E106.0.15.3", {"start": v(32.44, -41.65) * mm, "end": v(32.44, -46.27) * mm});
            skLineSegment(sketch, "E106.0.16.0", {"start": v(37.06, -58.97) * mm, "end": v(32.44, -58.97) * mm});
            skLineSegment(sketch, "E106.0.16.1", {"start": v(37.06, -54.35) * mm, "end": v(37.06, -58.97) * mm});
            skLineSegment(sketch, "E106.0.16.2", {"start": v(37.06, -54.35) * mm, "end": v(32.44, -54.35) * mm});
            skLineSegment(sketch, "E106.0.16.3", {"start": v(32.44, -54.35) * mm, "end": v(32.44, -58.97) * mm});
            skLineSegment(sketch, "E106.0.17.0", {"start": v(37.06, -71.67) * mm, "end": v(32.44, -71.67) * mm});
            skLineSegment(sketch, "E106.0.17.1", {"start": v(37.06, -67.05) * mm, "end": v(37.06, -71.67) * mm});
            skLineSegment(sketch, "E106.0.17.2", {"start": v(37.06, -67.05) * mm, "end": v(32.44, -67.05) * mm});
            skLineSegment(sketch, "E106.0.17.3", {"start": v(32.44, -67.05) * mm, "end": v(32.44, -71.67) * mm});
            skLineSegment(sketch, "E106.0.18.0", {"start": v(37.06, -84.37) * mm, "end": v(32.44, -84.37) * mm});
            skLineSegment(sketch, "E106.0.18.1", {"start": v(37.06, -79.75) * mm, "end": v(37.06, -84.37) * mm});
            skLineSegment(sketch, "E106.0.18.2", {"start": v(37.06, -79.75) * mm, "end": v(32.44, -79.75) * mm});
            skLineSegment(sketch, "E106.0.18.3", {"start": v(32.44, -79.75) * mm, "end": v(32.44, -84.37) * mm});
            skLineSegment(sketch, "E106.0.19.0", {"start": v(37.06, -97.07) * mm, "end": v(32.44, -97.07) * mm});
            skLineSegment(sketch, "E106.0.19.1", {"start": v(37.06, -92.45) * mm, "end": v(37.06, -97.07) * mm});
            skLineSegment(sketch, "E106.0.19.2", {"start": v(37.06, -92.45) * mm, "end": v(32.44, -92.45) * mm});
            skLineSegment(sketch, "E106.0.19.3", {"start": v(32.44, -92.45) * mm, "end": v(32.44, -97.07) * mm});
            skLineSegment(sketch, "E106.0.20.0", {"start": v(37.06, -109.77) * mm, "end": v(32.44, -109.77) * mm});
            skLineSegment(sketch, "E106.0.20.1", {"start": v(37.06, -105.15) * mm, "end": v(37.06, -109.77) * mm});
            skLineSegment(sketch, "E106.0.20.2", {"start": v(37.06, -105.15) * mm, "end": v(32.44, -105.15) * mm});
            skLineSegment(sketch, "E106.0.20.3", {"start": v(32.44, -105.15) * mm, "end": v(32.44, -109.77) * mm});
            skLineSegment(sketch, "E106.0.21.0", {"start": v(37.06, -122.47) * mm, "end": v(32.44, -122.47) * mm});
            skLineSegment(sketch, "E106.0.21.1", {"start": v(37.06, -117.85) * mm, "end": v(37.06, -122.47) * mm});
            skLineSegment(sketch, "E106.0.21.2", {"start": v(37.06, -117.85) * mm, "end": v(32.44, -117.85) * mm});
            skLineSegment(sketch, "E106.0.21.3", {"start": v(32.44, -117.85) * mm, "end": v(32.44, -122.47) * mm});
            skLineSegment(sketch, "E106.0.22.0", {"start": v(37.06, -135.17) * mm, "end": v(32.44, -135.17) * mm});
            skLineSegment(sketch, "E106.0.22.1", {"start": v(37.06, -130.55) * mm, "end": v(37.06, -135.17) * mm});
            skLineSegment(sketch, "E106.0.22.2", {"start": v(37.06, -130.55) * mm, "end": v(32.44, -130.55) * mm});
            skLineSegment(sketch, "E106.0.22.3", {"start": v(32.44, -130.55) * mm, "end": v(32.44, -135.17) * mm});
            skLineSegment(sketch, "E106.0.23.0", {"start": v(37.06, -147.87) * mm, "end": v(32.44, -147.87) * mm});
            skLineSegment(sketch, "E106.0.23.1", {"start": v(37.06, -143.25) * mm, "end": v(37.06, -147.87) * mm});
            skLineSegment(sketch, "E106.0.23.2", {"start": v(37.06, -143.25) * mm, "end": v(32.44, -143.25) * mm});
            skLineSegment(sketch, "E106.0.23.3", {"start": v(32.44, -143.25) * mm, "end": v(32.44, -147.87) * mm});
            skLineSegment(sketch, "E106.1.0.0", {"start": v(24.36, 144.23) * mm, "end": v(19.74, 144.23) * mm});
            skLineSegment(sketch, "E106.1.0.1", {"start": v(24.36, 148.85) * mm, "end": v(24.36, 144.23) * mm});
            skLineSegment(sketch, "E106.1.0.2", {"start": v(24.36, 148.85) * mm, "end": v(19.74, 148.85) * mm});
            skLineSegment(sketch, "E106.1.0.3", {"start": v(19.74, 148.85) * mm, "end": v(19.74, 144.23) * mm});
            skLineSegment(sketch, "E106.1.1.0", {"start": v(24.36, 131.53) * mm, "end": v(19.74, 131.53) * mm});
            skLineSegment(sketch, "E106.1.1.1", {"start": v(24.36, 136.15) * mm, "end": v(24.36, 131.53) * mm});
            skLineSegment(sketch, "E106.1.1.2", {"start": v(24.36, 136.15) * mm, "end": v(19.74, 136.15) * mm});
            skLineSegment(sketch, "E106.1.1.3", {"start": v(19.74, 136.15) * mm, "end": v(19.74, 131.53) * mm});
            skLineSegment(sketch, "E106.1.2.0", {"start": v(24.36, 118.83) * mm, "end": v(19.74, 118.83) * mm});
            skLineSegment(sketch, "E106.1.2.1", {"start": v(24.36, 123.45) * mm, "end": v(24.36, 118.83) * mm});
            skLineSegment(sketch, "E106.1.2.2", {"start": v(24.36, 123.45) * mm, "end": v(19.74, 123.45) * mm});
            skLineSegment(sketch, "E106.1.2.3", {"start": v(19.74, 123.45) * mm, "end": v(19.74, 118.83) * mm});
            skLineSegment(sketch, "E106.1.3.0", {"start": v(24.36, 106.13) * mm, "end": v(19.74, 106.13) * mm});
            skLineSegment(sketch, "E106.1.3.1", {"start": v(24.36, 110.75) * mm, "end": v(24.36, 106.13) * mm});
            skLineSegment(sketch, "E106.1.3.2", {"start": v(24.36, 110.75) * mm, "end": v(19.74, 110.75) * mm});
            skLineSegment(sketch, "E106.1.3.3", {"start": v(19.74, 110.75) * mm, "end": v(19.74, 106.13) * mm});
            skLineSegment(sketch, "E106.1.4.0", {"start": v(24.36, 93.43) * mm, "end": v(19.74, 93.43) * mm});
            skLineSegment(sketch, "E106.1.4.1", {"start": v(24.36, 98.05) * mm, "end": v(24.36, 93.43) * mm});
            skLineSegment(sketch, "E106.1.4.2", {"start": v(24.36, 98.05) * mm, "end": v(19.74, 98.05) * mm});
            skLineSegment(sketch, "E106.1.4.3", {"start": v(19.74, 98.05) * mm, "end": v(19.74, 93.43) * mm});
            skLineSegment(sketch, "E106.1.5.0", {"start": v(24.36, 80.73) * mm, "end": v(19.74, 80.73) * mm});
            skLineSegment(sketch, "E106.1.5.1", {"start": v(24.36, 85.35) * mm, "end": v(24.36, 80.73) * mm});
            skLineSegment(sketch, "E106.1.5.2", {"start": v(24.36, 85.35) * mm, "end": v(19.74, 85.35) * mm});
            skLineSegment(sketch, "E106.1.5.3", {"start": v(19.74, 85.35) * mm, "end": v(19.74, 80.73) * mm});
            skLineSegment(sketch, "E106.1.6.0", {"start": v(24.36, 68.03) * mm, "end": v(19.74, 68.03) * mm});
            skLineSegment(sketch, "E106.1.6.1", {"start": v(24.36, 72.65) * mm, "end": v(24.36, 68.03) * mm});
            skLineSegment(sketch, "E106.1.6.2", {"start": v(24.36, 72.65) * mm, "end": v(19.74, 72.65) * mm});
            skLineSegment(sketch, "E106.1.6.3", {"start": v(19.74, 72.65) * mm, "end": v(19.74, 68.03) * mm});
            skLineSegment(sketch, "E106.1.7.0", {"start": v(24.36, 55.33) * mm, "end": v(19.74, 55.33) * mm});
            skLineSegment(sketch, "E106.1.7.1", {"start": v(24.36, 59.95) * mm, "end": v(24.36, 55.33) * mm});
            skLineSegment(sketch, "E106.1.7.2", {"start": v(24.36, 59.95) * mm, "end": v(19.74, 59.95) * mm});
            skLineSegment(sketch, "E106.1.7.3", {"start": v(19.74, 59.95) * mm, "end": v(19.74, 55.33) * mm});
            skLineSegment(sketch, "E106.1.8.0", {"start": v(24.36, 42.63) * mm, "end": v(19.74, 42.63) * mm});
            skLineSegment(sketch, "E106.1.8.1", {"start": v(24.36, 47.25) * mm, "end": v(24.36, 42.63) * mm});
            skLineSegment(sketch, "E106.1.8.2", {"start": v(24.36, 47.25) * mm, "end": v(19.74, 47.25) * mm});
            skLineSegment(sketch, "E106.1.8.3", {"start": v(19.74, 47.25) * mm, "end": v(19.74, 42.63) * mm});
            skLineSegment(sketch, "E106.1.9.0", {"start": v(24.36, 29.93) * mm, "end": v(19.74, 29.93) * mm});
            skLineSegment(sketch, "E106.1.9.1", {"start": v(24.36, 34.55) * mm, "end": v(24.36, 29.93) * mm});
            skLineSegment(sketch, "E106.1.9.2", {"start": v(24.36, 34.55) * mm, "end": v(19.74, 34.55) * mm});
            skLineSegment(sketch, "E106.1.9.3", {"start": v(19.74, 34.55) * mm, "end": v(19.74, 29.93) * mm});
            skLineSegment(sketch, "E106.1.10.0", {"start": v(24.36, 17.23) * mm, "end": v(19.74, 17.23) * mm});
            skLineSegment(sketch, "E106.1.10.1", {"start": v(24.36, 21.85) * mm, "end": v(24.36, 17.23) * mm});
            skLineSegment(sketch, "E106.1.10.2", {"start": v(24.36, 21.85) * mm, "end": v(19.74, 21.85) * mm});
            skLineSegment(sketch, "E106.1.10.3", {"start": v(19.74, 21.85) * mm, "end": v(19.74, 17.23) * mm});
            skLineSegment(sketch, "E106.1.11.0", {"start": v(24.36, 4.53) * mm, "end": v(19.74, 4.53) * mm});
            skLineSegment(sketch, "E106.1.11.1", {"start": v(24.36, 9.15) * mm, "end": v(24.36, 4.53) * mm});
            skLineSegment(sketch, "E106.1.11.2", {"start": v(24.36, 9.15) * mm, "end": v(19.74, 9.15) * mm});
            skLineSegment(sketch, "E106.1.11.3", {"start": v(19.74, 9.15) * mm, "end": v(19.74, 4.53) * mm});
            skLineSegment(sketch, "E106.1.12.0", {"start": v(24.36, -8.17) * mm, "end": v(19.74, -8.17) * mm});
            skLineSegment(sketch, "E106.1.12.1", {"start": v(24.36, -3.55) * mm, "end": v(24.36, -8.17) * mm});
            skLineSegment(sketch, "E106.1.12.2", {"start": v(24.36, -3.55) * mm, "end": v(19.74, -3.55) * mm});
            skLineSegment(sketch, "E106.1.12.3", {"start": v(19.74, -3.55) * mm, "end": v(19.74, -8.17) * mm});
            skLineSegment(sketch, "E106.1.13.0", {"start": v(24.36, -20.87) * mm, "end": v(19.74, -20.87) * mm});
            skLineSegment(sketch, "E106.1.13.1", {"start": v(24.36, -16.25) * mm, "end": v(24.36, -20.87) * mm});
            skLineSegment(sketch, "E106.1.13.2", {"start": v(24.36, -16.25) * mm, "end": v(19.74, -16.25) * mm});
            skLineSegment(sketch, "E106.1.13.3", {"start": v(19.74, -16.25) * mm, "end": v(19.74, -20.87) * mm});
            skLineSegment(sketch, "E106.1.14.0", {"start": v(24.36, -33.57) * mm, "end": v(19.74, -33.57) * mm});
            skLineSegment(sketch, "E106.1.14.1", {"start": v(24.36, -28.95) * mm, "end": v(24.36, -33.57) * mm});
            skLineSegment(sketch, "E106.1.14.2", {"start": v(24.36, -28.95) * mm, "end": v(19.74, -28.95) * mm});
            skLineSegment(sketch, "E106.1.14.3", {"start": v(19.74, -28.95) * mm, "end": v(19.74, -33.57) * mm});
            skLineSegment(sketch, "E106.1.15.0", {"start": v(24.36, -46.27) * mm, "end": v(19.74, -46.27) * mm});
            skLineSegment(sketch, "E106.1.15.1", {"start": v(24.36, -41.65) * mm, "end": v(24.36, -46.27) * mm});
            skLineSegment(sketch, "E106.1.15.2", {"start": v(24.36, -41.65) * mm, "end": v(19.74, -41.65) * mm});
            skLineSegment(sketch, "E106.1.15.3", {"start": v(19.74, -41.65) * mm, "end": v(19.74, -46.27) * mm});
            skLineSegment(sketch, "E106.1.16.0", {"start": v(24.36, -58.97) * mm, "end": v(19.74, -58.97) * mm});
            skLineSegment(sketch, "E106.1.16.1", {"start": v(24.36, -54.35) * mm, "end": v(24.36, -58.97) * mm});
            skLineSegment(sketch, "E106.1.16.2", {"start": v(24.36, -54.35) * mm, "end": v(19.74, -54.35) * mm});
            skLineSegment(sketch, "E106.1.16.3", {"start": v(19.74, -54.35) * mm, "end": v(19.74, -58.97) * mm});
            skLineSegment(sketch, "E106.1.17.0", {"start": v(24.36, -71.67) * mm, "end": v(19.74, -71.67) * mm});
            skLineSegment(sketch, "E106.1.17.1", {"start": v(24.36, -67.05) * mm, "end": v(24.36, -71.67) * mm});
            skLineSegment(sketch, "E106.1.17.2", {"start": v(24.36, -67.05) * mm, "end": v(19.74, -67.05) * mm});
            skLineSegment(sketch, "E106.1.17.3", {"start": v(19.74, -67.05) * mm, "end": v(19.74, -71.67) * mm});
            skLineSegment(sketch, "E106.1.18.0", {"start": v(24.36, -84.37) * mm, "end": v(19.74, -84.37) * mm});
            skLineSegment(sketch, "E106.1.18.1", {"start": v(24.36, -79.75) * mm, "end": v(24.36, -84.37) * mm});
            skLineSegment(sketch, "E106.1.18.2", {"start": v(24.36, -79.75) * mm, "end": v(19.74, -79.75) * mm});
            skLineSegment(sketch, "E106.1.18.3", {"start": v(19.74, -79.75) * mm, "end": v(19.74, -84.37) * mm});
            skLineSegment(sketch, "E106.1.19.0", {"start": v(24.36, -97.07) * mm, "end": v(19.74, -97.07) * mm});
            skLineSegment(sketch, "E106.1.19.1", {"start": v(24.36, -92.45) * mm, "end": v(24.36, -97.07) * mm});
            skLineSegment(sketch, "E106.1.19.2", {"start": v(24.36, -92.45) * mm, "end": v(19.74, -92.45) * mm});
            skLineSegment(sketch, "E106.1.19.3", {"start": v(19.74, -92.45) * mm, "end": v(19.74, -97.07) * mm});
            skLineSegment(sketch, "E106.1.20.0", {"start": v(24.36, -109.77) * mm, "end": v(19.74, -109.77) * mm});
            skLineSegment(sketch, "E106.1.20.1", {"start": v(24.36, -105.15) * mm, "end": v(24.36, -109.77) * mm});
            skLineSegment(sketch, "E106.1.20.2", {"start": v(24.36, -105.15) * mm, "end": v(19.74, -105.15) * mm});
            skLineSegment(sketch, "E106.1.20.3", {"start": v(19.74, -105.15) * mm, "end": v(19.74, -109.77) * mm});
            skLineSegment(sketch, "E106.1.21.0", {"start": v(24.36, -122.47) * mm, "end": v(19.74, -122.47) * mm});
            skLineSegment(sketch, "E106.1.21.1", {"start": v(24.36, -117.85) * mm, "end": v(24.36, -122.47) * mm});
            skLineSegment(sketch, "E106.1.21.2", {"start": v(24.36, -117.85) * mm, "end": v(19.74, -117.85) * mm});
            skLineSegment(sketch, "E106.1.21.3", {"start": v(19.74, -117.85) * mm, "end": v(19.74, -122.47) * mm});
            skLineSegment(sketch, "E106.1.22.0", {"start": v(24.36, -135.17) * mm, "end": v(19.74, -135.17) * mm});
            skLineSegment(sketch, "E106.1.22.1", {"start": v(24.36, -130.55) * mm, "end": v(24.36, -135.17) * mm});
            skLineSegment(sketch, "E106.1.22.2", {"start": v(24.36, -130.55) * mm, "end": v(19.74, -130.55) * mm});
            skLineSegment(sketch, "E106.1.22.3", {"start": v(19.74, -130.55) * mm, "end": v(19.74, -135.17) * mm});
            skLineSegment(sketch, "E106.1.23.0", {"start": v(24.36, -147.87) * mm, "end": v(19.74, -147.87) * mm});
            skLineSegment(sketch, "E106.1.23.1", {"start": v(24.36, -143.25) * mm, "end": v(24.36, -147.87) * mm});
            skLineSegment(sketch, "E106.1.23.2", {"start": v(24.36, -143.25) * mm, "end": v(19.74, -143.25) * mm});
            skLineSegment(sketch, "E106.1.23.3", {"start": v(19.74, -143.25) * mm, "end": v(19.74, -147.87) * mm});
            skLineSegment(sketch, "E106.2.0.0", {"start": v(11.66, 144.23) * mm, "end": v(7.04, 144.23) * mm});
            skLineSegment(sketch, "E106.2.0.1", {"start": v(11.66, 148.85) * mm, "end": v(11.66, 144.23) * mm});
            skLineSegment(sketch, "E106.2.0.2", {"start": v(11.66, 148.85) * mm, "end": v(7.04, 148.85) * mm});
            skLineSegment(sketch, "E106.2.0.3", {"start": v(7.04, 148.85) * mm, "end": v(7.04, 144.23) * mm});
            skLineSegment(sketch, "E106.2.1.0", {"start": v(11.66, 131.53) * mm, "end": v(7.04, 131.53) * mm});
            skLineSegment(sketch, "E106.2.1.1", {"start": v(11.66, 136.15) * mm, "end": v(11.66, 131.53) * mm});
            skLineSegment(sketch, "E106.2.1.2", {"start": v(11.66, 136.15) * mm, "end": v(7.04, 136.15) * mm});
            skLineSegment(sketch, "E106.2.1.3", {"start": v(7.04, 136.15) * mm, "end": v(7.04, 131.53) * mm});
            skLineSegment(sketch, "E106.2.2.0", {"start": v(11.66, 118.83) * mm, "end": v(7.04, 118.83) * mm});
            skLineSegment(sketch, "E106.2.2.1", {"start": v(11.66, 123.45) * mm, "end": v(11.66, 118.83) * mm});
            skLineSegment(sketch, "E106.2.2.2", {"start": v(11.66, 123.45) * mm, "end": v(7.04, 123.45) * mm});
            skLineSegment(sketch, "E106.2.2.3", {"start": v(7.04, 123.45) * mm, "end": v(7.04, 118.83) * mm});
            skLineSegment(sketch, "E106.2.3.0", {"start": v(11.66, 106.13) * mm, "end": v(7.04, 106.13) * mm});
            skLineSegment(sketch, "E106.2.3.1", {"start": v(11.66, 110.75) * mm, "end": v(11.66, 106.13) * mm});
            skLineSegment(sketch, "E106.2.3.2", {"start": v(11.66, 110.75) * mm, "end": v(7.04, 110.75) * mm});
            skLineSegment(sketch, "E106.2.3.3", {"start": v(7.04, 110.75) * mm, "end": v(7.04, 106.13) * mm});
            skLineSegment(sketch, "E106.2.4.0", {"start": v(11.66, 93.43) * mm, "end": v(7.04, 93.43) * mm});
            skLineSegment(sketch, "E106.2.4.1", {"start": v(11.66, 98.05) * mm, "end": v(11.66, 93.43) * mm});
            skLineSegment(sketch, "E106.2.4.2", {"start": v(11.66, 98.05) * mm, "end": v(7.04, 98.05) * mm});
            skLineSegment(sketch, "E106.2.4.3", {"start": v(7.04, 98.05) * mm, "end": v(7.04, 93.43) * mm});
            skLineSegment(sketch, "E106.2.5.0", {"start": v(11.66, 80.73) * mm, "end": v(7.04, 80.73) * mm});
            skLineSegment(sketch, "E106.2.5.1", {"start": v(11.66, 85.35) * mm, "end": v(11.66, 80.73) * mm});
            skLineSegment(sketch, "E106.2.5.2", {"start": v(11.66, 85.35) * mm, "end": v(7.04, 85.35) * mm});
            skLineSegment(sketch, "E106.2.5.3", {"start": v(7.04, 85.35) * mm, "end": v(7.04, 80.73) * mm});
            skLineSegment(sketch, "E106.2.6.0", {"start": v(11.66, 68.03) * mm, "end": v(7.04, 68.03) * mm});
            skLineSegment(sketch, "E106.2.6.1", {"start": v(11.66, 72.65) * mm, "end": v(11.66, 68.03) * mm});
            skLineSegment(sketch, "E106.2.6.2", {"start": v(11.66, 72.65) * mm, "end": v(7.04, 72.65) * mm});
            skLineSegment(sketch, "E106.2.6.3", {"start": v(7.04, 72.65) * mm, "end": v(7.04, 68.03) * mm});
            skLineSegment(sketch, "E106.2.7.0", {"start": v(11.66, 55.33) * mm, "end": v(7.04, 55.33) * mm});
            skLineSegment(sketch, "E106.2.7.1", {"start": v(11.66, 59.95) * mm, "end": v(11.66, 55.33) * mm});
            skLineSegment(sketch, "E106.2.7.2", {"start": v(11.66, 59.95) * mm, "end": v(7.04, 59.95) * mm});
            skLineSegment(sketch, "E106.2.7.3", {"start": v(7.04, 59.95) * mm, "end": v(7.04, 55.33) * mm});
            skLineSegment(sketch, "E106.2.8.0", {"start": v(11.66, 42.63) * mm, "end": v(7.04, 42.63) * mm});
            skLineSegment(sketch, "E106.2.8.1", {"start": v(11.66, 47.25) * mm, "end": v(11.66, 42.63) * mm});
            skLineSegment(sketch, "E106.2.8.2", {"start": v(11.66, 47.25) * mm, "end": v(7.04, 47.25) * mm});
            skLineSegment(sketch, "E106.2.8.3", {"start": v(7.04, 47.25) * mm, "end": v(7.04, 42.63) * mm});
            skLineSegment(sketch, "E106.2.9.0", {"start": v(11.66, 29.93) * mm, "end": v(7.04, 29.93) * mm});
            skLineSegment(sketch, "E106.2.9.1", {"start": v(11.66, 34.55) * mm, "end": v(11.66, 29.93) * mm});
            skLineSegment(sketch, "E106.2.9.2", {"start": v(11.66, 34.55) * mm, "end": v(7.04, 34.55) * mm});
            skLineSegment(sketch, "E106.2.9.3", {"start": v(7.04, 34.55) * mm, "end": v(7.04, 29.93) * mm});
            skLineSegment(sketch, "E106.2.10.0", {"start": v(11.66, 17.23) * mm, "end": v(7.04, 17.23) * mm});
            skLineSegment(sketch, "E106.2.10.1", {"start": v(11.66, 21.85) * mm, "end": v(11.66, 17.23) * mm});
            skLineSegment(sketch, "E106.2.10.2", {"start": v(11.66, 21.85) * mm, "end": v(7.04, 21.85) * mm});
            skLineSegment(sketch, "E106.2.10.3", {"start": v(7.04, 21.85) * mm, "end": v(7.04, 17.23) * mm});
            skLineSegment(sketch, "E106.2.11.0", {"start": v(11.66, 4.53) * mm, "end": v(7.04, 4.53) * mm});
            skLineSegment(sketch, "E106.2.11.1", {"start": v(11.66, 9.15) * mm, "end": v(11.66, 4.53) * mm});
            skLineSegment(sketch, "E106.2.11.2", {"start": v(11.66, 9.15) * mm, "end": v(7.04, 9.15) * mm});
            skLineSegment(sketch, "E106.2.11.3", {"start": v(7.04, 9.15) * mm, "end": v(7.04, 4.53) * mm});
            skLineSegment(sketch, "E106.2.12.0", {"start": v(11.66, -8.17) * mm, "end": v(7.04, -8.17) * mm});
            skLineSegment(sketch, "E106.2.12.1", {"start": v(11.66, -3.55) * mm, "end": v(11.66, -8.17) * mm});
            skLineSegment(sketch, "E106.2.12.2", {"start": v(11.66, -3.55) * mm, "end": v(7.04, -3.55) * mm});
            skLineSegment(sketch, "E106.2.12.3", {"start": v(7.04, -3.55) * mm, "end": v(7.04, -8.17) * mm});
            skLineSegment(sketch, "E106.2.13.0", {"start": v(11.66, -20.87) * mm, "end": v(7.04, -20.87) * mm});
            skLineSegment(sketch, "E106.2.13.1", {"start": v(11.66, -16.25) * mm, "end": v(11.66, -20.87) * mm});
            skLineSegment(sketch, "E106.2.13.2", {"start": v(11.66, -16.25) * mm, "end": v(7.04, -16.25) * mm});
            skLineSegment(sketch, "E106.2.13.3", {"start": v(7.04, -16.25) * mm, "end": v(7.04, -20.87) * mm});
            skLineSegment(sketch, "E106.2.14.0", {"start": v(11.66, -33.57) * mm, "end": v(7.04, -33.57) * mm});
            skLineSegment(sketch, "E106.2.14.1", {"start": v(11.66, -28.95) * mm, "end": v(11.66, -33.57) * mm});
            skLineSegment(sketch, "E106.2.14.2", {"start": v(11.66, -28.95) * mm, "end": v(7.04, -28.95) * mm});
            skLineSegment(sketch, "E106.2.14.3", {"start": v(7.04, -28.95) * mm, "end": v(7.04, -33.57) * mm});
            skLineSegment(sketch, "E106.2.15.0", {"start": v(11.66, -46.27) * mm, "end": v(7.04, -46.27) * mm});
            skLineSegment(sketch, "E106.2.15.1", {"start": v(11.66, -41.65) * mm, "end": v(11.66, -46.27) * mm});
            skLineSegment(sketch, "E106.2.15.2", {"start": v(11.66, -41.65) * mm, "end": v(7.04, -41.65) * mm});
            skLineSegment(sketch, "E106.2.15.3", {"start": v(7.04, -41.65) * mm, "end": v(7.04, -46.27) * mm});
            skLineSegment(sketch, "E106.2.16.0", {"start": v(11.66, -58.97) * mm, "end": v(7.04, -58.97) * mm});
            skLineSegment(sketch, "E106.2.16.1", {"start": v(11.66, -54.35) * mm, "end": v(11.66, -58.97) * mm});
            skLineSegment(sketch, "E106.2.16.2", {"start": v(11.66, -54.35) * mm, "end": v(7.04, -54.35) * mm});
            skLineSegment(sketch, "E106.2.16.3", {"start": v(7.04, -54.35) * mm, "end": v(7.04, -58.97) * mm});
            skLineSegment(sketch, "E106.2.17.0", {"start": v(11.66, -71.67) * mm, "end": v(7.04, -71.67) * mm});
            skLineSegment(sketch, "E106.2.17.1", {"start": v(11.66, -67.05) * mm, "end": v(11.66, -71.67) * mm});
            skLineSegment(sketch, "E106.2.17.2", {"start": v(11.66, -67.05) * mm, "end": v(7.04, -67.05) * mm});
            skLineSegment(sketch, "E106.2.17.3", {"start": v(7.04, -67.05) * mm, "end": v(7.04, -71.67) * mm});
            skLineSegment(sketch, "E106.2.18.0", {"start": v(11.66, -84.37) * mm, "end": v(7.04, -84.37) * mm});
            skLineSegment(sketch, "E106.2.18.1", {"start": v(11.66, -79.75) * mm, "end": v(11.66, -84.37) * mm});
            skLineSegment(sketch, "E106.2.18.2", {"start": v(11.66, -79.75) * mm, "end": v(7.04, -79.75) * mm});
            skLineSegment(sketch, "E106.2.18.3", {"start": v(7.04, -79.75) * mm, "end": v(7.04, -84.37) * mm});
            skLineSegment(sketch, "E106.2.19.0", {"start": v(11.66, -97.07) * mm, "end": v(7.04, -97.07) * mm});
            skLineSegment(sketch, "E106.2.19.1", {"start": v(11.66, -92.45) * mm, "end": v(11.66, -97.07) * mm});
            skLineSegment(sketch, "E106.2.19.2", {"start": v(11.66, -92.45) * mm, "end": v(7.04, -92.45) * mm});
            skLineSegment(sketch, "E106.2.19.3", {"start": v(7.04, -92.45) * mm, "end": v(7.04, -97.07) * mm});
            skLineSegment(sketch, "E106.2.20.0", {"start": v(11.66, -109.77) * mm, "end": v(7.04, -109.77) * mm});
            skLineSegment(sketch, "E106.2.20.1", {"start": v(11.66, -105.15) * mm, "end": v(11.66, -109.77) * mm});
            skLineSegment(sketch, "E106.2.20.2", {"start": v(11.66, -105.15) * mm, "end": v(7.04, -105.15) * mm});
            skLineSegment(sketch, "E106.2.20.3", {"start": v(7.04, -105.15) * mm, "end": v(7.04, -109.77) * mm});
            skLineSegment(sketch, "E106.2.21.0", {"start": v(11.66, -122.47) * mm, "end": v(7.04, -122.47) * mm});
            skLineSegment(sketch, "E106.2.21.1", {"start": v(11.66, -117.85) * mm, "end": v(11.66, -122.47) * mm});
            skLineSegment(sketch, "E106.2.21.2", {"start": v(11.66, -117.85) * mm, "end": v(7.04, -117.85) * mm});
            skLineSegment(sketch, "E106.2.21.3", {"start": v(7.04, -117.85) * mm, "end": v(7.04, -122.47) * mm});
            skLineSegment(sketch, "E106.2.22.0", {"start": v(11.66, -135.17) * mm, "end": v(7.04, -135.17) * mm});
            skLineSegment(sketch, "E106.2.22.1", {"start": v(11.66, -130.55) * mm, "end": v(11.66, -135.17) * mm});
            skLineSegment(sketch, "E106.2.22.2", {"start": v(11.66, -130.55) * mm, "end": v(7.04, -130.55) * mm});
            skLineSegment(sketch, "E106.2.22.3", {"start": v(7.04, -130.55) * mm, "end": v(7.04, -135.17) * mm});
            skLineSegment(sketch, "E106.2.23.0", {"start": v(11.66, -147.87) * mm, "end": v(7.04, -147.87) * mm});
            skLineSegment(sketch, "E106.2.23.1", {"start": v(11.66, -143.25) * mm, "end": v(11.66, -147.87) * mm});
            skLineSegment(sketch, "E106.2.23.2", {"start": v(11.66, -143.25) * mm, "end": v(7.04, -143.25) * mm});
            skLineSegment(sketch, "E106.2.23.3", {"start": v(7.04, -143.25) * mm, "end": v(7.04, -147.87) * mm});
            skLineSegment(sketch, "E106.direction1", {"start": v(32.44, 144.23) * mm, "end": v(19.74, 144.23) * mm, "construction": true});
            skLineSegment(sketch, "E106.direction2", {"start": v(32.44, 144.23) * mm, "end": v(32.44, 131.53) * mm, "construction": true});
            skPoint(sketch, "E107.visualSharp", {"position": v(41.1, 155.43) * mm});
            skArc(sketch, "E107.filletArc", {"start": v(41.1, 149.08) * mm, "mid": v(39.24, 153.57) * mm, "end": v(34.75, 155.43) * mm});
            skLineSegment(sketch, "E108", {"start": v(41.1, 0) * mm, "end": v(41.45, -76.2) * mm});
            skLineSegment(sketch, "E109", {"start": v(3, 0) * mm, "end": v(3.35, -104.63) * mm});
            skLineSegment(sketch, "E110", {"start": v(3.35, -104.63) * mm, "end": v(3.35, -155.43) * mm});
            skLineSegment(sketch, "E111", {"start": v(41.45, -149.08) * mm, "end": v(41.45, -155.43) * mm});
            skLineSegment(sketch, "E112", {"start": v(3.35, -155.43) * mm, "end": v(-10.1, -155.43) * mm});
            skPoint(sketch, "E113.end.orphan", {"position": v(22.05, -155.43) * mm});
            skPoint(sketch, "E113.start.orphan", {"position": v(22.05, -147.87) * mm});
            skLineSegment(sketch, "E114", {"start": v(-10.1, -155.43) * mm, "end": v(-10.1, -257.03) * mm});
            skLineSegment(sketch, "E115", {"start": v(-10.1, -257.03) * mm, "end": v(13.9, -209.72) * mm});
            skLineSegment(sketch, "E116", {"start": v(25.4, -187.07) * mm, "end": v(19.74, -184.2) * mm});
            skLineSegment(sketch, "E117", {"start": v(19.74, -184.2) * mm, "end": v(8.24, -206.85) * mm});
            skLineSegment(sketch, "E118", {"start": v(8.24, -206.85) * mm, "end": v(13.9, -209.72) * mm});
            skLineSegment(sketch, "E119.trimOffspring", {"start": v(25.4, -187.07) * mm, "end": v(41.45, -155.43) * mm});
            skSolve(sketch);
        }
        {
            var Q0;
            Q0 = qSketchRegion(id + "F25", true);
            extrude(context, id + "F27", {"entities" : qUnion([Q0]), "operationType" : NewBodyOperationType.ADD, "oppositeDirection" : true, "depth" : 3.05 * mm});
        }
        {
            var Q0;
            Q0 = qSketchRegion(id + "F26", true);
            extrude(context, id + "F28", {"entities" : qUnion([Q0]), "depth" : 3.8 * mm});
        }
        {
            var Q0;
            Q0=makeQuery(id+"F2.opExtrude","CAP_FACE",FACE,{"disambiguationData":[OSD([sQuery(id+"F0.wireOp",EDGE,"e2akh6Oa-UBHa-86Pb-ZkKs-OABukGgOBKLV.right"),sQuery(id+"F0.wireOp",EDGE,"RFzYo0nL-dbGn-g4QQ-aZl6-wjgrSkBCbLW4.bottom"),sQuery(id+"F0.wireOp",EDGE,"RFzYo0nL-dbGn-g4QQ-aZl6-wjgrSkBCbLW4.top"),sQuery(id+"F0.wireOp",EDGE,"RFzYo0nL-dbGn-g4QQ-aZl6-wjgrSkBCbLW4.left"),sQuery(id+"F0.wireOp",EDGE,"RFzYo0nL-dbGn-g4QQ-aZl6-wjgrSkBCbLW4.right"),sQuery(id+"F0.wireOp",EDGE,"7c84c30b-10c3-426a-8278-929d31200ebf.0.1.0"),sQuery(id+"F0.wireOp",EDGE,"7c84c30b-10c3-426a-8278-929d31200ebf.0.1.1"),sQuery(id+"F0.wireOp",EDGE,"7c84c30b-10c3-426a-8278-929d31200ebf.0.1.2"),sQuery(id+"F0.wireOp",EDGE,"7c84c30b-10c3-426a-8278-929d31200ebf.0.1.3"),sQuery(id+"F0.wireOp",EDGE,"7c84c30b-10c3-426a-8278-929d31200ebf.0.2.0"),sQuery(id+"F0.wireOp",EDGE,"7c84c30b-10c3-426a-8278-929d31200ebf.0.2.1"),sQuery(id+"F0.wireOp",EDGE,"7c84c30b-10c3-426a-8278-929d31200ebf.0.2.2"),sQuery(id+"F0.wireOp",EDGE,"7c84c30b-10c3-426a-8278-929d31200ebf.0.2.3"),sQuery(id+"F0.wireOp",EDGE,"7c84c30b-10c3-426a-8278-929d31200ebf.0.3.0"),sQuery(id+"F0.wireOp",EDGE,"7c84c30b-10c3-426a-8278-929d31200ebf.0.3.1"),sQuery(id+"F0.wireOp",EDGE,"7c84c30b-10c3-426a-8278-929d31200ebf.0.3.2"),sQuery(id+"F0.wireOp",EDGE,"7c84c30b-10c3-426a-8278-929d31200ebf.0.3.3"),sQuery(id+"F0.wireOp",EDGE,"7c84c30b-10c3-426a-8278-929d31200ebf.0.4.0"),sQuery(id+"F0.wireOp",EDGE,"7c84c30b-10c3-426a-8278-929d31200ebf.0.4.1"),sQuery(id+"F0.wireOp",EDGE,"7c84c30b-10c3-426a-8278-929d31200ebf.0.4.2"),sQuery(id+"F0.wireOp",EDGE,"7c84c30b-10c3-426a-8278-929d31200ebf.0.4.3"),sQuery(id+"F0.wireOp",EDGE,"7c84c30b-10c3-426a-8278-929d31200ebf.0.5.0"),sQuery(id+"F0.wireOp",EDGE,"7c84c30b-10c3-426a-8278-929d31200ebf.0.5.1"),sQuery(id+"F0.wireOp",EDGE,"7c84c30b-10c3-426a-8278-929d31200ebf.0.5.2"),sQuery(id+"F0.wireOp",EDGE,"7c84c30b-10c3-426a-8278-929d31200ebf.0.5.3"),sQuery(id+"F0.wireOp",EDGE,"7c84c30b-10c3-426a-8278-929d31200ebf.0.6.0"),sQuery(id+"F0.wireOp",EDGE,"7c84c30b-10c3-426a-8278-929d31200ebf.0.6.1"),sQuery(id+"F0.wireOp",EDGE,"7c84c30b-10c3-426a-8278-929d31200ebf.0.6.2"),sQuery(id+"F0.wireOp",EDGE,"7c84c30b-10c3-426a-8278-929d31200ebf.0.6.3"),sQuery(id+"F0.wireOp",EDGE,"7c84c30b-10c3-426a-8278-929d31200ebf.0.7.0"),sQuery(id+"F0.wireOp",EDGE,"7c84c30b-10c3-426a-8278-929d31200ebf.0.7.1"),sQuery(id+"F0.wireOp",EDGE,"7c84c30b-10c3-426a-8278-929d31200ebf.0.7.2"),sQuery(id+"F0.wireOp",EDGE,"7c84c30b-10c3-426a-8278-929d31200ebf.0.7.3"),sQuery(id+"F0.wireOp",EDGE,"7c84c30b-10c3-426a-8278-929d31200ebf.0.8.0"),sQuery(id+"F0.wireOp",EDGE,"7c84c30b-10c3-426a-8278-929d31200ebf.0.8.1"),sQuery(id+"F0.wireOp",EDGE,"7c84c30b-10c3-426a-8278-929d31200ebf.0.8.2"),sQuery(id+"F0.wireOp",EDGE,"7c84c30b-10c3-426a-8278-929d31200ebf.0.8.3"),sQuery(id+"F0.wireOp",EDGE,"7c84c30b-10c3-426a-8278-929d31200ebf.0.9.0"),sQuery(id+"F0.wireOp",EDGE,"7c84c30b-10c3-426a-8278-929d31200ebf.0.9.1"),sQuery(id+"F0.wireOp",EDGE,"7c84c30b-10c3-426a-8278-929d31200ebf.0.9.2"),sQuery(id+"F0.wireOp",EDGE,"7c84c30b-10c3-426a-8278-929d31200ebf.0.9.3"),sQuery(id+"F0.wireOp",EDGE,"7c84c30b-10c3-426a-8278-929d31200ebf.0.10.0"),sQuery(id+"F0.wireOp",EDGE,"7c84c30b-10c3-426a-8278-929d31200ebf.0.10.1"),sQuery(id+"F0.wireOp",EDGE,"7c84c30b-10c3-426a-8278-929d31200ebf.0.10.2"),sQuery(id+"F0.wireOp",EDGE,"7c84c30b-10c3-426a-8278-929d31200ebf.0.10.3"),sQuery(id+"F0.wireOp",EDGE,"7c84c30b-10c3-426a-8278-929d31200ebf.0.11.0"),sQuery(id+"F0.wireOp",EDGE,"7c84c30b-10c3-426a-8278-929d31200ebf.0.11.1"),sQuery(id+"F0.wireOp",EDGE,"7c84c30b-10c3-426a-8278-929d31200ebf.0.11.2"),sQuery(id+"F0.wireOp",EDGE,"7c84c30b-10c3-426a-8278-929d31200ebf.0.11.3"),sQuery(id+"F0.wireOp",EDGE,"7c84c30b-10c3-426a-8278-929d31200ebf.0.12.0"),sQuery(id+"F0.wireOp",EDGE,"7c84c30b-10c3-426a-8278-929d31200ebf.0.12.1"),sQuery(id+"F0.wireOp",EDGE,"7c84c30b-10c3-426a-8278-929d31200ebf.0.12.2"),sQuery(id+"F0.wireOp",EDGE,"7c84c30b-10c3-426a-8278-929d31200ebf.0.12.3"),sQuery(id+"F0.wireOp",EDGE,"7c84c30b-10c3-426a-8278-929d31200ebf.0.13.0"),sQuery(id+"F0.wireOp",EDGE,"7c84c30b-10c3-426a-8278-929d31200ebf.0.13.1"),sQuery(id+"F0.wireOp",EDGE,"7c84c30b-10c3-426a-8278-929d31200ebf.0.13.2"),sQuery(id+"F0.wireOp",EDGE,"7c84c30b-10c3-426a-8278-929d31200ebf.0.13.3"),sQuery(id+"F0.wireOp",EDGE,"7c84c30b-10c3-426a-8278-929d31200ebf.0.14.0"),sQuery(id+"F0.wireOp",EDGE,"7c84c30b-10c3-426a-8278-929d31200ebf.0.14.1"),sQuery(id+"F0.wireOp",EDGE,"7c84c30b-10c3-426a-8278-929d31200ebf.0.14.2"),sQuery(id+"F0.wireOp",EDGE,"7c84c30b-10c3-426a-8278-929d31200ebf.0.14.3"),sQuery(id+"F0.wireOp",EDGE,"7c84c30b-10c3-426a-8278-929d31200ebf.0.15.0"),sQuery(id+"F0.wireOp",EDGE,"7c84c30b-10c3-426a-8278-929d31200ebf.0.15.1"),sQuery(id+"F0.wireOp",EDGE,"7c84c30b-10c3-426a-8278-929d31200ebf.0.15.2"),sQuery(id+"F0.wireOp",EDGE,"7c84c30b-10c3-426a-8278-929d31200ebf.0.15.3"),sQuery(id+"F0.wireOp",EDGE,"7c84c30b-10c3-426a-8278-929d31200ebf.0.16.0"),sQuery(id+"F0.wireOp",EDGE,"7c84c30b-10c3-426a-8278-929d31200ebf.0.16.1"),sQuery(id+"F0.wireOp",EDGE,"7c84c30b-10c3-426a-8278-929d31200ebf.0.16.2"),sQuery(id+"F0.wireOp",EDGE,"7c84c30b-10c3-426a-8278-929d31200ebf.0.16.3"),sQuery(id+"F0.wireOp",EDGE,"7c84c30b-10c3-426a-8278-929d31200ebf.0.17.0"),sQuery(id+"F0.wireOp",EDGE,"7c84c30b-10c3-426a-8278-929d31200ebf.0.17.1"),sQuery(id+"F0.wireOp",EDGE,"7c84c30b-10c3-426a-8278-929d31200ebf.0.17.2"),sQuery(id+"F0.wireOp",EDGE,"7c84c30b-10c3-426a-8278-929d31200ebf.0.17.3"),sQuery(id+"F0.wireOp",EDGE,"7c84c30b-10c3-426a-8278-929d31200ebf.0.18.0"),sQuery(id+"F0.wireOp",EDGE,"7c84c30b-10c3-426a-8278-929d31200ebf.0.18.1"),sQuery(id+"F0.wireOp",EDGE,"7c84c30b-10c3-426a-8278-929d31200ebf.0.18.2"),sQuery(id+"F0.wireOp",EDGE,"7c84c30b-10c3-426a-8278-929d31200ebf.0.18.3"),sQuery(id+"F0.wireOp",EDGE,"7c84c30b-10c3-426a-8278-929d31200ebf.0.19.0"),sQuery(id+"F0.wireOp",EDGE,"7c84c30b-10c3-426a-8278-929d31200ebf.0.19.1"),sQuery(id+"F0.wireOp",EDGE,"7c84c30b-10c3-426a-8278-929d31200ebf.0.19.2"),sQuery(id+"F0.wireOp",EDGE,"7c84c30b-10c3-426a-8278-929d31200ebf.0.19.3"),sQuery(id+"F0.wireOp",EDGE,"7c84c30b-10c3-426a-8278-929d31200ebf.0.20.0"),sQuery(id+"F0.wireOp",EDGE,"7c84c30b-10c3-426a-8278-929d31200ebf.0.20.1"),sQuery(id+"F0.wireOp",EDGE,"7c84c30b-10c3-426a-8278-929d31200ebf.0.20.2"),sQuery(id+"F0.wireOp",EDGE,"7c84c30b-10c3-426a-8278-929d31200ebf.0.20.3"),sQuery(id+"F0.wireOp",EDGE,"7c84c30b-10c3-426a-8278-929d31200ebf.0.21.0"),sQuery(id+"F0.wireOp",EDGE,"7c84c30b-10c3-426a-8278-929d31200ebf.0.21.1"),sQuery(id+"F0.wireOp",EDGE,"7c84c30b-10c3-426a-8278-929d31200ebf.0.21.2"),sQuery(id+"F0.wireOp",EDGE,"7c84c30b-10c3-426a-8278-929d31200ebf.0.21.3"),sQuery(id+"F0.wireOp",EDGE,"7c84c30b-10c3-426a-8278-929d31200ebf.0.22.0"),sQuery(id+"F0.wireOp",EDGE,"7c84c30b-10c3-426a-8278-929d31200ebf.0.22.1"),sQuery(id+"F0.wireOp",EDGE,"7c84c30b-10c3-426a-8278-929d31200ebf.0.22.2"),sQuery(id+"F0.wireOp",EDGE,"7c84c30b-10c3-426a-8278-929d31200ebf.0.22.3"),sQuery(id+"F0.wireOp",EDGE,"7c84c30b-10c3-426a-8278-929d31200ebf.0.23.0"),sQuery(id+"F0.wireOp",EDGE,"7c84c30b-10c3-426a-8278-929d31200ebf.0.23.1"),sQuery(id+"F0.wireOp",EDGE,"7c84c30b-10c3-426a-8278-929d31200ebf.0.23.2"),sQuery(id+"F0.wireOp",EDGE,"7c84c30b-10c3-426a-8278-929d31200ebf.0.23.3"),sQuery(id+"F0.wireOp",EDGE,"7c84c30b-10c3-426a-8278-929d31200ebf.0.24.0"),sQuery(id+"F0.wireOp",EDGE,"7c84c30b-10c3-426a-8278-929d31200ebf.0.24.1"),sQuery(id+"F0.wireOp",EDGE,"7c84c30b-10c3-426a-8278-929d31200ebf.0.24.2"),sQuery(id+"F0.wireOp",EDGE,"7c84c30b-10c3-426a-8278-929d31200ebf.0.24.3"),sQuery(id+"F0.wireOp",EDGE,"7c84c30b-10c3-426a-8278-929d31200ebf.0.25.0"),sQuery(id+"F0.wireOp",EDGE,"7c84c30b-10c3-426a-8278-929d31200ebf.0.25.1"),sQuery(id+"F0.wireOp",EDGE,"7c84c30b-10c3-426a-8278-929d31200ebf.0.25.2"),sQuery(id+"F0.wireOp",EDGE,"7c84c30b-10c3-426a-8278-929d31200ebf.0.25.3"),sQuery(id+"F0.wireOp",EDGE,"7c84c30b-10c3-426a-8278-929d31200ebf.1.0.0"),sQuery(id+"F0.wireOp",EDGE,"7c84c30b-10c3-426a-8278-929d31200ebf.1.0.1"),sQuery(id+"F0.wireOp",EDGE,"7c84c30b-10c3-426a-8278-929d31200ebf.1.0.2"),sQuery(id+"F0.wireOp",EDGE,"7c84c30b-10c3-426a-8278-929d31200ebf.1.0.3"),sQuery(id+"F0.wireOp",EDGE,"7c84c30b-10c3-426a-8278-929d31200ebf.1.1.0"),sQuery(id+"F0.wireOp",EDGE,"7c84c30b-10c3-426a-8278-929d31200ebf.1.1.1"),sQuery(id+"F0.wireOp",EDGE,"7c84c30b-10c3-426a-8278-929d31200ebf.1.1.2"),sQuery(id+"F0.wireOp",EDGE,"7c84c30b-10c3-426a-8278-929d31200ebf.1.1.3"),sQuery(id+"F0.wireOp",EDGE,"7c84c30b-10c3-426a-8278-929d31200ebf.1.2.0"),sQuery(id+"F0.wireOp",EDGE,"7c84c30b-10c3-426a-8278-929d31200ebf.1.2.1"),sQuery(id+"F0.wireOp",EDGE,"7c84c30b-10c3-426a-8278-929d31200ebf.1.2.2"),sQuery(id+"F0.wireOp",EDGE,"7c84c30b-10c3-426a-8278-929d31200ebf.1.2.3"),sQuery(id+"F0.wireOp",EDGE,"7c84c30b-10c3-426a-8278-929d31200ebf.1.3.0"),sQuery(id+"F0.wireOp",EDGE,"7c84c30b-10c3-426a-8278-929d31200ebf.1.3.1"),sQuery(id+"F0.wireOp",EDGE,"7c84c30b-10c3-426a-8278-929d31200ebf.1.3.2"),sQuery(id+"F0.wireOp",EDGE,"7c84c30b-10c3-426a-8278-929d31200ebf.1.3.3"),sQuery(id+"F0.wireOp",EDGE,"7c84c30b-10c3-426a-8278-929d31200ebf.1.4.0"),sQuery(id+"F0.wireOp",EDGE,"7c84c30b-10c3-426a-8278-929d31200ebf.1.4.1"),sQuery(id+"F0.wireOp",EDGE,"7c84c30b-10c3-426a-8278-929d31200ebf.1.4.2"),sQuery(id+"F0.wireOp",EDGE,"7c84c30b-10c3-426a-8278-929d31200ebf.1.4.3"),sQuery(id+"F0.wireOp",EDGE,"7c84c30b-10c3-426a-8278-929d31200ebf.1.5.0"),sQuery(id+"F0.wireOp",EDGE,"7c84c30b-10c3-426a-8278-929d31200ebf.1.5.1"),sQuery(id+"F0.wireOp",EDGE,"7c84c30b-10c3-426a-8278-929d31200ebf.1.5.2"),sQuery(id+"F0.wireOp",EDGE,"7c84c30b-10c3-426a-8278-929d31200ebf.1.5.3"),sQuery(id+"F0.wireOp",EDGE,"7c84c30b-10c3-426a-8278-929d31200ebf.1.6.0"),sQuery(id+"F0.wireOp",EDGE,"7c84c30b-10c3-426a-8278-929d31200ebf.1.6.1"),sQuery(id+"F0.wireOp",EDGE,"7c84c30b-10c3-426a-8278-929d31200ebf.1.6.2"),sQuery(id+"F0.wireOp",EDGE,"7c84c30b-10c3-426a-8278-929d31200ebf.1.6.3"),sQuery(id+"F0.wireOp",EDGE,"7c84c30b-10c3-426a-8278-929d31200ebf.1.7.0"),sQuery(id+"F0.wireOp",EDGE,"7c84c30b-10c3-426a-8278-929d31200ebf.1.7.1"),sQuery(id+"F0.wireOp",EDGE,"7c84c30b-10c3-426a-8278-929d31200ebf.1.7.2"),sQuery(id+"F0.wireOp",EDGE,"7c84c30b-10c3-426a-8278-929d31200ebf.1.7.3"),sQuery(id+"F0.wireOp",EDGE,"7c84c30b-10c3-426a-8278-929d31200ebf.1.8.0"),sQuery(id+"F0.wireOp",EDGE,"7c84c30b-10c3-426a-8278-929d31200ebf.1.8.1"),sQuery(id+"F0.wireOp",EDGE,"7c84c30b-10c3-426a-8278-929d31200ebf.1.8.2"),sQuery(id+"F0.wireOp",EDGE,"7c84c30b-10c3-426a-8278-929d31200ebf.1.8.3"),sQuery(id+"F0.wireOp",EDGE,"7c84c30b-10c3-426a-8278-929d31200ebf.1.9.0"),sQuery(id+"F0.wireOp",EDGE,"7c84c30b-10c3-426a-8278-929d31200ebf.1.9.1"),sQuery(id+"F0.wireOp",EDGE,"7c84c30b-10c3-426a-8278-929d31200ebf.1.9.2"),sQuery(id+"F0.wireOp",EDGE,"7c84c30b-10c3-426a-8278-929d31200ebf.1.9.3"),sQuery(id+"F0.wireOp",EDGE,"7c84c30b-10c3-426a-8278-929d31200ebf.1.10.0"),sQuery(id+"F0.wireOp",EDGE,"7c84c30b-10c3-426a-8278-929d31200ebf.1.10.1"),sQuery(id+"F0.wireOp",EDGE,"7c84c30b-10c3-426a-8278-929d31200ebf.1.10.2"),sQuery(id+"F0.wireOp",EDGE,"7c84c30b-10c3-426a-8278-929d31200ebf.1.10.3"),sQuery(id+"F0.wireOp",EDGE,"7c84c30b-10c3-426a-8278-929d31200ebf.1.11.0"),sQuery(id+"F0.wireOp",EDGE,"7c84c30b-10c3-426a-8278-929d31200ebf.1.11.1"),sQuery(id+"F0.wireOp",EDGE,"7c84c30b-10c3-426a-8278-929d31200ebf.1.11.2"),sQuery(id+"F0.wireOp",EDGE,"7c84c30b-10c3-426a-8278-929d31200ebf.1.11.3"),sQuery(id+"F0.wireOp",EDGE,"7c84c30b-10c3-426a-8278-929d31200ebf.1.12.0"),sQuery(id+"F0.wireOp",EDGE,"7c84c30b-10c3-426a-8278-929d31200ebf.1.12.1"),sQuery(id+"F0.wireOp",EDGE,"7c84c30b-10c3-426a-8278-929d31200ebf.1.12.2"),sQuery(id+"F0.wireOp",EDGE,"7c84c30b-10c3-426a-8278-929d31200ebf.1.12.3"),sQuery(id+"F0.wireOp",EDGE,"7c84c30b-10c3-426a-8278-929d31200ebf.1.13.0"),sQuery(id+"F0.wireOp",EDGE,"7c84c30b-10c3-426a-8278-929d31200ebf.1.13.1"),sQuery(id+"F0.wireOp",EDGE,"7c84c30b-10c3-426a-8278-929d31200ebf.1.13.2"),sQuery(id+"F0.wireOp",EDGE,"7c84c30b-10c3-426a-8278-929d31200ebf.1.13.3"),sQuery(id+"F0.wireOp",EDGE,"7c84c30b-10c3-426a-8278-929d31200ebf.1.14.0"),sQuery(id+"F0.wireOp",EDGE,"7c84c30b-10c3-426a-8278-929d31200ebf.1.14.1"),sQuery(id+"F0.wireOp",EDGE,"7c84c30b-10c3-426a-8278-929d31200ebf.1.14.2"),sQuery(id+"F0.wireOp",EDGE,"7c84c30b-10c3-426a-8278-929d31200ebf.1.14.3"),sQuery(id+"F0.wireOp",EDGE,"7c84c30b-10c3-426a-8278-929d31200ebf.1.15.0"),sQuery(id+"F0.wireOp",EDGE,"7c84c30b-10c3-426a-8278-929d31200ebf.1.15.1"),sQuery(id+"F0.wireOp",EDGE,"7c84c30b-10c3-426a-8278-929d31200ebf.1.15.2"),sQuery(id+"F0.wireOp",EDGE,"7c84c30b-10c3-426a-8278-929d31200ebf.1.15.3"),sQuery(id+"F0.wireOp",EDGE,"7c84c30b-10c3-426a-8278-929d31200ebf.1.16.0"),sQuery(id+"F0.wireOp",EDGE,"7c84c30b-10c3-426a-8278-929d31200ebf.1.16.1"),sQuery(id+"F0.wireOp",EDGE,"7c84c30b-10c3-426a-8278-929d31200ebf.1.16.2"),sQuery(id+"F0.wireOp",EDGE,"7c84c30b-10c3-426a-8278-929d31200ebf.1.16.3"),sQuery(id+"F0.wireOp",EDGE,"7c84c30b-10c3-426a-8278-929d31200ebf.1.17.0"),sQuery(id+"F0.wireOp",EDGE,"7c84c30b-10c3-426a-8278-929d31200ebf.1.17.1"),sQuery(id+"F0.wireOp",EDGE,"7c84c30b-10c3-426a-8278-929d31200ebf.1.17.2"),sQuery(id+"F0.wireOp",EDGE,"7c84c30b-10c3-426a-8278-929d31200ebf.1.17.3"),sQuery(id+"F0.wireOp",EDGE,"7c84c30b-10c3-426a-8278-929d31200ebf.1.18.0"),sQuery(id+"F0.wireOp",EDGE,"7c84c30b-10c3-426a-8278-929d31200ebf.1.18.1"),sQuery(id+"F0.wireOp",EDGE,"7c84c30b-10c3-426a-8278-929d31200ebf.1.18.2"),sQuery(id+"F0.wireOp",EDGE,"7c84c30b-10c3-426a-8278-929d31200ebf.1.18.3"),sQuery(id+"F0.wireOp",EDGE,"7c84c30b-10c3-426a-8278-929d31200ebf.1.19.0"),sQuery(id+"F0.wireOp",EDGE,"7c84c30b-10c3-426a-8278-929d31200ebf.1.19.1"),sQuery(id+"F0.wireOp",EDGE,"7c84c30b-10c3-426a-8278-929d31200ebf.1.19.2"),sQuery(id+"F0.wireOp",EDGE,"7c84c30b-10c3-426a-8278-929d31200ebf.1.19.3"),sQuery(id+"F0.wireOp",EDGE,"7c84c30b-10c3-426a-8278-929d31200ebf.1.20.0"),sQuery(id+"F0.wireOp",EDGE,"7c84c30b-10c3-426a-8278-929d31200ebf.1.20.1"),sQuery(id+"F0.wireOp",EDGE,"7c84c30b-10c3-426a-8278-929d31200ebf.1.20.2"),sQuery(id+"F0.wireOp",EDGE,"7c84c30b-10c3-426a-8278-929d31200ebf.1.20.3"),sQuery(id+"F0.wireOp",EDGE,"7c84c30b-10c3-426a-8278-929d31200ebf.1.21.0"),sQuery(id+"F0.wireOp",EDGE,"7c84c30b-10c3-426a-8278-929d31200ebf.1.21.1"),sQuery(id+"F0.wireOp",EDGE,"7c84c30b-10c3-426a-8278-929d31200ebf.1.21.2"),sQuery(id+"F0.wireOp",EDGE,"7c84c30b-10c3-426a-8278-929d31200ebf.1.21.3"),sQuery(id+"F0.wireOp",EDGE,"7c84c30b-10c3-426a-8278-929d31200ebf.1.22.0"),sQuery(id+"F0.wireOp",EDGE,"7c84c30b-10c3-426a-8278-929d31200ebf.1.22.1"),sQuery(id+"F0.wireOp",EDGE,"7c84c30b-10c3-426a-8278-929d31200ebf.1.22.2"),sQuery(id+"F0.wireOp",EDGE,"7c84c30b-10c3-426a-8278-929d31200ebf.1.22.3"),sQuery(id+"F0.wireOp",EDGE,"7c84c30b-10c3-426a-8278-929d31200ebf.1.23.0"),sQuery(id+"F0.wireOp",EDGE,"7c84c30b-10c3-426a-8278-929d31200ebf.1.23.1"),sQuery(id+"F0.wireOp",EDGE,"7c84c30b-10c3-426a-8278-929d31200ebf.1.23.2"),sQuery(id+"F0.wireOp",EDGE,"7c84c30b-10c3-426a-8278-929d31200ebf.1.23.3"),sQuery(id+"F0.wireOp",EDGE,"7c84c30b-10c3-426a-8278-929d31200ebf.1.24.0"),sQuery(id+"F0.wireOp",EDGE,"7c84c30b-10c3-426a-8278-929d31200ebf.1.24.1"),sQuery(id+"F0.wireOp",EDGE,"7c84c30b-10c3-426a-8278-929d31200ebf.1.24.2"),sQuery(id+"F0.wireOp",EDGE,"7c84c30b-10c3-426a-8278-929d31200ebf.1.24.3"),sQuery(id+"F0.wireOp",EDGE,"7c84c30b-10c3-426a-8278-929d31200ebf.1.25.0"),sQuery(id+"F0.wireOp",EDGE,"7c84c30b-10c3-426a-8278-929d31200ebf.1.25.1"),sQuery(id+"F0.wireOp",EDGE,"7c84c30b-10c3-426a-8278-929d31200ebf.1.25.2"),sQuery(id+"F0.wireOp",EDGE,"7c84c30b-10c3-426a-8278-929d31200ebf.1.25.3"),sQuery(id+"F0.wireOp",EDGE,"7c84c30b-10c3-426a-8278-929d31200ebf.2.0.0"),sQuery(id+"F0.wireOp",EDGE,"7c84c30b-10c3-426a-8278-929d31200ebf.2.0.1"),sQuery(id+"F0.wireOp",EDGE,"7c84c30b-10c3-426a-8278-929d31200ebf.2.0.2"),sQuery(id+"F0.wireOp",EDGE,"7c84c30b-10c3-426a-8278-929d31200ebf.2.0.3"),sQuery(id+"F0.wireOp",EDGE,"7c84c30b-10c3-426a-8278-929d31200ebf.2.1.0"),sQuery(id+"F0.wireOp",EDGE,"7c84c30b-10c3-426a-8278-929d31200ebf.2.1.1"),sQuery(id+"F0.wireOp",EDGE,"7c84c30b-10c3-426a-8278-929d31200ebf.2.1.2"),sQuery(id+"F0.wireOp",EDGE,"7c84c30b-10c3-426a-8278-929d31200ebf.2.1.3"),sQuery(id+"F0.wireOp",EDGE,"7c84c30b-10c3-426a-8278-929d31200ebf.2.2.0"),sQuery(id+"F0.wireOp",EDGE,"7c84c30b-10c3-426a-8278-929d31200ebf.2.2.1"),sQuery(id+"F0.wireOp",EDGE,"7c84c30b-10c3-426a-8278-929d31200ebf.2.2.2"),sQuery(id+"F0.wireOp",EDGE,"7c84c30b-10c3-426a-8278-929d31200ebf.2.2.3"),sQuery(id+"F0.wireOp",EDGE,"7c84c30b-10c3-426a-8278-929d31200ebf.2.3.0"),sQuery(id+"F0.wireOp",EDGE,"7c84c30b-10c3-426a-8278-929d31200ebf.2.3.1"),sQuery(id+"F0.wireOp",EDGE,"7c84c30b-10c3-426a-8278-929d31200ebf.2.3.2"),sQuery(id+"F0.wireOp",EDGE,"7c84c30b-10c3-426a-8278-929d31200ebf.2.3.3"),sQuery(id+"F0.wireOp",EDGE,"7c84c30b-10c3-426a-8278-929d31200ebf.2.4.0"),sQuery(id+"F0.wireOp",EDGE,"7c84c30b-10c3-426a-8278-929d31200ebf.2.4.1"),sQuery(id+"F0.wireOp",EDGE,"7c84c30b-10c3-426a-8278-929d31200ebf.2.4.2"),sQuery(id+"F0.wireOp",EDGE,"7c84c30b-10c3-426a-8278-929d31200ebf.2.4.3"),sQuery(id+"F0.wireOp",EDGE,"7c84c30b-10c3-426a-8278-929d31200ebf.2.5.0"),sQuery(id+"F0.wireOp",EDGE,"7c84c30b-10c3-426a-8278-929d31200ebf.2.5.1"),sQuery(id+"F0.wireOp",EDGE,"7c84c30b-10c3-426a-8278-929d31200ebf.2.5.2"),sQuery(id+"F0.wireOp",EDGE,"7c84c30b-10c3-426a-8278-929d31200ebf.2.5.3"),sQuery(id+"F0.wireOp",EDGE,"7c84c30b-10c3-426a-8278-929d31200ebf.2.6.0"),sQuery(id+"F0.wireOp",EDGE,"7c84c30b-10c3-426a-8278-929d31200ebf.2.6.1"),sQuery(id+"F0.wireOp",EDGE,"7c84c30b-10c3-426a-8278-929d31200ebf.2.6.2"),sQuery(id+"F0.wireOp",EDGE,"7c84c30b-10c3-426a-8278-929d31200ebf.2.6.3"),sQuery(id+"F0.wireOp",EDGE,"7c84c30b-10c3-426a-8278-929d31200ebf.2.7.0"),sQuery(id+"F0.wireOp",EDGE,"7c84c30b-10c3-426a-8278-929d31200ebf.2.7.1"),sQuery(id+"F0.wireOp",EDGE,"7c84c30b-10c3-426a-8278-929d31200ebf.2.7.2"),sQuery(id+"F0.wireOp",EDGE,"7c84c30b-10c3-426a-8278-929d31200ebf.2.7.3"),sQuery(id+"F0.wireOp",EDGE,"7c84c30b-10c3-426a-8278-929d31200ebf.2.8.0"),sQuery(id+"F0.wireOp",EDGE,"7c84c30b-10c3-426a-8278-929d31200ebf.2.8.1"),sQuery(id+"F0.wireOp",EDGE,"7c84c30b-10c3-426a-8278-929d31200ebf.2.8.2"),sQuery(id+"F0.wireOp",EDGE,"7c84c30b-10c3-426a-8278-929d31200ebf.2.8.3"),sQuery(id+"F0.wireOp",EDGE,"7c84c30b-10c3-426a-8278-929d31200ebf.2.9.0"),sQuery(id+"F0.wireOp",EDGE,"7c84c30b-10c3-426a-8278-929d31200ebf.2.9.1"),sQuery(id+"F0.wireOp",EDGE,"7c84c30b-10c3-426a-8278-929d31200ebf.2.9.2"),sQuery(id+"F0.wireOp",EDGE,"7c84c30b-10c3-426a-8278-929d31200ebf.2.9.3"),sQuery(id+"F0.wireOp",EDGE,"7c84c30b-10c3-426a-8278-929d31200ebf.2.10.0"),sQuery(id+"F0.wireOp",EDGE,"7c84c30b-10c3-426a-8278-929d31200ebf.2.10.1"),sQuery(id+"F0.wireOp",EDGE,"7c84c30b-10c3-426a-8278-929d31200ebf.2.10.2"),sQuery(id+"F0.wireOp",EDGE,"7c84c30b-10c3-426a-8278-929d31200ebf.2.10.3"),sQuery(id+"F0.wireOp",EDGE,"7c84c30b-10c3-426a-8278-929d31200ebf.2.11.0"),sQuery(id+"F0.wireOp",EDGE,"7c84c30b-10c3-426a-8278-929d31200ebf.2.11.1"),sQuery(id+"F0.wireOp",EDGE,"7c84c30b-10c3-426a-8278-929d31200ebf.2.11.2"),sQuery(id+"F0.wireOp",EDGE,"7c84c30b-10c3-426a-8278-929d31200ebf.2.11.3"),sQuery(id+"F0.wireOp",EDGE,"7c84c30b-10c3-426a-8278-929d31200ebf.2.12.0"),sQuery(id+"F0.wireOp",EDGE,"7c84c30b-10c3-426a-8278-929d31200ebf.2.12.1"),sQuery(id+"F0.wireOp",EDGE,"7c84c30b-10c3-426a-8278-929d31200ebf.2.12.2"),sQuery(id+"F0.wireOp",EDGE,"7c84c30b-10c3-426a-8278-929d31200ebf.2.12.3"),sQuery(id+"F0.wireOp",EDGE,"7c84c30b-10c3-426a-8278-929d31200ebf.2.13.0"),sQuery(id+"F0.wireOp",EDGE,"7c84c30b-10c3-426a-8278-929d31200ebf.2.13.1"),sQuery(id+"F0.wireOp",EDGE,"7c84c30b-10c3-426a-8278-929d31200ebf.2.13.2"),sQuery(id+"F0.wireOp",EDGE,"7c84c30b-10c3-426a-8278-929d31200ebf.2.13.3"),sQuery(id+"F0.wireOp",EDGE,"7c84c30b-10c3-426a-8278-929d31200ebf.2.14.0"),sQuery(id+"F0.wireOp",EDGE,"7c84c30b-10c3-426a-8278-929d31200ebf.2.14.1"),sQuery(id+"F0.wireOp",EDGE,"7c84c30b-10c3-426a-8278-929d31200ebf.2.14.2"),sQuery(id+"F0.wireOp",EDGE,"7c84c30b-10c3-426a-8278-929d31200ebf.2.14.3"),sQuery(id+"F0.wireOp",EDGE,"7c84c30b-10c3-426a-8278-929d31200ebf.2.15.0"),sQuery(id+"F0.wireOp",EDGE,"7c84c30b-10c3-426a-8278-929d31200ebf.2.15.1"),sQuery(id+"F0.wireOp",EDGE,"7c84c30b-10c3-426a-8278-929d31200ebf.2.15.2"),sQuery(id+"F0.wireOp",EDGE,"7c84c30b-10c3-426a-8278-929d31200ebf.2.15.3"),sQuery(id+"F0.wireOp",EDGE,"7c84c30b-10c3-426a-8278-929d31200ebf.2.16.0"),sQuery(id+"F0.wireOp",EDGE,"7c84c30b-10c3-426a-8278-929d31200ebf.2.16.1"),sQuery(id+"F0.wireOp",EDGE,"7c84c30b-10c3-426a-8278-929d31200ebf.2.16.2"),sQuery(id+"F0.wireOp",EDGE,"7c84c30b-10c3-426a-8278-929d31200ebf.2.16.3"),sQuery(id+"F0.wireOp",EDGE,"7c84c30b-10c3-426a-8278-929d31200ebf.2.17.0"),sQuery(id+"F0.wireOp",EDGE,"7c84c30b-10c3-426a-8278-929d31200ebf.2.17.1"),sQuery(id+"F0.wireOp",EDGE,"7c84c30b-10c3-426a-8278-929d31200ebf.2.17.2"),sQuery(id+"F0.wireOp",EDGE,"7c84c30b-10c3-426a-8278-929d31200ebf.2.17.3"),sQuery(id+"F0.wireOp",EDGE,"7c84c30b-10c3-426a-8278-929d31200ebf.2.18.0"),sQuery(id+"F0.wireOp",EDGE,"7c84c30b-10c3-426a-8278-929d31200ebf.2.18.1"),sQuery(id+"F0.wireOp",EDGE,"7c84c30b-10c3-426a-8278-929d31200ebf.2.18.2"),sQuery(id+"F0.wireOp",EDGE,"7c84c30b-10c3-426a-8278-929d31200ebf.2.18.3"),sQuery(id+"F0.wireOp",EDGE,"7c84c30b-10c3-426a-8278-929d31200ebf.2.19.0"),sQuery(id+"F0.wireOp",EDGE,"7c84c30b-10c3-426a-8278-929d31200ebf.2.19.1"),sQuery(id+"F0.wireOp",EDGE,"7c84c30b-10c3-426a-8278-929d31200ebf.2.19.2"),sQuery(id+"F0.wireOp",EDGE,"7c84c30b-10c3-426a-8278-929d31200ebf.2.19.3"),sQuery(id+"F0.wireOp",EDGE,"7c84c30b-10c3-426a-8278-929d31200ebf.2.20.0"),sQuery(id+"F0.wireOp",EDGE,"7c84c30b-10c3-426a-8278-929d31200ebf.2.20.1"),sQuery(id+"F0.wireOp",EDGE,"7c84c30b-10c3-426a-8278-929d31200ebf.2.20.2"),sQuery(id+"F0.wireOp",EDGE,"7c84c30b-10c3-426a-8278-929d31200ebf.2.20.3"),sQuery(id+"F0.wireOp",EDGE,"7c84c30b-10c3-426a-8278-929d31200ebf.2.21.0"),sQuery(id+"F0.wireOp",EDGE,"7c84c30b-10c3-426a-8278-929d31200ebf.2.21.1"),sQuery(id+"F0.wireOp",EDGE,"7c84c30b-10c3-426a-8278-929d31200ebf.2.21.2"),sQuery(id+"F0.wireOp",EDGE,"7c84c30b-10c3-426a-8278-929d31200ebf.2.21.3"),sQuery(id+"F0.wireOp",EDGE,"7c84c30b-10c3-426a-8278-929d31200ebf.2.22.0"),sQuery(id+"F0.wireOp",EDGE,"7c84c30b-10c3-426a-8278-929d31200ebf.2.22.1"),sQuery(id+"F0.wireOp",EDGE,"7c84c30b-10c3-426a-8278-929d31200ebf.2.22.2"),sQuery(id+"F0.wireOp",EDGE,"7c84c30b-10c3-426a-8278-929d31200ebf.2.22.3"),sQuery(id+"F0.wireOp",EDGE,"7c84c30b-10c3-426a-8278-929d31200ebf.2.23.0"),sQuery(id+"F0.wireOp",EDGE,"7c84c30b-10c3-426a-8278-929d31200ebf.2.23.1"),sQuery(id+"F0.wireOp",EDGE,"7c84c30b-10c3-426a-8278-929d31200ebf.2.23.2"),sQuery(id+"F0.wireOp",EDGE,"7c84c30b-10c3-426a-8278-929d31200ebf.2.23.3"),sQuery(id+"F0.wireOp",EDGE,"7c84c30b-10c3-426a-8278-929d31200ebf.2.24.0"),sQuery(id+"F0.wireOp",EDGE,"7c84c30b-10c3-426a-8278-929d31200ebf.2.24.1"),sQuery(id+"F0.wireOp",EDGE,"7c84c30b-10c3-426a-8278-929d31200ebf.2.24.2"),sQuery(id+"F0.wireOp",EDGE,"7c84c30b-10c3-426a-8278-929d31200ebf.2.24.3"),sQuery(id+"F0.wireOp",EDGE,"7c84c30b-10c3-426a-8278-929d31200ebf.2.25.0"),sQuery(id+"F0.wireOp",EDGE,"7c84c30b-10c3-426a-8278-929d31200ebf.2.25.1"),sQuery(id+"F0.wireOp",EDGE,"7c84c30b-10c3-426a-8278-929d31200ebf.2.25.2"),sQuery(id+"F0.wireOp",EDGE,"7c84c30b-10c3-426a-8278-929d31200ebf.2.25.3"),sQuery(id+"F0.wireOp",EDGE,"DqMKkSLq-MZEV-FMmD-DK04-qPwwkAkBIbn5"),sQuery(id+"F0.wireOp",EDGE,"b6izAig9-YVkh-wso9-hAal-lVyQwPKH0Rqq"),sQuery(id+"F0.wireOp",EDGE,"Ld8sGsMe-wxKW-HELd-rUX3-tJrgnMnEQjee"),sQuery(id+"F0.wireOp",EDGE,"KcqUpT09-MFPH-TNWY-efLy-ihoS9jBIaYSA"),sQuery(id+"F0.wireOp",EDGE,"E0.0.1.1"),sQuery(id+"F0.wireOp",EDGE,"E0.0.1.2"),sQuery(id+"F0.wireOp",EDGE,"E0.0.1.3"),sQuery(id+"F0.wireOp",EDGE,"E0.0.2.0"),sQuery(id+"F0.wireOp",EDGE,"E0.0.2.1"),sQuery(id+"F0.wireOp",EDGE,"E0.0.2.2"),sQuery(id+"F0.wireOp",EDGE,"E0.0.2.3"),sQuery(id+"F0.wireOp",EDGE,"E0.0.3.0"),sQuery(id+"F0.wireOp",EDGE,"E0.0.3.1"),sQuery(id+"F0.wireOp",EDGE,"E0.0.3.2"),sQuery(id+"F0.wireOp",EDGE,"E0.0.3.3"),sQuery(id+"F0.wireOp",EDGE,"E0.0.4.0"),sQuery(id+"F0.wireOp",EDGE,"E0.0.4.1"),sQuery(id+"F0.wireOp",EDGE,"E0.0.4.2"),sQuery(id+"F0.wireOp",EDGE,"E0.0.4.3"),sQuery(id+"F0.wireOp",EDGE,"E0.0.5.0"),sQuery(id+"F0.wireOp",EDGE,"E0.0.5.1"),sQuery(id+"F0.wireOp",EDGE,"E0.0.5.2"),sQuery(id+"F0.wireOp",EDGE,"E0.0.5.3"),sQuery(id+"F0.wireOp",EDGE,"E0.0.6.0"),sQuery(id+"F0.wireOp",EDGE,"E0.0.6.1"),sQuery(id+"F0.wireOp",EDGE,"E0.0.6.2"),sQuery(id+"F0.wireOp",EDGE,"E0.0.6.3"),sQuery(id+"F0.wireOp",EDGE,"E0.0.7.0"),sQuery(id+"F0.wireOp",EDGE,"E0.0.7.1"),sQuery(id+"F0.wireOp",EDGE,"E0.0.7.2"),sQuery(id+"F0.wireOp",EDGE,"E0.0.7.3"),sQuery(id+"F0.wireOp",EDGE,"E0.0.8.0"),sQuery(id+"F0.wireOp",EDGE,"E0.0.8.1"),sQuery(id+"F0.wireOp",EDGE,"E0.0.8.2"),sQuery(id+"F0.wireOp",EDGE,"E0.0.8.3"),sQuery(id+"F0.wireOp",EDGE,"E0.0.9.0"),sQuery(id+"F0.wireOp",EDGE,"E0.0.9.1"),sQuery(id+"F0.wireOp",EDGE,"E0.0.9.2"),sQuery(id+"F0.wireOp",EDGE,"E0.0.9.3"),sQuery(id+"F0.wireOp",EDGE,"E0.0.10.0"),sQuery(id+"F0.wireOp",EDGE,"E0.0.10.1"),sQuery(id+"F0.wireOp",EDGE,"E0.0.10.2"),sQuery(id+"F0.wireOp",EDGE,"E0.0.10.3"),sQuery(id+"F0.wireOp",EDGE,"E0.0.11.0"),sQuery(id+"F0.wireOp",EDGE,"E0.0.11.1"),sQuery(id+"F0.wireOp",EDGE,"E0.0.11.2"),sQuery(id+"F0.wireOp",EDGE,"E0.0.11.3"),sQuery(id+"F0.wireOp",EDGE,"E0.0.12.0"),sQuery(id+"F0.wireOp",EDGE,"E0.0.12.1"),sQuery(id+"F0.wireOp",EDGE,"E0.0.12.2"),sQuery(id+"F0.wireOp",EDGE,"E0.0.12.3"),sQuery(id+"F0.wireOp",EDGE,"E0.0.13.0"),sQuery(id+"F0.wireOp",EDGE,"E0.0.13.1"),sQuery(id+"F0.wireOp",EDGE,"E0.0.13.2"),sQuery(id+"F0.wireOp",EDGE,"E0.0.13.3"),sQuery(id+"F0.wireOp",EDGE,"E0.0.14.0"),sQuery(id+"F0.wireOp",EDGE,"E0.0.14.1"),sQuery(id+"F0.wireOp",EDGE,"E0.0.14.2"),sQuery(id+"F0.wireOp",EDGE,"E0.0.14.3"),sQuery(id+"F0.wireOp",EDGE,"E0.0.15.0"),sQuery(id+"F0.wireOp",EDGE,"E0.0.15.1"),sQuery(id+"F0.wireOp",EDGE,"E0.0.15.2"),sQuery(id+"F0.wireOp",EDGE,"E0.0.15.3"),sQuery(id+"F0.wireOp",EDGE,"E0.0.16.0"),sQuery(id+"F0.wireOp",EDGE,"E0.0.16.1"),sQuery(id+"F0.wireOp",EDGE,"E0.0.16.2"),sQuery(id+"F0.wireOp",EDGE,"E0.0.16.3"),sQuery(id+"F0.wireOp",EDGE,"E0.0.17.0"),sQuery(id+"F0.wireOp",EDGE,"E0.0.17.1"),sQuery(id+"F0.wireOp",EDGE,"E0.0.17.2"),sQuery(id+"F0.wireOp",EDGE,"E0.0.17.3"),sQuery(id+"F0.wireOp",EDGE,"E0.0.18.0"),sQuery(id+"F0.wireOp",EDGE,"E0.0.18.1"),sQuery(id+"F0.wireOp",EDGE,"E0.0.18.2"),sQuery(id+"F0.wireOp",EDGE,"E0.0.18.3"),sQuery(id+"F0.wireOp",EDGE,"E0.0.19.0"),sQuery(id+"F0.wireOp",EDGE,"E0.0.19.1"),sQuery(id+"F0.wireOp",EDGE,"E0.0.19.2"),sQuery(id+"F0.wireOp",EDGE,"E0.0.19.3"),sQuery(id+"F0.wireOp",EDGE,"E0.0.20.0"),sQuery(id+"F0.wireOp",EDGE,"E0.0.20.1"),sQuery(id+"F0.wireOp",EDGE,"E0.0.20.2"),sQuery(id+"F0.wireOp",EDGE,"E0.0.20.3"),sQuery(id+"F0.wireOp",EDGE,"E0.0.21.0"),sQuery(id+"F0.wireOp",EDGE,"E0.0.21.1"),sQuery(id+"F0.wireOp",EDGE,"E0.0.21.2"),sQuery(id+"F0.wireOp",EDGE,"E0.0.21.3"),sQuery(id+"F0.wireOp",EDGE,"E0.0.22.0"),sQuery(id+"F0.wireOp",EDGE,"E0.0.22.1"),sQuery(id+"F0.wireOp",EDGE,"E0.0.22.2"),sQuery(id+"F0.wireOp",EDGE,"E0.0.22.3"),sQuery(id+"F0.wireOp",EDGE,"E0.0.23.0"),sQuery(id+"F0.wireOp",EDGE,"E0.0.23.1"),sQuery(id+"F0.wireOp",EDGE,"E0.0.23.2"),sQuery(id+"F0.wireOp",EDGE,"E0.0.23.3"),sQuery(id+"F0.wireOp",EDGE,"E0.0.24.0"),sQuery(id+"F0.wireOp",EDGE,"E0.0.24.1"),sQuery(id+"F0.wireOp",EDGE,"E0.0.24.2"),sQuery(id+"F0.wireOp",EDGE,"E0.0.24.3"),sQuery(id+"F0.wireOp",EDGE,"E0.0.25.0"),sQuery(id+"F0.wireOp",EDGE,"E0.0.25.1"),sQuery(id+"F0.wireOp",EDGE,"E0.0.25.2"),sQuery(id+"F0.wireOp",EDGE,"E0.0.25.3"),sQuery(id+"F0.wireOp",EDGE,"E0.1.0.0"),sQuery(id+"F0.wireOp",EDGE,"E0.1.0.1"),sQuery(id+"F0.wireOp",EDGE,"E0.1.0.2"),sQuery(id+"F0.wireOp",EDGE,"E0.1.0.3"),sQuery(id+"F0.wireOp",EDGE,"E0.1.1.0"),sQuery(id+"F0.wireOp",EDGE,"E0.1.1.1"),sQuery(id+"F0.wireOp",EDGE,"E0.1.1.2"),sQuery(id+"F0.wireOp",EDGE,"E0.1.1.3"),sQuery(id+"F0.wireOp",EDGE,"E0.1.2.0"),sQuery(id+"F0.wireOp",EDGE,"E0.1.2.1"),sQuery(id+"F0.wireOp",EDGE,"E0.1.2.2"),sQuery(id+"F0.wireOp",EDGE,"E0.1.2.3"),sQuery(id+"F0.wireOp",EDGE,"E0.1.3.0"),sQuery(id+"F0.wireOp",EDGE,"E0.1.3.1"),sQuery(id+"F0.wireOp",EDGE,"E0.1.3.2"),sQuery(id+"F0.wireOp",EDGE,"E0.1.3.3"),sQuery(id+"F0.wireOp",EDGE,"E0.1.4.0"),sQuery(id+"F0.wireOp",EDGE,"E0.1.4.1"),sQuery(id+"F0.wireOp",EDGE,"E0.1.4.2"),sQuery(id+"F0.wireOp",EDGE,"E0.1.4.3"),sQuery(id+"F0.wireOp",EDGE,"E0.1.5.0"),sQuery(id+"F0.wireOp",EDGE,"E0.1.5.1"),sQuery(id+"F0.wireOp",EDGE,"E0.1.5.2"),sQuery(id+"F0.wireOp",EDGE,"E0.1.5.3"),sQuery(id+"F0.wireOp",EDGE,"E0.1.6.0"),sQuery(id+"F0.wireOp",EDGE,"E0.1.6.1"),sQuery(id+"F0.wireOp",EDGE,"E0.1.6.2"),sQuery(id+"F0.wireOp",EDGE,"E0.1.6.3"),sQuery(id+"F0.wireOp",EDGE,"E0.1.7.0"),sQuery(id+"F0.wireOp",EDGE,"E0.1.7.1"),sQuery(id+"F0.wireOp",EDGE,"E0.1.7.2"),sQuery(id+"F0.wireOp",EDGE,"E0.1.7.3"),sQuery(id+"F0.wireOp",EDGE,"E0.1.8.0"),sQuery(id+"F0.wireOp",EDGE,"E0.1.8.1"),sQuery(id+"F0.wireOp",EDGE,"E0.1.8.2"),sQuery(id+"F0.wireOp",EDGE,"E0.1.8.3"),sQuery(id+"F0.wireOp",EDGE,"E0.1.9.0"),sQuery(id+"F0.wireOp",EDGE,"E0.1.9.1"),sQuery(id+"F0.wireOp",EDGE,"E0.1.9.2"),sQuery(id+"F0.wireOp",EDGE,"E0.1.9.3"),sQuery(id+"F0.wireOp",EDGE,"E0.1.10.0"),sQuery(id+"F0.wireOp",EDGE,"E0.1.10.1"),sQuery(id+"F0.wireOp",EDGE,"E0.1.10.2"),sQuery(id+"F0.wireOp",EDGE,"E0.1.10.3"),sQuery(id+"F0.wireOp",EDGE,"E0.1.11.0"),sQuery(id+"F0.wireOp",EDGE,"E0.1.11.1"),sQuery(id+"F0.wireOp",EDGE,"E0.1.11.2"),sQuery(id+"F0.wireOp",EDGE,"E0.1.11.3"),sQuery(id+"F0.wireOp",EDGE,"E0.1.12.0"),sQuery(id+"F0.wireOp",EDGE,"E0.1.12.1"),sQuery(id+"F0.wireOp",EDGE,"E0.1.12.2"),sQuery(id+"F0.wireOp",EDGE,"E0.1.12.3"),sQuery(id+"F0.wireOp",EDGE,"E0.1.13.0"),sQuery(id+"F0.wireOp",EDGE,"E0.1.13.1"),sQuery(id+"F0.wireOp",EDGE,"E0.1.13.2"),sQuery(id+"F0.wireOp",EDGE,"E0.1.13.3"),sQuery(id+"F0.wireOp",EDGE,"E0.1.14.0"),sQuery(id+"F0.wireOp",EDGE,"E0.1.14.1"),sQuery(id+"F0.wireOp",EDGE,"E0.1.14.2"),sQuery(id+"F0.wireOp",EDGE,"E0.1.14.3"),sQuery(id+"F0.wireOp",EDGE,"E0.1.15.0"),sQuery(id+"F0.wireOp",EDGE,"E0.1.15.1"),sQuery(id+"F0.wireOp",EDGE,"E0.1.15.2"),sQuery(id+"F0.wireOp",EDGE,"E0.1.15.3"),sQuery(id+"F0.wireOp",EDGE,"E0.1.16.0"),sQuery(id+"F0.wireOp",EDGE,"E0.1.16.1"),sQuery(id+"F0.wireOp",EDGE,"E0.1.16.2"),sQuery(id+"F0.wireOp",EDGE,"E0.1.16.3"),sQuery(id+"F0.wireOp",EDGE,"E0.1.17.0"),sQuery(id+"F0.wireOp",EDGE,"E0.1.17.1"),sQuery(id+"F0.wireOp",EDGE,"E0.1.17.2"),sQuery(id+"F0.wireOp",EDGE,"E0.1.17.3"),sQuery(id+"F0.wireOp",EDGE,"E0.1.18.0"),sQuery(id+"F0.wireOp",EDGE,"E0.1.18.1"),sQuery(id+"F0.wireOp",EDGE,"E0.1.18.2"),sQuery(id+"F0.wireOp",EDGE,"E0.1.18.3"),sQuery(id+"F0.wireOp",EDGE,"E0.1.19.0"),sQuery(id+"F0.wireOp",EDGE,"E0.1.19.1"),sQuery(id+"F0.wireOp",EDGE,"E0.1.19.2"),sQuery(id+"F0.wireOp",EDGE,"E0.1.19.3"),sQuery(id+"F0.wireOp",EDGE,"E0.1.20.0"),sQuery(id+"F0.wireOp",EDGE,"E0.1.20.1"),sQuery(id+"F0.wireOp",EDGE,"E0.1.20.2"),sQuery(id+"F0.wireOp",EDGE,"E0.1.20.3"),sQuery(id+"F0.wireOp",EDGE,"E0.1.21.0"),sQuery(id+"F0.wireOp",EDGE,"E0.1.21.1"),sQuery(id+"F0.wireOp",EDGE,"E0.1.21.2"),sQuery(id+"F0.wireOp",EDGE,"E0.1.21.3"),sQuery(id+"F0.wireOp",EDGE,"E0.1.22.0"),sQuery(id+"F0.wireOp",EDGE,"E0.1.22.1"),sQuery(id+"F0.wireOp",EDGE,"E0.1.22.2"),sQuery(id+"F0.wireOp",EDGE,"E0.1.22.3"),sQuery(id+"F0.wireOp",EDGE,"E0.1.23.0"),sQuery(id+"F0.wireOp",EDGE,"E0.1.23.1"),sQuery(id+"F0.wireOp",EDGE,"E0.1.23.2"),sQuery(id+"F0.wireOp",EDGE,"E0.1.23.3"),sQuery(id+"F0.wireOp",EDGE,"E0.1.24.0"),sQuery(id+"F0.wireOp",EDGE,"E0.1.24.1"),sQuery(id+"F0.wireOp",EDGE,"E0.1.24.2"),sQuery(id+"F0.wireOp",EDGE,"E0.1.24.3"),sQuery(id+"F0.wireOp",EDGE,"E0.1.25.0"),sQuery(id+"F0.wireOp",EDGE,"E0.1.25.1"),sQuery(id+"F0.wireOp",EDGE,"E0.1.25.2"),sQuery(id+"F0.wireOp",EDGE,"E0.1.25.3"),sQuery(id+"F0.wireOp",EDGE,"E0.2.0.0"),sQuery(id+"F0.wireOp",EDGE,"E0.2.0.1"),sQuery(id+"F0.wireOp",EDGE,"E0.2.0.2"),sQuery(id+"F0.wireOp",EDGE,"E0.2.0.3"),sQuery(id+"F0.wireOp",EDGE,"E0.2.1.0"),sQuery(id+"F0.wireOp",EDGE,"E0.2.1.1"),sQuery(id+"F0.wireOp",EDGE,"E0.2.1.2"),sQuery(id+"F0.wireOp",EDGE,"E0.2.1.3"),sQuery(id+"F0.wireOp",EDGE,"E0.2.2.0"),sQuery(id+"F0.wireOp",EDGE,"E0.2.2.1"),sQuery(id+"F0.wireOp",EDGE,"E0.2.2.2"),sQuery(id+"F0.wireOp",EDGE,"E0.2.2.3"),sQuery(id+"F0.wireOp",EDGE,"E0.2.3.0"),sQuery(id+"F0.wireOp",EDGE,"E0.2.3.1"),sQuery(id+"F0.wireOp",EDGE,"E0.2.3.2"),sQuery(id+"F0.wireOp",EDGE,"E0.2.3.3"),sQuery(id+"F0.wireOp",EDGE,"E0.2.4.0"),sQuery(id+"F0.wireOp",EDGE,"E0.2.4.1"),sQuery(id+"F0.wireOp",EDGE,"E0.2.4.2"),sQuery(id+"F0.wireOp",EDGE,"E0.2.4.3"),sQuery(id+"F0.wireOp",EDGE,"E0.2.5.0"),sQuery(id+"F0.wireOp",EDGE,"E0.2.5.1"),sQuery(id+"F0.wireOp",EDGE,"E0.2.5.2"),sQuery(id+"F0.wireOp",EDGE,"E0.2.5.3"),sQuery(id+"F0.wireOp",EDGE,"E0.2.6.0"),sQuery(id+"F0.wireOp",EDGE,"E0.2.6.1"),sQuery(id+"F0.wireOp",EDGE,"E0.2.6.2"),sQuery(id+"F0.wireOp",EDGE,"E0.2.6.3"),sQuery(id+"F0.wireOp",EDGE,"E0.2.7.0"),sQuery(id+"F0.wireOp",EDGE,"E0.2.7.1"),sQuery(id+"F0.wireOp",EDGE,"E0.2.7.2"),sQuery(id+"F0.wireOp",EDGE,"E0.2.7.3"),sQuery(id+"F0.wireOp",EDGE,"E0.2.8.0"),sQuery(id+"F0.wireOp",EDGE,"E0.2.8.1"),sQuery(id+"F0.wireOp",EDGE,"E0.2.8.2"),sQuery(id+"F0.wireOp",EDGE,"E0.2.8.3"),sQuery(id+"F0.wireOp",EDGE,"E0.2.9.0"),sQuery(id+"F0.wireOp",EDGE,"E0.2.9.1"),sQuery(id+"F0.wireOp",EDGE,"E0.2.9.2"),sQuery(id+"F0.wireOp",EDGE,"E0.2.9.3"),sQuery(id+"F0.wireOp",EDGE,"E0.2.10.0"),sQuery(id+"F0.wireOp",EDGE,"E0.2.10.1"),sQuery(id+"F0.wireOp",EDGE,"E0.2.10.2"),sQuery(id+"F0.wireOp",EDGE,"E0.2.10.3"),sQuery(id+"F0.wireOp",EDGE,"E0.2.11.0"),sQuery(id+"F0.wireOp",EDGE,"E0.2.11.1"),sQuery(id+"F0.wireOp",EDGE,"E0.2.11.2"),sQuery(id+"F0.wireOp",EDGE,"E0.2.11.3"),sQuery(id+"F0.wireOp",EDGE,"E0.2.12.0"),sQuery(id+"F0.wireOp",EDGE,"E0.2.12.1"),sQuery(id+"F0.wireOp",EDGE,"E0.2.12.2"),sQuery(id+"F0.wireOp",EDGE,"E0.2.12.3"),sQuery(id+"F0.wireOp",EDGE,"E0.2.13.0"),sQuery(id+"F0.wireOp",EDGE,"E0.2.13.1"),sQuery(id+"F0.wireOp",EDGE,"E0.2.13.2"),sQuery(id+"F0.wireOp",EDGE,"E0.2.13.3"),sQuery(id+"F0.wireOp",EDGE,"E0.2.14.0"),sQuery(id+"F0.wireOp",EDGE,"E0.2.14.1"),sQuery(id+"F0.wireOp",EDGE,"E0.2.14.2"),sQuery(id+"F0.wireOp",EDGE,"E0.2.14.3"),sQuery(id+"F0.wireOp",EDGE,"E0.2.15.0"),sQuery(id+"F0.wireOp",EDGE,"E0.2.15.1"),sQuery(id+"F0.wireOp",EDGE,"E0.2.15.2"),sQuery(id+"F0.wireOp",EDGE,"E0.2.15.3"),sQuery(id+"F0.wireOp",EDGE,"E0.2.16.0"),sQuery(id+"F0.wireOp",EDGE,"E0.2.16.1"),sQuery(id+"F0.wireOp",EDGE,"E0.2.16.2"),sQuery(id+"F0.wireOp",EDGE,"E0.2.16.3"),sQuery(id+"F0.wireOp",EDGE,"E0.2.17.0"),sQuery(id+"F0.wireOp",EDGE,"E0.2.17.1"),sQuery(id+"F0.wireOp",EDGE,"E0.2.17.2"),sQuery(id+"F0.wireOp",EDGE,"E0.2.17.3"),sQuery(id+"F0.wireOp",EDGE,"E0.2.18.0"),sQuery(id+"F0.wireOp",EDGE,"E0.2.18.1"),sQuery(id+"F0.wireOp",EDGE,"E0.2.18.2"),sQuery(id+"F0.wireOp",EDGE,"E0.2.18.3"),sQuery(id+"F0.wireOp",EDGE,"E0.2.19.0"),sQuery(id+"F0.wireOp",EDGE,"E0.2.19.1"),sQuery(id+"F0.wireOp",EDGE,"E0.2.19.2"),sQuery(id+"F0.wireOp",EDGE,"E0.2.19.3"),sQuery(id+"F0.wireOp",EDGE,"E0.2.20.0"),sQuery(id+"F0.wireOp",EDGE,"E0.2.20.1"),sQuery(id+"F0.wireOp",EDGE,"E0.2.20.2"),sQuery(id+"F0.wireOp",EDGE,"E0.2.20.3"),sQuery(id+"F0.wireOp",EDGE,"E0.2.21.0"),sQuery(id+"F0.wireOp",EDGE,"E0.2.21.1"),sQuery(id+"F0.wireOp",EDGE,"E0.2.21.2"),sQuery(id+"F0.wireOp",EDGE,"E0.2.21.3"),sQuery(id+"F0.wireOp",EDGE,"E0.2.22.0"),sQuery(id+"F0.wireOp",EDGE,"E0.2.22.1"),sQuery(id+"F0.wireOp",EDGE,"E0.2.22.2"),sQuery(id+"F0.wireOp",EDGE,"E0.2.22.3"),sQuery(id+"F0.wireOp",EDGE,"E0.2.23.0"),sQuery(id+"F0.wireOp",EDGE,"E0.2.23.1"),sQuery(id+"F0.wireOp",EDGE,"E0.2.23.2"),sQuery(id+"F0.wireOp",EDGE,"E0.2.23.3"),sQuery(id+"F0.wireOp",EDGE,"E0.2.24.0"),sQuery(id+"F0.wireOp",EDGE,"E0.2.24.1"),sQuery(id+"F0.wireOp",EDGE,"E0.2.24.2"),sQuery(id+"F0.wireOp",EDGE,"E0.2.24.3"),sQuery(id+"F0.wireOp",EDGE,"E0.2.25.0"),sQuery(id+"F0.wireOp",EDGE,"E0.2.25.1"),sQuery(id+"F0.wireOp",EDGE,"E0.2.25.2"),sQuery(id+"F0.wireOp",EDGE,"E0.2.25.3"),sQuery(id+"F0.wireOp",EDGE,"AU2oHFlj-txaj-hLN4-KDEQ-E2aTrxoRIFTm"),sQuery(id+"F0.wireOp",EDGE,"T7GrudpP-bjZC-sghp-RzMj-ol2ZXyDjpRGs"),sQuery(id+"F0.wireOp",EDGE,"E1"),sQuery(id+"F0.wireOp",EDGE,"90fbf2e0-ce94-4077-ba36-f7078a65e9f6.1.0.0"),sQuery(id+"F0.wireOp",EDGE,"90fbf2e0-ce94-4077-ba36-f7078a65e9f6.1.0.1"),sQuery(id+"F0.wireOp",EDGE,"90fbf2e0-ce94-4077-ba36-f7078a65e9f6.1.0.2"),sQuery(id+"F0.wireOp",EDGE,"90fbf2e0-ce94-4077-ba36-f7078a65e9f6.1.0.3"),sQuery(id+"F0.wireOp",EDGE,"90fbf2e0-ce94-4077-ba36-f7078a65e9f6.1.0.4"),sQuery(id+"F0.wireOp",EDGE,"90fbf2e0-ce94-4077-ba36-f7078a65e9f6.1.0.5"),sQuery(id+"F0.wireOp",EDGE,"90fbf2e0-ce94-4077-ba36-f7078a65e9f6.1.0.6"),sQuery(id+"F0.wireOp",EDGE,"90fbf2e0-ce94-4077-ba36-f7078a65e9f6.1.0.7"),sQuery(id+"F0.wireOp",EDGE,"90fbf2e0-ce94-4077-ba36-f7078a65e9f6.1.0.8"),sQuery(id+"F0.wireOp",EDGE,"90fbf2e0-ce94-4077-ba36-f7078a65e9f6.1.0.9"),sQuery(id+"F0.wireOp",EDGE,"90fbf2e0-ce94-4077-ba36-f7078a65e9f6.1.0.10"),sQuery(id+"F0.wireOp",EDGE,"90fbf2e0-ce94-4077-ba36-f7078a65e9f6.1.0.11"),sQuery(id+"F0.wireOp",EDGE,"90fbf2e0-ce94-4077-ba36-f7078a65e9f6.2.0.0"),sQuery(id+"F0.wireOp",EDGE,"90fbf2e0-ce94-4077-ba36-f7078a65e9f6.2.0.1"),sQuery(id+"F0.wireOp",EDGE,"90fbf2e0-ce94-4077-ba36-f7078a65e9f6.2.0.2"),sQuery(id+"F0.wireOp",EDGE,"90fbf2e0-ce94-4077-ba36-f7078a65e9f6.2.0.3"),sQuery(id+"F0.wireOp",EDGE,"90fbf2e0-ce94-4077-ba36-f7078a65e9f6.2.0.4"),sQuery(id+"F0.wireOp",EDGE,"90fbf2e0-ce94-4077-ba36-f7078a65e9f6.2.0.5"),sQuery(id+"F0.wireOp",EDGE,"90fbf2e0-ce94-4077-ba36-f7078a65e9f6.2.0.6"),sQuery(id+"F0.wireOp",EDGE,"90fbf2e0-ce94-4077-ba36-f7078a65e9f6.2.0.7"),sQuery(id+"F0.wireOp",EDGE,"90fbf2e0-ce94-4077-ba36-f7078a65e9f6.2.0.8"),sQuery(id+"F0.wireOp",EDGE,"90fbf2e0-ce94-4077-ba36-f7078a65e9f6.2.0.9"),sQuery(id+"F0.wireOp",EDGE,"90fbf2e0-ce94-4077-ba36-f7078a65e9f6.2.0.10"),sQuery(id+"F0.wireOp",EDGE,"90fbf2e0-ce94-4077-ba36-f7078a65e9f6.2.0.11"),sQuery(id+"F0.wireOp",EDGE,"90fbf2e0-ce94-4077-ba36-f7078a65e9f6.3.0.0"),sQuery(id+"F0.wireOp",EDGE,"90fbf2e0-ce94-4077-ba36-f7078a65e9f6.3.0.1"),sQuery(id+"F0.wireOp",EDGE,"90fbf2e0-ce94-4077-ba36-f7078a65e9f6.3.0.2"),sQuery(id+"F0.wireOp",EDGE,"90fbf2e0-ce94-4077-ba36-f7078a65e9f6.3.0.3"),sQuery(id+"F0.wireOp",EDGE,"90fbf2e0-ce94-4077-ba36-f7078a65e9f6.3.0.4"),sQuery(id+"F0.wireOp",EDGE,"90fbf2e0-ce94-4077-ba36-f7078a65e9f6.3.0.5"),sQuery(id+"F0.wireOp",EDGE,"90fbf2e0-ce94-4077-ba36-f7078a65e9f6.3.0.6"),sQuery(id+"F0.wireOp",EDGE,"90fbf2e0-ce94-4077-ba36-f7078a65e9f6.3.0.7"),sQuery(id+"F0.wireOp",EDGE,"90fbf2e0-ce94-4077-ba36-f7078a65e9f6.3.0.8"),sQuery(id+"F0.wireOp",EDGE,"90fbf2e0-ce94-4077-ba36-f7078a65e9f6.3.0.9"),sQuery(id+"F0.wireOp",EDGE,"90fbf2e0-ce94-4077-ba36-f7078a65e9f6.3.0.10"),sQuery(id+"F0.wireOp",EDGE,"90fbf2e0-ce94-4077-ba36-f7078a65e9f6.3.0.11"),sQuery(id+"F0.wireOp",EDGE,"90fbf2e0-ce94-4077-ba36-f7078a65e9f6.4.0.0"),sQuery(id+"F0.wireOp",EDGE,"90fbf2e0-ce94-4077-ba36-f7078a65e9f6.4.0.1"),sQuery(id+"F0.wireOp",EDGE,"90fbf2e0-ce94-4077-ba36-f7078a65e9f6.4.0.2"),sQuery(id+"F0.wireOp",EDGE,"90fbf2e0-ce94-4077-ba36-f7078a65e9f6.4.0.3"),sQuery(id+"F0.wireOp",EDGE,"90fbf2e0-ce94-4077-ba36-f7078a65e9f6.4.0.4"),sQuery(id+"F0.wireOp",EDGE,"90fbf2e0-ce94-4077-ba36-f7078a65e9f6.4.0.5"),sQuery(id+"F0.wireOp",EDGE,"90fbf2e0-ce94-4077-ba36-f7078a65e9f6.4.0.6"),sQuery(id+"F0.wireOp",EDGE,"90fbf2e0-ce94-4077-ba36-f7078a65e9f6.4.0.7"),sQuery(id+"F0.wireOp",EDGE,"90fbf2e0-ce94-4077-ba36-f7078a65e9f6.4.0.8"),sQuery(id+"F0.wireOp",EDGE,"90fbf2e0-ce94-4077-ba36-f7078a65e9f6.4.0.9"),sQuery(id+"F0.wireOp",EDGE,"90fbf2e0-ce94-4077-ba36-f7078a65e9f6.4.0.10"),sQuery(id+"F0.wireOp",EDGE,"90fbf2e0-ce94-4077-ba36-f7078a65e9f6.4.0.11"),sQuery(id+"F0.wireOp",EDGE,"90fbf2e0-ce94-4077-ba36-f7078a65e9f6.5.0.0"),sQuery(id+"F0.wireOp",EDGE,"90fbf2e0-ce94-4077-ba36-f7078a65e9f6.5.0.1"),sQuery(id+"F0.wireOp",EDGE,"90fbf2e0-ce94-4077-ba36-f7078a65e9f6.5.0.2"),sQuery(id+"F0.wireOp",EDGE,"90fbf2e0-ce94-4077-ba36-f7078a65e9f6.5.0.3"),sQuery(id+"F0.wireOp",EDGE,"90fbf2e0-ce94-4077-ba36-f7078a65e9f6.5.0.4"),sQuery(id+"F0.wireOp",EDGE,"90fbf2e0-ce94-4077-ba36-f7078a65e9f6.5.0.5"),sQuery(id+"F0.wireOp",EDGE,"90fbf2e0-ce94-4077-ba36-f7078a65e9f6.5.0.6"),sQuery(id+"F0.wireOp",EDGE,"90fbf2e0-ce94-4077-ba36-f7078a65e9f6.5.0.7"),sQuery(id+"F0.wireOp",EDGE,"90fbf2e0-ce94-4077-ba36-f7078a65e9f6.5.0.8"),sQuery(id+"F0.wireOp",EDGE,"90fbf2e0-ce94-4077-ba36-f7078a65e9f6.5.0.9"),sQuery(id+"F0.wireOp",EDGE,"90fbf2e0-ce94-4077-ba36-f7078a65e9f6.5.0.10"),sQuery(id+"F0.wireOp",EDGE,"90fbf2e0-ce94-4077-ba36-f7078a65e9f6.5.0.11"),sQuery(id+"F0.wireOp",EDGE,"90fbf2e0-ce94-4077-ba36-f7078a65e9f6.6.0.0"),sQuery(id+"F0.wireOp",EDGE,"90fbf2e0-ce94-4077-ba36-f7078a65e9f6.6.0.1"),sQuery(id+"F0.wireOp",EDGE,"90fbf2e0-ce94-4077-ba36-f7078a65e9f6.6.0.2"),sQuery(id+"F0.wireOp",EDGE,"90fbf2e0-ce94-4077-ba36-f7078a65e9f6.6.0.3"),sQuery(id+"F0.wireOp",EDGE,"90fbf2e0-ce94-4077-ba36-f7078a65e9f6.6.0.4"),sQuery(id+"F0.wireOp",EDGE,"90fbf2e0-ce94-4077-ba36-f7078a65e9f6.6.0.5"),sQuery(id+"F0.wireOp",EDGE,"90fbf2e0-ce94-4077-ba36-f7078a65e9f6.6.0.6"),sQuery(id+"F0.wireOp",EDGE,"90fbf2e0-ce94-4077-ba36-f7078a65e9f6.6.0.7"),sQuery(id+"F0.wireOp",EDGE,"90fbf2e0-ce94-4077-ba36-f7078a65e9f6.6.0.8"),sQuery(id+"F0.wireOp",EDGE,"90fbf2e0-ce94-4077-ba36-f7078a65e9f6.6.0.9"),sQuery(id+"F0.wireOp",EDGE,"90fbf2e0-ce94-4077-ba36-f7078a65e9f6.6.0.10"),sQuery(id+"F0.wireOp",EDGE,"90fbf2e0-ce94-4077-ba36-f7078a65e9f6.6.0.11"),sQuery(id+"F0.wireOp",EDGE,"90fbf2e0-ce94-4077-ba36-f7078a65e9f6.7.0.0"),sQuery(id+"F0.wireOp",EDGE,"90fbf2e0-ce94-4077-ba36-f7078a65e9f6.7.0.1"),sQuery(id+"F0.wireOp",EDGE,"90fbf2e0-ce94-4077-ba36-f7078a65e9f6.7.0.2"),sQuery(id+"F0.wireOp",EDGE,"90fbf2e0-ce94-4077-ba36-f7078a65e9f6.7.0.3"),sQuery(id+"F0.wireOp",EDGE,"90fbf2e0-ce94-4077-ba36-f7078a65e9f6.7.0.4"),sQuery(id+"F0.wireOp",EDGE,"90fbf2e0-ce94-4077-ba36-f7078a65e9f6.7.0.5"),sQuery(id+"F0.wireOp",EDGE,"90fbf2e0-ce94-4077-ba36-f7078a65e9f6.7.0.6"),sQuery(id+"F0.wireOp",EDGE,"90fbf2e0-ce94-4077-ba36-f7078a65e9f6.7.0.7"),sQuery(id+"F0.wireOp",EDGE,"90fbf2e0-ce94-4077-ba36-f7078a65e9f6.7.0.8"),sQuery(id+"F0.wireOp",EDGE,"90fbf2e0-ce94-4077-ba36-f7078a65e9f6.7.0.9"),sQuery(id+"F0.wireOp",EDGE,"90fbf2e0-ce94-4077-ba36-f7078a65e9f6.7.0.10"),sQuery(id+"F0.wireOp",EDGE,"90fbf2e0-ce94-4077-ba36-f7078a65e9f6.7.0.11"),sQuery(id+"F0.wireOp",EDGE,"90fbf2e0-ce94-4077-ba36-f7078a65e9f6.8.0.0"),sQuery(id+"F0.wireOp",EDGE,"90fbf2e0-ce94-4077-ba36-f7078a65e9f6.8.0.1"),sQuery(id+"F0.wireOp",EDGE,"90fbf2e0-ce94-4077-ba36-f7078a65e9f6.8.0.2"),sQuery(id+"F0.wireOp",EDGE,"90fbf2e0-ce94-4077-ba36-f7078a65e9f6.8.0.3"),sQuery(id+"F0.wireOp",EDGE,"90fbf2e0-ce94-4077-ba36-f7078a65e9f6.8.0.4"),sQuery(id+"F0.wireOp",EDGE,"90fbf2e0-ce94-4077-ba36-f7078a65e9f6.8.0.5"),sQuery(id+"F0.wireOp",EDGE,"90fbf2e0-ce94-4077-ba36-f7078a65e9f6.8.0.6"),sQuery(id+"F0.wireOp",EDGE,"90fbf2e0-ce94-4077-ba36-f7078a65e9f6.8.0.7"),sQuery(id+"F0.wireOp",EDGE,"90fbf2e0-ce94-4077-ba36-f7078a65e9f6.8.0.8"),sQuery(id+"F0.wireOp",EDGE,"90fbf2e0-ce94-4077-ba36-f7078a65e9f6.8.0.9"),sQuery(id+"F0.wireOp",EDGE,"90fbf2e0-ce94-4077-ba36-f7078a65e9f6.8.0.10"),sQuery(id+"F0.wireOp",EDGE,"90fbf2e0-ce94-4077-ba36-f7078a65e9f6.8.0.11"),sQuery(id+"F0.wireOp",EDGE,"90fbf2e0-ce94-4077-ba36-f7078a65e9f6.9.0.0"),sQuery(id+"F0.wireOp",EDGE,"90fbf2e0-ce94-4077-ba36-f7078a65e9f6.9.0.1"),sQuery(id+"F0.wireOp",EDGE,"90fbf2e0-ce94-4077-ba36-f7078a65e9f6.9.0.2"),sQuery(id+"F0.wireOp",EDGE,"90fbf2e0-ce94-4077-ba36-f7078a65e9f6.9.0.3"),sQuery(id+"F0.wireOp",EDGE,"90fbf2e0-ce94-4077-ba36-f7078a65e9f6.9.0.4"),sQuery(id+"F0.wireOp",EDGE,"90fbf2e0-ce94-4077-ba36-f7078a65e9f6.9.0.5"),sQuery(id+"F0.wireOp",EDGE,"90fbf2e0-ce94-4077-ba36-f7078a65e9f6.9.0.6"),sQuery(id+"F0.wireOp",EDGE,"90fbf2e0-ce94-4077-ba36-f7078a65e9f6.9.0.7"),sQuery(id+"F0.wireOp",EDGE,"90fbf2e0-ce94-4077-ba36-f7078a65e9f6.9.0.8"),sQuery(id+"F0.wireOp",EDGE,"90fbf2e0-ce94-4077-ba36-f7078a65e9f6.9.0.9"),sQuery(id+"F0.wireOp",EDGE,"90fbf2e0-ce94-4077-ba36-f7078a65e9f6.9.0.10"),sQuery(id+"F0.wireOp",EDGE,"90fbf2e0-ce94-4077-ba36-f7078a65e9f6.9.0.11"),sQuery(id+"F0.wireOp",EDGE,"90fbf2e0-ce94-4077-ba36-f7078a65e9f6.10.0.0"),sQuery(id+"F0.wireOp",EDGE,"90fbf2e0-ce94-4077-ba36-f7078a65e9f6.10.0.1"),sQuery(id+"F0.wireOp",EDGE,"90fbf2e0-ce94-4077-ba36-f7078a65e9f6.10.0.2"),sQuery(id+"F0.wireOp",EDGE,"90fbf2e0-ce94-4077-ba36-f7078a65e9f6.10.0.3"),sQuery(id+"F0.wireOp",EDGE,"90fbf2e0-ce94-4077-ba36-f7078a65e9f6.10.0.4"),sQuery(id+"F0.wireOp",EDGE,"90fbf2e0-ce94-4077-ba36-f7078a65e9f6.10.0.5"),sQuery(id+"F0.wireOp",EDGE,"90fbf2e0-ce94-4077-ba36-f7078a65e9f6.10.0.6"),sQuery(id+"F0.wireOp",EDGE,"90fbf2e0-ce94-4077-ba36-f7078a65e9f6.10.0.7"),sQuery(id+"F0.wireOp",EDGE,"90fbf2e0-ce94-4077-ba36-f7078a65e9f6.10.0.8"),sQuery(id+"F0.wireOp",EDGE,"90fbf2e0-ce94-4077-ba36-f7078a65e9f6.10.0.9"),sQuery(id+"F0.wireOp",EDGE,"90fbf2e0-ce94-4077-ba36-f7078a65e9f6.10.0.10"),sQuery(id+"F0.wireOp",EDGE,"90fbf2e0-ce94-4077-ba36-f7078a65e9f6.10.0.11"),sQuery(id+"F0.wireOp",EDGE,"ef05f06f-9539-49a4-bbe1-e5de78f87bac.1.0.0"),sQuery(id+"F0.wireOp",EDGE,"ef05f06f-9539-49a4-bbe1-e5de78f87bac.1.0.1"),sQuery(id+"F0.wireOp",EDGE,"ef05f06f-9539-49a4-bbe1-e5de78f87bac.1.0.2"),sQuery(id+"F0.wireOp",EDGE,"ef05f06f-9539-49a4-bbe1-e5de78f87bac.1.0.3"),sQuery(id+"F0.wireOp",EDGE,"ef05f06f-9539-49a4-bbe1-e5de78f87bac.1.0.4"),sQuery(id+"F0.wireOp",EDGE,"ef05f06f-9539-49a4-bbe1-e5de78f87bac.1.0.5"),sQuery(id+"F0.wireOp",EDGE,"ef05f06f-9539-49a4-bbe1-e5de78f87bac.1.0.6"),sQuery(id+"F0.wireOp",EDGE,"ef05f06f-9539-49a4-bbe1-e5de78f87bac.1.0.7"),sQuery(id+"F0.wireOp",EDGE,"ef05f06f-9539-49a4-bbe1-e5de78f87bac.1.0.8"),sQuery(id+"F0.wireOp",EDGE,"ef05f06f-9539-49a4-bbe1-e5de78f87bac.1.0.9"),sQuery(id+"F0.wireOp",EDGE,"ef05f06f-9539-49a4-bbe1-e5de78f87bac.1.0.10"),sQuery(id+"F0.wireOp",EDGE,"ef05f06f-9539-49a4-bbe1-e5de78f87bac.1.0.11"),sQuery(id+"F0.wireOp",EDGE,"ef05f06f-9539-49a4-bbe1-e5de78f87bac.2.0.0"),sQuery(id+"F0.wireOp",EDGE,"ef05f06f-9539-49a4-bbe1-e5de78f87bac.2.0.1"),sQuery(id+"F0.wireOp",EDGE,"ef05f06f-9539-49a4-bbe1-e5de78f87bac.2.0.2"),sQuery(id+"F0.wireOp",EDGE,"ef05f06f-9539-49a4-bbe1-e5de78f87bac.2.0.3"),sQuery(id+"F0.wireOp",EDGE,"ef05f06f-9539-49a4-bbe1-e5de78f87bac.2.0.4"),sQuery(id+"F0.wireOp",EDGE,"ef05f06f-9539-49a4-bbe1-e5de78f87bac.2.0.5"),sQuery(id+"F0.wireOp",EDGE,"ef05f06f-9539-49a4-bbe1-e5de78f87bac.2.0.6"),sQuery(id+"F0.wireOp",EDGE,"ef05f06f-9539-49a4-bbe1-e5de78f87bac.2.0.7"),sQuery(id+"F0.wireOp",EDGE,"ef05f06f-9539-49a4-bbe1-e5de78f87bac.2.0.8"),sQuery(id+"F0.wireOp",EDGE,"ef05f06f-9539-49a4-bbe1-e5de78f87bac.2.0.9"),sQuery(id+"F0.wireOp",EDGE,"ef05f06f-9539-49a4-bbe1-e5de78f87bac.2.0.10"),sQuery(id+"F0.wireOp",EDGE,"ef05f06f-9539-49a4-bbe1-e5de78f87bac.2.0.11"),sQuery(id+"F0.wireOp",EDGE,"ef05f06f-9539-49a4-bbe1-e5de78f87bac.3.0.0"),sQuery(id+"F0.wireOp",EDGE,"ef05f06f-9539-49a4-bbe1-e5de78f87bac.3.0.1"),sQuery(id+"F0.wireOp",EDGE,"ef05f06f-9539-49a4-bbe1-e5de78f87bac.3.0.2"),sQuery(id+"F0.wireOp",EDGE,"ef05f06f-9539-49a4-bbe1-e5de78f87bac.3.0.3"),sQuery(id+"F0.wireOp",EDGE,"ef05f06f-9539-49a4-bbe1-e5de78f87bac.3.0.4"),sQuery(id+"F0.wireOp",EDGE,"ef05f06f-9539-49a4-bbe1-e5de78f87bac.3.0.5"),sQuery(id+"F0.wireOp",EDGE,"ef05f06f-9539-49a4-bbe1-e5de78f87bac.3.0.6"),sQuery(id+"F0.wireOp",EDGE,"ef05f06f-9539-49a4-bbe1-e5de78f87bac.3.0.7"),sQuery(id+"F0.wireOp",EDGE,"ef05f06f-9539-49a4-bbe1-e5de78f87bac.3.0.8"),sQuery(id+"F0.wireOp",EDGE,"ef05f06f-9539-49a4-bbe1-e5de78f87bac.3.0.9"),sQuery(id+"F0.wireOp",EDGE,"ef05f06f-9539-49a4-bbe1-e5de78f87bac.3.0.10"),sQuery(id+"F0.wireOp",EDGE,"ef05f06f-9539-49a4-bbe1-e5de78f87bac.3.0.11"),sQuery(id+"F0.wireOp",EDGE,"ef05f06f-9539-49a4-bbe1-e5de78f87bac.4.0.0"),sQuery(id+"F0.wireOp",EDGE,"ef05f06f-9539-49a4-bbe1-e5de78f87bac.4.0.1"),sQuery(id+"F0.wireOp",EDGE,"ef05f06f-9539-49a4-bbe1-e5de78f87bac.4.0.2"),sQuery(id+"F0.wireOp",EDGE,"ef05f06f-9539-49a4-bbe1-e5de78f87bac.4.0.3"),sQuery(id+"F0.wireOp",EDGE,"ef05f06f-9539-49a4-bbe1-e5de78f87bac.4.0.4"),sQuery(id+"F0.wireOp",EDGE,"ef05f06f-9539-49a4-bbe1-e5de78f87bac.4.0.5"),sQuery(id+"F0.wireOp",EDGE,"ef05f06f-9539-49a4-bbe1-e5de78f87bac.4.0.6"),sQuery(id+"F0.wireOp",EDGE,"ef05f06f-9539-49a4-bbe1-e5de78f87bac.4.0.7"),sQuery(id+"F0.wireOp",EDGE,"ef05f06f-9539-49a4-bbe1-e5de78f87bac.4.0.8"),sQuery(id+"F0.wireOp",EDGE,"ef05f06f-9539-49a4-bbe1-e5de78f87bac.4.0.9"),sQuery(id+"F0.wireOp",EDGE,"ef05f06f-9539-49a4-bbe1-e5de78f87bac.4.0.10"),sQuery(id+"F0.wireOp",EDGE,"ef05f06f-9539-49a4-bbe1-e5de78f87bac.4.0.11"),sQuery(id+"F0.wireOp",EDGE,"ef05f06f-9539-49a4-bbe1-e5de78f87bac.5.0.0"),sQuery(id+"F0.wireOp",EDGE,"ef05f06f-9539-49a4-bbe1-e5de78f87bac.5.0.1"),sQuery(id+"F0.wireOp",EDGE,"ef05f06f-9539-49a4-bbe1-e5de78f87bac.5.0.2"),sQuery(id+"F0.wireOp",EDGE,"ef05f06f-9539-49a4-bbe1-e5de78f87bac.5.0.3"),sQuery(id+"F0.wireOp",EDGE,"ef05f06f-9539-49a4-bbe1-e5de78f87bac.5.0.4"),sQuery(id+"F0.wireOp",EDGE,"ef05f06f-9539-49a4-bbe1-e5de78f87bac.5.0.5"),sQuery(id+"F0.wireOp",EDGE,"ef05f06f-9539-49a4-bbe1-e5de78f87bac.5.0.6"),sQuery(id+"F0.wireOp",EDGE,"ef05f06f-9539-49a4-bbe1-e5de78f87bac.5.0.7"),sQuery(id+"F0.wireOp",EDGE,"ef05f06f-9539-49a4-bbe1-e5de78f87bac.5.0.8"),sQuery(id+"F0.wireOp",EDGE,"ef05f06f-9539-49a4-bbe1-e5de78f87bac.5.0.9"),sQuery(id+"F0.wireOp",EDGE,"ef05f06f-9539-49a4-bbe1-e5de78f87bac.5.0.10"),sQuery(id+"F0.wireOp",EDGE,"ef05f06f-9539-49a4-bbe1-e5de78f87bac.5.0.11"),sQuery(id+"F0.wireOp",EDGE,"ef05f06f-9539-49a4-bbe1-e5de78f87bac.6.0.0"),sQuery(id+"F0.wireOp",EDGE,"ef05f06f-9539-49a4-bbe1-e5de78f87bac.6.0.1"),sQuery(id+"F0.wireOp",EDGE,"ef05f06f-9539-49a4-bbe1-e5de78f87bac.6.0.2"),sQuery(id+"F0.wireOp",EDGE,"ef05f06f-9539-49a4-bbe1-e5de78f87bac.6.0.3"),sQuery(id+"F0.wireOp",EDGE,"ef05f06f-9539-49a4-bbe1-e5de78f87bac.6.0.4"),sQuery(id+"F0.wireOp",EDGE,"ef05f06f-9539-49a4-bbe1-e5de78f87bac.6.0.5"),sQuery(id+"F0.wireOp",EDGE,"ef05f06f-9539-49a4-bbe1-e5de78f87bac.6.0.6"),sQuery(id+"F0.wireOp",EDGE,"ef05f06f-9539-49a4-bbe1-e5de78f87bac.6.0.7"),sQuery(id+"F0.wireOp",EDGE,"ef05f06f-9539-49a4-bbe1-e5de78f87bac.6.0.8"),sQuery(id+"F0.wireOp",EDGE,"ef05f06f-9539-49a4-bbe1-e5de78f87bac.6.0.9"),sQuery(id+"F0.wireOp",EDGE,"ef05f06f-9539-49a4-bbe1-e5de78f87bac.6.0.10"),sQuery(id+"F0.wireOp",EDGE,"ef05f06f-9539-49a4-bbe1-e5de78f87bac.6.0.11"),sQuery(id+"F0.wireOp",EDGE,"ef05f06f-9539-49a4-bbe1-e5de78f87bac.7.0.0"),sQuery(id+"F0.wireOp",EDGE,"ef05f06f-9539-49a4-bbe1-e5de78f87bac.7.0.1"),sQuery(id+"F0.wireOp",EDGE,"ef05f06f-9539-49a4-bbe1-e5de78f87bac.7.0.2"),sQuery(id+"F0.wireOp",EDGE,"ef05f06f-9539-49a4-bbe1-e5de78f87bac.7.0.3"),sQuery(id+"F0.wireOp",EDGE,"ef05f06f-9539-49a4-bbe1-e5de78f87bac.7.0.4"),sQuery(id+"F0.wireOp",EDGE,"ef05f06f-9539-49a4-bbe1-e5de78f87bac.7.0.5"),sQuery(id+"F0.wireOp",EDGE,"ef05f06f-9539-49a4-bbe1-e5de78f87bac.7.0.6"),sQuery(id+"F0.wireOp",EDGE,"ef05f06f-9539-49a4-bbe1-e5de78f87bac.7.0.7"),sQuery(id+"F0.wireOp",EDGE,"ef05f06f-9539-49a4-bbe1-e5de78f87bac.7.0.8"),sQuery(id+"F0.wireOp",EDGE,"ef05f06f-9539-49a4-bbe1-e5de78f87bac.7.0.9"),sQuery(id+"F0.wireOp",EDGE,"ef05f06f-9539-49a4-bbe1-e5de78f87bac.7.0.10"),sQuery(id+"F0.wireOp",EDGE,"ef05f06f-9539-49a4-bbe1-e5de78f87bac.7.0.11"),sQuery(id+"F0.wireOp",EDGE,"ef05f06f-9539-49a4-bbe1-e5de78f87bac.8.0.0"),sQuery(id+"F0.wireOp",EDGE,"ef05f06f-9539-49a4-bbe1-e5de78f87bac.8.0.1"),sQuery(id+"F0.wireOp",EDGE,"ef05f06f-9539-49a4-bbe1-e5de78f87bac.8.0.2"),sQuery(id+"F0.wireOp",EDGE,"ef05f06f-9539-49a4-bbe1-e5de78f87bac.8.0.3"),sQuery(id+"F0.wireOp",EDGE,"ef05f06f-9539-49a4-bbe1-e5de78f87bac.8.0.4"),sQuery(id+"F0.wireOp",EDGE,"ef05f06f-9539-49a4-bbe1-e5de78f87bac.8.0.5"),sQuery(id+"F0.wireOp",EDGE,"ef05f06f-9539-49a4-bbe1-e5de78f87bac.8.0.6"),sQuery(id+"F0.wireOp",EDGE,"ef05f06f-9539-49a4-bbe1-e5de78f87bac.8.0.7"),sQuery(id+"F0.wireOp",EDGE,"ef05f06f-9539-49a4-bbe1-e5de78f87bac.8.0.8"),sQuery(id+"F0.wireOp",EDGE,"ef05f06f-9539-49a4-bbe1-e5de78f87bac.8.0.9"),sQuery(id+"F0.wireOp",EDGE,"ef05f06f-9539-49a4-bbe1-e5de78f87bac.8.0.10"),sQuery(id+"F0.wireOp",EDGE,"ef05f06f-9539-49a4-bbe1-e5de78f87bac.8.0.11"),sQuery(id+"F0.wireOp",EDGE,"ef05f06f-9539-49a4-bbe1-e5de78f87bac.9.0.0"),sQuery(id+"F0.wireOp",EDGE,"ef05f06f-9539-49a4-bbe1-e5de78f87bac.9.0.1"),sQuery(id+"F0.wireOp",EDGE,"ef05f06f-9539-49a4-bbe1-e5de78f87bac.9.0.2"),sQuery(id+"F0.wireOp",EDGE,"ef05f06f-9539-49a4-bbe1-e5de78f87bac.9.0.3"),sQuery(id+"F0.wireOp",EDGE,"ef05f06f-9539-49a4-bbe1-e5de78f87bac.9.0.4"),sQuery(id+"F0.wireOp",EDGE,"ef05f06f-9539-49a4-bbe1-e5de78f87bac.9.0.5"),sQuery(id+"F0.wireOp",EDGE,"ef05f06f-9539-49a4-bbe1-e5de78f87bac.9.0.6"),sQuery(id+"F0.wireOp",EDGE,"ef05f06f-9539-49a4-bbe1-e5de78f87bac.9.0.7"),sQuery(id+"F0.wireOp",EDGE,"ef05f06f-9539-49a4-bbe1-e5de78f87bac.9.0.8"),sQuery(id+"F0.wireOp",EDGE,"ef05f06f-9539-49a4-bbe1-e5de78f87bac.9.0.9"),sQuery(id+"F0.wireOp",EDGE,"ef05f06f-9539-49a4-bbe1-e5de78f87bac.9.0.10"),sQuery(id+"F0.wireOp",EDGE,"ef05f06f-9539-49a4-bbe1-e5de78f87bac.9.0.11"),sQuery(id+"F0.wireOp",EDGE,"ef05f06f-9539-49a4-bbe1-e5de78f87bac.10.0.0"),sQuery(id+"F0.wireOp",EDGE,"ef05f06f-9539-49a4-bbe1-e5de78f87bac.10.0.1"),sQuery(id+"F0.wireOp",EDGE,"ef05f06f-9539-49a4-bbe1-e5de78f87bac.10.0.2"),sQuery(id+"F0.wireOp",EDGE,"ef05f06f-9539-49a4-bbe1-e5de78f87bac.10.0.3"),sQuery(id+"F0.wireOp",EDGE,"ef05f06f-9539-49a4-bbe1-e5de78f87bac.10.0.4"),sQuery(id+"F0.wireOp",EDGE,"ef05f06f-9539-49a4-bbe1-e5de78f87bac.10.0.5"),sQuery(id+"F0.wireOp",EDGE,"ef05f06f-9539-49a4-bbe1-e5de78f87bac.10.0.6"),sQuery(id+"F0.wireOp",EDGE,"ef05f06f-9539-49a4-bbe1-e5de78f87bac.10.0.7"),sQuery(id+"F0.wireOp",EDGE,"ef05f06f-9539-49a4-bbe1-e5de78f87bac.10.0.8"),sQuery(id+"F0.wireOp",EDGE,"ef05f06f-9539-49a4-bbe1-e5de78f87bac.10.0.9"),sQuery(id+"F0.wireOp",EDGE,"ef05f06f-9539-49a4-bbe1-e5de78f87bac.10.0.10"),sQuery(id+"F0.wireOp",EDGE,"ef05f06f-9539-49a4-bbe1-e5de78f87bac.10.0.11"),sQuery(id+"F0.wireOp",EDGE,"OJy4rNNo-w8Xi-PtYp-78KY-KX9WQq1O9zWX"),sQuery(id+"F0.wireOp",EDGE,"6ad1825e-1499-4b2d-8658-c8d5a4458ecc.filletArc"),sQuery(id+"F0.wireOp",EDGE,"0e28861b-0804-44a8-a45e-df2b0c80d6fb.filletArc"),sQuery(id+"F0.wireOp",EDGE,"69729d80-6c64-417c-b4d8-b2ce01de760d.filletArc"),sQuery(id+"F0.wireOp",EDGE,"57ece835-d495-4d14-92ee-c9d50648b8c1.filletArc")])],"isStart":false});
            var sketch = newSketch(context, id + "F29", { "sketchPlane" : qUnion([Q0])});
            skLineSegment(sketch, "E120", {"start": v(-86.55, 131.53) * mm, "end": v(-86.55, 136.15) * mm});
            skLineSegment(sketch, "E121", {"start": v(-86.55, 136.15) * mm, "end": v(-91.18, 136.15) * mm});
            skLineSegment(sketch, "E122", {"start": v(-91.18, 136.15) * mm, "end": v(-91.18, 131.53) * mm});
            skLineSegment(sketch, "E123", {"start": v(-91.18, 131.53) * mm, "end": v(-86.55, 131.53) * mm});
            skLineSegment(sketch, "E124", {"start": v(-86.55, 4.53) * mm, "end": v(-86.55, 9.15) * mm});
            skLineSegment(sketch, "E125", {"start": v(-86.55, 9.15) * mm, "end": v(-91.18, 9.15) * mm});
            skLineSegment(sketch, "E126", {"start": v(-91.18, 9.15) * mm, "end": v(-91.18, 4.53) * mm});
            skLineSegment(sketch, "E127", {"start": v(-91.18, 4.53) * mm, "end": v(-86.55, 4.53) * mm});
            skLineSegment(sketch, "E128", {"start": v(17.95, -1.73) * mm, "end": v(22.57, -1.73) * mm});
            skLineSegment(sketch, "E129", {"start": v(22.57, -1.73) * mm, "end": v(22.57, -6.36) * mm});
            skLineSegment(sketch, "E130", {"start": v(22.57, -6.36) * mm, "end": v(17.95, -6.36) * mm});
            skLineSegment(sketch, "E131", {"start": v(17.95, -6.36) * mm, "end": v(17.95, -1.73) * mm});
            skLineSegment(sketch, "E132", {"start": v(53.15, 136.15) * mm, "end": v(48.52, 136.15) * mm});
            skLineSegment(sketch, "E133", {"start": v(48.52, 136.15) * mm, "end": v(48.52, 131.53) * mm});
            skLineSegment(sketch, "E134", {"start": v(48.52, 131.53) * mm, "end": v(53.15, 131.53) * mm});
            skLineSegment(sketch, "E135", {"start": v(53.15, 131.53) * mm, "end": v(53.15, 136.15) * mm});
            skSolve(sketch);
        }
        {
            var Q0;
            Q0 = qSketchRegion(id + "F29", true);
            extrude(context, id + "F30", {"entities" : qUnion([Q0]), "depth" : 76.2 * mm});
        }
        {
            var Q0;
            Q0=makeQuery(id+"F30.opExtrude","CAP_FACE",FACE,{"disambiguationData":[OSD([sQuery(id+"F29.wireOp",EDGE,"E132"),sQuery(id+"F29.wireOp",EDGE,"E133"),sQuery(id+"F29.wireOp",EDGE,"E134"),sQuery(id+"F29.wireOp",EDGE,"E135")])],"isStart":false});
            var sketch = newSketch(context, id + "F31", { "sketchPlane" : qUnion([Q0])});
            skLineSegment(sketch, "E136", {"start": v(53.15, 136.15) * mm, "end": v(48.52, 136.15) * mm});
            skLineSegment(sketch, "E137", {"start": v(48.52, 136.15) * mm, "end": v(48.52, 131.53) * mm});
            skLineSegment(sketch, "E138", {"start": v(48.52, 131.53) * mm, "end": v(53.15, 131.53) * mm});
            skLineSegment(sketch, "E139", {"start": v(53.15, 131.53) * mm, "end": v(53.15, 136.15) * mm});
            skLineSegment(sketch, "E140.bottom", {"start": v(57.19, 140.2) * mm, "end": v(-95.21, 140.2) * mm});
            skLineSegment(sketch, "E140.top", {"start": v(57.19, 0.5) * mm, "end": v(-95.21, 0.5) * mm});
            skLineSegment(sketch, "E140.left", {"start": v(57.19, 140.2) * mm, "end": v(57.19, 0.5) * mm});
            skLineSegment(sketch, "E140.right", {"start": v(-95.21, 140.2) * mm, "end": v(-95.21, 0.5) * mm});
            skLineSegment(sketch, "E141.0.1.0", {"start": v(53.15, 118.83) * mm, "end": v(53.15, 123.45) * mm});
            skLineSegment(sketch, "E141.0.1.1", {"start": v(53.15, 123.45) * mm, "end": v(48.52, 123.45) * mm});
            skLineSegment(sketch, "E141.0.1.2", {"start": v(48.52, 123.45) * mm, "end": v(48.52, 118.83) * mm});
            skLineSegment(sketch, "E141.0.1.3", {"start": v(48.52, 118.83) * mm, "end": v(53.15, 118.83) * mm});
            skLineSegment(sketch, "E141.0.2.0", {"start": v(53.15, 106.13) * mm, "end": v(53.15, 110.75) * mm});
            skLineSegment(sketch, "E141.0.2.1", {"start": v(53.15, 110.75) * mm, "end": v(48.52, 110.75) * mm});
            skLineSegment(sketch, "E141.0.2.2", {"start": v(48.52, 110.75) * mm, "end": v(48.52, 106.13) * mm});
            skLineSegment(sketch, "E141.0.2.3", {"start": v(48.52, 106.13) * mm, "end": v(53.15, 106.13) * mm});
            skLineSegment(sketch, "E141.0.3.0", {"start": v(53.15, 93.43) * mm, "end": v(53.15, 98.05) * mm});
            skLineSegment(sketch, "E141.0.3.1", {"start": v(53.15, 98.05) * mm, "end": v(48.52, 98.05) * mm});
            skLineSegment(sketch, "E141.0.3.2", {"start": v(48.52, 98.05) * mm, "end": v(48.52, 93.43) * mm});
            skLineSegment(sketch, "E141.0.3.3", {"start": v(48.52, 93.43) * mm, "end": v(53.15, 93.43) * mm});
            skLineSegment(sketch, "E141.0.4.0", {"start": v(53.15, 80.73) * mm, "end": v(53.15, 85.35) * mm});
            skLineSegment(sketch, "E141.0.4.1", {"start": v(53.15, 85.35) * mm, "end": v(48.52, 85.35) * mm});
            skLineSegment(sketch, "E141.0.4.2", {"start": v(48.52, 85.35) * mm, "end": v(48.52, 80.73) * mm});
            skLineSegment(sketch, "E141.0.4.3", {"start": v(48.52, 80.73) * mm, "end": v(53.15, 80.73) * mm});
            skLineSegment(sketch, "E141.0.5.0", {"start": v(53.15, 68.03) * mm, "end": v(53.15, 72.65) * mm});
            skLineSegment(sketch, "E141.0.5.1", {"start": v(53.15, 72.65) * mm, "end": v(48.52, 72.65) * mm});
            skLineSegment(sketch, "E141.0.5.2", {"start": v(48.52, 72.65) * mm, "end": v(48.52, 68.03) * mm});
            skLineSegment(sketch, "E141.0.5.3", {"start": v(48.52, 68.03) * mm, "end": v(53.15, 68.03) * mm});
            skLineSegment(sketch, "E141.0.6.0", {"start": v(53.15, 55.33) * mm, "end": v(53.15, 59.95) * mm});
            skLineSegment(sketch, "E141.0.6.1", {"start": v(53.15, 59.95) * mm, "end": v(48.52, 59.95) * mm});
            skLineSegment(sketch, "E141.0.6.2", {"start": v(48.52, 59.95) * mm, "end": v(48.52, 55.33) * mm});
            skLineSegment(sketch, "E141.0.6.3", {"start": v(48.52, 55.33) * mm, "end": v(53.15, 55.33) * mm});
            skLineSegment(sketch, "E141.0.7.0", {"start": v(53.15, 42.63) * mm, "end": v(53.15, 47.25) * mm});
            skLineSegment(sketch, "E141.0.7.1", {"start": v(53.15, 47.25) * mm, "end": v(48.52, 47.25) * mm});
            skLineSegment(sketch, "E141.0.7.2", {"start": v(48.52, 47.25) * mm, "end": v(48.52, 42.63) * mm});
            skLineSegment(sketch, "E141.0.7.3", {"start": v(48.52, 42.63) * mm, "end": v(53.15, 42.63) * mm});
            skLineSegment(sketch, "E141.0.8.0", {"start": v(53.15, 29.93) * mm, "end": v(53.15, 34.55) * mm});
            skLineSegment(sketch, "E141.0.8.1", {"start": v(53.15, 34.55) * mm, "end": v(48.52, 34.55) * mm});
            skLineSegment(sketch, "E141.0.8.2", {"start": v(48.52, 34.55) * mm, "end": v(48.52, 29.93) * mm});
            skLineSegment(sketch, "E141.0.8.3", {"start": v(48.52, 29.93) * mm, "end": v(53.15, 29.93) * mm});
            skLineSegment(sketch, "E141.0.9.0", {"start": v(53.15, 17.23) * mm, "end": v(53.15, 21.85) * mm});
            skLineSegment(sketch, "E141.0.9.1", {"start": v(53.15, 21.85) * mm, "end": v(48.52, 21.85) * mm});
            skLineSegment(sketch, "E141.0.9.2", {"start": v(48.52, 21.85) * mm, "end": v(48.52, 17.23) * mm});
            skLineSegment(sketch, "E141.0.9.3", {"start": v(48.52, 17.23) * mm, "end": v(53.15, 17.23) * mm});
            skLineSegment(sketch, "E141.0.10.0", {"start": v(53.15, 4.53) * mm, "end": v(53.15, 9.15) * mm});
            skLineSegment(sketch, "E141.0.10.1", {"start": v(53.15, 9.15) * mm, "end": v(48.52, 9.15) * mm});
            skLineSegment(sketch, "E141.0.10.2", {"start": v(48.52, 9.15) * mm, "end": v(48.52, 4.53) * mm});
            skLineSegment(sketch, "E141.0.10.3", {"start": v(48.52, 4.53) * mm, "end": v(53.15, 4.53) * mm});
            skLineSegment(sketch, "E141.1.0.0", {"start": v(40.45, 131.53) * mm, "end": v(40.45, 136.15) * mm});
            skLineSegment(sketch, "E141.1.0.1", {"start": v(40.45, 136.15) * mm, "end": v(35.82, 136.15) * mm});
            skLineSegment(sketch, "E141.1.0.2", {"start": v(35.82, 136.15) * mm, "end": v(35.82, 131.53) * mm});
            skLineSegment(sketch, "E141.1.0.3", {"start": v(35.82, 131.53) * mm, "end": v(40.45, 131.53) * mm});
            skLineSegment(sketch, "E141.1.1.0", {"start": v(40.45, 118.83) * mm, "end": v(40.45, 123.45) * mm});
            skLineSegment(sketch, "E141.1.1.1", {"start": v(40.45, 123.45) * mm, "end": v(35.82, 123.45) * mm});
            skLineSegment(sketch, "E141.1.1.2", {"start": v(35.82, 123.45) * mm, "end": v(35.82, 118.83) * mm});
            skLineSegment(sketch, "E141.1.1.3", {"start": v(35.82, 118.83) * mm, "end": v(40.45, 118.83) * mm});
            skLineSegment(sketch, "E141.1.2.0", {"start": v(40.45, 106.13) * mm, "end": v(40.45, 110.75) * mm});
            skLineSegment(sketch, "E141.1.2.1", {"start": v(40.45, 110.75) * mm, "end": v(35.82, 110.75) * mm});
            skLineSegment(sketch, "E141.1.2.2", {"start": v(35.82, 110.75) * mm, "end": v(35.82, 106.13) * mm});
            skLineSegment(sketch, "E141.1.2.3", {"start": v(35.82, 106.13) * mm, "end": v(40.45, 106.13) * mm});
            skLineSegment(sketch, "E141.1.3.0", {"start": v(40.45, 93.43) * mm, "end": v(40.45, 98.05) * mm});
            skLineSegment(sketch, "E141.1.3.1", {"start": v(40.45, 98.05) * mm, "end": v(35.82, 98.05) * mm});
            skLineSegment(sketch, "E141.1.3.2", {"start": v(35.82, 98.05) * mm, "end": v(35.82, 93.43) * mm});
            skLineSegment(sketch, "E141.1.3.3", {"start": v(35.82, 93.43) * mm, "end": v(40.45, 93.43) * mm});
            skLineSegment(sketch, "E141.1.4.0", {"start": v(40.45, 80.73) * mm, "end": v(40.45, 85.35) * mm});
            skLineSegment(sketch, "E141.1.4.1", {"start": v(40.45, 85.35) * mm, "end": v(35.82, 85.35) * mm});
            skLineSegment(sketch, "E141.1.4.2", {"start": v(35.82, 85.35) * mm, "end": v(35.82, 80.73) * mm});
            skLineSegment(sketch, "E141.1.4.3", {"start": v(35.82, 80.73) * mm, "end": v(40.45, 80.73) * mm});
            skLineSegment(sketch, "E141.1.5.0", {"start": v(40.45, 68.03) * mm, "end": v(40.45, 72.65) * mm});
            skLineSegment(sketch, "E141.1.5.1", {"start": v(40.45, 72.65) * mm, "end": v(35.82, 72.65) * mm});
            skLineSegment(sketch, "E141.1.5.2", {"start": v(35.82, 72.65) * mm, "end": v(35.82, 68.03) * mm});
            skLineSegment(sketch, "E141.1.5.3", {"start": v(35.82, 68.03) * mm, "end": v(40.45, 68.03) * mm});
            skLineSegment(sketch, "E141.1.6.0", {"start": v(40.45, 55.33) * mm, "end": v(40.45, 59.95) * mm});
            skLineSegment(sketch, "E141.1.6.1", {"start": v(40.45, 59.95) * mm, "end": v(35.82, 59.95) * mm});
            skLineSegment(sketch, "E141.1.6.2", {"start": v(35.82, 59.95) * mm, "end": v(35.82, 55.33) * mm});
            skLineSegment(sketch, "E141.1.6.3", {"start": v(35.82, 55.33) * mm, "end": v(40.45, 55.33) * mm});
            skLineSegment(sketch, "E141.1.7.0", {"start": v(40.45, 42.63) * mm, "end": v(40.45, 47.25) * mm});
            skLineSegment(sketch, "E141.1.7.1", {"start": v(40.45, 47.25) * mm, "end": v(35.82, 47.25) * mm});
            skLineSegment(sketch, "E141.1.7.2", {"start": v(35.82, 47.25) * mm, "end": v(35.82, 42.63) * mm});
            skLineSegment(sketch, "E141.1.7.3", {"start": v(35.82, 42.63) * mm, "end": v(40.45, 42.63) * mm});
            skLineSegment(sketch, "E141.1.8.0", {"start": v(40.45, 29.93) * mm, "end": v(40.45, 34.55) * mm});
            skLineSegment(sketch, "E141.1.8.1", {"start": v(40.45, 34.55) * mm, "end": v(35.82, 34.55) * mm});
            skLineSegment(sketch, "E141.1.8.2", {"start": v(35.82, 34.55) * mm, "end": v(35.82, 29.93) * mm});
            skLineSegment(sketch, "E141.1.8.3", {"start": v(35.82, 29.93) * mm, "end": v(40.45, 29.93) * mm});
            skLineSegment(sketch, "E141.1.9.0", {"start": v(40.45, 17.23) * mm, "end": v(40.45, 21.85) * mm});
            skLineSegment(sketch, "E141.1.9.1", {"start": v(40.45, 21.85) * mm, "end": v(35.82, 21.85) * mm});
            skLineSegment(sketch, "E141.1.9.2", {"start": v(35.82, 21.85) * mm, "end": v(35.82, 17.23) * mm});
            skLineSegment(sketch, "E141.1.9.3", {"start": v(35.82, 17.23) * mm, "end": v(40.45, 17.23) * mm});
            skLineSegment(sketch, "E141.1.10.0", {"start": v(40.45, 4.53) * mm, "end": v(40.45, 9.15) * mm});
            skLineSegment(sketch, "E141.1.10.1", {"start": v(40.45, 9.15) * mm, "end": v(35.82, 9.15) * mm});
            skLineSegment(sketch, "E141.1.10.2", {"start": v(35.82, 9.15) * mm, "end": v(35.82, 4.53) * mm});
            skLineSegment(sketch, "E141.1.10.3", {"start": v(35.82, 4.53) * mm, "end": v(40.45, 4.53) * mm});
            skLineSegment(sketch, "E141.direction1", {"start": v(53.15, 131.53) * mm, "end": v(40.45, 131.53) * mm, "construction": true});
            skLineSegment(sketch, "E141.direction2", {"start": v(53.15, 131.53) * mm, "end": v(53.15, 118.83) * mm, "construction": true});
            skLineSegment(sketch, "E142.1.0.0", {"start": v(27.75, 4.53) * mm, "end": v(27.75, 9.15) * mm});
            skLineSegment(sketch, "E142.1.0.1", {"start": v(23.12, 4.53) * mm, "end": v(27.75, 4.53) * mm});
            skLineSegment(sketch, "E142.1.0.2", {"start": v(23.12, 9.15) * mm, "end": v(23.12, 4.53) * mm});
            skLineSegment(sketch, "E142.1.0.3", {"start": v(27.75, 9.15) * mm, "end": v(23.12, 9.15) * mm});
            skLineSegment(sketch, "E142.1.1.0", {"start": v(27.75, 17.23) * mm, "end": v(27.75, 21.85) * mm});
            skLineSegment(sketch, "E142.1.1.1", {"start": v(23.12, 17.23) * mm, "end": v(27.75, 17.23) * mm});
            skLineSegment(sketch, "E142.1.1.2", {"start": v(23.12, 21.85) * mm, "end": v(23.12, 17.23) * mm});
            skLineSegment(sketch, "E142.1.1.3", {"start": v(27.75, 21.85) * mm, "end": v(23.12, 21.85) * mm});
            skLineSegment(sketch, "E142.2.0.0", {"start": v(15.05, 4.53) * mm, "end": v(15.05, 9.15) * mm});
            skLineSegment(sketch, "E142.2.0.1", {"start": v(10.42, 4.53) * mm, "end": v(15.05, 4.53) * mm});
            skLineSegment(sketch, "E142.2.0.2", {"start": v(10.42, 9.15) * mm, "end": v(10.42, 4.53) * mm});
            skLineSegment(sketch, "E142.2.0.3", {"start": v(15.05, 9.15) * mm, "end": v(10.42, 9.15) * mm});
            skLineSegment(sketch, "E142.2.1.0", {"start": v(15.05, 17.23) * mm, "end": v(15.05, 21.85) * mm});
            skLineSegment(sketch, "E142.2.1.1", {"start": v(10.42, 17.23) * mm, "end": v(15.05, 17.23) * mm});
            skLineSegment(sketch, "E142.2.1.2", {"start": v(10.42, 21.85) * mm, "end": v(10.42, 17.23) * mm});
            skLineSegment(sketch, "E142.2.1.3", {"start": v(15.05, 21.85) * mm, "end": v(10.42, 21.85) * mm});
            skLineSegment(sketch, "E142.3.0.0", {"start": v(2.35, 4.53) * mm, "end": v(2.35, 9.15) * mm});
            skLineSegment(sketch, "E142.3.0.1", {"start": v(-2.28, 4.53) * mm, "end": v(2.35, 4.53) * mm});
            skLineSegment(sketch, "E142.3.0.2", {"start": v(-2.28, 9.15) * mm, "end": v(-2.28, 4.53) * mm});
            skLineSegment(sketch, "E142.3.0.3", {"start": v(2.35, 9.15) * mm, "end": v(-2.28, 9.15) * mm});
            skLineSegment(sketch, "E142.3.1.0", {"start": v(2.35, 17.23) * mm, "end": v(2.35, 21.85) * mm});
            skLineSegment(sketch, "E142.3.1.1", {"start": v(-2.28, 17.23) * mm, "end": v(2.35, 17.23) * mm});
            skLineSegment(sketch, "E142.3.1.2", {"start": v(-2.28, 21.85) * mm, "end": v(-2.28, 17.23) * mm});
            skLineSegment(sketch, "E142.3.1.3", {"start": v(2.35, 21.85) * mm, "end": v(-2.28, 21.85) * mm});
            skLineSegment(sketch, "E142.4.0.0", {"start": v(-10.35, 4.53) * mm, "end": v(-10.35, 9.15) * mm});
            skLineSegment(sketch, "E142.4.0.1", {"start": v(-14.98, 4.53) * mm, "end": v(-10.35, 4.53) * mm});
            skLineSegment(sketch, "E142.4.0.2", {"start": v(-14.98, 9.15) * mm, "end": v(-14.98, 4.53) * mm});
            skLineSegment(sketch, "E142.4.0.3", {"start": v(-10.35, 9.15) * mm, "end": v(-14.98, 9.15) * mm});
            skLineSegment(sketch, "E142.4.1.0", {"start": v(-10.35, 17.23) * mm, "end": v(-10.35, 21.85) * mm});
            skLineSegment(sketch, "E142.4.1.1", {"start": v(-14.98, 17.23) * mm, "end": v(-10.35, 17.23) * mm});
            skLineSegment(sketch, "E142.4.1.2", {"start": v(-14.98, 21.85) * mm, "end": v(-14.98, 17.23) * mm});
            skLineSegment(sketch, "E142.4.1.3", {"start": v(-10.35, 21.85) * mm, "end": v(-14.98, 21.85) * mm});
            skLineSegment(sketch, "E142.5.0.0", {"start": v(-23.05, 4.53) * mm, "end": v(-23.05, 9.15) * mm});
            skLineSegment(sketch, "E142.5.0.1", {"start": v(-27.68, 4.53) * mm, "end": v(-23.05, 4.53) * mm});
            skLineSegment(sketch, "E142.5.0.2", {"start": v(-27.68, 9.15) * mm, "end": v(-27.68, 4.53) * mm});
            skLineSegment(sketch, "E142.5.0.3", {"start": v(-23.05, 9.15) * mm, "end": v(-27.68, 9.15) * mm});
            skLineSegment(sketch, "E142.5.1.0", {"start": v(-23.05, 17.23) * mm, "end": v(-23.05, 21.85) * mm});
            skLineSegment(sketch, "E142.5.1.1", {"start": v(-27.68, 17.23) * mm, "end": v(-23.05, 17.23) * mm});
            skLineSegment(sketch, "E142.5.1.2", {"start": v(-27.68, 21.85) * mm, "end": v(-27.68, 17.23) * mm});
            skLineSegment(sketch, "E142.5.1.3", {"start": v(-23.05, 21.85) * mm, "end": v(-27.68, 21.85) * mm});
            skLineSegment(sketch, "E142.6.0.0", {"start": v(-35.75, 4.53) * mm, "end": v(-35.75, 9.15) * mm});
            skLineSegment(sketch, "E142.6.0.1", {"start": v(-40.38, 4.53) * mm, "end": v(-35.75, 4.53) * mm});
            skLineSegment(sketch, "E142.6.0.2", {"start": v(-40.38, 9.15) * mm, "end": v(-40.38, 4.53) * mm});
            skLineSegment(sketch, "E142.6.0.3", {"start": v(-35.75, 9.15) * mm, "end": v(-40.38, 9.15) * mm});
            skLineSegment(sketch, "E142.6.1.0", {"start": v(-35.75, 17.23) * mm, "end": v(-35.75, 21.85) * mm});
            skLineSegment(sketch, "E142.6.1.1", {"start": v(-40.38, 17.23) * mm, "end": v(-35.75, 17.23) * mm});
            skLineSegment(sketch, "E142.6.1.2", {"start": v(-40.38, 21.85) * mm, "end": v(-40.38, 17.23) * mm});
            skLineSegment(sketch, "E142.6.1.3", {"start": v(-35.75, 21.85) * mm, "end": v(-40.38, 21.85) * mm});
            skLineSegment(sketch, "E142.7.0.0", {"start": v(-48.45, 4.53) * mm, "end": v(-48.45, 9.15) * mm});
            skLineSegment(sketch, "E142.7.0.1", {"start": v(-53.08, 4.53) * mm, "end": v(-48.45, 4.53) * mm});
            skLineSegment(sketch, "E142.7.0.2", {"start": v(-53.08, 9.15) * mm, "end": v(-53.08, 4.53) * mm});
            skLineSegment(sketch, "E142.7.0.3", {"start": v(-48.45, 9.15) * mm, "end": v(-53.08, 9.15) * mm});
            skLineSegment(sketch, "E142.7.1.0", {"start": v(-48.45, 17.23) * mm, "end": v(-48.45, 21.85) * mm});
            skLineSegment(sketch, "E142.7.1.1", {"start": v(-53.08, 17.23) * mm, "end": v(-48.45, 17.23) * mm});
            skLineSegment(sketch, "E142.7.1.2", {"start": v(-53.08, 21.85) * mm, "end": v(-53.08, 17.23) * mm});
            skLineSegment(sketch, "E142.7.1.3", {"start": v(-48.45, 21.85) * mm, "end": v(-53.08, 21.85) * mm});
            skLineSegment(sketch, "E142.8.0.0", {"start": v(-61.15, 4.53) * mm, "end": v(-61.15, 9.15) * mm});
            skLineSegment(sketch, "E142.8.0.1", {"start": v(-65.78, 4.53) * mm, "end": v(-61.15, 4.53) * mm});
            skLineSegment(sketch, "E142.8.0.2", {"start": v(-65.78, 9.15) * mm, "end": v(-65.78, 4.53) * mm});
            skLineSegment(sketch, "E142.8.0.3", {"start": v(-61.15, 9.15) * mm, "end": v(-65.78, 9.15) * mm});
            skLineSegment(sketch, "E142.8.1.0", {"start": v(-61.15, 17.23) * mm, "end": v(-61.15, 21.85) * mm});
            skLineSegment(sketch, "E142.8.1.1", {"start": v(-65.78, 17.23) * mm, "end": v(-61.15, 17.23) * mm});
            skLineSegment(sketch, "E142.8.1.2", {"start": v(-65.78, 21.85) * mm, "end": v(-65.78, 17.23) * mm});
            skLineSegment(sketch, "E142.8.1.3", {"start": v(-61.15, 21.85) * mm, "end": v(-65.78, 21.85) * mm});
            skLineSegment(sketch, "E142.9.0.0", {"start": v(-73.85, 4.53) * mm, "end": v(-73.85, 9.15) * mm});
            skLineSegment(sketch, "E142.9.0.1", {"start": v(-78.48, 4.53) * mm, "end": v(-73.85, 4.53) * mm});
            skLineSegment(sketch, "E142.9.0.2", {"start": v(-78.48, 9.15) * mm, "end": v(-78.48, 4.53) * mm});
            skLineSegment(sketch, "E142.9.0.3", {"start": v(-73.85, 9.15) * mm, "end": v(-78.48, 9.15) * mm});
            skLineSegment(sketch, "E142.9.1.0", {"start": v(-73.85, 17.23) * mm, "end": v(-73.85, 21.85) * mm});
            skLineSegment(sketch, "E142.9.1.1", {"start": v(-78.48, 17.23) * mm, "end": v(-73.85, 17.23) * mm});
            skLineSegment(sketch, "E142.9.1.2", {"start": v(-78.48, 21.85) * mm, "end": v(-78.48, 17.23) * mm});
            skLineSegment(sketch, "E142.9.1.3", {"start": v(-73.85, 21.85) * mm, "end": v(-78.48, 21.85) * mm});
            skLineSegment(sketch, "E142.10.0.0", {"start": v(-86.55, 4.53) * mm, "end": v(-86.55, 9.15) * mm});
            skLineSegment(sketch, "E142.10.0.1", {"start": v(-91.18, 4.53) * mm, "end": v(-86.55, 4.53) * mm});
            skLineSegment(sketch, "E142.10.0.2", {"start": v(-91.18, 9.15) * mm, "end": v(-91.18, 4.53) * mm});
            skLineSegment(sketch, "E142.10.0.3", {"start": v(-86.55, 9.15) * mm, "end": v(-91.18, 9.15) * mm});
            skLineSegment(sketch, "E142.10.1.0", {"start": v(-86.55, 17.23) * mm, "end": v(-86.55, 21.85) * mm});
            skLineSegment(sketch, "E142.10.1.1", {"start": v(-91.18, 17.23) * mm, "end": v(-86.55, 17.23) * mm});
            skLineSegment(sketch, "E142.10.1.2", {"start": v(-91.18, 21.85) * mm, "end": v(-91.18, 17.23) * mm});
            skLineSegment(sketch, "E142.10.1.3", {"start": v(-86.55, 21.85) * mm, "end": v(-91.18, 21.85) * mm});
            skLineSegment(sketch, "E142.direction1", {"start": v(35.82, 4.53) * mm, "end": v(23.12, 4.53) * mm, "construction": true});
            skLineSegment(sketch, "E142.direction2", {"start": v(35.82, 4.53) * mm, "end": v(35.82, 17.23) * mm, "construction": true});
            skLineSegment(sketch, "E143.0.1.0", {"start": v(-86.55, 34.55) * mm, "end": v(-91.18, 34.55) * mm});
            skLineSegment(sketch, "E143.0.1.1", {"start": v(-91.18, 34.55) * mm, "end": v(-91.18, 29.93) * mm});
            skLineSegment(sketch, "E143.0.1.2", {"start": v(-91.18, 29.93) * mm, "end": v(-86.55, 29.93) * mm});
            skLineSegment(sketch, "E143.0.1.3", {"start": v(-86.55, 29.93) * mm, "end": v(-86.55, 34.55) * mm});
            skLineSegment(sketch, "E143.0.2.0", {"start": v(-86.55, 47.25) * mm, "end": v(-91.18, 47.25) * mm});
            skLineSegment(sketch, "E143.0.2.1", {"start": v(-91.18, 47.25) * mm, "end": v(-91.18, 42.63) * mm});
            skLineSegment(sketch, "E143.0.2.2", {"start": v(-91.18, 42.63) * mm, "end": v(-86.55, 42.63) * mm});
            skLineSegment(sketch, "E143.0.2.3", {"start": v(-86.55, 42.63) * mm, "end": v(-86.55, 47.25) * mm});
            skLineSegment(sketch, "E143.0.3.0", {"start": v(-86.55, 59.95) * mm, "end": v(-91.18, 59.95) * mm});
            skLineSegment(sketch, "E143.0.3.1", {"start": v(-91.18, 59.95) * mm, "end": v(-91.18, 55.33) * mm});
            skLineSegment(sketch, "E143.0.3.2", {"start": v(-91.18, 55.33) * mm, "end": v(-86.55, 55.33) * mm});
            skLineSegment(sketch, "E143.0.3.3", {"start": v(-86.55, 55.33) * mm, "end": v(-86.55, 59.95) * mm});
            skLineSegment(sketch, "E143.0.4.0", {"start": v(-86.55, 72.65) * mm, "end": v(-91.18, 72.65) * mm});
            skLineSegment(sketch, "E143.0.4.1", {"start": v(-91.18, 72.65) * mm, "end": v(-91.18, 68.03) * mm});
            skLineSegment(sketch, "E143.0.4.2", {"start": v(-91.18, 68.03) * mm, "end": v(-86.55, 68.03) * mm});
            skLineSegment(sketch, "E143.0.4.3", {"start": v(-86.55, 68.03) * mm, "end": v(-86.55, 72.65) * mm});
            skLineSegment(sketch, "E143.0.5.0", {"start": v(-86.55, 85.35) * mm, "end": v(-91.18, 85.35) * mm});
            skLineSegment(sketch, "E143.0.5.1", {"start": v(-91.18, 85.35) * mm, "end": v(-91.18, 80.73) * mm});
            skLineSegment(sketch, "E143.0.5.2", {"start": v(-91.18, 80.73) * mm, "end": v(-86.55, 80.73) * mm});
            skLineSegment(sketch, "E143.0.5.3", {"start": v(-86.55, 80.73) * mm, "end": v(-86.55, 85.35) * mm});
            skLineSegment(sketch, "E143.0.6.0", {"start": v(-86.55, 98.05) * mm, "end": v(-91.18, 98.05) * mm});
            skLineSegment(sketch, "E143.0.6.1", {"start": v(-91.18, 98.05) * mm, "end": v(-91.18, 93.43) * mm});
            skLineSegment(sketch, "E143.0.6.2", {"start": v(-91.18, 93.43) * mm, "end": v(-86.55, 93.43) * mm});
            skLineSegment(sketch, "E143.0.6.3", {"start": v(-86.55, 93.43) * mm, "end": v(-86.55, 98.05) * mm});
            skLineSegment(sketch, "E143.0.7.0", {"start": v(-86.55, 110.75) * mm, "end": v(-91.18, 110.75) * mm});
            skLineSegment(sketch, "E143.0.7.1", {"start": v(-91.18, 110.75) * mm, "end": v(-91.18, 106.13) * mm});
            skLineSegment(sketch, "E143.0.7.2", {"start": v(-91.18, 106.13) * mm, "end": v(-86.55, 106.13) * mm});
            skLineSegment(sketch, "E143.0.7.3", {"start": v(-86.55, 106.13) * mm, "end": v(-86.55, 110.75) * mm});
            skLineSegment(sketch, "E143.0.8.0", {"start": v(-86.55, 123.45) * mm, "end": v(-91.18, 123.45) * mm});
            skLineSegment(sketch, "E143.0.8.1", {"start": v(-91.18, 123.45) * mm, "end": v(-91.18, 118.83) * mm});
            skLineSegment(sketch, "E143.0.8.2", {"start": v(-91.18, 118.83) * mm, "end": v(-86.55, 118.83) * mm});
            skLineSegment(sketch, "E143.0.8.3", {"start": v(-86.55, 118.83) * mm, "end": v(-86.55, 123.45) * mm});
            skLineSegment(sketch, "E143.0.9.0", {"start": v(-86.55, 136.15) * mm, "end": v(-91.18, 136.15) * mm});
            skLineSegment(sketch, "E143.0.9.1", {"start": v(-91.18, 136.15) * mm, "end": v(-91.18, 131.53) * mm});
            skLineSegment(sketch, "E143.0.9.2", {"start": v(-91.18, 131.53) * mm, "end": v(-86.55, 131.53) * mm});
            skLineSegment(sketch, "E143.0.9.3", {"start": v(-86.55, 131.53) * mm, "end": v(-86.55, 136.15) * mm});
            skLineSegment(sketch, "E143.1.1.0", {"start": v(-73.85, 34.55) * mm, "end": v(-78.48, 34.55) * mm});
            skLineSegment(sketch, "E143.1.1.1", {"start": v(-78.48, 34.55) * mm, "end": v(-78.48, 29.93) * mm});
            skLineSegment(sketch, "E143.1.1.2", {"start": v(-78.48, 29.93) * mm, "end": v(-73.85, 29.93) * mm});
            skLineSegment(sketch, "E143.1.1.3", {"start": v(-73.85, 29.93) * mm, "end": v(-73.85, 34.55) * mm});
            skLineSegment(sketch, "E143.1.2.0", {"start": v(-73.85, 47.25) * mm, "end": v(-78.48, 47.25) * mm});
            skLineSegment(sketch, "E143.1.2.1", {"start": v(-78.48, 47.25) * mm, "end": v(-78.48, 42.63) * mm});
            skLineSegment(sketch, "E143.1.2.2", {"start": v(-78.48, 42.63) * mm, "end": v(-73.85, 42.63) * mm});
            skLineSegment(sketch, "E143.1.2.3", {"start": v(-73.85, 42.63) * mm, "end": v(-73.85, 47.25) * mm});
            skLineSegment(sketch, "E143.1.3.0", {"start": v(-73.85, 59.95) * mm, "end": v(-78.48, 59.95) * mm});
            skLineSegment(sketch, "E143.1.3.1", {"start": v(-78.48, 59.95) * mm, "end": v(-78.48, 55.33) * mm});
            skLineSegment(sketch, "E143.1.3.2", {"start": v(-78.48, 55.33) * mm, "end": v(-73.85, 55.33) * mm});
            skLineSegment(sketch, "E143.1.3.3", {"start": v(-73.85, 55.33) * mm, "end": v(-73.85, 59.95) * mm});
            skLineSegment(sketch, "E143.1.4.0", {"start": v(-73.85, 72.65) * mm, "end": v(-78.48, 72.65) * mm});
            skLineSegment(sketch, "E143.1.4.1", {"start": v(-78.48, 72.65) * mm, "end": v(-78.48, 68.03) * mm});
            skLineSegment(sketch, "E143.1.4.2", {"start": v(-78.48, 68.03) * mm, "end": v(-73.85, 68.03) * mm});
            skLineSegment(sketch, "E143.1.4.3", {"start": v(-73.85, 68.03) * mm, "end": v(-73.85, 72.65) * mm});
            skLineSegment(sketch, "E143.1.5.0", {"start": v(-73.85, 85.35) * mm, "end": v(-78.48, 85.35) * mm});
            skLineSegment(sketch, "E143.1.5.1", {"start": v(-78.48, 85.35) * mm, "end": v(-78.48, 80.73) * mm});
            skLineSegment(sketch, "E143.1.5.2", {"start": v(-78.48, 80.73) * mm, "end": v(-73.85, 80.73) * mm});
            skLineSegment(sketch, "E143.1.5.3", {"start": v(-73.85, 80.73) * mm, "end": v(-73.85, 85.35) * mm});
            skLineSegment(sketch, "E143.1.6.0", {"start": v(-73.85, 98.05) * mm, "end": v(-78.48, 98.05) * mm});
            skLineSegment(sketch, "E143.1.6.1", {"start": v(-78.48, 98.05) * mm, "end": v(-78.48, 93.43) * mm});
            skLineSegment(sketch, "E143.1.6.2", {"start": v(-78.48, 93.43) * mm, "end": v(-73.85, 93.43) * mm});
            skLineSegment(sketch, "E143.1.6.3", {"start": v(-73.85, 93.43) * mm, "end": v(-73.85, 98.05) * mm});
            skLineSegment(sketch, "E143.1.7.0", {"start": v(-73.85, 110.75) * mm, "end": v(-78.48, 110.75) * mm});
            skLineSegment(sketch, "E143.1.7.1", {"start": v(-78.48, 110.75) * mm, "end": v(-78.48, 106.13) * mm});
            skLineSegment(sketch, "E143.1.7.2", {"start": v(-78.48, 106.13) * mm, "end": v(-73.85, 106.13) * mm});
            skLineSegment(sketch, "E143.1.7.3", {"start": v(-73.85, 106.13) * mm, "end": v(-73.85, 110.75) * mm});
            skLineSegment(sketch, "E143.1.8.0", {"start": v(-73.85, 123.45) * mm, "end": v(-78.48, 123.45) * mm});
            skLineSegment(sketch, "E143.1.8.1", {"start": v(-78.48, 123.45) * mm, "end": v(-78.48, 118.83) * mm});
            skLineSegment(sketch, "E143.1.8.2", {"start": v(-78.48, 118.83) * mm, "end": v(-73.85, 118.83) * mm});
            skLineSegment(sketch, "E143.1.8.3", {"start": v(-73.85, 118.83) * mm, "end": v(-73.85, 123.45) * mm});
            skLineSegment(sketch, "E143.1.9.0", {"start": v(-73.85, 136.15) * mm, "end": v(-78.48, 136.15) * mm});
            skLineSegment(sketch, "E143.1.9.1", {"start": v(-78.48, 136.15) * mm, "end": v(-78.48, 131.53) * mm});
            skLineSegment(sketch, "E143.1.9.2", {"start": v(-78.48, 131.53) * mm, "end": v(-73.85, 131.53) * mm});
            skLineSegment(sketch, "E143.1.9.3", {"start": v(-73.85, 131.53) * mm, "end": v(-73.85, 136.15) * mm});
            skLineSegment(sketch, "E143.direction1", {"start": v(-91.18, 17.23) * mm, "end": v(-78.48, 17.23) * mm, "construction": true});
            skLineSegment(sketch, "E144.1.0.0", {"start": v(27.75, 131.53) * mm, "end": v(27.75, 136.15) * mm});
            skLineSegment(sketch, "E144.1.0.1", {"start": v(27.75, 136.15) * mm, "end": v(23.12, 136.15) * mm});
            skLineSegment(sketch, "E144.1.0.2", {"start": v(23.12, 136.15) * mm, "end": v(23.12, 131.53) * mm});
            skLineSegment(sketch, "E144.1.0.3", {"start": v(23.12, 131.53) * mm, "end": v(27.75, 131.53) * mm});
            skLineSegment(sketch, "E144.1.1.0", {"start": v(27.75, 118.83) * mm, "end": v(27.75, 123.45) * mm});
            skLineSegment(sketch, "E144.1.1.1", {"start": v(27.75, 123.45) * mm, "end": v(23.12, 123.45) * mm});
            skLineSegment(sketch, "E144.1.1.2", {"start": v(23.12, 123.45) * mm, "end": v(23.12, 118.83) * mm});
            skLineSegment(sketch, "E144.1.1.3", {"start": v(23.12, 118.83) * mm, "end": v(27.75, 118.83) * mm});
            skLineSegment(sketch, "E144.2.0.0", {"start": v(15.05, 131.53) * mm, "end": v(15.05, 136.15) * mm});
            skLineSegment(sketch, "E144.2.0.1", {"start": v(15.05, 136.15) * mm, "end": v(10.42, 136.15) * mm});
            skLineSegment(sketch, "E144.2.0.2", {"start": v(10.42, 136.15) * mm, "end": v(10.42, 131.53) * mm});
            skLineSegment(sketch, "E144.2.0.3", {"start": v(10.42, 131.53) * mm, "end": v(15.05, 131.53) * mm});
            skLineSegment(sketch, "E144.2.1.0", {"start": v(15.05, 118.83) * mm, "end": v(15.05, 123.45) * mm});
            skLineSegment(sketch, "E144.2.1.1", {"start": v(15.05, 123.45) * mm, "end": v(10.42, 123.45) * mm});
            skLineSegment(sketch, "E144.2.1.2", {"start": v(10.42, 123.45) * mm, "end": v(10.42, 118.83) * mm});
            skLineSegment(sketch, "E144.2.1.3", {"start": v(10.42, 118.83) * mm, "end": v(15.05, 118.83) * mm});
            skLineSegment(sketch, "E144.3.0.0", {"start": v(2.35, 131.53) * mm, "end": v(2.35, 136.15) * mm});
            skLineSegment(sketch, "E144.3.0.1", {"start": v(2.35, 136.15) * mm, "end": v(-2.28, 136.15) * mm});
            skLineSegment(sketch, "E144.3.0.2", {"start": v(-2.28, 136.15) * mm, "end": v(-2.28, 131.53) * mm});
            skLineSegment(sketch, "E144.3.0.3", {"start": v(-2.28, 131.53) * mm, "end": v(2.35, 131.53) * mm});
            skLineSegment(sketch, "E144.3.1.0", {"start": v(2.35, 118.83) * mm, "end": v(2.35, 123.45) * mm});
            skLineSegment(sketch, "E144.3.1.1", {"start": v(2.35, 123.45) * mm, "end": v(-2.28, 123.45) * mm});
            skLineSegment(sketch, "E144.3.1.2", {"start": v(-2.28, 123.45) * mm, "end": v(-2.28, 118.83) * mm});
            skLineSegment(sketch, "E144.3.1.3", {"start": v(-2.28, 118.83) * mm, "end": v(2.35, 118.83) * mm});
            skLineSegment(sketch, "E144.4.0.0", {"start": v(-10.35, 131.53) * mm, "end": v(-10.35, 136.15) * mm});
            skLineSegment(sketch, "E144.4.0.1", {"start": v(-10.35, 136.15) * mm, "end": v(-14.98, 136.15) * mm});
            skLineSegment(sketch, "E144.4.0.2", {"start": v(-14.98, 136.15) * mm, "end": v(-14.98, 131.53) * mm});
            skLineSegment(sketch, "E144.4.0.3", {"start": v(-14.98, 131.53) * mm, "end": v(-10.35, 131.53) * mm});
            skLineSegment(sketch, "E144.4.1.0", {"start": v(-10.35, 118.83) * mm, "end": v(-10.35, 123.45) * mm});
            skLineSegment(sketch, "E144.4.1.1", {"start": v(-10.35, 123.45) * mm, "end": v(-14.98, 123.45) * mm});
            skLineSegment(sketch, "E144.4.1.2", {"start": v(-14.98, 123.45) * mm, "end": v(-14.98, 118.83) * mm});
            skLineSegment(sketch, "E144.4.1.3", {"start": v(-14.98, 118.83) * mm, "end": v(-10.35, 118.83) * mm});
            skLineSegment(sketch, "E144.5.0.0", {"start": v(-23.05, 131.53) * mm, "end": v(-23.05, 136.15) * mm});
            skLineSegment(sketch, "E144.5.0.1", {"start": v(-23.05, 136.15) * mm, "end": v(-27.68, 136.15) * mm});
            skLineSegment(sketch, "E144.5.0.2", {"start": v(-27.68, 136.15) * mm, "end": v(-27.68, 131.53) * mm});
            skLineSegment(sketch, "E144.5.0.3", {"start": v(-27.68, 131.53) * mm, "end": v(-23.05, 131.53) * mm});
            skLineSegment(sketch, "E144.5.1.0", {"start": v(-23.05, 118.83) * mm, "end": v(-23.05, 123.45) * mm});
            skLineSegment(sketch, "E144.5.1.1", {"start": v(-23.05, 123.45) * mm, "end": v(-27.68, 123.45) * mm});
            skLineSegment(sketch, "E144.5.1.2", {"start": v(-27.68, 123.45) * mm, "end": v(-27.68, 118.83) * mm});
            skLineSegment(sketch, "E144.5.1.3", {"start": v(-27.68, 118.83) * mm, "end": v(-23.05, 118.83) * mm});
            skLineSegment(sketch, "E144.6.0.0", {"start": v(-35.75, 131.53) * mm, "end": v(-35.75, 136.15) * mm});
            skLineSegment(sketch, "E144.6.0.1", {"start": v(-35.75, 136.15) * mm, "end": v(-40.38, 136.15) * mm});
            skLineSegment(sketch, "E144.6.0.2", {"start": v(-40.38, 136.15) * mm, "end": v(-40.38, 131.53) * mm});
            skLineSegment(sketch, "E144.6.0.3", {"start": v(-40.38, 131.53) * mm, "end": v(-35.75, 131.53) * mm});
            skLineSegment(sketch, "E144.6.1.0", {"start": v(-35.75, 118.83) * mm, "end": v(-35.75, 123.45) * mm});
            skLineSegment(sketch, "E144.6.1.1", {"start": v(-35.75, 123.45) * mm, "end": v(-40.38, 123.45) * mm});
            skLineSegment(sketch, "E144.6.1.2", {"start": v(-40.38, 123.45) * mm, "end": v(-40.38, 118.83) * mm});
            skLineSegment(sketch, "E144.6.1.3", {"start": v(-40.38, 118.83) * mm, "end": v(-35.75, 118.83) * mm});
            skLineSegment(sketch, "E144.7.0.0", {"start": v(-48.45, 131.53) * mm, "end": v(-48.45, 136.15) * mm});
            skLineSegment(sketch, "E144.7.0.1", {"start": v(-48.45, 136.15) * mm, "end": v(-53.08, 136.15) * mm});
            skLineSegment(sketch, "E144.7.0.2", {"start": v(-53.08, 136.15) * mm, "end": v(-53.08, 131.53) * mm});
            skLineSegment(sketch, "E144.7.0.3", {"start": v(-53.08, 131.53) * mm, "end": v(-48.45, 131.53) * mm});
            skLineSegment(sketch, "E144.7.1.0", {"start": v(-48.45, 118.83) * mm, "end": v(-48.45, 123.45) * mm});
            skLineSegment(sketch, "E144.7.1.1", {"start": v(-48.45, 123.45) * mm, "end": v(-53.08, 123.45) * mm});
            skLineSegment(sketch, "E144.7.1.2", {"start": v(-53.08, 123.45) * mm, "end": v(-53.08, 118.83) * mm});
            skLineSegment(sketch, "E144.7.1.3", {"start": v(-53.08, 118.83) * mm, "end": v(-48.45, 118.83) * mm});
            skLineSegment(sketch, "E144.8.0.0", {"start": v(-61.15, 131.53) * mm, "end": v(-61.15, 136.15) * mm});
            skLineSegment(sketch, "E144.8.0.1", {"start": v(-61.15, 136.15) * mm, "end": v(-65.78, 136.15) * mm});
            skLineSegment(sketch, "E144.8.0.2", {"start": v(-65.78, 136.15) * mm, "end": v(-65.78, 131.53) * mm});
            skLineSegment(sketch, "E144.8.0.3", {"start": v(-65.78, 131.53) * mm, "end": v(-61.15, 131.53) * mm});
            skLineSegment(sketch, "E144.8.1.0", {"start": v(-61.15, 118.83) * mm, "end": v(-61.15, 123.45) * mm});
            skLineSegment(sketch, "E144.8.1.1", {"start": v(-61.15, 123.45) * mm, "end": v(-65.78, 123.45) * mm});
            skLineSegment(sketch, "E144.8.1.2", {"start": v(-65.78, 123.45) * mm, "end": v(-65.78, 118.83) * mm});
            skLineSegment(sketch, "E144.8.1.3", {"start": v(-65.78, 118.83) * mm, "end": v(-61.15, 118.83) * mm});
            skLineSegment(sketch, "E144.direction1", {"start": v(40.45, 131.53) * mm, "end": v(27.75, 131.53) * mm, "construction": true});
            skLineSegment(sketch, "E144.direction2", {"start": v(40.45, 131.53) * mm, "end": v(40.45, 118.83) * mm, "construction": true});
            skLineSegment(sketch, "E145.bottom", {"start": v(18.17, 103.64) * mm, "end": v(21.35, 103.64) * mm});
            skLineSegment(sketch, "E145.top", {"start": v(18.17, 100.46) * mm, "end": v(21.35, 100.46) * mm});
            skLineSegment(sketch, "E145.left", {"start": v(18.17, 103.64) * mm, "end": v(18.17, 100.46) * mm});
            skLineSegment(sketch, "E145.right", {"start": v(21.35, 103.64) * mm, "end": v(21.35, 100.46) * mm});
            skLineSegment(sketch, "E146.0.1.0", {"start": v(21.35, 38.64) * mm, "end": v(21.35, 35.46) * mm});
            skLineSegment(sketch, "E146.0.1.1", {"start": v(18.17, 38.64) * mm, "end": v(21.35, 38.64) * mm});
            skLineSegment(sketch, "E146.0.1.2", {"start": v(18.17, 38.64) * mm, "end": v(18.17, 35.46) * mm});
            skLineSegment(sketch, "E146.0.1.3", {"start": v(18.17, 35.46) * mm, "end": v(21.35, 35.46) * mm});
            skLineSegment(sketch, "E146.direction1", {"start": v(21.35, 100.46) * mm, "end": v(37.5, 100.46) * mm, "construction": true});
            skLineSegment(sketch, "E146.direction2", {"start": v(21.35, 100.46) * mm, "end": v(21.35, 35.46) * mm, "construction": true});
            skLineSegment(sketch, "E147.1.0.0", {"start": v(-57.61, 103.64) * mm, "end": v(-57.61, 100.46) * mm});
            skLineSegment(sketch, "E147.1.0.1", {"start": v(-60.79, 103.64) * mm, "end": v(-57.61, 103.64) * mm});
            skLineSegment(sketch, "E147.1.0.2", {"start": v(-60.79, 103.64) * mm, "end": v(-60.79, 100.46) * mm});
            skLineSegment(sketch, "E147.1.0.3", {"start": v(-60.79, 100.46) * mm, "end": v(-57.61, 100.46) * mm});
            skLineSegment(sketch, "E147.direction1", {"start": v(21.35, 100.46) * mm, "end": v(-57.61, 100.46) * mm, "construction": true});
            skLineSegment(sketch, "E148.0.1.0", {"start": v(-57.61, 45.82) * mm, "end": v(-57.61, 42.65) * mm});
            skLineSegment(sketch, "E148.0.1.1", {"start": v(-60.79, 45.82) * mm, "end": v(-57.61, 45.82) * mm});
            skLineSegment(sketch, "E148.0.1.2", {"start": v(-60.79, 45.82) * mm, "end": v(-60.79, 42.65) * mm});
            skLineSegment(sketch, "E148.0.1.3", {"start": v(-60.79, 42.65) * mm, "end": v(-57.61, 42.65) * mm});
            skLineSegment(sketch, "E148.direction1", {"start": v(-57.61, 100.46) * mm, "end": v(-31.7, 100.46) * mm, "construction": true});
            skLineSegment(sketch, "E148.direction2", {"start": v(-57.61, 100.46) * mm, "end": v(-57.61, 42.65) * mm, "construction": true});
            skCircle(sketch, "E149", {"center": v(-62.22, 74.72) * mm, "radius": 6.35 * mm});
            skLineSegment(sketch, "E150", {"start": v(-62.22, 74.72) * mm, "end": v(25.41, 74.72) * mm});
            skCircle(sketch, "E151", {"center": v(25.41, 74.72) * mm, "radius": 6.35 * mm});
            skSolve(sketch);
        }
        {
            var Q0;
            Q0 = qSketchRegion(id + "F31", true);
            extrude(context, id + "F32", {"entities" : qUnion([Q0]), "depth" : 3.8 * mm});
        }
        {
            var Q0;
            Q0=makeQuery(id+"F2.opExtrude","SWEPT_FACE",FACE,{"disambiguationData":[OSD([sQuery(id+"F0.wireOp",EDGE,"E1")])]});
            var sketch = newSketch(context, id + "F33", { "sketchPlane" : qUnion([Q0])});
            skLineSegment(sketch, "E152", {"start": v(-196.31, 3) * mm, "end": v(-196.31, 34.75) * mm});
            skLineSegment(sketch, "E153", {"start": v(45.66, 3) * mm, "end": v(45.66, 34.75) * mm});
            skLineSegment(sketch, "E154", {"start": v(39.31, 41.1) * mm, "end": v(-189.96, 41.1) * mm});
            skLineSegment(sketch, "E155", {"start": v(-196.31, 3) * mm, "end": v(45.66, 3) * mm});
            skLineSegment(sketch, "E156.bottom", {"start": v(-186.15, 37.06) * mm, "end": v(-181.53, 37.06) * mm});
            skLineSegment(sketch, "E156.top", {"start": v(-186.15, 32.44) * mm, "end": v(-181.53, 32.44) * mm});
            skLineSegment(sketch, "E156.left", {"start": v(-186.15, 37.06) * mm, "end": v(-186.15, 32.44) * mm});
            skLineSegment(sketch, "E156.right", {"start": v(-181.53, 37.06) * mm, "end": v(-181.53, 32.44) * mm});
            skLineSegment(sketch, "E157.0.1.0", {"start": v(-181.53, 24.36) * mm, "end": v(-181.53, 19.74) * mm});
            skLineSegment(sketch, "E157.0.1.1", {"start": v(-186.15, 24.36) * mm, "end": v(-181.53, 24.36) * mm});
            skLineSegment(sketch, "E157.0.1.2", {"start": v(-186.15, 24.36) * mm, "end": v(-186.15, 19.74) * mm});
            skLineSegment(sketch, "E157.0.1.3", {"start": v(-186.15, 19.74) * mm, "end": v(-181.53, 19.74) * mm});
            skLineSegment(sketch, "E157.0.2.0", {"start": v(-181.53, 11.66) * mm, "end": v(-181.53, 7.04) * mm});
            skLineSegment(sketch, "E157.0.2.1", {"start": v(-186.15, 11.66) * mm, "end": v(-181.53, 11.66) * mm});
            skLineSegment(sketch, "E157.0.2.2", {"start": v(-186.15, 11.66) * mm, "end": v(-186.15, 7.04) * mm});
            skLineSegment(sketch, "E157.0.2.3", {"start": v(-186.15, 7.04) * mm, "end": v(-181.53, 7.04) * mm});
            skLineSegment(sketch, "E157.1.0.0", {"start": v(-168.83, 37.06) * mm, "end": v(-168.83, 32.44) * mm});
            skLineSegment(sketch, "E157.1.0.1", {"start": v(-173.45, 37.06) * mm, "end": v(-168.83, 37.06) * mm});
            skLineSegment(sketch, "E157.1.0.2", {"start": v(-173.45, 37.06) * mm, "end": v(-173.45, 32.44) * mm});
            skLineSegment(sketch, "E157.1.0.3", {"start": v(-173.45, 32.44) * mm, "end": v(-168.83, 32.44) * mm});
            skLineSegment(sketch, "E157.1.1.0", {"start": v(-168.83, 24.36) * mm, "end": v(-168.83, 19.74) * mm});
            skLineSegment(sketch, "E157.1.1.1", {"start": v(-173.45, 24.36) * mm, "end": v(-168.83, 24.36) * mm});
            skLineSegment(sketch, "E157.1.1.2", {"start": v(-173.45, 24.36) * mm, "end": v(-173.45, 19.74) * mm});
            skLineSegment(sketch, "E157.1.1.3", {"start": v(-173.45, 19.74) * mm, "end": v(-168.83, 19.74) * mm});
            skLineSegment(sketch, "E157.1.2.0", {"start": v(-168.83, 11.66) * mm, "end": v(-168.83, 7.04) * mm});
            skLineSegment(sketch, "E157.1.2.1", {"start": v(-173.45, 11.66) * mm, "end": v(-168.83, 11.66) * mm});
            skLineSegment(sketch, "E157.1.2.2", {"start": v(-173.45, 11.66) * mm, "end": v(-173.45, 7.04) * mm});
            skLineSegment(sketch, "E157.1.2.3", {"start": v(-173.45, 7.04) * mm, "end": v(-168.83, 7.04) * mm});
            skLineSegment(sketch, "E157.2.0.0", {"start": v(-156.13, 37.06) * mm, "end": v(-156.13, 32.44) * mm});
            skLineSegment(sketch, "E157.2.0.1", {"start": v(-160.75, 37.06) * mm, "end": v(-156.13, 37.06) * mm});
            skLineSegment(sketch, "E157.2.0.2", {"start": v(-160.75, 37.06) * mm, "end": v(-160.75, 32.44) * mm});
            skLineSegment(sketch, "E157.2.0.3", {"start": v(-160.75, 32.44) * mm, "end": v(-156.13, 32.44) * mm});
            skLineSegment(sketch, "E157.2.1.0", {"start": v(-156.13, 24.36) * mm, "end": v(-156.13, 19.74) * mm});
            skLineSegment(sketch, "E157.2.1.1", {"start": v(-160.75, 24.36) * mm, "end": v(-156.13, 24.36) * mm});
            skLineSegment(sketch, "E157.2.1.2", {"start": v(-160.75, 24.36) * mm, "end": v(-160.75, 19.74) * mm});
            skLineSegment(sketch, "E157.2.1.3", {"start": v(-160.75, 19.74) * mm, "end": v(-156.13, 19.74) * mm});
            skLineSegment(sketch, "E157.2.2.0", {"start": v(-156.13, 11.66) * mm, "end": v(-156.13, 7.04) * mm});
            skLineSegment(sketch, "E157.2.2.1", {"start": v(-160.75, 11.66) * mm, "end": v(-156.13, 11.66) * mm});
            skLineSegment(sketch, "E157.2.2.2", {"start": v(-160.75, 11.66) * mm, "end": v(-160.75, 7.04) * mm});
            skLineSegment(sketch, "E157.2.2.3", {"start": v(-160.75, 7.04) * mm, "end": v(-156.13, 7.04) * mm});
            skLineSegment(sketch, "E157.3.0.0", {"start": v(-143.43, 37.06) * mm, "end": v(-143.43, 32.44) * mm});
            skLineSegment(sketch, "E157.3.0.1", {"start": v(-148.05, 37.06) * mm, "end": v(-143.43, 37.06) * mm});
            skLineSegment(sketch, "E157.3.0.2", {"start": v(-148.05, 37.06) * mm, "end": v(-148.05, 32.44) * mm});
            skLineSegment(sketch, "E157.3.0.3", {"start": v(-148.05, 32.44) * mm, "end": v(-143.43, 32.44) * mm});
            skLineSegment(sketch, "E157.3.1.0", {"start": v(-143.43, 24.36) * mm, "end": v(-143.43, 19.74) * mm});
            skLineSegment(sketch, "E157.3.1.1", {"start": v(-148.05, 24.36) * mm, "end": v(-143.43, 24.36) * mm});
            skLineSegment(sketch, "E157.3.1.2", {"start": v(-148.05, 24.36) * mm, "end": v(-148.05, 19.74) * mm});
            skLineSegment(sketch, "E157.3.1.3", {"start": v(-148.05, 19.74) * mm, "end": v(-143.43, 19.74) * mm});
            skLineSegment(sketch, "E157.3.2.0", {"start": v(-143.43, 11.66) * mm, "end": v(-143.43, 7.04) * mm});
            skLineSegment(sketch, "E157.3.2.1", {"start": v(-148.05, 11.66) * mm, "end": v(-143.43, 11.66) * mm});
            skLineSegment(sketch, "E157.3.2.2", {"start": v(-148.05, 11.66) * mm, "end": v(-148.05, 7.04) * mm});
            skLineSegment(sketch, "E157.3.2.3", {"start": v(-148.05, 7.04) * mm, "end": v(-143.43, 7.04) * mm});
            skLineSegment(sketch, "E157.4.0.0", {"start": v(-130.73, 37.06) * mm, "end": v(-130.73, 32.44) * mm});
            skLineSegment(sketch, "E157.4.0.1", {"start": v(-135.35, 37.06) * mm, "end": v(-130.73, 37.06) * mm});
            skLineSegment(sketch, "E157.4.0.2", {"start": v(-135.35, 37.06) * mm, "end": v(-135.35, 32.44) * mm});
            skLineSegment(sketch, "E157.4.0.3", {"start": v(-135.35, 32.44) * mm, "end": v(-130.73, 32.44) * mm});
            skLineSegment(sketch, "E157.4.1.0", {"start": v(-130.73, 24.36) * mm, "end": v(-130.73, 19.74) * mm});
            skLineSegment(sketch, "E157.4.1.1", {"start": v(-135.35, 24.36) * mm, "end": v(-130.73, 24.36) * mm});
            skLineSegment(sketch, "E157.4.1.2", {"start": v(-135.35, 24.36) * mm, "end": v(-135.35, 19.74) * mm});
            skLineSegment(sketch, "E157.4.1.3", {"start": v(-135.35, 19.74) * mm, "end": v(-130.73, 19.74) * mm});
            skLineSegment(sketch, "E157.4.2.0", {"start": v(-130.73, 11.66) * mm, "end": v(-130.73, 7.04) * mm});
            skLineSegment(sketch, "E157.4.2.1", {"start": v(-135.35, 11.66) * mm, "end": v(-130.73, 11.66) * mm});
            skLineSegment(sketch, "E157.4.2.2", {"start": v(-135.35, 11.66) * mm, "end": v(-135.35, 7.04) * mm});
            skLineSegment(sketch, "E157.4.2.3", {"start": v(-135.35, 7.04) * mm, "end": v(-130.73, 7.04) * mm});
            skLineSegment(sketch, "E157.5.0.0", {"start": v(-118.03, 37.06) * mm, "end": v(-118.03, 32.44) * mm});
            skLineSegment(sketch, "E157.5.0.1", {"start": v(-122.65, 37.06) * mm, "end": v(-118.03, 37.06) * mm});
            skLineSegment(sketch, "E157.5.0.2", {"start": v(-122.65, 37.06) * mm, "end": v(-122.65, 32.44) * mm});
            skLineSegment(sketch, "E157.5.0.3", {"start": v(-122.65, 32.44) * mm, "end": v(-118.03, 32.44) * mm});
            skLineSegment(sketch, "E157.5.1.0", {"start": v(-118.03, 24.36) * mm, "end": v(-118.03, 19.74) * mm});
            skLineSegment(sketch, "E157.5.1.1", {"start": v(-122.65, 24.36) * mm, "end": v(-118.03, 24.36) * mm});
            skLineSegment(sketch, "E157.5.1.2", {"start": v(-122.65, 24.36) * mm, "end": v(-122.65, 19.74) * mm});
            skLineSegment(sketch, "E157.5.1.3", {"start": v(-122.65, 19.74) * mm, "end": v(-118.03, 19.74) * mm});
            skLineSegment(sketch, "E157.5.2.0", {"start": v(-118.03, 11.66) * mm, "end": v(-118.03, 7.04) * mm});
            skLineSegment(sketch, "E157.5.2.1", {"start": v(-122.65, 11.66) * mm, "end": v(-118.03, 11.66) * mm});
            skLineSegment(sketch, "E157.5.2.2", {"start": v(-122.65, 11.66) * mm, "end": v(-122.65, 7.04) * mm});
            skLineSegment(sketch, "E157.5.2.3", {"start": v(-122.65, 7.04) * mm, "end": v(-118.03, 7.04) * mm});
            skLineSegment(sketch, "E157.6.0.0", {"start": v(-105.33, 37.06) * mm, "end": v(-105.33, 32.44) * mm});
            skLineSegment(sketch, "E157.6.0.1", {"start": v(-109.95, 37.06) * mm, "end": v(-105.33, 37.06) * mm});
            skLineSegment(sketch, "E157.6.0.2", {"start": v(-109.95, 37.06) * mm, "end": v(-109.95, 32.44) * mm});
            skLineSegment(sketch, "E157.6.0.3", {"start": v(-109.95, 32.44) * mm, "end": v(-105.33, 32.44) * mm});
            skLineSegment(sketch, "E157.6.1.0", {"start": v(-105.33, 24.36) * mm, "end": v(-105.33, 19.74) * mm});
            skLineSegment(sketch, "E157.6.1.1", {"start": v(-109.95, 24.36) * mm, "end": v(-105.33, 24.36) * mm});
            skLineSegment(sketch, "E157.6.1.2", {"start": v(-109.95, 24.36) * mm, "end": v(-109.95, 19.74) * mm});
            skLineSegment(sketch, "E157.6.1.3", {"start": v(-109.95, 19.74) * mm, "end": v(-105.33, 19.74) * mm});
            skLineSegment(sketch, "E157.6.2.0", {"start": v(-105.33, 11.66) * mm, "end": v(-105.33, 7.04) * mm});
            skLineSegment(sketch, "E157.6.2.1", {"start": v(-109.95, 11.66) * mm, "end": v(-105.33, 11.66) * mm});
            skLineSegment(sketch, "E157.6.2.2", {"start": v(-109.95, 11.66) * mm, "end": v(-109.95, 7.04) * mm});
            skLineSegment(sketch, "E157.6.2.3", {"start": v(-109.95, 7.04) * mm, "end": v(-105.33, 7.04) * mm});
            skLineSegment(sketch, "E157.7.0.0", {"start": v(-92.63, 37.06) * mm, "end": v(-92.63, 32.44) * mm});
            skLineSegment(sketch, "E157.7.0.1", {"start": v(-97.25, 37.06) * mm, "end": v(-92.63, 37.06) * mm});
            skLineSegment(sketch, "E157.7.0.2", {"start": v(-97.25, 37.06) * mm, "end": v(-97.25, 32.44) * mm});
            skLineSegment(sketch, "E157.7.0.3", {"start": v(-97.25, 32.44) * mm, "end": v(-92.63, 32.44) * mm});
            skLineSegment(sketch, "E157.7.1.0", {"start": v(-92.63, 24.36) * mm, "end": v(-92.63, 19.74) * mm});
            skLineSegment(sketch, "E157.7.1.1", {"start": v(-97.25, 24.36) * mm, "end": v(-92.63, 24.36) * mm});
            skLineSegment(sketch, "E157.7.1.2", {"start": v(-97.25, 24.36) * mm, "end": v(-97.25, 19.74) * mm});
            skLineSegment(sketch, "E157.7.1.3", {"start": v(-97.25, 19.74) * mm, "end": v(-92.63, 19.74) * mm});
            skLineSegment(sketch, "E157.7.2.0", {"start": v(-92.63, 11.66) * mm, "end": v(-92.63, 7.04) * mm});
            skLineSegment(sketch, "E157.7.2.1", {"start": v(-97.25, 11.66) * mm, "end": v(-92.63, 11.66) * mm});
            skLineSegment(sketch, "E157.7.2.2", {"start": v(-97.25, 11.66) * mm, "end": v(-97.25, 7.04) * mm});
            skLineSegment(sketch, "E157.7.2.3", {"start": v(-97.25, 7.04) * mm, "end": v(-92.63, 7.04) * mm});
            skLineSegment(sketch, "E157.8.0.0", {"start": v(-79.93, 37.06) * mm, "end": v(-79.93, 32.44) * mm});
            skLineSegment(sketch, "E157.8.0.1", {"start": v(-84.55, 37.06) * mm, "end": v(-79.93, 37.06) * mm});
            skLineSegment(sketch, "E157.8.0.2", {"start": v(-84.55, 37.06) * mm, "end": v(-84.55, 32.44) * mm});
            skLineSegment(sketch, "E157.8.0.3", {"start": v(-84.55, 32.44) * mm, "end": v(-79.93, 32.44) * mm});
            skLineSegment(sketch, "E157.8.1.0", {"start": v(-79.93, 24.36) * mm, "end": v(-79.93, 19.74) * mm});
            skLineSegment(sketch, "E157.8.1.1", {"start": v(-84.55, 24.36) * mm, "end": v(-79.93, 24.36) * mm});
            skLineSegment(sketch, "E157.8.1.2", {"start": v(-84.55, 24.36) * mm, "end": v(-84.55, 19.74) * mm});
            skLineSegment(sketch, "E157.8.1.3", {"start": v(-84.55, 19.74) * mm, "end": v(-79.93, 19.74) * mm});
            skLineSegment(sketch, "E157.8.2.0", {"start": v(-79.93, 11.66) * mm, "end": v(-79.93, 7.04) * mm});
            skLineSegment(sketch, "E157.8.2.1", {"start": v(-84.55, 11.66) * mm, "end": v(-79.93, 11.66) * mm});
            skLineSegment(sketch, "E157.8.2.2", {"start": v(-84.55, 11.66) * mm, "end": v(-84.55, 7.04) * mm});
            skLineSegment(sketch, "E157.8.2.3", {"start": v(-84.55, 7.04) * mm, "end": v(-79.93, 7.04) * mm});
            skLineSegment(sketch, "E157.9.0.0", {"start": v(-67.23, 37.06) * mm, "end": v(-67.23, 32.44) * mm});
            skLineSegment(sketch, "E157.9.0.1", {"start": v(-71.85, 37.06) * mm, "end": v(-67.23, 37.06) * mm});
            skLineSegment(sketch, "E157.9.0.2", {"start": v(-71.85, 37.06) * mm, "end": v(-71.85, 32.44) * mm});
            skLineSegment(sketch, "E157.9.0.3", {"start": v(-71.85, 32.44) * mm, "end": v(-67.23, 32.44) * mm});
            skLineSegment(sketch, "E157.9.1.0", {"start": v(-67.23, 24.36) * mm, "end": v(-67.23, 19.74) * mm});
            skLineSegment(sketch, "E157.9.1.1", {"start": v(-71.85, 24.36) * mm, "end": v(-67.23, 24.36) * mm});
            skLineSegment(sketch, "E157.9.1.2", {"start": v(-71.85, 24.36) * mm, "end": v(-71.85, 19.74) * mm});
            skLineSegment(sketch, "E157.9.1.3", {"start": v(-71.85, 19.74) * mm, "end": v(-67.23, 19.74) * mm});
            skLineSegment(sketch, "E157.9.2.0", {"start": v(-67.23, 11.66) * mm, "end": v(-67.23, 7.04) * mm});
            skLineSegment(sketch, "E157.9.2.1", {"start": v(-71.85, 11.66) * mm, "end": v(-67.23, 11.66) * mm});
            skLineSegment(sketch, "E157.9.2.2", {"start": v(-71.85, 11.66) * mm, "end": v(-71.85, 7.04) * mm});
            skLineSegment(sketch, "E157.9.2.3", {"start": v(-71.85, 7.04) * mm, "end": v(-67.23, 7.04) * mm});
            skLineSegment(sketch, "E157.10.0.0", {"start": v(-54.53, 37.06) * mm, "end": v(-54.53, 32.44) * mm});
            skLineSegment(sketch, "E157.10.0.1", {"start": v(-59.15, 37.06) * mm, "end": v(-54.53, 37.06) * mm});
            skLineSegment(sketch, "E157.10.0.2", {"start": v(-59.15, 37.06) * mm, "end": v(-59.15, 32.44) * mm});
            skLineSegment(sketch, "E157.10.0.3", {"start": v(-59.15, 32.44) * mm, "end": v(-54.53, 32.44) * mm});
            skLineSegment(sketch, "E157.10.1.0", {"start": v(-54.53, 24.36) * mm, "end": v(-54.53, 19.74) * mm});
            skLineSegment(sketch, "E157.10.1.1", {"start": v(-59.15, 24.36) * mm, "end": v(-54.53, 24.36) * mm});
            skLineSegment(sketch, "E157.10.1.2", {"start": v(-59.15, 24.36) * mm, "end": v(-59.15, 19.74) * mm});
            skLineSegment(sketch, "E157.10.1.3", {"start": v(-59.15, 19.74) * mm, "end": v(-54.53, 19.74) * mm});
            skLineSegment(sketch, "E157.10.2.0", {"start": v(-54.53, 11.66) * mm, "end": v(-54.53, 7.04) * mm});
            skLineSegment(sketch, "E157.10.2.1", {"start": v(-59.15, 11.66) * mm, "end": v(-54.53, 11.66) * mm});
            skLineSegment(sketch, "E157.10.2.2", {"start": v(-59.15, 11.66) * mm, "end": v(-59.15, 7.04) * mm});
            skLineSegment(sketch, "E157.10.2.3", {"start": v(-59.15, 7.04) * mm, "end": v(-54.53, 7.04) * mm});
            skLineSegment(sketch, "E157.11.0.0", {"start": v(-41.83, 37.06) * mm, "end": v(-41.83, 32.44) * mm});
            skLineSegment(sketch, "E157.11.0.1", {"start": v(-46.45, 37.06) * mm, "end": v(-41.83, 37.06) * mm});
            skLineSegment(sketch, "E157.11.0.2", {"start": v(-46.45, 37.06) * mm, "end": v(-46.45, 32.44) * mm});
            skLineSegment(sketch, "E157.11.0.3", {"start": v(-46.45, 32.44) * mm, "end": v(-41.83, 32.44) * mm});
            skLineSegment(sketch, "E157.11.1.0", {"start": v(-41.83, 24.36) * mm, "end": v(-41.83, 19.74) * mm});
            skLineSegment(sketch, "E157.11.1.1", {"start": v(-46.45, 24.36) * mm, "end": v(-41.83, 24.36) * mm});
            skLineSegment(sketch, "E157.11.1.2", {"start": v(-46.45, 24.36) * mm, "end": v(-46.45, 19.74) * mm});
            skLineSegment(sketch, "E157.11.1.3", {"start": v(-46.45, 19.74) * mm, "end": v(-41.83, 19.74) * mm});
            skLineSegment(sketch, "E157.11.2.0", {"start": v(-41.83, 11.66) * mm, "end": v(-41.83, 7.04) * mm});
            skLineSegment(sketch, "E157.11.2.1", {"start": v(-46.45, 11.66) * mm, "end": v(-41.83, 11.66) * mm});
            skLineSegment(sketch, "E157.11.2.2", {"start": v(-46.45, 11.66) * mm, "end": v(-46.45, 7.04) * mm});
            skLineSegment(sketch, "E157.11.2.3", {"start": v(-46.45, 7.04) * mm, "end": v(-41.83, 7.04) * mm});
            skLineSegment(sketch, "E157.12.0.0", {"start": v(-29.13, 37.06) * mm, "end": v(-29.13, 32.44) * mm});
            skLineSegment(sketch, "E157.12.0.1", {"start": v(-33.75, 37.06) * mm, "end": v(-29.13, 37.06) * mm});
            skLineSegment(sketch, "E157.12.0.2", {"start": v(-33.75, 37.06) * mm, "end": v(-33.75, 32.44) * mm});
            skLineSegment(sketch, "E157.12.0.3", {"start": v(-33.75, 32.44) * mm, "end": v(-29.13, 32.44) * mm});
            skLineSegment(sketch, "E157.12.1.0", {"start": v(-29.13, 24.36) * mm, "end": v(-29.13, 19.74) * mm});
            skLineSegment(sketch, "E157.12.1.1", {"start": v(-33.75, 24.36) * mm, "end": v(-29.13, 24.36) * mm});
            skLineSegment(sketch, "E157.12.1.2", {"start": v(-33.75, 24.36) * mm, "end": v(-33.75, 19.74) * mm});
            skLineSegment(sketch, "E157.12.1.3", {"start": v(-33.75, 19.74) * mm, "end": v(-29.13, 19.74) * mm});
            skLineSegment(sketch, "E157.12.2.0", {"start": v(-29.13, 11.66) * mm, "end": v(-29.13, 7.04) * mm});
            skLineSegment(sketch, "E157.12.2.1", {"start": v(-33.75, 11.66) * mm, "end": v(-29.13, 11.66) * mm});
            skLineSegment(sketch, "E157.12.2.2", {"start": v(-33.75, 11.66) * mm, "end": v(-33.75, 7.04) * mm});
            skLineSegment(sketch, "E157.12.2.3", {"start": v(-33.75, 7.04) * mm, "end": v(-29.13, 7.04) * mm});
            skLineSegment(sketch, "E157.13.0.0", {"start": v(-16.43, 37.06) * mm, "end": v(-16.43, 32.44) * mm});
            skLineSegment(sketch, "E157.13.0.1", {"start": v(-21.05, 37.06) * mm, "end": v(-16.43, 37.06) * mm});
            skLineSegment(sketch, "E157.13.0.2", {"start": v(-21.05, 37.06) * mm, "end": v(-21.05, 32.44) * mm});
            skLineSegment(sketch, "E157.13.0.3", {"start": v(-21.05, 32.44) * mm, "end": v(-16.43, 32.44) * mm});
            skLineSegment(sketch, "E157.13.1.0", {"start": v(-16.43, 24.36) * mm, "end": v(-16.43, 19.74) * mm});
            skLineSegment(sketch, "E157.13.1.1", {"start": v(-21.05, 24.36) * mm, "end": v(-16.43, 24.36) * mm});
            skLineSegment(sketch, "E157.13.1.2", {"start": v(-21.05, 24.36) * mm, "end": v(-21.05, 19.74) * mm});
            skLineSegment(sketch, "E157.13.1.3", {"start": v(-21.05, 19.74) * mm, "end": v(-16.43, 19.74) * mm});
            skLineSegment(sketch, "E157.13.2.0", {"start": v(-16.43, 11.66) * mm, "end": v(-16.43, 7.04) * mm});
            skLineSegment(sketch, "E157.13.2.1", {"start": v(-21.05, 11.66) * mm, "end": v(-16.43, 11.66) * mm});
            skLineSegment(sketch, "E157.13.2.2", {"start": v(-21.05, 11.66) * mm, "end": v(-21.05, 7.04) * mm});
            skLineSegment(sketch, "E157.13.2.3", {"start": v(-21.05, 7.04) * mm, "end": v(-16.43, 7.04) * mm});
            skLineSegment(sketch, "E157.direction1", {"start": v(-181.53, 32.44) * mm, "end": v(-168.83, 32.44) * mm, "construction": true});
            skLineSegment(sketch, "E157.direction2", {"start": v(-181.53, 32.44) * mm, "end": v(-181.53, 19.74) * mm, "construction": true});
            skPoint(sketch, "E158.visualSharp", {"position": v(-196.31, 41.1) * mm});
            skArc(sketch, "E158.filletArc", {"start": v(-189.96, 41.1) * mm, "mid": v(-194.45, 39.24) * mm, "end": v(-196.31, 34.75) * mm});
            skPoint(sketch, "E159.visualSharp", {"position": v(45.66, 41.1) * mm});
            skArc(sketch, "E159.filletArc", {"start": v(45.66, 34.75) * mm, "mid": v(43.8, 39.24) * mm, "end": v(39.31, 41.1) * mm});
            skLineSegment(sketch, "E160.0.14.0", {"start": v(-3.73, 37.06) * mm, "end": v(-3.73, 32.44) * mm});
            skLineSegment(sketch, "E160.3.14.0", {"start": v(-8.35, 37.06) * mm, "end": v(-3.73, 37.06) * mm});
            skLineSegment(sketch, "E160.6.14.0", {"start": v(-8.35, 37.06) * mm, "end": v(-8.35, 32.44) * mm});
            skLineSegment(sketch, "E160.9.14.0", {"start": v(-8.35, 32.44) * mm, "end": v(-3.73, 32.44) * mm});
            skLineSegment(sketch, "E160.0.14.1", {"start": v(-3.73, 24.36) * mm, "end": v(-3.73, 19.74) * mm});
            skLineSegment(sketch, "E160.3.14.1", {"start": v(-8.35, 24.36) * mm, "end": v(-3.73, 24.36) * mm});
            skLineSegment(sketch, "E160.6.14.1", {"start": v(-8.35, 24.36) * mm, "end": v(-8.35, 19.74) * mm});
            skLineSegment(sketch, "E160.9.14.1", {"start": v(-8.35, 19.74) * mm, "end": v(-3.73, 19.74) * mm});
            skLineSegment(sketch, "E160.0.14.2", {"start": v(-3.73, 11.66) * mm, "end": v(-3.73, 7.04) * mm});
            skLineSegment(sketch, "E160.3.14.2", {"start": v(-8.35, 11.66) * mm, "end": v(-3.73, 11.66) * mm});
            skLineSegment(sketch, "E160.6.14.2", {"start": v(-8.35, 11.66) * mm, "end": v(-8.35, 7.04) * mm});
            skLineSegment(sketch, "E160.9.14.2", {"start": v(-8.35, 7.04) * mm, "end": v(-3.73, 7.04) * mm});
            skLineSegment(sketch, "E160.0.15.0", {"start": v(8.97, 37.06) * mm, "end": v(8.97, 32.44) * mm});
            skLineSegment(sketch, "E160.3.15.0", {"start": v(4.35, 37.06) * mm, "end": v(8.97, 37.06) * mm});
            skLineSegment(sketch, "E160.6.15.0", {"start": v(4.35, 37.06) * mm, "end": v(4.35, 32.44) * mm});
            skLineSegment(sketch, "E160.9.15.0", {"start": v(4.35, 32.44) * mm, "end": v(8.97, 32.44) * mm});
            skLineSegment(sketch, "E160.0.15.1", {"start": v(8.97, 24.36) * mm, "end": v(8.97, 19.74) * mm});
            skLineSegment(sketch, "E160.3.15.1", {"start": v(4.35, 24.36) * mm, "end": v(8.97, 24.36) * mm});
            skLineSegment(sketch, "E160.6.15.1", {"start": v(4.35, 24.36) * mm, "end": v(4.35, 19.74) * mm});
            skLineSegment(sketch, "E160.9.15.1", {"start": v(4.35, 19.74) * mm, "end": v(8.97, 19.74) * mm});
            skLineSegment(sketch, "E160.0.15.2", {"start": v(8.97, 11.66) * mm, "end": v(8.97, 7.04) * mm});
            skLineSegment(sketch, "E160.3.15.2", {"start": v(4.35, 11.66) * mm, "end": v(8.97, 11.66) * mm});
            skLineSegment(sketch, "E160.6.15.2", {"start": v(4.35, 11.66) * mm, "end": v(4.35, 7.04) * mm});
            skLineSegment(sketch, "E160.9.15.2", {"start": v(4.35, 7.04) * mm, "end": v(8.97, 7.04) * mm});
            skLineSegment(sketch, "E160.0.16.0", {"start": v(21.67, 37.06) * mm, "end": v(21.67, 32.44) * mm});
            skLineSegment(sketch, "E160.3.16.0", {"start": v(17.05, 37.06) * mm, "end": v(21.67, 37.06) * mm});
            skLineSegment(sketch, "E160.6.16.0", {"start": v(17.05, 37.06) * mm, "end": v(17.05, 32.44) * mm});
            skLineSegment(sketch, "E160.9.16.0", {"start": v(17.05, 32.44) * mm, "end": v(21.67, 32.44) * mm});
            skLineSegment(sketch, "E160.0.16.1", {"start": v(21.67, 24.36) * mm, "end": v(21.67, 19.74) * mm});
            skLineSegment(sketch, "E160.3.16.1", {"start": v(17.05, 24.36) * mm, "end": v(21.67, 24.36) * mm});
            skLineSegment(sketch, "E160.6.16.1", {"start": v(17.05, 24.36) * mm, "end": v(17.05, 19.74) * mm});
            skLineSegment(sketch, "E160.9.16.1", {"start": v(17.05, 19.74) * mm, "end": v(21.67, 19.74) * mm});
            skLineSegment(sketch, "E160.0.16.2", {"start": v(21.67, 11.66) * mm, "end": v(21.67, 7.04) * mm});
            skLineSegment(sketch, "E160.3.16.2", {"start": v(17.05, 11.66) * mm, "end": v(21.67, 11.66) * mm});
            skLineSegment(sketch, "E160.6.16.2", {"start": v(17.05, 11.66) * mm, "end": v(17.05, 7.04) * mm});
            skLineSegment(sketch, "E160.9.16.2", {"start": v(17.05, 7.04) * mm, "end": v(21.67, 7.04) * mm});
            skLineSegment(sketch, "E161.0.17.0", {"start": v(34.37, 37.06) * mm, "end": v(34.37, 32.44) * mm});
            skLineSegment(sketch, "E161.3.17.0", {"start": v(29.75, 37.06) * mm, "end": v(34.37, 37.06) * mm});
            skLineSegment(sketch, "E161.6.17.0", {"start": v(29.75, 37.06) * mm, "end": v(29.75, 32.44) * mm});
            skLineSegment(sketch, "E161.9.17.0", {"start": v(29.75, 32.44) * mm, "end": v(34.37, 32.44) * mm});
            skLineSegment(sketch, "E161.0.17.1", {"start": v(34.37, 24.36) * mm, "end": v(34.37, 19.74) * mm});
            skLineSegment(sketch, "E161.3.17.1", {"start": v(29.75, 24.36) * mm, "end": v(34.37, 24.36) * mm});
            skLineSegment(sketch, "E161.6.17.1", {"start": v(29.75, 24.36) * mm, "end": v(29.75, 19.74) * mm});
            skLineSegment(sketch, "E161.9.17.1", {"start": v(29.75, 19.74) * mm, "end": v(34.37, 19.74) * mm});
            skLineSegment(sketch, "E161.0.17.2", {"start": v(34.37, 11.66) * mm, "end": v(34.37, 7.04) * mm});
            skLineSegment(sketch, "E161.3.17.2", {"start": v(29.75, 11.66) * mm, "end": v(34.37, 11.66) * mm});
            skLineSegment(sketch, "E161.6.17.2", {"start": v(29.75, 11.66) * mm, "end": v(29.75, 7.04) * mm});
            skLineSegment(sketch, "E161.9.17.2", {"start": v(29.75, 7.04) * mm, "end": v(34.37, 7.04) * mm});
            skSolve(sketch);
        }
        {
            var Q0;
            Q0 = qSketchRegion(id + "F33", true);
            extrude(context, id + "F34", {"entities" : qUnion([Q0]), "depth" : 3.8 * mm});
        }
    });
